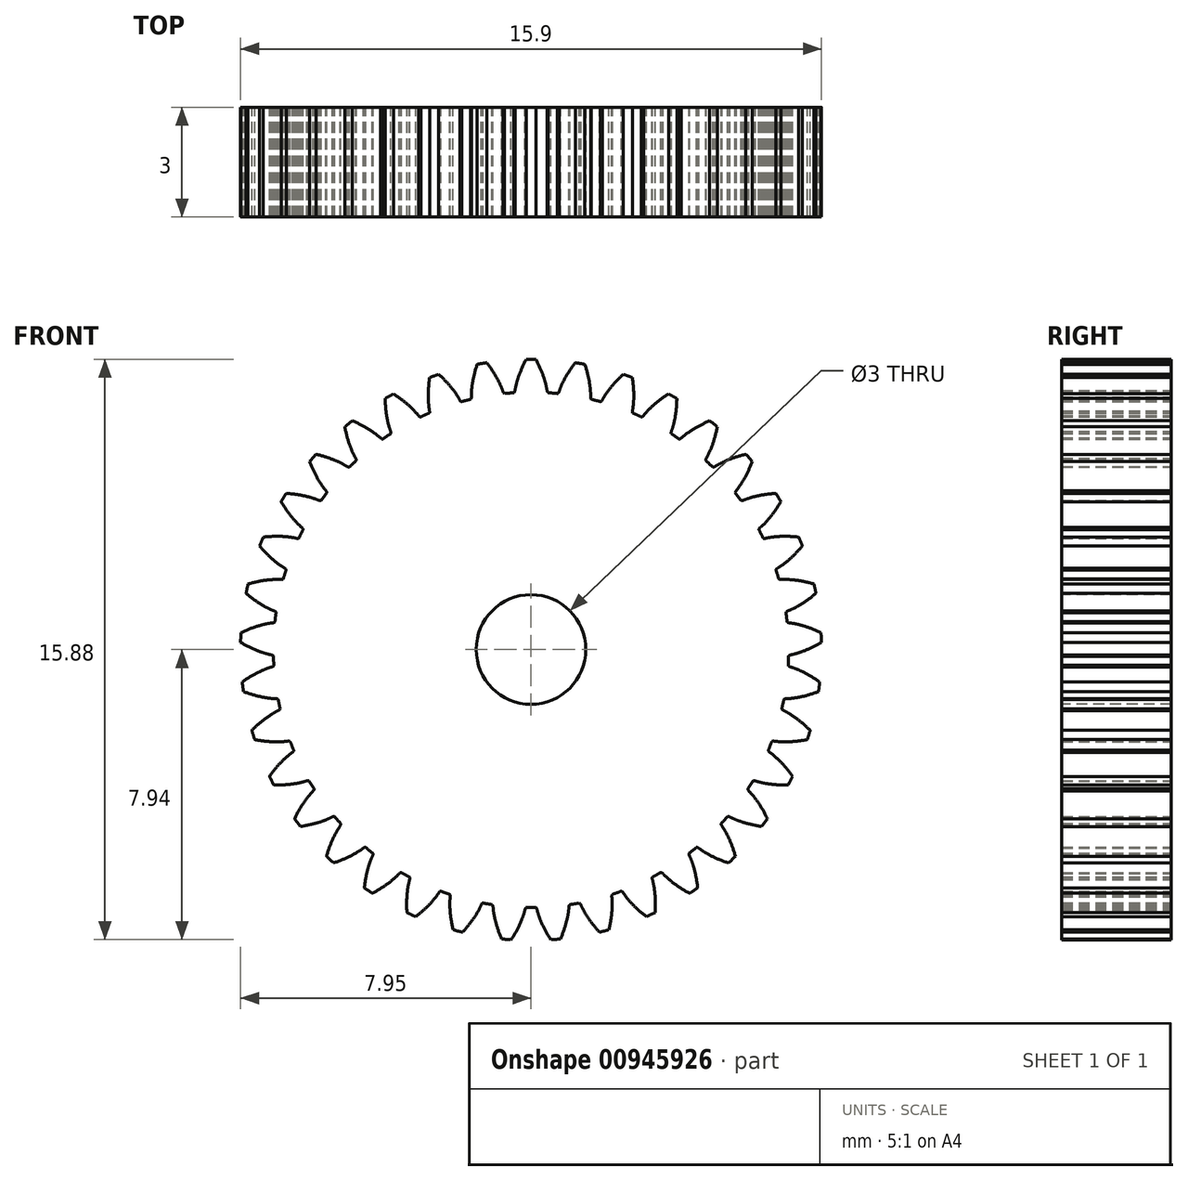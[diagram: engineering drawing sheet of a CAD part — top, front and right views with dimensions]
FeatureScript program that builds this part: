
annotation { "Feature Type Name" : "Feature", "Feature Type Description" : "" }
export const myFeature = defineFeature(function(context is Context, id is Id, definition is map)
    precondition{}
    {
        {
            var Q0;
            Q0=qCreatedBy(makeId("Front.planeOp"),FACE);
            var sketch = newSketch(context, id + "F0", { "sketchPlane" : qUnion([Q0])});
            skLineSegment(sketch, "E0", {"start": v(-0.47, 7.03) * mm, "end": v(-0.47, 7.03) * mm});
            skLineSegment(sketch, "E1", {"start": v(-0.47, 7.03) * mm, "end": v(-0.46, 7.03) * mm});
            skLineSegment(sketch, "E2", {"start": v(-0.46, 7.03) * mm, "end": v(-0.46, 7.04) * mm});
            skLineSegment(sketch, "E3", {"start": v(-0.46, 7.04) * mm, "end": v(-0.45, 7.05) * mm});
            skLineSegment(sketch, "E4", {"start": v(-0.45, 7.05) * mm, "end": v(-0.45, 7.06) * mm});
            skLineSegment(sketch, "E5", {"start": v(-0.45, 7.06) * mm, "end": v(-0.44, 7.07) * mm});
            skLineSegment(sketch, "E6", {"start": v(-0.44, 7.07) * mm, "end": v(-0.44, 7.09) * mm});
            skLineSegment(sketch, "E7", {"start": v(-0.44, 7.09) * mm, "end": v(-0.44, 7.1) * mm});
            skLineSegment(sketch, "E8", {"start": v(-0.44, 7.1) * mm, "end": v(-0.44, 7.1) * mm});
            skLineSegment(sketch, "E9", {"start": v(-0.44, 7.1) * mm, "end": v(-0.43, 7.12) * mm});
            skLineSegment(sketch, "E10", {"start": v(-0.43, 7.12) * mm, "end": v(-0.43, 7.13) * mm});
            skLineSegment(sketch, "E11", {"start": v(-0.43, 7.13) * mm, "end": v(-0.43, 7.15) * mm});
            skLineSegment(sketch, "E12", {"start": v(-0.43, 7.15) * mm, "end": v(-0.42, 7.16) * mm});
            skLineSegment(sketch, "E13", {"start": v(-0.42, 7.16) * mm, "end": v(-0.42, 7.18) * mm});
            skLineSegment(sketch, "E14", {"start": v(-0.42, 7.18) * mm, "end": v(-0.42, 7.2) * mm});
            skLineSegment(sketch, "E15", {"start": v(-0.42, 7.2) * mm, "end": v(-0.41, 7.21) * mm});
            skLineSegment(sketch, "E16", {"start": v(-0.41, 7.21) * mm, "end": v(-0.41, 7.23) * mm});
            skLineSegment(sketch, "E17", {"start": v(-0.41, 7.23) * mm, "end": v(-0.4, 7.25) * mm});
            skLineSegment(sketch, "E18", {"start": v(-0.4, 7.25) * mm, "end": v(-0.4, 7.27) * mm});
            skLineSegment(sketch, "E19", {"start": v(-0.4, 7.27) * mm, "end": v(-0.4, 7.28) * mm});
            skLineSegment(sketch, "E20", {"start": v(-0.4, 7.28) * mm, "end": v(-0.4, 7.3) * mm});
            skLineSegment(sketch, "E21", {"start": v(-0.4, 7.3) * mm, "end": v(-0.39, 7.32) * mm});
            skLineSegment(sketch, "E22", {"start": v(-0.39, 7.32) * mm, "end": v(-0.38, 7.34) * mm});
            skLineSegment(sketch, "E23", {"start": v(-0.38, 7.34) * mm, "end": v(-0.38, 7.36) * mm});
            skLineSegment(sketch, "E24", {"start": v(-0.38, 7.36) * mm, "end": v(-0.37, 7.38) * mm});
            skLineSegment(sketch, "E25", {"start": v(-0.37, 7.38) * mm, "end": v(-0.36, 7.4) * mm});
            skLineSegment(sketch, "E26", {"start": v(-0.36, 7.4) * mm, "end": v(-0.36, 7.43) * mm});
            skLineSegment(sketch, "E27", {"start": v(-0.36, 7.43) * mm, "end": v(-0.35, 7.45) * mm});
            skLineSegment(sketch, "E28", {"start": v(-0.35, 7.45) * mm, "end": v(-0.34, 7.47) * mm});
            skLineSegment(sketch, "E29", {"start": v(-0.34, 7.47) * mm, "end": v(-0.33, 7.5) * mm});
            skLineSegment(sketch, "E30", {"start": v(-0.33, 7.5) * mm, "end": v(-0.32, 7.52) * mm});
            skLineSegment(sketch, "E31", {"start": v(-0.32, 7.52) * mm, "end": v(-0.31, 7.54) * mm});
            skLineSegment(sketch, "E32", {"start": v(-0.31, 7.54) * mm, "end": v(-0.3, 7.56) * mm});
            skLineSegment(sketch, "E33", {"start": v(-0.3, 7.56) * mm, "end": v(-0.3, 7.59) * mm});
            skLineSegment(sketch, "E34", {"start": v(-0.3, 7.59) * mm, "end": v(-0.29, 7.61) * mm});
            skLineSegment(sketch, "E35", {"start": v(-0.29, 7.61) * mm, "end": v(-0.28, 7.64) * mm});
            skLineSegment(sketch, "E36", {"start": v(-0.28, 7.64) * mm, "end": v(-0.26, 7.66) * mm});
            skLineSegment(sketch, "E37", {"start": v(-0.26, 7.66) * mm, "end": v(-0.25, 7.7) * mm});
            skLineSegment(sketch, "E38", {"start": v(-0.25, 7.7) * mm, "end": v(-0.24, 7.72) * mm});
            skLineSegment(sketch, "E39", {"start": v(-0.24, 7.72) * mm, "end": v(-0.23, 7.74) * mm});
            skLineSegment(sketch, "E40", {"start": v(-0.23, 7.74) * mm, "end": v(-0.22, 7.77) * mm});
            skLineSegment(sketch, "E41", {"start": v(-0.22, 7.77) * mm, "end": v(-0.2, 7.8) * mm});
            skLineSegment(sketch, "E42", {"start": v(-0.2, 7.8) * mm, "end": v(-0.2, 7.83) * mm});
            skLineSegment(sketch, "E43", {"start": v(-0.2, 7.83) * mm, "end": v(-0.18, 7.85) * mm});
            skLineSegment(sketch, "E44", {"start": v(-0.18, 7.85) * mm, "end": v(-0.16, 7.88) * mm});
            skLineSegment(sketch, "E45", {"start": v(-0.16, 7.88) * mm, "end": v(-0.15, 7.91) * mm});
            skLineSegment(sketch, "E46", {"start": v(-0.15, 7.91) * mm, "end": v(-0.13, 7.94) * mm});
            skLineSegment(sketch, "E47", {"start": v(0.47, 7.03) * mm, "end": v(0.47, 7.03) * mm});
            skLineSegment(sketch, "E48", {"start": v(0.47, 7.03) * mm, "end": v(0.46, 7.03) * mm});
            skLineSegment(sketch, "E49", {"start": v(0.46, 7.03) * mm, "end": v(0.46, 7.04) * mm});
            skLineSegment(sketch, "E50", {"start": v(0.46, 7.04) * mm, "end": v(0.45, 7.05) * mm});
            skLineSegment(sketch, "E51", {"start": v(0.45, 7.05) * mm, "end": v(0.45, 7.06) * mm});
            skLineSegment(sketch, "E52", {"start": v(0.45, 7.06) * mm, "end": v(0.44, 7.07) * mm});
            skLineSegment(sketch, "E53", {"start": v(0.44, 7.07) * mm, "end": v(0.44, 7.09) * mm});
            skLineSegment(sketch, "E54", {"start": v(0.44, 7.09) * mm, "end": v(0.44, 7.1) * mm});
            skLineSegment(sketch, "E55", {"start": v(0.44, 7.1) * mm, "end": v(0.44, 7.1) * mm});
            skLineSegment(sketch, "E56", {"start": v(0.44, 7.1) * mm, "end": v(0.43, 7.12) * mm});
            skLineSegment(sketch, "E57", {"start": v(0.43, 7.12) * mm, "end": v(0.43, 7.13) * mm});
            skLineSegment(sketch, "E58", {"start": v(0.43, 7.13) * mm, "end": v(0.43, 7.15) * mm});
            skLineSegment(sketch, "E59", {"start": v(0.43, 7.15) * mm, "end": v(0.42, 7.16) * mm});
            skLineSegment(sketch, "E60", {"start": v(0.42, 7.16) * mm, "end": v(0.42, 7.18) * mm});
            skLineSegment(sketch, "E61", {"start": v(0.42, 7.18) * mm, "end": v(0.42, 7.2) * mm});
            skLineSegment(sketch, "E62", {"start": v(0.42, 7.2) * mm, "end": v(0.41, 7.21) * mm});
            skLineSegment(sketch, "E63", {"start": v(0.41, 7.21) * mm, "end": v(0.41, 7.23) * mm});
            skLineSegment(sketch, "E64", {"start": v(0.41, 7.23) * mm, "end": v(0.4, 7.25) * mm});
            skLineSegment(sketch, "E65", {"start": v(0.4, 7.25) * mm, "end": v(0.4, 7.27) * mm});
            skLineSegment(sketch, "E66", {"start": v(0.4, 7.27) * mm, "end": v(0.4, 7.28) * mm});
            skLineSegment(sketch, "E67", {"start": v(0.4, 7.28) * mm, "end": v(0.4, 7.3) * mm});
            skLineSegment(sketch, "E68", {"start": v(0.4, 7.3) * mm, "end": v(0.39, 7.32) * mm});
            skLineSegment(sketch, "E69", {"start": v(0.39, 7.32) * mm, "end": v(0.38, 7.34) * mm});
            skLineSegment(sketch, "E70", {"start": v(0.38, 7.34) * mm, "end": v(0.38, 7.36) * mm});
            skLineSegment(sketch, "E71", {"start": v(0.38, 7.36) * mm, "end": v(0.37, 7.38) * mm});
            skLineSegment(sketch, "E72", {"start": v(0.37, 7.38) * mm, "end": v(0.36, 7.4) * mm});
            skLineSegment(sketch, "E73", {"start": v(0.36, 7.4) * mm, "end": v(0.36, 7.43) * mm});
            skLineSegment(sketch, "E74", {"start": v(0.36, 7.43) * mm, "end": v(0.35, 7.45) * mm});
            skLineSegment(sketch, "E75", {"start": v(0.35, 7.45) * mm, "end": v(0.34, 7.47) * mm});
            skLineSegment(sketch, "E76", {"start": v(0.34, 7.47) * mm, "end": v(0.33, 7.5) * mm});
            skLineSegment(sketch, "E77", {"start": v(0.33, 7.5) * mm, "end": v(0.32, 7.52) * mm});
            skLineSegment(sketch, "E78", {"start": v(0.32, 7.52) * mm, "end": v(0.31, 7.54) * mm});
            skLineSegment(sketch, "E79", {"start": v(0.31, 7.54) * mm, "end": v(0.3, 7.56) * mm});
            skLineSegment(sketch, "E80", {"start": v(0.3, 7.56) * mm, "end": v(0.3, 7.59) * mm});
            skLineSegment(sketch, "E81", {"start": v(0.3, 7.59) * mm, "end": v(0.29, 7.61) * mm});
            skLineSegment(sketch, "E82", {"start": v(0.29, 7.61) * mm, "end": v(0.28, 7.64) * mm});
            skLineSegment(sketch, "E83", {"start": v(0.28, 7.64) * mm, "end": v(0.26, 7.66) * mm});
            skLineSegment(sketch, "E84", {"start": v(0.26, 7.66) * mm, "end": v(0.25, 7.7) * mm});
            skLineSegment(sketch, "E85", {"start": v(0.25, 7.7) * mm, "end": v(0.24, 7.72) * mm});
            skLineSegment(sketch, "E86", {"start": v(0.24, 7.72) * mm, "end": v(0.23, 7.74) * mm});
            skLineSegment(sketch, "E87", {"start": v(0.23, 7.74) * mm, "end": v(0.22, 7.77) * mm});
            skLineSegment(sketch, "E88", {"start": v(0.22, 7.77) * mm, "end": v(0.2, 7.8) * mm});
            skLineSegment(sketch, "E89", {"start": v(0.2, 7.8) * mm, "end": v(0.2, 7.83) * mm});
            skLineSegment(sketch, "E90", {"start": v(0.2, 7.83) * mm, "end": v(0.18, 7.85) * mm});
            skLineSegment(sketch, "E91", {"start": v(0.18, 7.85) * mm, "end": v(0.16, 7.88) * mm});
            skLineSegment(sketch, "E92", {"start": v(0.16, 7.88) * mm, "end": v(0.15, 7.91) * mm});
            skLineSegment(sketch, "E93", {"start": v(0.15, 7.91) * mm, "end": v(0.13, 7.94) * mm});
            skArc(sketch, "E94", {"start": v(0.13, 7.94) * mm, "mid": v(0, 7.94) * mm, "end": v(-0.13, 7.94) * mm});
            skLineSegment(sketch, "E95", {"start": v(0.72, 7) * mm, "end": v(0.73, 7) * mm});
            skLineSegment(sketch, "E96", {"start": v(0.73, 7) * mm, "end": v(0.74, 7) * mm});
            skLineSegment(sketch, "E97", {"start": v(0.74, 7) * mm, "end": v(0.74, 7.01) * mm});
            skLineSegment(sketch, "E98", {"start": v(0.74, 7.01) * mm, "end": v(0.75, 7.02) * mm});
            skLineSegment(sketch, "E99", {"start": v(0.75, 7.02) * mm, "end": v(0.76, 7.03) * mm});
            skLineSegment(sketch, "E100", {"start": v(0.76, 7.03) * mm, "end": v(0.76, 7.04) * mm});
            skLineSegment(sketch, "E101", {"start": v(0.76, 7.04) * mm, "end": v(0.77, 7.06) * mm});
            skLineSegment(sketch, "E102", {"start": v(0.77, 7.06) * mm, "end": v(0.77, 7.07) * mm});
            skLineSegment(sketch, "E103", {"start": v(0.77, 7.07) * mm, "end": v(0.77, 7.08) * mm});
            skLineSegment(sketch, "E104", {"start": v(0.77, 7.08) * mm, "end": v(0.78, 7.1) * mm});
            skLineSegment(sketch, "E105", {"start": v(0.78, 7.1) * mm, "end": v(0.78, 7.1) * mm});
            skLineSegment(sketch, "E106", {"start": v(0.78, 7.1) * mm, "end": v(0.79, 7.12) * mm});
            skLineSegment(sketch, "E107", {"start": v(0.79, 7.12) * mm, "end": v(0.8, 7.13) * mm});
            skLineSegment(sketch, "E108", {"start": v(0.8, 7.13) * mm, "end": v(0.8, 7.15) * mm});
            skLineSegment(sketch, "E109", {"start": v(0.8, 7.15) * mm, "end": v(0.8, 7.16) * mm});
            skLineSegment(sketch, "E110", {"start": v(0.8, 7.16) * mm, "end": v(0.81, 7.18) * mm});
            skLineSegment(sketch, "E111", {"start": v(0.81, 7.18) * mm, "end": v(0.82, 7.2) * mm});
            skLineSegment(sketch, "E112", {"start": v(0.82, 7.2) * mm, "end": v(0.83, 7.21) * mm});
            skLineSegment(sketch, "E113", {"start": v(0.83, 7.21) * mm, "end": v(0.83, 7.23) * mm});
            skLineSegment(sketch, "E114", {"start": v(0.83, 7.23) * mm, "end": v(0.84, 7.25) * mm});
            skLineSegment(sketch, "E115", {"start": v(0.84, 7.25) * mm, "end": v(0.85, 7.26) * mm});
            skLineSegment(sketch, "E116", {"start": v(0.85, 7.26) * mm, "end": v(0.86, 7.28) * mm});
            skLineSegment(sketch, "E117", {"start": v(0.86, 7.28) * mm, "end": v(0.87, 7.3) * mm});
            skLineSegment(sketch, "E118", {"start": v(0.87, 7.3) * mm, "end": v(0.88, 7.32) * mm});
            skLineSegment(sketch, "E119", {"start": v(0.88, 7.32) * mm, "end": v(0.89, 7.34) * mm});
            skLineSegment(sketch, "E120", {"start": v(0.89, 7.34) * mm, "end": v(0.9, 7.36) * mm});
            skLineSegment(sketch, "E121", {"start": v(0.9, 7.36) * mm, "end": v(0.9, 7.38) * mm});
            skLineSegment(sketch, "E122", {"start": v(0.9, 7.38) * mm, "end": v(0.92, 7.4) * mm});
            skLineSegment(sketch, "E123", {"start": v(0.92, 7.4) * mm, "end": v(0.93, 7.42) * mm});
            skLineSegment(sketch, "E124", {"start": v(0.93, 7.42) * mm, "end": v(0.94, 7.44) * mm});
            skLineSegment(sketch, "E125", {"start": v(0.94, 7.44) * mm, "end": v(0.95, 7.46) * mm});
            skLineSegment(sketch, "E126", {"start": v(0.95, 7.46) * mm, "end": v(0.97, 7.48) * mm});
            skLineSegment(sketch, "E127", {"start": v(0.97, 7.48) * mm, "end": v(0.98, 7.5) * mm});
            skLineSegment(sketch, "E128", {"start": v(0.98, 7.5) * mm, "end": v(1, 7.53) * mm});
            skLineSegment(sketch, "E129", {"start": v(1, 7.53) * mm, "end": v(1, 7.55) * mm});
            skLineSegment(sketch, "E130", {"start": v(1, 7.55) * mm, "end": v(1.02, 7.58) * mm});
            skLineSegment(sketch, "E131", {"start": v(1.02, 7.58) * mm, "end": v(1.04, 7.6) * mm});
            skLineSegment(sketch, "E132", {"start": v(1.04, 7.6) * mm, "end": v(1.05, 7.62) * mm});
            skLineSegment(sketch, "E133", {"start": v(1.05, 7.62) * mm, "end": v(1.07, 7.65) * mm});
            skLineSegment(sketch, "E134", {"start": v(1.07, 7.65) * mm, "end": v(1.08, 7.67) * mm});
            skLineSegment(sketch, "E135", {"start": v(1.08, 7.67) * mm, "end": v(1.1, 7.7) * mm});
            skLineSegment(sketch, "E136", {"start": v(1.1, 7.7) * mm, "end": v(1.12, 7.72) * mm});
            skLineSegment(sketch, "E137", {"start": v(1.12, 7.72) * mm, "end": v(1.14, 7.75) * mm});
            skLineSegment(sketch, "E138", {"start": v(1.14, 7.75) * mm, "end": v(1.15, 7.77) * mm});
            skLineSegment(sketch, "E139", {"start": v(1.15, 7.77) * mm, "end": v(1.17, 7.8) * mm});
            skLineSegment(sketch, "E140", {"start": v(1.17, 7.8) * mm, "end": v(1.2, 7.82) * mm});
            skLineSegment(sketch, "E141", {"start": v(1.2, 7.82) * mm, "end": v(1.21, 7.85) * mm});
            skLineSegment(sketch, "E142", {"start": v(1.65, 6.85) * mm, "end": v(1.65, 6.85) * mm});
            skLineSegment(sketch, "E143", {"start": v(1.65, 6.85) * mm, "end": v(1.64, 6.85) * mm});
            skLineSegment(sketch, "E144", {"start": v(1.64, 6.85) * mm, "end": v(1.64, 6.86) * mm});
            skLineSegment(sketch, "E145", {"start": v(1.64, 6.86) * mm, "end": v(1.64, 6.87) * mm});
            skLineSegment(sketch, "E146", {"start": v(1.64, 6.87) * mm, "end": v(1.63, 6.88) * mm});
            skLineSegment(sketch, "E147", {"start": v(1.63, 6.88) * mm, "end": v(1.63, 6.9) * mm});
            skLineSegment(sketch, "E148", {"start": v(1.63, 6.9) * mm, "end": v(1.63, 6.91) * mm});
            skLineSegment(sketch, "E149", {"start": v(1.63, 6.91) * mm, "end": v(1.63, 6.92) * mm});
            skLineSegment(sketch, "E150", {"start": v(1.63, 6.92) * mm, "end": v(1.63, 6.93) * mm});
            skLineSegment(sketch, "E151", {"start": v(1.63, 6.93) * mm, "end": v(1.63, 6.94) * mm});
            skLineSegment(sketch, "E152", {"start": v(1.63, 6.94) * mm, "end": v(1.63, 6.96) * mm});
            skLineSegment(sketch, "E153", {"start": v(1.63, 6.96) * mm, "end": v(1.63, 6.97) * mm});
            skLineSegment(sketch, "E154", {"start": v(1.63, 6.97) * mm, "end": v(1.63, 6.99) * mm});
            skLineSegment(sketch, "E155", {"start": v(1.63, 6.99) * mm, "end": v(1.63, 7) * mm});
            skLineSegment(sketch, "E156", {"start": v(1.63, 7) * mm, "end": v(1.63, 7.02) * mm});
            skLineSegment(sketch, "E157", {"start": v(1.63, 7.02) * mm, "end": v(1.63, 7.04) * mm});
            skLineSegment(sketch, "E158", {"start": v(1.63, 7.04) * mm, "end": v(1.63, 7.06) * mm});
            skLineSegment(sketch, "E159", {"start": v(1.63, 7.06) * mm, "end": v(1.63, 7.07) * mm});
            skLineSegment(sketch, "E160", {"start": v(1.63, 7.07) * mm, "end": v(1.63, 7.1) * mm});
            skLineSegment(sketch, "E161", {"start": v(1.63, 7.1) * mm, "end": v(1.62, 7.11) * mm});
            skLineSegment(sketch, "E162", {"start": v(1.62, 7.11) * mm, "end": v(1.62, 7.13) * mm});
            skLineSegment(sketch, "E163", {"start": v(1.62, 7.13) * mm, "end": v(1.62, 7.15) * mm});
            skLineSegment(sketch, "E164", {"start": v(1.62, 7.15) * mm, "end": v(1.62, 7.17) * mm});
            skLineSegment(sketch, "E165", {"start": v(1.62, 7.17) * mm, "end": v(1.62, 7.2) * mm});
            skLineSegment(sketch, "E166", {"start": v(1.62, 7.2) * mm, "end": v(1.61, 7.21) * mm});
            skLineSegment(sketch, "E167", {"start": v(1.61, 7.21) * mm, "end": v(1.6, 7.24) * mm});
            skLineSegment(sketch, "E168", {"start": v(1.6, 7.24) * mm, "end": v(1.6, 7.26) * mm});
            skLineSegment(sketch, "E169", {"start": v(1.6, 7.26) * mm, "end": v(1.6, 7.28) * mm});
            skLineSegment(sketch, "E170", {"start": v(1.6, 7.28) * mm, "end": v(1.6, 7.3) * mm});
            skLineSegment(sketch, "E171", {"start": v(1.6, 7.3) * mm, "end": v(1.6, 7.33) * mm});
            skLineSegment(sketch, "E172", {"start": v(1.6, 7.33) * mm, "end": v(1.6, 7.35) * mm});
            skLineSegment(sketch, "E173", {"start": v(1.6, 7.35) * mm, "end": v(1.59, 7.38) * mm});
            skLineSegment(sketch, "E174", {"start": v(1.59, 7.38) * mm, "end": v(1.58, 7.4) * mm});
            skLineSegment(sketch, "E175", {"start": v(1.58, 7.4) * mm, "end": v(1.58, 7.43) * mm});
            skLineSegment(sketch, "E176", {"start": v(1.58, 7.43) * mm, "end": v(1.57, 7.46) * mm});
            skLineSegment(sketch, "E177", {"start": v(1.57, 7.46) * mm, "end": v(1.56, 7.48) * mm});
            skLineSegment(sketch, "E178", {"start": v(1.56, 7.48) * mm, "end": v(1.56, 7.5) * mm});
            skLineSegment(sketch, "E179", {"start": v(1.56, 7.5) * mm, "end": v(1.55, 7.54) * mm});
            skLineSegment(sketch, "E180", {"start": v(1.55, 7.54) * mm, "end": v(1.54, 7.57) * mm});
            skLineSegment(sketch, "E181", {"start": v(1.54, 7.57) * mm, "end": v(1.54, 7.6) * mm});
            skLineSegment(sketch, "E182", {"start": v(1.54, 7.6) * mm, "end": v(1.53, 7.62) * mm});
            skLineSegment(sketch, "E183", {"start": v(1.53, 7.62) * mm, "end": v(1.52, 7.65) * mm});
            skLineSegment(sketch, "E184", {"start": v(1.52, 7.65) * mm, "end": v(1.51, 7.68) * mm});
            skLineSegment(sketch, "E185", {"start": v(1.51, 7.68) * mm, "end": v(1.5, 7.71) * mm});
            skLineSegment(sketch, "E186", {"start": v(1.5, 7.71) * mm, "end": v(1.5, 7.74) * mm});
            skLineSegment(sketch, "E187", {"start": v(1.5, 7.74) * mm, "end": v(1.48, 7.77) * mm});
            skLineSegment(sketch, "E188", {"start": v(1.48, 7.77) * mm, "end": v(1.47, 7.8) * mm});
            skArc(sketch, "E189", {"start": v(1.47, 7.8) * mm, "mid": v(1.34, 7.83) * mm, "end": v(1.21, 7.85) * mm});
            skLineSegment(sketch, "E190", {"start": v(1.9, 6.78) * mm, "end": v(1.9, 6.78) * mm});
            skLineSegment(sketch, "E191", {"start": v(1.9, 6.78) * mm, "end": v(1.91, 6.78) * mm});
            skLineSegment(sketch, "E192", {"start": v(1.91, 6.78) * mm, "end": v(1.92, 6.79) * mm});
            skLineSegment(sketch, "E193", {"start": v(1.92, 6.79) * mm, "end": v(1.93, 6.8) * mm});
            skLineSegment(sketch, "E194", {"start": v(1.93, 6.8) * mm, "end": v(1.93, 6.8) * mm});
            skLineSegment(sketch, "E195", {"start": v(1.93, 6.8) * mm, "end": v(1.94, 6.81) * mm});
            skLineSegment(sketch, "E196", {"start": v(1.94, 6.81) * mm, "end": v(1.95, 6.83) * mm});
            skLineSegment(sketch, "E197", {"start": v(1.95, 6.83) * mm, "end": v(1.95, 6.83) * mm});
            skLineSegment(sketch, "E198", {"start": v(1.95, 6.83) * mm, "end": v(1.96, 6.85) * mm});
            skLineSegment(sketch, "E199", {"start": v(1.96, 6.85) * mm, "end": v(1.97, 6.86) * mm});
            skLineSegment(sketch, "E200", {"start": v(1.97, 6.86) * mm, "end": v(1.97, 6.87) * mm});
            skLineSegment(sketch, "E201", {"start": v(1.97, 6.87) * mm, "end": v(1.98, 6.88) * mm});
            skLineSegment(sketch, "E202", {"start": v(1.98, 6.88) * mm, "end": v(1.99, 6.9) * mm});
            skLineSegment(sketch, "E203", {"start": v(1.99, 6.9) * mm, "end": v(2, 6.9) * mm});
            skLineSegment(sketch, "E204", {"start": v(2, 6.9) * mm, "end": v(2, 6.92) * mm});
            skLineSegment(sketch, "E205", {"start": v(2, 6.92) * mm, "end": v(2.02, 6.94) * mm});
            skLineSegment(sketch, "E206", {"start": v(2.02, 6.94) * mm, "end": v(2.02, 6.95) * mm});
            skLineSegment(sketch, "E207", {"start": v(2.02, 6.95) * mm, "end": v(2.03, 6.97) * mm});
            skLineSegment(sketch, "E208", {"start": v(2.03, 6.97) * mm, "end": v(2.04, 6.98) * mm});
            skLineSegment(sketch, "E209", {"start": v(2.04, 6.98) * mm, "end": v(2.06, 7) * mm});
            skLineSegment(sketch, "E210", {"start": v(2.06, 7) * mm, "end": v(2.07, 7.02) * mm});
            skLineSegment(sketch, "E211", {"start": v(2.07, 7.02) * mm, "end": v(2.08, 7.03) * mm});
            skLineSegment(sketch, "E212", {"start": v(2.08, 7.03) * mm, "end": v(2.09, 7.05) * mm});
            skLineSegment(sketch, "E213", {"start": v(2.09, 7.05) * mm, "end": v(2.1, 7.07) * mm});
            skLineSegment(sketch, "E214", {"start": v(2.1, 7.07) * mm, "end": v(2.11, 7.08) * mm});
            skLineSegment(sketch, "E215", {"start": v(2.11, 7.08) * mm, "end": v(2.13, 7.1) * mm});
            skLineSegment(sketch, "E216", {"start": v(2.13, 7.1) * mm, "end": v(2.14, 7.12) * mm});
            skLineSegment(sketch, "E217", {"start": v(2.14, 7.12) * mm, "end": v(2.16, 7.14) * mm});
            skLineSegment(sketch, "E218", {"start": v(2.16, 7.14) * mm, "end": v(2.17, 7.16) * mm});
            skLineSegment(sketch, "E219", {"start": v(2.17, 7.16) * mm, "end": v(2.19, 7.18) * mm});
            skLineSegment(sketch, "E220", {"start": v(2.19, 7.18) * mm, "end": v(2.2, 7.2) * mm});
            skLineSegment(sketch, "E221", {"start": v(2.2, 7.2) * mm, "end": v(2.22, 7.21) * mm});
            skLineSegment(sketch, "E222", {"start": v(2.22, 7.21) * mm, "end": v(2.23, 7.23) * mm});
            skLineSegment(sketch, "E223", {"start": v(2.23, 7.23) * mm, "end": v(2.25, 7.25) * mm});
            skLineSegment(sketch, "E224", {"start": v(2.25, 7.25) * mm, "end": v(2.27, 7.27) * mm});
            skLineSegment(sketch, "E225", {"start": v(2.27, 7.27) * mm, "end": v(2.29, 7.3) * mm});
            skLineSegment(sketch, "E226", {"start": v(2.29, 7.3) * mm, "end": v(2.3, 7.31) * mm});
            skLineSegment(sketch, "E227", {"start": v(2.3, 7.31) * mm, "end": v(2.33, 7.34) * mm});
            skLineSegment(sketch, "E228", {"start": v(2.33, 7.34) * mm, "end": v(2.35, 7.36) * mm});
            skLineSegment(sketch, "E229", {"start": v(2.35, 7.36) * mm, "end": v(2.37, 7.38) * mm});
            skLineSegment(sketch, "E230", {"start": v(2.37, 7.38) * mm, "end": v(2.39, 7.4) * mm});
            skLineSegment(sketch, "E231", {"start": v(2.39, 7.4) * mm, "end": v(2.4, 7.42) * mm});
            skLineSegment(sketch, "E232", {"start": v(2.4, 7.42) * mm, "end": v(2.43, 7.44) * mm});
            skLineSegment(sketch, "E233", {"start": v(2.43, 7.44) * mm, "end": v(2.45, 7.46) * mm});
            skLineSegment(sketch, "E234", {"start": v(2.45, 7.46) * mm, "end": v(2.48, 7.49) * mm});
            skLineSegment(sketch, "E235", {"start": v(2.48, 7.49) * mm, "end": v(2.5, 7.5) * mm});
            skLineSegment(sketch, "E236", {"start": v(2.5, 7.5) * mm, "end": v(2.52, 7.53) * mm});
            skLineSegment(sketch, "E237", {"start": v(2.79, 6.47) * mm, "end": v(2.78, 6.47) * mm});
            skLineSegment(sketch, "E238", {"start": v(2.78, 6.47) * mm, "end": v(2.78, 6.48) * mm});
            skLineSegment(sketch, "E239", {"start": v(2.78, 6.48) * mm, "end": v(2.78, 6.48) * mm});
            skLineSegment(sketch, "E240", {"start": v(2.78, 6.48) * mm, "end": v(2.78, 6.5) * mm});
            skLineSegment(sketch, "E241", {"start": v(2.78, 6.5) * mm, "end": v(2.77, 6.5) * mm});
            skLineSegment(sketch, "E242", {"start": v(2.77, 6.5) * mm, "end": v(2.78, 6.52) * mm});
            skLineSegment(sketch, "E243", {"start": v(2.78, 6.52) * mm, "end": v(2.78, 6.54) * mm});
            skLineSegment(sketch, "E244", {"start": v(2.78, 6.54) * mm, "end": v(2.78, 6.54) * mm});
            skLineSegment(sketch, "E245", {"start": v(2.78, 6.54) * mm, "end": v(2.78, 6.56) * mm});
            skLineSegment(sketch, "E246", {"start": v(2.78, 6.56) * mm, "end": v(2.78, 6.57) * mm});
            skLineSegment(sketch, "E247", {"start": v(2.78, 6.57) * mm, "end": v(2.79, 6.58) * mm});
            skLineSegment(sketch, "E248", {"start": v(2.79, 6.58) * mm, "end": v(2.79, 6.6) * mm});
            skLineSegment(sketch, "E249", {"start": v(2.79, 6.6) * mm, "end": v(2.8, 6.61) * mm});
            skLineSegment(sketch, "E250", {"start": v(2.8, 6.61) * mm, "end": v(2.8, 6.63) * mm});
            skLineSegment(sketch, "E251", {"start": v(2.8, 6.63) * mm, "end": v(2.8, 6.65) * mm});
            skLineSegment(sketch, "E252", {"start": v(2.8, 6.65) * mm, "end": v(2.8, 6.66) * mm});
            skLineSegment(sketch, "E253", {"start": v(2.8, 6.66) * mm, "end": v(2.8, 6.68) * mm});
            skLineSegment(sketch, "E254", {"start": v(2.8, 6.68) * mm, "end": v(2.8, 6.7) * mm});
            skLineSegment(sketch, "E255", {"start": v(2.8, 6.7) * mm, "end": v(2.8, 6.72) * mm});
            skLineSegment(sketch, "E256", {"start": v(2.8, 6.72) * mm, "end": v(2.8, 6.73) * mm});
            skLineSegment(sketch, "E257", {"start": v(2.8, 6.73) * mm, "end": v(2.8, 6.75) * mm});
            skLineSegment(sketch, "E258", {"start": v(2.8, 6.75) * mm, "end": v(2.8, 6.77) * mm});
            skLineSegment(sketch, "E259", {"start": v(2.8, 6.77) * mm, "end": v(2.8, 6.8) * mm});
            skLineSegment(sketch, "E260", {"start": v(2.8, 6.8) * mm, "end": v(2.8, 6.82) * mm});
            skLineSegment(sketch, "E261", {"start": v(2.8, 6.82) * mm, "end": v(2.81, 6.84) * mm});
            skLineSegment(sketch, "E262", {"start": v(2.81, 6.84) * mm, "end": v(2.81, 6.86) * mm});
            skLineSegment(sketch, "E263", {"start": v(2.81, 6.86) * mm, "end": v(2.81, 6.88) * mm});
            skLineSegment(sketch, "E264", {"start": v(2.81, 6.88) * mm, "end": v(2.81, 6.9) * mm});
            skLineSegment(sketch, "E265", {"start": v(2.81, 6.9) * mm, "end": v(2.81, 6.93) * mm});
            skLineSegment(sketch, "E266", {"start": v(2.81, 6.93) * mm, "end": v(2.81, 6.95) * mm});
            skLineSegment(sketch, "E267", {"start": v(2.81, 6.95) * mm, "end": v(2.81, 6.98) * mm});
            skLineSegment(sketch, "E268", {"start": v(2.81, 6.98) * mm, "end": v(2.81, 7) * mm});
            skLineSegment(sketch, "E269", {"start": v(2.81, 7) * mm, "end": v(2.81, 7.03) * mm});
            skLineSegment(sketch, "E270", {"start": v(2.81, 7.03) * mm, "end": v(2.81, 7.06) * mm});
            skLineSegment(sketch, "E271", {"start": v(2.81, 7.06) * mm, "end": v(2.8, 7.08) * mm});
            skLineSegment(sketch, "E272", {"start": v(2.8, 7.08) * mm, "end": v(2.8, 7.11) * mm});
            skLineSegment(sketch, "E273", {"start": v(2.8, 7.11) * mm, "end": v(2.8, 7.14) * mm});
            skLineSegment(sketch, "E274", {"start": v(2.8, 7.14) * mm, "end": v(2.8, 7.17) * mm});
            skLineSegment(sketch, "E275", {"start": v(2.8, 7.17) * mm, "end": v(2.8, 7.2) * mm});
            skLineSegment(sketch, "E276", {"start": v(2.8, 7.2) * mm, "end": v(2.8, 7.22) * mm});
            skLineSegment(sketch, "E277", {"start": v(2.8, 7.22) * mm, "end": v(2.8, 7.25) * mm});
            skLineSegment(sketch, "E278", {"start": v(2.8, 7.25) * mm, "end": v(2.8, 7.28) * mm});
            skLineSegment(sketch, "E279", {"start": v(2.8, 7.28) * mm, "end": v(2.8, 7.32) * mm});
            skLineSegment(sketch, "E280", {"start": v(2.8, 7.32) * mm, "end": v(2.79, 7.35) * mm});
            skLineSegment(sketch, "E281", {"start": v(2.79, 7.35) * mm, "end": v(2.78, 7.38) * mm});
            skLineSegment(sketch, "E282", {"start": v(2.78, 7.38) * mm, "end": v(2.78, 7.41) * mm});
            skLineSegment(sketch, "E283", {"start": v(2.78, 7.41) * mm, "end": v(2.77, 7.44) * mm});
            skArc(sketch, "E284", {"start": v(2.77, 7.44) * mm, "mid": v(2.65, 7.49) * mm, "end": v(2.52, 7.53) * mm});
            skLineSegment(sketch, "E285", {"start": v(3.02, 6.36) * mm, "end": v(3.03, 6.36) * mm});
            skLineSegment(sketch, "E286", {"start": v(3.03, 6.36) * mm, "end": v(3.03, 6.36) * mm});
            skLineSegment(sketch, "E287", {"start": v(3.03, 6.36) * mm, "end": v(3.04, 6.37) * mm});
            skLineSegment(sketch, "E288", {"start": v(3.04, 6.37) * mm, "end": v(3.05, 6.37) * mm});
            skLineSegment(sketch, "E289", {"start": v(3.05, 6.37) * mm, "end": v(3.06, 6.38) * mm});
            skLineSegment(sketch, "E290", {"start": v(3.06, 6.38) * mm, "end": v(3.07, 6.39) * mm});
            skLineSegment(sketch, "E291", {"start": v(3.07, 6.39) * mm, "end": v(3.08, 6.4) * mm});
            skLineSegment(sketch, "E292", {"start": v(3.08, 6.4) * mm, "end": v(3.08, 6.4) * mm});
            skLineSegment(sketch, "E293", {"start": v(3.08, 6.4) * mm, "end": v(3.1, 6.42) * mm});
            skLineSegment(sketch, "E294", {"start": v(3.1, 6.42) * mm, "end": v(3.1, 6.43) * mm});
            skLineSegment(sketch, "E295", {"start": v(3.1, 6.43) * mm, "end": v(3.1, 6.44) * mm});
            skLineSegment(sketch, "E296", {"start": v(3.1, 6.44) * mm, "end": v(3.12, 6.45) * mm});
            skLineSegment(sketch, "E297", {"start": v(3.12, 6.45) * mm, "end": v(3.13, 6.46) * mm});
            skLineSegment(sketch, "E298", {"start": v(3.13, 6.46) * mm, "end": v(3.14, 6.47) * mm});
            skLineSegment(sketch, "E299", {"start": v(3.14, 6.47) * mm, "end": v(3.15, 6.49) * mm});
            skLineSegment(sketch, "E300", {"start": v(3.15, 6.49) * mm, "end": v(3.16, 6.5) * mm});
            skLineSegment(sketch, "E301", {"start": v(3.16, 6.5) * mm, "end": v(3.17, 6.51) * mm});
            skLineSegment(sketch, "E302", {"start": v(3.17, 6.51) * mm, "end": v(3.18, 6.52) * mm});
            skLineSegment(sketch, "E303", {"start": v(3.18, 6.52) * mm, "end": v(3.2, 6.54) * mm});
            skLineSegment(sketch, "E304", {"start": v(3.2, 6.54) * mm, "end": v(3.21, 6.55) * mm});
            skLineSegment(sketch, "E305", {"start": v(3.21, 6.55) * mm, "end": v(3.22, 6.57) * mm});
            skLineSegment(sketch, "E306", {"start": v(3.22, 6.57) * mm, "end": v(3.24, 6.58) * mm});
            skLineSegment(sketch, "E307", {"start": v(3.24, 6.58) * mm, "end": v(3.25, 6.6) * mm});
            skLineSegment(sketch, "E308", {"start": v(3.25, 6.6) * mm, "end": v(3.27, 6.6) * mm});
            skLineSegment(sketch, "E309", {"start": v(3.27, 6.6) * mm, "end": v(3.28, 6.62) * mm});
            skLineSegment(sketch, "E310", {"start": v(3.28, 6.62) * mm, "end": v(3.3, 6.64) * mm});
            skLineSegment(sketch, "E311", {"start": v(3.3, 6.64) * mm, "end": v(3.32, 6.65) * mm});
            skLineSegment(sketch, "E312", {"start": v(3.32, 6.65) * mm, "end": v(3.33, 6.67) * mm});
            skLineSegment(sketch, "E313", {"start": v(3.33, 6.67) * mm, "end": v(3.35, 6.69) * mm});
            skLineSegment(sketch, "E314", {"start": v(3.35, 6.69) * mm, "end": v(3.37, 6.7) * mm});
            skLineSegment(sketch, "E315", {"start": v(3.37, 6.7) * mm, "end": v(3.39, 6.72) * mm});
            skLineSegment(sketch, "E316", {"start": v(3.39, 6.72) * mm, "end": v(3.4, 6.73) * mm});
            skLineSegment(sketch, "E317", {"start": v(3.4, 6.73) * mm, "end": v(3.43, 6.75) * mm});
            skLineSegment(sketch, "E318", {"start": v(3.43, 6.75) * mm, "end": v(3.45, 6.77) * mm});
            skLineSegment(sketch, "E319", {"start": v(3.45, 6.77) * mm, "end": v(3.47, 6.79) * mm});
            skLineSegment(sketch, "E320", {"start": v(3.47, 6.79) * mm, "end": v(3.49, 6.8) * mm});
            skLineSegment(sketch, "E321", {"start": v(3.49, 6.8) * mm, "end": v(3.51, 6.82) * mm});
            skLineSegment(sketch, "E322", {"start": v(3.51, 6.82) * mm, "end": v(3.53, 6.84) * mm});
            skLineSegment(sketch, "E323", {"start": v(3.53, 6.84) * mm, "end": v(3.56, 6.85) * mm});
            skLineSegment(sketch, "E324", {"start": v(3.56, 6.85) * mm, "end": v(3.58, 6.87) * mm});
            skLineSegment(sketch, "E325", {"start": v(3.58, 6.87) * mm, "end": v(3.6, 6.89) * mm});
            skLineSegment(sketch, "E326", {"start": v(3.6, 6.89) * mm, "end": v(3.63, 6.9) * mm});
            skLineSegment(sketch, "E327", {"start": v(3.63, 6.9) * mm, "end": v(3.66, 6.92) * mm});
            skLineSegment(sketch, "E328", {"start": v(3.66, 6.92) * mm, "end": v(3.68, 6.94) * mm});
            skLineSegment(sketch, "E329", {"start": v(3.68, 6.94) * mm, "end": v(3.7, 6.96) * mm});
            skLineSegment(sketch, "E330", {"start": v(3.7, 6.96) * mm, "end": v(3.73, 6.98) * mm});
            skLineSegment(sketch, "E331", {"start": v(3.73, 6.98) * mm, "end": v(3.76, 7) * mm});
            skLineSegment(sketch, "E332", {"start": v(3.84, 5.9) * mm, "end": v(3.84, 5.9) * mm});
            skLineSegment(sketch, "E333", {"start": v(3.84, 5.9) * mm, "end": v(3.84, 5.91) * mm});
            skLineSegment(sketch, "E334", {"start": v(3.84, 5.91) * mm, "end": v(3.83, 5.92) * mm});
            skLineSegment(sketch, "E335", {"start": v(3.83, 5.92) * mm, "end": v(3.83, 5.93) * mm});
            skLineSegment(sketch, "E336", {"start": v(3.83, 5.93) * mm, "end": v(3.84, 5.94) * mm});
            skLineSegment(sketch, "E337", {"start": v(3.84, 5.94) * mm, "end": v(3.84, 5.96) * mm});
            skLineSegment(sketch, "E338", {"start": v(3.84, 5.96) * mm, "end": v(3.84, 5.97) * mm});
            skLineSegment(sketch, "E339", {"start": v(3.84, 5.97) * mm, "end": v(3.85, 5.98) * mm});
            skLineSegment(sketch, "E340", {"start": v(3.85, 5.98) * mm, "end": v(3.85, 6) * mm});
            skLineSegment(sketch, "E341", {"start": v(3.85, 6) * mm, "end": v(3.86, 6) * mm});
            skLineSegment(sketch, "E342", {"start": v(3.86, 6) * mm, "end": v(3.86, 6.02) * mm});
            skLineSegment(sketch, "E343", {"start": v(3.86, 6.02) * mm, "end": v(3.86, 6.03) * mm});
            skLineSegment(sketch, "E344", {"start": v(3.86, 6.03) * mm, "end": v(3.87, 6.05) * mm});
            skLineSegment(sketch, "E345", {"start": v(3.87, 6.05) * mm, "end": v(3.87, 6.06) * mm});
            skLineSegment(sketch, "E346", {"start": v(3.87, 6.06) * mm, "end": v(3.88, 6.08) * mm});
            skLineSegment(sketch, "E347", {"start": v(3.88, 6.08) * mm, "end": v(3.88, 6.1) * mm});
            skLineSegment(sketch, "E348", {"start": v(3.88, 6.1) * mm, "end": v(3.89, 6.11) * mm});
            skLineSegment(sketch, "E349", {"start": v(3.89, 6.11) * mm, "end": v(3.9, 6.13) * mm});
            skLineSegment(sketch, "E350", {"start": v(3.9, 6.13) * mm, "end": v(3.9, 6.15) * mm});
            skLineSegment(sketch, "E351", {"start": v(3.9, 6.15) * mm, "end": v(3.9, 6.16) * mm});
            skLineSegment(sketch, "E352", {"start": v(3.9, 6.16) * mm, "end": v(3.9, 6.18) * mm});
            skLineSegment(sketch, "E353", {"start": v(3.9, 6.18) * mm, "end": v(3.91, 6.2) * mm});
            skLineSegment(sketch, "E354", {"start": v(3.91, 6.2) * mm, "end": v(3.92, 6.22) * mm});
            skLineSegment(sketch, "E355", {"start": v(3.92, 6.22) * mm, "end": v(3.92, 6.24) * mm});
            skLineSegment(sketch, "E356", {"start": v(3.92, 6.24) * mm, "end": v(3.93, 6.26) * mm});
            skLineSegment(sketch, "E357", {"start": v(3.93, 6.26) * mm, "end": v(3.93, 6.29) * mm});
            skLineSegment(sketch, "E358", {"start": v(3.93, 6.29) * mm, "end": v(3.94, 6.3) * mm});
            skLineSegment(sketch, "E359", {"start": v(3.94, 6.3) * mm, "end": v(3.94, 6.33) * mm});
            skLineSegment(sketch, "E360", {"start": v(3.94, 6.33) * mm, "end": v(3.94, 6.35) * mm});
            skLineSegment(sketch, "E361", {"start": v(3.94, 6.35) * mm, "end": v(3.95, 6.38) * mm});
            skLineSegment(sketch, "E362", {"start": v(3.95, 6.38) * mm, "end": v(3.95, 6.4) * mm});
            skLineSegment(sketch, "E363", {"start": v(3.95, 6.4) * mm, "end": v(3.96, 6.43) * mm});
            skLineSegment(sketch, "E364", {"start": v(3.96, 6.43) * mm, "end": v(3.96, 6.45) * mm});
            skLineSegment(sketch, "E365", {"start": v(3.96, 6.45) * mm, "end": v(3.96, 6.48) * mm});
            skLineSegment(sketch, "E366", {"start": v(3.96, 6.48) * mm, "end": v(3.97, 6.5) * mm});
            skLineSegment(sketch, "E367", {"start": v(3.97, 6.5) * mm, "end": v(3.97, 6.53) * mm});
            skLineSegment(sketch, "E368", {"start": v(3.97, 6.53) * mm, "end": v(3.97, 6.56) * mm});
            skLineSegment(sketch, "E369", {"start": v(3.97, 6.56) * mm, "end": v(3.98, 6.59) * mm});
            skLineSegment(sketch, "E370", {"start": v(3.98, 6.59) * mm, "end": v(3.98, 6.62) * mm});
            skLineSegment(sketch, "E371", {"start": v(3.98, 6.62) * mm, "end": v(3.98, 6.65) * mm});
            skLineSegment(sketch, "E372", {"start": v(3.98, 6.65) * mm, "end": v(3.98, 6.68) * mm});
            skLineSegment(sketch, "E373", {"start": v(3.98, 6.68) * mm, "end": v(3.99, 6.7) * mm});
            skLineSegment(sketch, "E374", {"start": v(3.99, 6.7) * mm, "end": v(3.99, 6.74) * mm});
            skLineSegment(sketch, "E375", {"start": v(3.99, 6.74) * mm, "end": v(3.99, 6.77) * mm});
            skLineSegment(sketch, "E376", {"start": v(3.99, 6.77) * mm, "end": v(4, 6.8) * mm});
            skLineSegment(sketch, "E377", {"start": v(4, 6.8) * mm, "end": v(4, 6.83) * mm});
            skLineSegment(sketch, "E378", {"start": v(4, 6.83) * mm, "end": v(4, 6.87) * mm});
            skArc(sketch, "E379", {"start": v(4, 6.87) * mm, "mid": v(3.88, 6.93) * mm, "end": v(3.76, 7) * mm});
            skLineSegment(sketch, "E380", {"start": v(4.05, 5.76) * mm, "end": v(4.06, 5.76) * mm});
            skLineSegment(sketch, "E381", {"start": v(4.06, 5.76) * mm, "end": v(4.07, 5.76) * mm});
            skLineSegment(sketch, "E382", {"start": v(4.07, 5.76) * mm, "end": v(4.07, 5.76) * mm});
            skLineSegment(sketch, "E383", {"start": v(4.07, 5.76) * mm, "end": v(4.08, 5.76) * mm});
            skLineSegment(sketch, "E384", {"start": v(4.08, 5.76) * mm, "end": v(4.1, 5.77) * mm});
            skLineSegment(sketch, "E385", {"start": v(4.1, 5.77) * mm, "end": v(4.1, 5.78) * mm});
            skLineSegment(sketch, "E386", {"start": v(4.1, 5.78) * mm, "end": v(4.12, 5.79) * mm});
            skLineSegment(sketch, "E387", {"start": v(4.12, 5.79) * mm, "end": v(4.12, 5.8) * mm});
            skLineSegment(sketch, "E388", {"start": v(4.12, 5.8) * mm, "end": v(4.13, 5.8) * mm});
            skLineSegment(sketch, "E389", {"start": v(4.13, 5.8) * mm, "end": v(4.14, 5.81) * mm});
            skLineSegment(sketch, "E390", {"start": v(4.14, 5.81) * mm, "end": v(4.15, 5.82) * mm});
            skLineSegment(sketch, "E391", {"start": v(4.15, 5.82) * mm, "end": v(4.16, 5.83) * mm});
            skLineSegment(sketch, "E392", {"start": v(4.16, 5.83) * mm, "end": v(4.18, 5.84) * mm});
            skLineSegment(sketch, "E393", {"start": v(4.18, 5.84) * mm, "end": v(4.19, 5.85) * mm});
            skLineSegment(sketch, "E394", {"start": v(4.19, 5.85) * mm, "end": v(4.2, 5.86) * mm});
            skLineSegment(sketch, "E395", {"start": v(4.2, 5.86) * mm, "end": v(4.21, 5.87) * mm});
            skLineSegment(sketch, "E396", {"start": v(4.21, 5.87) * mm, "end": v(4.23, 5.88) * mm});
            skLineSegment(sketch, "E397", {"start": v(4.23, 5.88) * mm, "end": v(4.24, 5.9) * mm});
            skLineSegment(sketch, "E398", {"start": v(4.24, 5.9) * mm, "end": v(4.26, 5.9) * mm});
            skLineSegment(sketch, "E399", {"start": v(4.26, 5.9) * mm, "end": v(4.27, 5.91) * mm});
            skLineSegment(sketch, "E400", {"start": v(4.27, 5.91) * mm, "end": v(4.29, 5.93) * mm});
            skLineSegment(sketch, "E401", {"start": v(4.29, 5.93) * mm, "end": v(4.3, 5.94) * mm});
            skLineSegment(sketch, "E402", {"start": v(4.3, 5.94) * mm, "end": v(4.32, 5.95) * mm});
            skLineSegment(sketch, "E403", {"start": v(4.32, 5.95) * mm, "end": v(4.34, 5.96) * mm});
            skLineSegment(sketch, "E404", {"start": v(4.34, 5.96) * mm, "end": v(4.36, 5.97) * mm});
            skLineSegment(sketch, "E405", {"start": v(4.36, 5.97) * mm, "end": v(4.38, 5.99) * mm});
            skLineSegment(sketch, "E406", {"start": v(4.38, 5.99) * mm, "end": v(4.4, 6) * mm});
            skLineSegment(sketch, "E407", {"start": v(4.4, 6) * mm, "end": v(4.41, 6.01) * mm});
            skLineSegment(sketch, "E408", {"start": v(4.41, 6.01) * mm, "end": v(4.43, 6.02) * mm});
            skLineSegment(sketch, "E409", {"start": v(4.43, 6.02) * mm, "end": v(4.45, 6.04) * mm});
            skLineSegment(sketch, "E410", {"start": v(4.45, 6.04) * mm, "end": v(4.48, 6.05) * mm});
            skLineSegment(sketch, "E411", {"start": v(4.48, 6.05) * mm, "end": v(4.5, 6.06) * mm});
            skLineSegment(sketch, "E412", {"start": v(4.5, 6.06) * mm, "end": v(4.52, 6.08) * mm});
            skLineSegment(sketch, "E413", {"start": v(4.52, 6.08) * mm, "end": v(4.54, 6.09) * mm});
            skLineSegment(sketch, "E414", {"start": v(4.54, 6.09) * mm, "end": v(4.57, 6.1) * mm});
            skLineSegment(sketch, "E415", {"start": v(4.57, 6.1) * mm, "end": v(4.6, 6.11) * mm});
            skLineSegment(sketch, "E416", {"start": v(4.6, 6.11) * mm, "end": v(4.61, 6.13) * mm});
            skLineSegment(sketch, "E417", {"start": v(4.61, 6.13) * mm, "end": v(4.64, 6.14) * mm});
            skLineSegment(sketch, "E418", {"start": v(4.64, 6.14) * mm, "end": v(4.67, 6.15) * mm});
            skLineSegment(sketch, "E419", {"start": v(4.67, 6.15) * mm, "end": v(4.7, 6.17) * mm});
            skLineSegment(sketch, "E420", {"start": v(4.7, 6.17) * mm, "end": v(4.72, 6.18) * mm});
            skLineSegment(sketch, "E421", {"start": v(4.72, 6.18) * mm, "end": v(4.75, 6.2) * mm});
            skLineSegment(sketch, "E422", {"start": v(4.75, 6.2) * mm, "end": v(4.77, 6.2) * mm});
            skLineSegment(sketch, "E423", {"start": v(4.77, 6.2) * mm, "end": v(4.8, 6.22) * mm});
            skLineSegment(sketch, "E424", {"start": v(4.8, 6.22) * mm, "end": v(4.83, 6.23) * mm});
            skLineSegment(sketch, "E425", {"start": v(4.83, 6.23) * mm, "end": v(4.86, 6.25) * mm});
            skLineSegment(sketch, "E426", {"start": v(4.86, 6.25) * mm, "end": v(4.9, 6.26) * mm});
            skLineSegment(sketch, "E427", {"start": v(4.79, 5.17) * mm, "end": v(4.78, 5.17) * mm});
            skLineSegment(sketch, "E428", {"start": v(4.78, 5.17) * mm, "end": v(4.78, 5.18) * mm});
            skLineSegment(sketch, "E429", {"start": v(4.78, 5.18) * mm, "end": v(4.78, 5.19) * mm});
            skLineSegment(sketch, "E430", {"start": v(4.78, 5.19) * mm, "end": v(4.78, 5.2) * mm});
            skLineSegment(sketch, "E431", {"start": v(4.78, 5.2) * mm, "end": v(4.79, 5.2) * mm});
            skLineSegment(sketch, "E432", {"start": v(4.79, 5.2) * mm, "end": v(4.8, 5.22) * mm});
            skLineSegment(sketch, "E433", {"start": v(4.8, 5.22) * mm, "end": v(4.8, 5.24) * mm});
            skLineSegment(sketch, "E434", {"start": v(4.8, 5.24) * mm, "end": v(4.8, 5.24) * mm});
            skLineSegment(sketch, "E435", {"start": v(4.8, 5.24) * mm, "end": v(4.8, 5.25) * mm});
            skLineSegment(sketch, "E436", {"start": v(4.8, 5.25) * mm, "end": v(4.82, 5.27) * mm});
            skLineSegment(sketch, "E437", {"start": v(4.82, 5.27) * mm, "end": v(4.82, 5.28) * mm});
            skLineSegment(sketch, "E438", {"start": v(4.82, 5.28) * mm, "end": v(4.83, 5.3) * mm});
            skLineSegment(sketch, "E439", {"start": v(4.83, 5.3) * mm, "end": v(4.84, 5.3) * mm});
            skLineSegment(sketch, "E440", {"start": v(4.84, 5.3) * mm, "end": v(4.84, 5.32) * mm});
            skLineSegment(sketch, "E441", {"start": v(4.84, 5.32) * mm, "end": v(4.85, 5.33) * mm});
            skLineSegment(sketch, "E442", {"start": v(4.85, 5.33) * mm, "end": v(4.86, 5.35) * mm});
            skLineSegment(sketch, "E443", {"start": v(4.86, 5.35) * mm, "end": v(4.87, 5.37) * mm});
            skLineSegment(sketch, "E444", {"start": v(4.87, 5.37) * mm, "end": v(4.88, 5.38) * mm});
            skLineSegment(sketch, "E445", {"start": v(4.88, 5.38) * mm, "end": v(4.88, 5.4) * mm});
            skLineSegment(sketch, "E446", {"start": v(4.88, 5.4) * mm, "end": v(4.9, 5.42) * mm});
            skLineSegment(sketch, "E447", {"start": v(4.9, 5.42) * mm, "end": v(4.9, 5.43) * mm});
            skLineSegment(sketch, "E448", {"start": v(4.9, 5.43) * mm, "end": v(4.9, 5.45) * mm});
            skLineSegment(sketch, "E449", {"start": v(4.9, 5.45) * mm, "end": v(4.91, 5.47) * mm});
            skLineSegment(sketch, "E450", {"start": v(4.91, 5.47) * mm, "end": v(4.92, 5.5) * mm});
            skLineSegment(sketch, "E451", {"start": v(4.92, 5.5) * mm, "end": v(4.93, 5.51) * mm});
            skLineSegment(sketch, "E452", {"start": v(4.93, 5.51) * mm, "end": v(4.94, 5.53) * mm});
            skLineSegment(sketch, "E453", {"start": v(4.94, 5.53) * mm, "end": v(4.95, 5.55) * mm});
            skLineSegment(sketch, "E454", {"start": v(4.95, 5.55) * mm, "end": v(4.96, 5.57) * mm});
            skLineSegment(sketch, "E455", {"start": v(4.96, 5.57) * mm, "end": v(4.96, 5.6) * mm});
            skLineSegment(sketch, "E456", {"start": v(4.96, 5.6) * mm, "end": v(4.97, 5.62) * mm});
            skLineSegment(sketch, "E457", {"start": v(4.97, 5.62) * mm, "end": v(4.98, 5.64) * mm});
            skLineSegment(sketch, "E458", {"start": v(4.98, 5.64) * mm, "end": v(4.99, 5.67) * mm});
            skLineSegment(sketch, "E459", {"start": v(4.99, 5.67) * mm, "end": v(5, 5.7) * mm});
            skLineSegment(sketch, "E460", {"start": v(5, 5.7) * mm, "end": v(5, 5.72) * mm});
            skLineSegment(sketch, "E461", {"start": v(5, 5.72) * mm, "end": v(5.01, 5.74) * mm});
            skLineSegment(sketch, "E462", {"start": v(5.01, 5.74) * mm, "end": v(5.02, 5.77) * mm});
            skLineSegment(sketch, "E463", {"start": v(5.02, 5.77) * mm, "end": v(5.03, 5.8) * mm});
            skLineSegment(sketch, "E464", {"start": v(5.03, 5.8) * mm, "end": v(5.03, 5.82) * mm});
            skLineSegment(sketch, "E465", {"start": v(5.03, 5.82) * mm, "end": v(5.04, 5.85) * mm});
            skLineSegment(sketch, "E466", {"start": v(5.04, 5.85) * mm, "end": v(5.05, 5.88) * mm});
            skLineSegment(sketch, "E467", {"start": v(5.05, 5.88) * mm, "end": v(5.06, 5.9) * mm});
            skLineSegment(sketch, "E468", {"start": v(5.06, 5.9) * mm, "end": v(5.06, 5.94) * mm});
            skLineSegment(sketch, "E469", {"start": v(5.06, 5.94) * mm, "end": v(5.07, 5.97) * mm});
            skLineSegment(sketch, "E470", {"start": v(5.07, 5.97) * mm, "end": v(5.08, 6) * mm});
            skLineSegment(sketch, "E471", {"start": v(5.08, 6) * mm, "end": v(5.08, 6.03) * mm});
            skLineSegment(sketch, "E472", {"start": v(5.08, 6.03) * mm, "end": v(5.1, 6.06) * mm});
            skLineSegment(sketch, "E473", {"start": v(5.1, 6.06) * mm, "end": v(5.1, 6.1) * mm});
            skArc(sketch, "E474", {"start": v(5.1, 6.1) * mm, "mid": v(5, 6.18) * mm, "end": v(4.9, 6.26) * mm});
            skLineSegment(sketch, "E475", {"start": v(4.97, 5) * mm, "end": v(4.97, 5) * mm});
            skLineSegment(sketch, "E476", {"start": v(4.97, 5) * mm, "end": v(4.98, 4.99) * mm});
            skLineSegment(sketch, "E477", {"start": v(4.98, 4.99) * mm, "end": v(5, 4.99) * mm});
            skLineSegment(sketch, "E478", {"start": v(5, 4.99) * mm, "end": v(5, 5) * mm});
            skLineSegment(sketch, "E479", {"start": v(5, 5) * mm, "end": v(5.01, 5) * mm});
            skLineSegment(sketch, "E480", {"start": v(5.01, 5) * mm, "end": v(5.02, 5) * mm});
            skLineSegment(sketch, "E481", {"start": v(5.02, 5) * mm, "end": v(5.04, 5) * mm});
            skLineSegment(sketch, "E482", {"start": v(5.04, 5) * mm, "end": v(5.04, 5.01) * mm});
            skLineSegment(sketch, "E483", {"start": v(5.04, 5.01) * mm, "end": v(5.05, 5.02) * mm});
            skLineSegment(sketch, "E484", {"start": v(5.05, 5.02) * mm, "end": v(5.07, 5.03) * mm});
            skLineSegment(sketch, "E485", {"start": v(5.07, 5.03) * mm, "end": v(5.08, 5.03) * mm});
            skLineSegment(sketch, "E486", {"start": v(5.08, 5.03) * mm, "end": v(5.1, 5.04) * mm});
            skLineSegment(sketch, "E487", {"start": v(5.1, 5.04) * mm, "end": v(5.1, 5.05) * mm});
            skLineSegment(sketch, "E488", {"start": v(5.1, 5.05) * mm, "end": v(5.12, 5.06) * mm});
            skLineSegment(sketch, "E489", {"start": v(5.12, 5.06) * mm, "end": v(5.13, 5.07) * mm});
            skLineSegment(sketch, "E490", {"start": v(5.13, 5.07) * mm, "end": v(5.15, 5.07) * mm});
            skLineSegment(sketch, "E491", {"start": v(5.15, 5.07) * mm, "end": v(5.16, 5.08) * mm});
            skLineSegment(sketch, "E492", {"start": v(5.16, 5.08) * mm, "end": v(5.18, 5.1) * mm});
            skLineSegment(sketch, "E493", {"start": v(5.18, 5.1) * mm, "end": v(5.2, 5.1) * mm});
            skLineSegment(sketch, "E494", {"start": v(5.2, 5.1) * mm, "end": v(5.21, 5.1) * mm});
            skLineSegment(sketch, "E495", {"start": v(5.21, 5.1) * mm, "end": v(5.23, 5.12) * mm});
            skLineSegment(sketch, "E496", {"start": v(5.23, 5.12) * mm, "end": v(5.25, 5.12) * mm});
            skLineSegment(sketch, "E497", {"start": v(5.25, 5.12) * mm, "end": v(5.27, 5.13) * mm});
            skLineSegment(sketch, "E498", {"start": v(5.27, 5.13) * mm, "end": v(5.29, 5.14) * mm});
            skLineSegment(sketch, "E499", {"start": v(5.29, 5.14) * mm, "end": v(5.3, 5.15) * mm});
            skLineSegment(sketch, "E500", {"start": v(5.3, 5.15) * mm, "end": v(5.33, 5.16) * mm});
            skLineSegment(sketch, "E501", {"start": v(5.33, 5.16) * mm, "end": v(5.35, 5.17) * mm});
            skLineSegment(sketch, "E502", {"start": v(5.35, 5.17) * mm, "end": v(5.37, 5.18) * mm});
            skLineSegment(sketch, "E503", {"start": v(5.37, 5.18) * mm, "end": v(5.39, 5.19) * mm});
            skLineSegment(sketch, "E504", {"start": v(5.39, 5.19) * mm, "end": v(5.41, 5.2) * mm});
            skLineSegment(sketch, "E505", {"start": v(5.41, 5.2) * mm, "end": v(5.44, 5.2) * mm});
            skLineSegment(sketch, "E506", {"start": v(5.44, 5.2) * mm, "end": v(5.46, 5.21) * mm});
            skLineSegment(sketch, "E507", {"start": v(5.46, 5.21) * mm, "end": v(5.48, 5.22) * mm});
            skLineSegment(sketch, "E508", {"start": v(5.48, 5.22) * mm, "end": v(5.5, 5.23) * mm});
            skLineSegment(sketch, "E509", {"start": v(5.5, 5.23) * mm, "end": v(5.53, 5.24) * mm});
            skLineSegment(sketch, "E510", {"start": v(5.53, 5.24) * mm, "end": v(5.56, 5.25) * mm});
            skLineSegment(sketch, "E511", {"start": v(5.56, 5.25) * mm, "end": v(5.59, 5.26) * mm});
            skLineSegment(sketch, "E512", {"start": v(5.59, 5.26) * mm, "end": v(5.61, 5.27) * mm});
            skLineSegment(sketch, "E513", {"start": v(5.61, 5.27) * mm, "end": v(5.64, 5.28) * mm});
            skLineSegment(sketch, "E514", {"start": v(5.64, 5.28) * mm, "end": v(5.67, 5.29) * mm});
            skLineSegment(sketch, "E515", {"start": v(5.67, 5.29) * mm, "end": v(5.7, 5.3) * mm});
            skLineSegment(sketch, "E516", {"start": v(5.7, 5.3) * mm, "end": v(5.73, 5.3) * mm});
            skLineSegment(sketch, "E517", {"start": v(5.73, 5.3) * mm, "end": v(5.76, 5.31) * mm});
            skLineSegment(sketch, "E518", {"start": v(5.76, 5.31) * mm, "end": v(5.79, 5.32) * mm});
            skLineSegment(sketch, "E519", {"start": v(5.79, 5.32) * mm, "end": v(5.82, 5.33) * mm});
            skLineSegment(sketch, "E520", {"start": v(5.82, 5.33) * mm, "end": v(5.85, 5.33) * mm});
            skLineSegment(sketch, "E521", {"start": v(5.85, 5.33) * mm, "end": v(5.88, 5.34) * mm});
            skLineSegment(sketch, "E522", {"start": v(5.6, 4.28) * mm, "end": v(5.6, 4.3) * mm});
            skLineSegment(sketch, "E523", {"start": v(5.6, 4.3) * mm, "end": v(5.6, 4.3) * mm});
            skLineSegment(sketch, "E524", {"start": v(5.6, 4.3) * mm, "end": v(5.6, 4.31) * mm});
            skLineSegment(sketch, "E525", {"start": v(5.6, 4.31) * mm, "end": v(5.6, 4.33) * mm});
            skLineSegment(sketch, "E526", {"start": v(5.6, 4.33) * mm, "end": v(5.6, 4.34) * mm});
            skLineSegment(sketch, "E527", {"start": v(5.6, 4.34) * mm, "end": v(5.62, 4.35) * mm});
            skLineSegment(sketch, "E528", {"start": v(5.62, 4.35) * mm, "end": v(5.62, 4.36) * mm});
            skLineSegment(sketch, "E529", {"start": v(5.62, 4.36) * mm, "end": v(5.63, 4.37) * mm});
            skLineSegment(sketch, "E530", {"start": v(5.63, 4.37) * mm, "end": v(5.64, 4.38) * mm});
            skLineSegment(sketch, "E531", {"start": v(5.64, 4.38) * mm, "end": v(5.65, 4.39) * mm});
            skLineSegment(sketch, "E532", {"start": v(5.65, 4.39) * mm, "end": v(5.66, 4.4) * mm});
            skLineSegment(sketch, "E533", {"start": v(5.66, 4.4) * mm, "end": v(5.67, 4.41) * mm});
            skLineSegment(sketch, "E534", {"start": v(5.67, 4.41) * mm, "end": v(5.68, 4.42) * mm});
            skLineSegment(sketch, "E535", {"start": v(5.68, 4.42) * mm, "end": v(5.69, 4.44) * mm});
            skLineSegment(sketch, "E536", {"start": v(5.69, 4.44) * mm, "end": v(5.7, 4.45) * mm});
            skLineSegment(sketch, "E537", {"start": v(5.7, 4.45) * mm, "end": v(5.7, 4.47) * mm});
            skLineSegment(sketch, "E538", {"start": v(5.7, 4.47) * mm, "end": v(5.72, 4.48) * mm});
            skLineSegment(sketch, "E539", {"start": v(5.72, 4.48) * mm, "end": v(5.73, 4.5) * mm});
            skLineSegment(sketch, "E540", {"start": v(5.73, 4.5) * mm, "end": v(5.74, 4.51) * mm});
            skLineSegment(sketch, "E541", {"start": v(5.74, 4.51) * mm, "end": v(5.75, 4.53) * mm});
            skLineSegment(sketch, "E542", {"start": v(5.75, 4.53) * mm, "end": v(5.76, 4.54) * mm});
            skLineSegment(sketch, "E543", {"start": v(5.76, 4.54) * mm, "end": v(5.77, 4.56) * mm});
            skLineSegment(sketch, "E544", {"start": v(5.77, 4.56) * mm, "end": v(5.78, 4.58) * mm});
            skLineSegment(sketch, "E545", {"start": v(5.78, 4.58) * mm, "end": v(5.8, 4.6) * mm});
            skLineSegment(sketch, "E546", {"start": v(5.8, 4.6) * mm, "end": v(5.8, 4.62) * mm});
            skLineSegment(sketch, "E547", {"start": v(5.8, 4.62) * mm, "end": v(5.82, 4.64) * mm});
            skLineSegment(sketch, "E548", {"start": v(5.82, 4.64) * mm, "end": v(5.83, 4.66) * mm});
            skLineSegment(sketch, "E549", {"start": v(5.83, 4.66) * mm, "end": v(5.84, 4.68) * mm});
            skLineSegment(sketch, "E550", {"start": v(5.84, 4.68) * mm, "end": v(5.85, 4.7) * mm});
            skLineSegment(sketch, "E551", {"start": v(5.85, 4.7) * mm, "end": v(5.86, 4.72) * mm});
            skLineSegment(sketch, "E552", {"start": v(5.86, 4.72) * mm, "end": v(5.88, 4.74) * mm});
            skLineSegment(sketch, "E553", {"start": v(5.88, 4.74) * mm, "end": v(5.89, 4.76) * mm});
            skLineSegment(sketch, "E554", {"start": v(5.89, 4.76) * mm, "end": v(5.9, 4.79) * mm});
            skLineSegment(sketch, "E555", {"start": v(5.9, 4.79) * mm, "end": v(5.91, 4.81) * mm});
            skLineSegment(sketch, "E556", {"start": v(5.91, 4.81) * mm, "end": v(5.92, 4.84) * mm});
            skLineSegment(sketch, "E557", {"start": v(5.92, 4.84) * mm, "end": v(5.94, 4.86) * mm});
            skLineSegment(sketch, "E558", {"start": v(5.94, 4.86) * mm, "end": v(5.95, 4.89) * mm});
            skLineSegment(sketch, "E559", {"start": v(5.95, 4.89) * mm, "end": v(5.96, 4.91) * mm});
            skLineSegment(sketch, "E560", {"start": v(5.96, 4.91) * mm, "end": v(5.97, 4.94) * mm});
            skLineSegment(sketch, "E561", {"start": v(5.97, 4.94) * mm, "end": v(5.98, 4.97) * mm});
            skLineSegment(sketch, "E562", {"start": v(5.98, 4.97) * mm, "end": v(6, 5) * mm});
            skLineSegment(sketch, "E563", {"start": v(6, 5) * mm, "end": v(6, 5.02) * mm});
            skLineSegment(sketch, "E564", {"start": v(6, 5.02) * mm, "end": v(6.02, 5.05) * mm});
            skLineSegment(sketch, "E565", {"start": v(6.02, 5.05) * mm, "end": v(6.03, 5.08) * mm});
            skLineSegment(sketch, "E566", {"start": v(6.03, 5.08) * mm, "end": v(6.04, 5.11) * mm});
            skLineSegment(sketch, "E567", {"start": v(6.04, 5.11) * mm, "end": v(6.06, 5.14) * mm});
            skArc(sketch, "E568", {"start": v(6.06, 5.14) * mm, "mid": v(5.97, 5.24) * mm, "end": v(5.88, 5.34) * mm});
            skLineSegment(sketch, "E569", {"start": v(5.74, 4.08) * mm, "end": v(5.75, 4.08) * mm});
            skLineSegment(sketch, "E570", {"start": v(5.75, 4.08) * mm, "end": v(5.75, 4.08) * mm});
            skLineSegment(sketch, "E571", {"start": v(5.75, 4.08) * mm, "end": v(5.76, 4.07) * mm});
            skLineSegment(sketch, "E572", {"start": v(5.76, 4.07) * mm, "end": v(5.77, 4.07) * mm});
            skLineSegment(sketch, "E573", {"start": v(5.77, 4.07) * mm, "end": v(5.78, 4.08) * mm});
            skLineSegment(sketch, "E574", {"start": v(5.78, 4.08) * mm, "end": v(5.8, 4.08) * mm});
            skLineSegment(sketch, "E575", {"start": v(5.8, 4.08) * mm, "end": v(5.81, 4.08) * mm});
            skLineSegment(sketch, "E576", {"start": v(5.81, 4.08) * mm, "end": v(5.82, 4.09) * mm});
            skLineSegment(sketch, "E577", {"start": v(5.82, 4.09) * mm, "end": v(5.83, 4.1) * mm});
            skLineSegment(sketch, "E578", {"start": v(5.83, 4.1) * mm, "end": v(5.84, 4.1) * mm});
            skLineSegment(sketch, "E579", {"start": v(5.84, 4.1) * mm, "end": v(5.86, 4.1) * mm});
            skLineSegment(sketch, "E580", {"start": v(5.86, 4.1) * mm, "end": v(5.87, 4.1) * mm});
            skLineSegment(sketch, "E581", {"start": v(5.87, 4.1) * mm, "end": v(5.89, 4.11) * mm});
            skLineSegment(sketch, "E582", {"start": v(5.89, 4.11) * mm, "end": v(5.9, 4.12) * mm});
            skLineSegment(sketch, "E583", {"start": v(5.9, 4.12) * mm, "end": v(5.92, 4.12) * mm});
            skLineSegment(sketch, "E584", {"start": v(5.92, 4.12) * mm, "end": v(5.93, 4.13) * mm});
            skLineSegment(sketch, "E585", {"start": v(5.93, 4.13) * mm, "end": v(5.95, 4.14) * mm});
            skLineSegment(sketch, "E586", {"start": v(5.95, 4.14) * mm, "end": v(5.97, 4.14) * mm});
            skLineSegment(sketch, "E587", {"start": v(5.97, 4.14) * mm, "end": v(5.98, 4.15) * mm});
            skLineSegment(sketch, "E588", {"start": v(5.98, 4.15) * mm, "end": v(6, 4.15) * mm});
            skLineSegment(sketch, "E589", {"start": v(6, 4.15) * mm, "end": v(6.02, 4.16) * mm});
            skLineSegment(sketch, "E590", {"start": v(6.02, 4.16) * mm, "end": v(6.04, 4.16) * mm});
            skLineSegment(sketch, "E591", {"start": v(6.04, 4.16) * mm, "end": v(6.06, 4.17) * mm});
            skLineSegment(sketch, "E592", {"start": v(6.06, 4.17) * mm, "end": v(6.08, 4.18) * mm});
            skLineSegment(sketch, "E593", {"start": v(6.08, 4.18) * mm, "end": v(6.1, 4.18) * mm});
            skLineSegment(sketch, "E594", {"start": v(6.1, 4.18) * mm, "end": v(6.12, 4.19) * mm});
            skLineSegment(sketch, "E595", {"start": v(6.12, 4.19) * mm, "end": v(6.14, 4.2) * mm});
            skLineSegment(sketch, "E596", {"start": v(6.14, 4.2) * mm, "end": v(6.17, 4.2) * mm});
            skLineSegment(sketch, "E597", {"start": v(6.17, 4.2) * mm, "end": v(6.2, 4.2) * mm});
            skLineSegment(sketch, "E598", {"start": v(6.2, 4.2) * mm, "end": v(6.21, 4.2) * mm});
            skLineSegment(sketch, "E599", {"start": v(6.21, 4.2) * mm, "end": v(6.24, 4.21) * mm});
            skLineSegment(sketch, "E600", {"start": v(6.24, 4.21) * mm, "end": v(6.26, 4.22) * mm});
            skLineSegment(sketch, "E601", {"start": v(6.26, 4.22) * mm, "end": v(6.29, 4.22) * mm});
            skLineSegment(sketch, "E602", {"start": v(6.29, 4.22) * mm, "end": v(6.31, 4.23) * mm});
            skLineSegment(sketch, "E603", {"start": v(6.31, 4.23) * mm, "end": v(6.34, 4.23) * mm});
            skLineSegment(sketch, "E604", {"start": v(6.34, 4.23) * mm, "end": v(6.37, 4.24) * mm});
            skLineSegment(sketch, "E605", {"start": v(6.37, 4.24) * mm, "end": v(6.4, 4.24) * mm});
            skLineSegment(sketch, "E606", {"start": v(6.4, 4.24) * mm, "end": v(6.42, 4.24) * mm});
            skLineSegment(sketch, "E607", {"start": v(6.42, 4.24) * mm, "end": v(6.45, 4.25) * mm});
            skLineSegment(sketch, "E608", {"start": v(6.45, 4.25) * mm, "end": v(6.48, 4.25) * mm});
            skLineSegment(sketch, "E609", {"start": v(6.48, 4.25) * mm, "end": v(6.51, 4.25) * mm});
            skLineSegment(sketch, "E610", {"start": v(6.51, 4.25) * mm, "end": v(6.54, 4.26) * mm});
            skLineSegment(sketch, "E611", {"start": v(6.54, 4.26) * mm, "end": v(6.57, 4.26) * mm});
            skLineSegment(sketch, "E612", {"start": v(6.57, 4.26) * mm, "end": v(6.6, 4.26) * mm});
            skLineSegment(sketch, "E613", {"start": v(6.6, 4.26) * mm, "end": v(6.64, 4.27) * mm});
            skLineSegment(sketch, "E614", {"start": v(6.64, 4.27) * mm, "end": v(6.67, 4.27) * mm});
            skLineSegment(sketch, "E615", {"start": v(6.67, 4.27) * mm, "end": v(6.7, 4.27) * mm});
            skLineSegment(sketch, "E616", {"start": v(6.24, 3.28) * mm, "end": v(6.24, 3.28) * mm});
            skLineSegment(sketch, "E617", {"start": v(6.24, 3.28) * mm, "end": v(6.24, 3.3) * mm});
            skLineSegment(sketch, "E618", {"start": v(6.24, 3.3) * mm, "end": v(6.24, 3.3) * mm});
            skLineSegment(sketch, "E619", {"start": v(6.24, 3.3) * mm, "end": v(6.25, 3.3) * mm});
            skLineSegment(sketch, "E620", {"start": v(6.25, 3.3) * mm, "end": v(6.25, 3.32) * mm});
            skLineSegment(sketch, "E621", {"start": v(6.25, 3.32) * mm, "end": v(6.26, 3.33) * mm});
            skLineSegment(sketch, "E622", {"start": v(6.26, 3.33) * mm, "end": v(6.27, 3.34) * mm});
            skLineSegment(sketch, "E623", {"start": v(6.27, 3.34) * mm, "end": v(6.28, 3.34) * mm});
            skLineSegment(sketch, "E624", {"start": v(6.28, 3.34) * mm, "end": v(6.29, 3.35) * mm});
            skLineSegment(sketch, "E625", {"start": v(6.29, 3.35) * mm, "end": v(6.3, 3.36) * mm});
            skLineSegment(sketch, "E626", {"start": v(6.3, 3.36) * mm, "end": v(6.3, 3.37) * mm});
            skLineSegment(sketch, "E627", {"start": v(6.3, 3.37) * mm, "end": v(6.32, 3.38) * mm});
            skLineSegment(sketch, "E628", {"start": v(6.32, 3.38) * mm, "end": v(6.33, 3.4) * mm});
            skLineSegment(sketch, "E629", {"start": v(6.33, 3.4) * mm, "end": v(6.34, 3.4) * mm});
            skLineSegment(sketch, "E630", {"start": v(6.34, 3.4) * mm, "end": v(6.36, 3.41) * mm});
            skLineSegment(sketch, "E631", {"start": v(6.36, 3.41) * mm, "end": v(6.37, 3.42) * mm});
            skLineSegment(sketch, "E632", {"start": v(6.37, 3.42) * mm, "end": v(6.38, 3.44) * mm});
            skLineSegment(sketch, "E633", {"start": v(6.38, 3.44) * mm, "end": v(6.4, 3.45) * mm});
            skLineSegment(sketch, "E634", {"start": v(6.4, 3.45) * mm, "end": v(6.4, 3.46) * mm});
            skLineSegment(sketch, "E635", {"start": v(6.4, 3.46) * mm, "end": v(6.42, 3.48) * mm});
            skLineSegment(sketch, "E636", {"start": v(6.42, 3.48) * mm, "end": v(6.43, 3.5) * mm});
            skLineSegment(sketch, "E637", {"start": v(6.43, 3.5) * mm, "end": v(6.45, 3.5) * mm});
            skLineSegment(sketch, "E638", {"start": v(6.45, 3.5) * mm, "end": v(6.46, 3.52) * mm});
            skLineSegment(sketch, "E639", {"start": v(6.46, 3.52) * mm, "end": v(6.47, 3.54) * mm});
            skLineSegment(sketch, "E640", {"start": v(6.47, 3.54) * mm, "end": v(6.49, 3.55) * mm});
            skLineSegment(sketch, "E641", {"start": v(6.49, 3.55) * mm, "end": v(6.5, 3.57) * mm});
            skLineSegment(sketch, "E642", {"start": v(6.5, 3.57) * mm, "end": v(6.52, 3.59) * mm});
            skLineSegment(sketch, "E643", {"start": v(6.52, 3.59) * mm, "end": v(6.53, 3.6) * mm});
            skLineSegment(sketch, "E644", {"start": v(6.53, 3.6) * mm, "end": v(6.55, 3.62) * mm});
            skLineSegment(sketch, "E645", {"start": v(6.55, 3.62) * mm, "end": v(6.56, 3.64) * mm});
            skLineSegment(sketch, "E646", {"start": v(6.56, 3.64) * mm, "end": v(6.58, 3.66) * mm});
            skLineSegment(sketch, "E647", {"start": v(6.58, 3.66) * mm, "end": v(6.6, 3.68) * mm});
            skLineSegment(sketch, "E648", {"start": v(6.6, 3.68) * mm, "end": v(6.6, 3.7) * mm});
            skLineSegment(sketch, "E649", {"start": v(6.6, 3.7) * mm, "end": v(6.63, 3.72) * mm});
            skLineSegment(sketch, "E650", {"start": v(6.63, 3.72) * mm, "end": v(6.64, 3.74) * mm});
            skLineSegment(sketch, "E651", {"start": v(6.64, 3.74) * mm, "end": v(6.66, 3.77) * mm});
            skLineSegment(sketch, "E652", {"start": v(6.66, 3.77) * mm, "end": v(6.67, 3.79) * mm});
            skLineSegment(sketch, "E653", {"start": v(6.67, 3.79) * mm, "end": v(6.69, 3.81) * mm});
            skLineSegment(sketch, "E654", {"start": v(6.69, 3.81) * mm, "end": v(6.7, 3.84) * mm});
            skLineSegment(sketch, "E655", {"start": v(6.7, 3.84) * mm, "end": v(6.72, 3.86) * mm});
            skLineSegment(sketch, "E656", {"start": v(6.72, 3.86) * mm, "end": v(6.74, 3.89) * mm});
            skLineSegment(sketch, "E657", {"start": v(6.74, 3.89) * mm, "end": v(6.76, 3.91) * mm});
            skLineSegment(sketch, "E658", {"start": v(6.76, 3.91) * mm, "end": v(6.77, 3.94) * mm});
            skLineSegment(sketch, "E659", {"start": v(6.77, 3.94) * mm, "end": v(6.79, 3.96) * mm});
            skLineSegment(sketch, "E660", {"start": v(6.79, 3.96) * mm, "end": v(6.8, 4) * mm});
            skLineSegment(sketch, "E661", {"start": v(6.8, 4) * mm, "end": v(6.82, 4.02) * mm});
            skLineSegment(sketch, "E662", {"start": v(6.82, 4.02) * mm, "end": v(6.84, 4.05) * mm});
            skArc(sketch, "E663", {"start": v(6.84, 4.05) * mm, "mid": v(6.77, 4.16) * mm, "end": v(6.7, 4.27) * mm});
            skLineSegment(sketch, "E664", {"start": v(6.35, 3.05) * mm, "end": v(6.36, 3.05) * mm});
            skLineSegment(sketch, "E665", {"start": v(6.36, 3.05) * mm, "end": v(6.36, 3.04) * mm});
            skLineSegment(sketch, "E666", {"start": v(6.36, 3.04) * mm, "end": v(6.37, 3.04) * mm});
            skLineSegment(sketch, "E667", {"start": v(6.37, 3.04) * mm, "end": v(6.38, 3.04) * mm});
            skLineSegment(sketch, "E668", {"start": v(6.38, 3.04) * mm, "end": v(6.4, 3.04) * mm});
            skLineSegment(sketch, "E669", {"start": v(6.4, 3.04) * mm, "end": v(6.4, 3.04) * mm});
            skLineSegment(sketch, "E670", {"start": v(6.4, 3.04) * mm, "end": v(6.42, 3.04) * mm});
            skLineSegment(sketch, "E671", {"start": v(6.42, 3.04) * mm, "end": v(6.43, 3.04) * mm});
            skLineSegment(sketch, "E672", {"start": v(6.43, 3.04) * mm, "end": v(6.44, 3.05) * mm});
            skLineSegment(sketch, "E673", {"start": v(6.44, 3.05) * mm, "end": v(6.45, 3.05) * mm});
            skLineSegment(sketch, "E674", {"start": v(6.45, 3.05) * mm, "end": v(6.47, 3.05) * mm});
            skLineSegment(sketch, "E675", {"start": v(6.47, 3.05) * mm, "end": v(6.48, 3.06) * mm});
            skLineSegment(sketch, "E676", {"start": v(6.48, 3.06) * mm, "end": v(6.5, 3.06) * mm});
            skLineSegment(sketch, "E677", {"start": v(6.5, 3.06) * mm, "end": v(6.51, 3.06) * mm});
            skLineSegment(sketch, "E678", {"start": v(6.51, 3.06) * mm, "end": v(6.53, 3.07) * mm});
            skLineSegment(sketch, "E679", {"start": v(6.53, 3.07) * mm, "end": v(6.55, 3.07) * mm});
            skLineSegment(sketch, "E680", {"start": v(6.55, 3.07) * mm, "end": v(6.56, 3.07) * mm});
            skLineSegment(sketch, "E681", {"start": v(6.56, 3.07) * mm, "end": v(6.58, 3.07) * mm});
            skLineSegment(sketch, "E682", {"start": v(6.58, 3.07) * mm, "end": v(6.6, 3.08) * mm});
            skLineSegment(sketch, "E683", {"start": v(6.6, 3.08) * mm, "end": v(6.62, 3.08) * mm});
            skLineSegment(sketch, "E684", {"start": v(6.62, 3.08) * mm, "end": v(6.64, 3.08) * mm});
            skLineSegment(sketch, "E685", {"start": v(6.64, 3.08) * mm, "end": v(6.66, 3.08) * mm});
            skLineSegment(sketch, "E686", {"start": v(6.66, 3.08) * mm, "end": v(6.68, 3.09) * mm});
            skLineSegment(sketch, "E687", {"start": v(6.68, 3.09) * mm, "end": v(6.7, 3.09) * mm});
            skLineSegment(sketch, "E688", {"start": v(6.7, 3.09) * mm, "end": v(6.72, 3.09) * mm});
            skLineSegment(sketch, "E689", {"start": v(6.72, 3.09) * mm, "end": v(6.74, 3.1) * mm});
            skLineSegment(sketch, "E690", {"start": v(6.74, 3.1) * mm, "end": v(6.77, 3.1) * mm});
            skLineSegment(sketch, "E691", {"start": v(6.77, 3.1) * mm, "end": v(6.79, 3.1) * mm});
            skLineSegment(sketch, "E692", {"start": v(6.79, 3.1) * mm, "end": v(6.81, 3.1) * mm});
            skLineSegment(sketch, "E693", {"start": v(6.81, 3.1) * mm, "end": v(6.84, 3.1) * mm});
            skLineSegment(sketch, "E694", {"start": v(6.84, 3.1) * mm, "end": v(6.86, 3.1) * mm});
            skLineSegment(sketch, "E695", {"start": v(6.86, 3.1) * mm, "end": v(6.89, 3.1) * mm});
            skLineSegment(sketch, "E696", {"start": v(6.89, 3.1) * mm, "end": v(6.91, 3.1) * mm});
            skLineSegment(sketch, "E697", {"start": v(6.91, 3.1) * mm, "end": v(6.94, 3.1) * mm});
            skLineSegment(sketch, "E698", {"start": v(6.94, 3.1) * mm, "end": v(6.97, 3.1) * mm});
            skLineSegment(sketch, "E699", {"start": v(6.97, 3.1) * mm, "end": v(7, 3.1) * mm});
            skLineSegment(sketch, "E700", {"start": v(7, 3.1) * mm, "end": v(7.02, 3.1) * mm});
            skLineSegment(sketch, "E701", {"start": v(7.02, 3.1) * mm, "end": v(7.05, 3.1) * mm});
            skLineSegment(sketch, "E702", {"start": v(7.05, 3.1) * mm, "end": v(7.08, 3.1) * mm});
            skLineSegment(sketch, "E703", {"start": v(7.08, 3.1) * mm, "end": v(7.1, 3.1) * mm});
            skLineSegment(sketch, "E704", {"start": v(7.1, 3.1) * mm, "end": v(7.14, 3.1) * mm});
            skLineSegment(sketch, "E705", {"start": v(7.14, 3.1) * mm, "end": v(7.17, 3.1) * mm});
            skLineSegment(sketch, "E706", {"start": v(7.17, 3.1) * mm, "end": v(7.2, 3.09) * mm});
            skLineSegment(sketch, "E707", {"start": v(7.2, 3.09) * mm, "end": v(7.23, 3.09) * mm});
            skLineSegment(sketch, "E708", {"start": v(7.23, 3.09) * mm, "end": v(7.26, 3.08) * mm});
            skLineSegment(sketch, "E709", {"start": v(7.26, 3.08) * mm, "end": v(7.3, 3.08) * mm});
            skLineSegment(sketch, "E710", {"start": v(7.3, 3.08) * mm, "end": v(7.33, 3.08) * mm});
            skLineSegment(sketch, "E711", {"start": v(6.7, 2.18) * mm, "end": v(6.7, 2.18) * mm});
            skLineSegment(sketch, "E712", {"start": v(6.7, 2.18) * mm, "end": v(6.7, 2.19) * mm});
            skLineSegment(sketch, "E713", {"start": v(6.7, 2.19) * mm, "end": v(6.7, 2.2) * mm});
            skLineSegment(sketch, "E714", {"start": v(6.7, 2.2) * mm, "end": v(6.72, 2.2) * mm});
            skLineSegment(sketch, "E715", {"start": v(6.72, 2.2) * mm, "end": v(6.72, 2.21) * mm});
            skLineSegment(sketch, "E716", {"start": v(6.72, 2.21) * mm, "end": v(6.74, 2.22) * mm});
            skLineSegment(sketch, "E717", {"start": v(6.74, 2.22) * mm, "end": v(6.75, 2.23) * mm});
            skLineSegment(sketch, "E718", {"start": v(6.75, 2.23) * mm, "end": v(6.75, 2.23) * mm});
            skLineSegment(sketch, "E719", {"start": v(6.75, 2.23) * mm, "end": v(6.77, 2.24) * mm});
            skLineSegment(sketch, "E720", {"start": v(6.77, 2.24) * mm, "end": v(6.78, 2.25) * mm});
            skLineSegment(sketch, "E721", {"start": v(6.78, 2.25) * mm, "end": v(6.79, 2.26) * mm});
            skLineSegment(sketch, "E722", {"start": v(6.79, 2.26) * mm, "end": v(6.8, 2.26) * mm});
            skLineSegment(sketch, "E723", {"start": v(6.8, 2.26) * mm, "end": v(6.81, 2.27) * mm});
            skLineSegment(sketch, "E724", {"start": v(6.81, 2.27) * mm, "end": v(6.83, 2.28) * mm});
            skLineSegment(sketch, "E725", {"start": v(6.83, 2.28) * mm, "end": v(6.84, 2.29) * mm});
            skLineSegment(sketch, "E726", {"start": v(6.84, 2.29) * mm, "end": v(6.86, 2.3) * mm});
            skLineSegment(sketch, "E727", {"start": v(6.86, 2.3) * mm, "end": v(6.87, 2.3) * mm});
            skLineSegment(sketch, "E728", {"start": v(6.87, 2.3) * mm, "end": v(6.88, 2.32) * mm});
            skLineSegment(sketch, "E729", {"start": v(6.88, 2.32) * mm, "end": v(6.9, 2.33) * mm});
            skLineSegment(sketch, "E730", {"start": v(6.9, 2.33) * mm, "end": v(6.92, 2.34) * mm});
            skLineSegment(sketch, "E731", {"start": v(6.92, 2.34) * mm, "end": v(6.93, 2.35) * mm});
            skLineSegment(sketch, "E732", {"start": v(6.93, 2.35) * mm, "end": v(6.95, 2.37) * mm});
            skLineSegment(sketch, "E733", {"start": v(6.95, 2.37) * mm, "end": v(6.96, 2.38) * mm});
            skLineSegment(sketch, "E734", {"start": v(6.96, 2.38) * mm, "end": v(6.98, 2.4) * mm});
            skLineSegment(sketch, "E735", {"start": v(6.98, 2.4) * mm, "end": v(7, 2.4) * mm});
            skLineSegment(sketch, "E736", {"start": v(7, 2.4) * mm, "end": v(7.01, 2.42) * mm});
            skLineSegment(sketch, "E737", {"start": v(7.01, 2.42) * mm, "end": v(7.03, 2.43) * mm});
            skLineSegment(sketch, "E738", {"start": v(7.03, 2.43) * mm, "end": v(7.05, 2.45) * mm});
            skLineSegment(sketch, "E739", {"start": v(7.05, 2.45) * mm, "end": v(7.07, 2.46) * mm});
            skLineSegment(sketch, "E740", {"start": v(7.07, 2.46) * mm, "end": v(7.09, 2.48) * mm});
            skLineSegment(sketch, "E741", {"start": v(7.09, 2.48) * mm, "end": v(7.1, 2.5) * mm});
            skLineSegment(sketch, "E742", {"start": v(7.1, 2.5) * mm, "end": v(7.12, 2.51) * mm});
            skLineSegment(sketch, "E743", {"start": v(7.12, 2.51) * mm, "end": v(7.14, 2.53) * mm});
            skLineSegment(sketch, "E744", {"start": v(7.14, 2.53) * mm, "end": v(7.16, 2.55) * mm});
            skLineSegment(sketch, "E745", {"start": v(7.16, 2.55) * mm, "end": v(7.18, 2.57) * mm});
            skLineSegment(sketch, "E746", {"start": v(7.18, 2.57) * mm, "end": v(7.2, 2.59) * mm});
            skLineSegment(sketch, "E747", {"start": v(7.2, 2.59) * mm, "end": v(7.22, 2.6) * mm});
            skLineSegment(sketch, "E748", {"start": v(7.22, 2.6) * mm, "end": v(7.24, 2.63) * mm});
            skLineSegment(sketch, "E749", {"start": v(7.24, 2.63) * mm, "end": v(7.26, 2.65) * mm});
            skLineSegment(sketch, "E750", {"start": v(7.26, 2.65) * mm, "end": v(7.28, 2.67) * mm});
            skLineSegment(sketch, "E751", {"start": v(7.28, 2.67) * mm, "end": v(7.3, 2.7) * mm});
            skLineSegment(sketch, "E752", {"start": v(7.3, 2.7) * mm, "end": v(7.32, 2.71) * mm});
            skLineSegment(sketch, "E753", {"start": v(7.32, 2.71) * mm, "end": v(7.34, 2.74) * mm});
            skLineSegment(sketch, "E754", {"start": v(7.34, 2.74) * mm, "end": v(7.36, 2.76) * mm});
            skLineSegment(sketch, "E755", {"start": v(7.36, 2.76) * mm, "end": v(7.38, 2.78) * mm});
            skLineSegment(sketch, "E756", {"start": v(7.38, 2.78) * mm, "end": v(7.4, 2.8) * mm});
            skLineSegment(sketch, "E757", {"start": v(7.4, 2.8) * mm, "end": v(7.43, 2.83) * mm});
            skArc(sketch, "E758", {"start": v(7.43, 2.83) * mm, "mid": v(7.38, 2.96) * mm, "end": v(7.33, 3.08) * mm});
            skLineSegment(sketch, "E759", {"start": v(6.78, 1.93) * mm, "end": v(6.78, 1.93) * mm});
            skLineSegment(sketch, "E760", {"start": v(6.78, 1.93) * mm, "end": v(6.79, 1.92) * mm});
            skLineSegment(sketch, "E761", {"start": v(6.79, 1.92) * mm, "end": v(6.8, 1.92) * mm});
            skLineSegment(sketch, "E762", {"start": v(6.8, 1.92) * mm, "end": v(6.8, 1.92) * mm});
            skLineSegment(sketch, "E763", {"start": v(6.8, 1.92) * mm, "end": v(6.82, 1.92) * mm});
            skLineSegment(sketch, "E764", {"start": v(6.82, 1.92) * mm, "end": v(6.83, 1.91) * mm});
            skLineSegment(sketch, "E765", {"start": v(6.83, 1.91) * mm, "end": v(6.84, 1.91) * mm});
            skLineSegment(sketch, "E766", {"start": v(6.84, 1.91) * mm, "end": v(6.85, 1.91) * mm});
            skLineSegment(sketch, "E767", {"start": v(6.85, 1.91) * mm, "end": v(6.86, 1.92) * mm});
            skLineSegment(sketch, "E768", {"start": v(6.86, 1.92) * mm, "end": v(6.88, 1.92) * mm});
            skLineSegment(sketch, "E769", {"start": v(6.88, 1.92) * mm, "end": v(6.9, 1.92) * mm});
            skLineSegment(sketch, "E770", {"start": v(6.9, 1.92) * mm, "end": v(6.9, 1.92) * mm});
            skLineSegment(sketch, "E771", {"start": v(6.9, 1.92) * mm, "end": v(6.92, 1.92) * mm});
            skLineSegment(sketch, "E772", {"start": v(6.92, 1.92) * mm, "end": v(6.94, 1.92) * mm});
            skLineSegment(sketch, "E773", {"start": v(6.94, 1.92) * mm, "end": v(6.96, 1.92) * mm});
            skLineSegment(sketch, "E774", {"start": v(6.96, 1.92) * mm, "end": v(6.97, 1.92) * mm});
            skLineSegment(sketch, "E775", {"start": v(6.97, 1.92) * mm, "end": v(7, 1.92) * mm});
            skLineSegment(sketch, "E776", {"start": v(7, 1.92) * mm, "end": v(7, 1.92) * mm});
            skLineSegment(sketch, "E777", {"start": v(7, 1.92) * mm, "end": v(7.03, 1.92) * mm});
            skLineSegment(sketch, "E778", {"start": v(7.03, 1.92) * mm, "end": v(7.05, 1.92) * mm});
            skLineSegment(sketch, "E779", {"start": v(7.05, 1.92) * mm, "end": v(7.07, 1.91) * mm});
            skLineSegment(sketch, "E780", {"start": v(7.07, 1.91) * mm, "end": v(7.09, 1.91) * mm});
            skLineSegment(sketch, "E781", {"start": v(7.09, 1.91) * mm, "end": v(7.1, 1.91) * mm});
            skLineSegment(sketch, "E782", {"start": v(7.1, 1.91) * mm, "end": v(7.13, 1.91) * mm});
            skLineSegment(sketch, "E783", {"start": v(7.13, 1.91) * mm, "end": v(7.15, 1.9) * mm});
            skLineSegment(sketch, "E784", {"start": v(7.15, 1.9) * mm, "end": v(7.17, 1.9) * mm});
            skLineSegment(sketch, "E785", {"start": v(7.17, 1.9) * mm, "end": v(7.2, 1.9) * mm});
            skLineSegment(sketch, "E786", {"start": v(7.2, 1.9) * mm, "end": v(7.22, 1.9) * mm});
            skLineSegment(sketch, "E787", {"start": v(7.22, 1.9) * mm, "end": v(7.24, 1.9) * mm});
            skLineSegment(sketch, "E788", {"start": v(7.24, 1.9) * mm, "end": v(7.26, 1.9) * mm});
            skLineSegment(sketch, "E789", {"start": v(7.26, 1.9) * mm, "end": v(7.29, 1.9) * mm});
            skLineSegment(sketch, "E790", {"start": v(7.29, 1.9) * mm, "end": v(7.31, 1.89) * mm});
            skLineSegment(sketch, "E791", {"start": v(7.31, 1.89) * mm, "end": v(7.34, 1.89) * mm});
            skLineSegment(sketch, "E792", {"start": v(7.34, 1.89) * mm, "end": v(7.37, 1.88) * mm});
            skLineSegment(sketch, "E793", {"start": v(7.37, 1.88) * mm, "end": v(7.4, 1.88) * mm});
            skLineSegment(sketch, "E794", {"start": v(7.4, 1.88) * mm, "end": v(7.42, 1.87) * mm});
            skLineSegment(sketch, "E795", {"start": v(7.42, 1.87) * mm, "end": v(7.45, 1.87) * mm});
            skLineSegment(sketch, "E796", {"start": v(7.45, 1.87) * mm, "end": v(7.47, 1.86) * mm});
            skLineSegment(sketch, "E797", {"start": v(7.47, 1.86) * mm, "end": v(7.5, 1.85) * mm});
            skLineSegment(sketch, "E798", {"start": v(7.5, 1.85) * mm, "end": v(7.53, 1.85) * mm});
            skLineSegment(sketch, "E799", {"start": v(7.53, 1.85) * mm, "end": v(7.56, 1.84) * mm});
            skLineSegment(sketch, "E800", {"start": v(7.56, 1.84) * mm, "end": v(7.59, 1.84) * mm});
            skLineSegment(sketch, "E801", {"start": v(7.59, 1.84) * mm, "end": v(7.62, 1.83) * mm});
            skLineSegment(sketch, "E802", {"start": v(7.62, 1.83) * mm, "end": v(7.65, 1.82) * mm});
            skLineSegment(sketch, "E803", {"start": v(7.65, 1.82) * mm, "end": v(7.68, 1.81) * mm});
            skLineSegment(sketch, "E804", {"start": v(7.68, 1.81) * mm, "end": v(7.71, 1.8) * mm});
            skLineSegment(sketch, "E805", {"start": v(7.71, 1.8) * mm, "end": v(7.74, 1.8) * mm});
            skLineSegment(sketch, "E806", {"start": v(6.98, 1.01) * mm, "end": v(6.98, 1.02) * mm});
            skLineSegment(sketch, "E807", {"start": v(6.98, 1.02) * mm, "end": v(6.98, 1.02) * mm});
            skLineSegment(sketch, "E808", {"start": v(6.98, 1.02) * mm, "end": v(6.99, 1.03) * mm});
            skLineSegment(sketch, "E809", {"start": v(6.99, 1.03) * mm, "end": v(7, 1.04) * mm});
            skLineSegment(sketch, "E810", {"start": v(7, 1.04) * mm, "end": v(7, 1.04) * mm});
            skLineSegment(sketch, "E811", {"start": v(7, 1.04) * mm, "end": v(7.02, 1.05) * mm});
            skLineSegment(sketch, "E812", {"start": v(7.02, 1.05) * mm, "end": v(7.03, 1.06) * mm});
            skLineSegment(sketch, "E813", {"start": v(7.03, 1.06) * mm, "end": v(7.04, 1.06) * mm});
            skLineSegment(sketch, "E814", {"start": v(7.04, 1.06) * mm, "end": v(7.05, 1.06) * mm});
            skLineSegment(sketch, "E815", {"start": v(7.05, 1.06) * mm, "end": v(7.06, 1.07) * mm});
            skLineSegment(sketch, "E816", {"start": v(7.06, 1.07) * mm, "end": v(7.07, 1.08) * mm});
            skLineSegment(sketch, "E817", {"start": v(7.07, 1.08) * mm, "end": v(7.09, 1.08) * mm});
            skLineSegment(sketch, "E818", {"start": v(7.09, 1.08) * mm, "end": v(7.1, 1.09) * mm});
            skLineSegment(sketch, "E819", {"start": v(7.1, 1.09) * mm, "end": v(7.12, 1.1) * mm});
            skLineSegment(sketch, "E820", {"start": v(7.12, 1.1) * mm, "end": v(7.13, 1.1) * mm});
            skLineSegment(sketch, "E821", {"start": v(7.13, 1.1) * mm, "end": v(7.15, 1.1) * mm});
            skLineSegment(sketch, "E822", {"start": v(7.15, 1.1) * mm, "end": v(7.16, 1.11) * mm});
            skLineSegment(sketch, "E823", {"start": v(7.16, 1.11) * mm, "end": v(7.18, 1.12) * mm});
            skLineSegment(sketch, "E824", {"start": v(7.18, 1.12) * mm, "end": v(7.2, 1.13) * mm});
            skLineSegment(sketch, "E825", {"start": v(7.2, 1.13) * mm, "end": v(7.21, 1.14) * mm});
            skLineSegment(sketch, "E826", {"start": v(7.21, 1.14) * mm, "end": v(7.23, 1.15) * mm});
            skLineSegment(sketch, "E827", {"start": v(7.23, 1.15) * mm, "end": v(7.25, 1.16) * mm});
            skLineSegment(sketch, "E828", {"start": v(7.25, 1.16) * mm, "end": v(7.27, 1.17) * mm});
            skLineSegment(sketch, "E829", {"start": v(7.27, 1.17) * mm, "end": v(7.29, 1.18) * mm});
            skLineSegment(sketch, "E830", {"start": v(7.29, 1.18) * mm, "end": v(7.3, 1.19) * mm});
            skLineSegment(sketch, "E831", {"start": v(7.3, 1.19) * mm, "end": v(7.32, 1.2) * mm});
            skLineSegment(sketch, "E832", {"start": v(7.32, 1.2) * mm, "end": v(7.34, 1.2) * mm});
            skLineSegment(sketch, "E833", {"start": v(7.34, 1.2) * mm, "end": v(7.36, 1.22) * mm});
            skLineSegment(sketch, "E834", {"start": v(7.36, 1.22) * mm, "end": v(7.38, 1.23) * mm});
            skLineSegment(sketch, "E835", {"start": v(7.38, 1.23) * mm, "end": v(7.4, 1.25) * mm});
            skLineSegment(sketch, "E836", {"start": v(7.4, 1.25) * mm, "end": v(7.42, 1.26) * mm});
            skLineSegment(sketch, "E837", {"start": v(7.42, 1.26) * mm, "end": v(7.45, 1.27) * mm});
            skLineSegment(sketch, "E838", {"start": v(7.45, 1.27) * mm, "end": v(7.47, 1.29) * mm});
            skLineSegment(sketch, "E839", {"start": v(7.47, 1.29) * mm, "end": v(7.49, 1.3) * mm});
            skLineSegment(sketch, "E840", {"start": v(7.49, 1.3) * mm, "end": v(7.51, 1.32) * mm});
            skLineSegment(sketch, "E841", {"start": v(7.51, 1.32) * mm, "end": v(7.53, 1.33) * mm});
            skLineSegment(sketch, "E842", {"start": v(7.53, 1.33) * mm, "end": v(7.56, 1.35) * mm});
            skLineSegment(sketch, "E843", {"start": v(7.56, 1.35) * mm, "end": v(7.58, 1.37) * mm});
            skLineSegment(sketch, "E844", {"start": v(7.58, 1.37) * mm, "end": v(7.6, 1.38) * mm});
            skLineSegment(sketch, "E845", {"start": v(7.6, 1.38) * mm, "end": v(7.63, 1.4) * mm});
            skLineSegment(sketch, "E846", {"start": v(7.63, 1.4) * mm, "end": v(7.65, 1.42) * mm});
            skLineSegment(sketch, "E847", {"start": v(7.65, 1.42) * mm, "end": v(7.68, 1.44) * mm});
            skLineSegment(sketch, "E848", {"start": v(7.68, 1.44) * mm, "end": v(7.7, 1.46) * mm});
            skLineSegment(sketch, "E849", {"start": v(7.7, 1.46) * mm, "end": v(7.72, 1.47) * mm});
            skLineSegment(sketch, "E850", {"start": v(7.72, 1.47) * mm, "end": v(7.75, 1.5) * mm});
            skLineSegment(sketch, "E851", {"start": v(7.75, 1.5) * mm, "end": v(7.77, 1.52) * mm});
            skLineSegment(sketch, "E852", {"start": v(7.77, 1.52) * mm, "end": v(7.8, 1.54) * mm});
            skArc(sketch, "E853", {"start": v(7.8, 1.54) * mm, "mid": v(7.77, 1.67) * mm, "end": v(7.74, 1.8) * mm});
            skLineSegment(sketch, "E854", {"start": v(7, 0.76) * mm, "end": v(7.01, 0.76) * mm});
            skLineSegment(sketch, "E855", {"start": v(7.01, 0.76) * mm, "end": v(7.02, 0.75) * mm});
            skLineSegment(sketch, "E856", {"start": v(7.02, 0.75) * mm, "end": v(7.02, 0.74) * mm});
            skLineSegment(sketch, "E857", {"start": v(7.02, 0.74) * mm, "end": v(7.03, 0.74) * mm});
            skLineSegment(sketch, "E858", {"start": v(7.03, 0.74) * mm, "end": v(7.04, 0.74) * mm});
            skLineSegment(sketch, "E859", {"start": v(7.04, 0.74) * mm, "end": v(7.06, 0.73) * mm});
            skLineSegment(sketch, "E860", {"start": v(7.06, 0.73) * mm, "end": v(7.07, 0.73) * mm});
            skLineSegment(sketch, "E861", {"start": v(7.07, 0.73) * mm, "end": v(7.08, 0.73) * mm});
            skLineSegment(sketch, "E862", {"start": v(7.08, 0.73) * mm, "end": v(7.1, 0.73) * mm});
            skLineSegment(sketch, "E863", {"start": v(7.1, 0.73) * mm, "end": v(7.1, 0.73) * mm});
            skLineSegment(sketch, "E864", {"start": v(7.1, 0.73) * mm, "end": v(7.12, 0.72) * mm});
            skLineSegment(sketch, "E865", {"start": v(7.12, 0.72) * mm, "end": v(7.13, 0.72) * mm});
            skLineSegment(sketch, "E866", {"start": v(7.13, 0.72) * mm, "end": v(7.15, 0.72) * mm});
            skLineSegment(sketch, "E867", {"start": v(7.15, 0.72) * mm, "end": v(7.17, 0.72) * mm});
            skLineSegment(sketch, "E868", {"start": v(7.17, 0.72) * mm, "end": v(7.18, 0.71) * mm});
            skLineSegment(sketch, "E869", {"start": v(7.18, 0.71) * mm, "end": v(7.2, 0.71) * mm});
            skLineSegment(sketch, "E870", {"start": v(7.2, 0.71) * mm, "end": v(7.22, 0.7) * mm});
            skLineSegment(sketch, "E871", {"start": v(7.22, 0.7) * mm, "end": v(7.23, 0.7) * mm});
            skLineSegment(sketch, "E872", {"start": v(7.23, 0.7) * mm, "end": v(7.25, 0.7) * mm});
            skLineSegment(sketch, "E873", {"start": v(7.25, 0.7) * mm, "end": v(7.27, 0.7) * mm});
            skLineSegment(sketch, "E874", {"start": v(7.27, 0.7) * mm, "end": v(7.29, 0.7) * mm});
            skLineSegment(sketch, "E875", {"start": v(7.29, 0.7) * mm, "end": v(7.3, 0.69) * mm});
            skLineSegment(sketch, "E876", {"start": v(7.3, 0.69) * mm, "end": v(7.33, 0.68) * mm});
            skLineSegment(sketch, "E877", {"start": v(7.33, 0.68) * mm, "end": v(7.35, 0.68) * mm});
            skLineSegment(sketch, "E878", {"start": v(7.35, 0.68) * mm, "end": v(7.37, 0.67) * mm});
            skLineSegment(sketch, "E879", {"start": v(7.37, 0.67) * mm, "end": v(7.4, 0.67) * mm});
            skLineSegment(sketch, "E880", {"start": v(7.4, 0.67) * mm, "end": v(7.41, 0.66) * mm});
            skLineSegment(sketch, "E881", {"start": v(7.41, 0.66) * mm, "end": v(7.44, 0.65) * mm});
            skLineSegment(sketch, "E882", {"start": v(7.44, 0.65) * mm, "end": v(7.46, 0.65) * mm});
            skLineSegment(sketch, "E883", {"start": v(7.46, 0.65) * mm, "end": v(7.48, 0.64) * mm});
            skLineSegment(sketch, "E884", {"start": v(7.48, 0.64) * mm, "end": v(7.5, 0.63) * mm});
            skLineSegment(sketch, "E885", {"start": v(7.5, 0.63) * mm, "end": v(7.53, 0.63) * mm});
            skLineSegment(sketch, "E886", {"start": v(7.53, 0.63) * mm, "end": v(7.55, 0.62) * mm});
            skLineSegment(sketch, "E887", {"start": v(7.55, 0.62) * mm, "end": v(7.58, 0.6) * mm});
            skLineSegment(sketch, "E888", {"start": v(7.58, 0.6) * mm, "end": v(7.6, 0.6) * mm});
            skLineSegment(sketch, "E889", {"start": v(7.6, 0.6) * mm, "end": v(7.63, 0.6) * mm});
            skLineSegment(sketch, "E890", {"start": v(7.63, 0.6) * mm, "end": v(7.66, 0.58) * mm});
            skLineSegment(sketch, "E891", {"start": v(7.66, 0.58) * mm, "end": v(7.68, 0.57) * mm});
            skLineSegment(sketch, "E892", {"start": v(7.68, 0.57) * mm, "end": v(7.7, 0.56) * mm});
            skLineSegment(sketch, "E893", {"start": v(7.7, 0.56) * mm, "end": v(7.74, 0.55) * mm});
            skLineSegment(sketch, "E894", {"start": v(7.74, 0.55) * mm, "end": v(7.76, 0.54) * mm});
            skLineSegment(sketch, "E895", {"start": v(7.76, 0.54) * mm, "end": v(7.8, 0.53) * mm});
            skLineSegment(sketch, "E896", {"start": v(7.8, 0.53) * mm, "end": v(7.82, 0.51) * mm});
            skLineSegment(sketch, "E897", {"start": v(7.82, 0.51) * mm, "end": v(7.85, 0.5) * mm});
            skLineSegment(sketch, "E898", {"start": v(7.85, 0.5) * mm, "end": v(7.88, 0.49) * mm});
            skLineSegment(sketch, "E899", {"start": v(7.88, 0.49) * mm, "end": v(7.9, 0.47) * mm});
            skLineSegment(sketch, "E900", {"start": v(7.9, 0.47) * mm, "end": v(7.94, 0.46) * mm});
            skLineSegment(sketch, "E901", {"start": v(7.05, -0.18) * mm, "end": v(7.05, -0.18) * mm});
            skLineSegment(sketch, "E902", {"start": v(7.05, -0.18) * mm, "end": v(7.05, -0.17) * mm});
            skLineSegment(sketch, "E903", {"start": v(7.05, -0.17) * mm, "end": v(7.06, -0.16) * mm});
            skLineSegment(sketch, "E904", {"start": v(7.06, -0.16) * mm, "end": v(7.07, -0.16) * mm});
            skLineSegment(sketch, "E905", {"start": v(7.07, -0.16) * mm, "end": v(7.08, -0.15) * mm});
            skLineSegment(sketch, "E906", {"start": v(7.08, -0.15) * mm, "end": v(7.1, -0.15) * mm});
            skLineSegment(sketch, "E907", {"start": v(7.1, -0.15) * mm, "end": v(7.1, -0.15) * mm});
            skLineSegment(sketch, "E908", {"start": v(7.1, -0.15) * mm, "end": v(7.12, -0.14) * mm});
            skLineSegment(sketch, "E909", {"start": v(7.12, -0.14) * mm, "end": v(7.13, -0.14) * mm});
            skLineSegment(sketch, "E910", {"start": v(7.13, -0.14) * mm, "end": v(7.14, -0.14) * mm});
            skLineSegment(sketch, "E911", {"start": v(7.14, -0.14) * mm, "end": v(7.16, -0.14) * mm});
            skLineSegment(sketch, "E912", {"start": v(7.16, -0.14) * mm, "end": v(7.17, -0.13) * mm});
            skLineSegment(sketch, "E913", {"start": v(7.17, -0.13) * mm, "end": v(7.19, -0.13) * mm});
            skLineSegment(sketch, "E914", {"start": v(7.19, -0.13) * mm, "end": v(7.2, -0.13) * mm});
            skLineSegment(sketch, "E915", {"start": v(7.2, -0.13) * mm, "end": v(7.22, -0.12) * mm});
            skLineSegment(sketch, "E916", {"start": v(7.22, -0.12) * mm, "end": v(7.23, -0.12) * mm});
            skLineSegment(sketch, "E917", {"start": v(7.23, -0.12) * mm, "end": v(7.25, -0.11) * mm});
            skLineSegment(sketch, "E918", {"start": v(7.25, -0.11) * mm, "end": v(7.27, -0.1) * mm});
            skLineSegment(sketch, "E919", {"start": v(7.27, -0.1) * mm, "end": v(7.29, -0.1) * mm});
            skLineSegment(sketch, "E920", {"start": v(7.29, -0.1) * mm, "end": v(7.3, -0.1) * mm});
            skLineSegment(sketch, "E921", {"start": v(7.3, -0.1) * mm, "end": v(7.32, -0.1) * mm});
            skLineSegment(sketch, "E922", {"start": v(7.32, -0.1) * mm, "end": v(7.34, -0.08) * mm});
            skLineSegment(sketch, "E923", {"start": v(7.34, -0.08) * mm, "end": v(7.36, -0.08) * mm});
            skLineSegment(sketch, "E924", {"start": v(7.36, -0.08) * mm, "end": v(7.38, -0.07) * mm});
            skLineSegment(sketch, "E925", {"start": v(7.38, -0.07) * mm, "end": v(7.4, -0.06) * mm});
            skLineSegment(sketch, "E926", {"start": v(7.4, -0.06) * mm, "end": v(7.42, -0.06) * mm});
            skLineSegment(sketch, "E927", {"start": v(7.42, -0.06) * mm, "end": v(7.44, -0.05) * mm});
            skLineSegment(sketch, "E928", {"start": v(7.44, -0.05) * mm, "end": v(7.47, -0.04) * mm});
            skLineSegment(sketch, "E929", {"start": v(7.47, -0.04) * mm, "end": v(7.49, -0.03) * mm});
            skLineSegment(sketch, "E930", {"start": v(7.49, -0.03) * mm, "end": v(7.5, -0.02) * mm});
            skLineSegment(sketch, "E931", {"start": v(7.5, -0.02) * mm, "end": v(7.53, -0.01) * mm});
            skLineSegment(sketch, "E932", {"start": v(7.53, -0.01) * mm, "end": v(7.56, 0) * mm});
            skLineSegment(sketch, "E933", {"start": v(7.56, 0) * mm, "end": v(7.58, 0) * mm});
            skLineSegment(sketch, "E934", {"start": v(7.58, 0) * mm, "end": v(7.6, 0.02) * mm});
            skLineSegment(sketch, "E935", {"start": v(7.6, 0.02) * mm, "end": v(7.63, 0.03) * mm});
            skLineSegment(sketch, "E936", {"start": v(7.63, 0.03) * mm, "end": v(7.65, 0.04) * mm});
            skLineSegment(sketch, "E937", {"start": v(7.65, 0.04) * mm, "end": v(7.68, 0.05) * mm});
            skLineSegment(sketch, "E938", {"start": v(7.68, 0.05) * mm, "end": v(7.7, 0.06) * mm});
            skLineSegment(sketch, "E939", {"start": v(7.7, 0.06) * mm, "end": v(7.73, 0.08) * mm});
            skLineSegment(sketch, "E940", {"start": v(7.73, 0.08) * mm, "end": v(7.76, 0.1) * mm});
            skLineSegment(sketch, "E941", {"start": v(7.76, 0.1) * mm, "end": v(7.78, 0.1) * mm});
            skLineSegment(sketch, "E942", {"start": v(7.78, 0.1) * mm, "end": v(7.8, 0.12) * mm});
            skLineSegment(sketch, "E943", {"start": v(7.8, 0.12) * mm, "end": v(7.84, 0.13) * mm});
            skLineSegment(sketch, "E944", {"start": v(7.84, 0.13) * mm, "end": v(7.86, 0.15) * mm});
            skLineSegment(sketch, "E945", {"start": v(7.86, 0.15) * mm, "end": v(7.9, 0.16) * mm});
            skLineSegment(sketch, "E946", {"start": v(7.9, 0.16) * mm, "end": v(7.92, 0.18) * mm});
            skLineSegment(sketch, "E947", {"start": v(7.92, 0.18) * mm, "end": v(7.95, 0.2) * mm});
            skArc(sketch, "E948", {"start": v(7.95, 0.2) * mm, "mid": v(7.94, 0.33) * mm, "end": v(7.94, 0.46) * mm});
            skLineSegment(sketch, "E949", {"start": v(7.04, -0.43) * mm, "end": v(7.04, -0.44) * mm});
            skLineSegment(sketch, "E950", {"start": v(7.04, -0.44) * mm, "end": v(7.04, -0.45) * mm});
            skLineSegment(sketch, "E951", {"start": v(7.04, -0.45) * mm, "end": v(7.05, -0.45) * mm});
            skLineSegment(sketch, "E952", {"start": v(7.05, -0.45) * mm, "end": v(7.06, -0.46) * mm});
            skLineSegment(sketch, "E953", {"start": v(7.06, -0.46) * mm, "end": v(7.07, -0.46) * mm});
            skLineSegment(sketch, "E954", {"start": v(7.07, -0.46) * mm, "end": v(7.08, -0.47) * mm});
            skLineSegment(sketch, "E955", {"start": v(7.08, -0.47) * mm, "end": v(7.1, -0.48) * mm});
            skLineSegment(sketch, "E956", {"start": v(7.1, -0.48) * mm, "end": v(7.1, -0.48) * mm});
            skLineSegment(sketch, "E957", {"start": v(7.1, -0.48) * mm, "end": v(7.11, -0.48) * mm});
            skLineSegment(sketch, "E958", {"start": v(7.11, -0.48) * mm, "end": v(7.13, -0.49) * mm});
            skLineSegment(sketch, "E959", {"start": v(7.13, -0.49) * mm, "end": v(7.14, -0.49) * mm});
            skLineSegment(sketch, "E960", {"start": v(7.14, -0.49) * mm, "end": v(7.16, -0.5) * mm});
            skLineSegment(sketch, "E961", {"start": v(7.16, -0.5) * mm, "end": v(7.17, -0.5) * mm});
            skLineSegment(sketch, "E962", {"start": v(7.17, -0.5) * mm, "end": v(7.18, -0.5) * mm});
            skLineSegment(sketch, "E963", {"start": v(7.18, -0.5) * mm, "end": v(7.2, -0.5) * mm});
            skLineSegment(sketch, "E964", {"start": v(7.2, -0.5) * mm, "end": v(7.22, -0.52) * mm});
            skLineSegment(sketch, "E965", {"start": v(7.22, -0.52) * mm, "end": v(7.23, -0.52) * mm});
            skLineSegment(sketch, "E966", {"start": v(7.23, -0.52) * mm, "end": v(7.25, -0.53) * mm});
            skLineSegment(sketch, "E967", {"start": v(7.25, -0.53) * mm, "end": v(7.27, -0.53) * mm});
            skLineSegment(sketch, "E968", {"start": v(7.27, -0.53) * mm, "end": v(7.28, -0.54) * mm});
            skLineSegment(sketch, "E969", {"start": v(7.28, -0.54) * mm, "end": v(7.3, -0.55) * mm});
            skLineSegment(sketch, "E970", {"start": v(7.3, -0.55) * mm, "end": v(7.32, -0.56) * mm});
            skLineSegment(sketch, "E971", {"start": v(7.32, -0.56) * mm, "end": v(7.34, -0.56) * mm});
            skLineSegment(sketch, "E972", {"start": v(7.34, -0.56) * mm, "end": v(7.36, -0.57) * mm});
            skLineSegment(sketch, "E973", {"start": v(7.36, -0.57) * mm, "end": v(7.38, -0.58) * mm});
            skLineSegment(sketch, "E974", {"start": v(7.38, -0.58) * mm, "end": v(7.4, -0.6) * mm});
            skLineSegment(sketch, "E975", {"start": v(7.4, -0.6) * mm, "end": v(7.42, -0.6) * mm});
            skLineSegment(sketch, "E976", {"start": v(7.42, -0.6) * mm, "end": v(7.44, -0.61) * mm});
            skLineSegment(sketch, "E977", {"start": v(7.44, -0.61) * mm, "end": v(7.46, -0.62) * mm});
            skLineSegment(sketch, "E978", {"start": v(7.46, -0.62) * mm, "end": v(7.48, -0.63) * mm});
            skLineSegment(sketch, "E979", {"start": v(7.48, -0.63) * mm, "end": v(7.5, -0.64) * mm});
            skLineSegment(sketch, "E980", {"start": v(7.5, -0.64) * mm, "end": v(7.53, -0.66) * mm});
            skLineSegment(sketch, "E981", {"start": v(7.53, -0.66) * mm, "end": v(7.55, -0.67) * mm});
            skLineSegment(sketch, "E982", {"start": v(7.55, -0.67) * mm, "end": v(7.57, -0.68) * mm});
            skLineSegment(sketch, "E983", {"start": v(7.57, -0.68) * mm, "end": v(7.6, -0.7) * mm});
            skLineSegment(sketch, "E984", {"start": v(7.6, -0.7) * mm, "end": v(7.62, -0.7) * mm});
            skLineSegment(sketch, "E985", {"start": v(7.62, -0.7) * mm, "end": v(7.65, -0.72) * mm});
            skLineSegment(sketch, "E986", {"start": v(7.65, -0.72) * mm, "end": v(7.67, -0.74) * mm});
            skLineSegment(sketch, "E987", {"start": v(7.67, -0.74) * mm, "end": v(7.7, -0.75) * mm});
            skLineSegment(sketch, "E988", {"start": v(7.7, -0.75) * mm, "end": v(7.72, -0.77) * mm});
            skLineSegment(sketch, "E989", {"start": v(7.72, -0.77) * mm, "end": v(7.74, -0.78) * mm});
            skLineSegment(sketch, "E990", {"start": v(7.74, -0.78) * mm, "end": v(7.77, -0.8) * mm});
            skLineSegment(sketch, "E991", {"start": v(7.77, -0.8) * mm, "end": v(7.8, -0.82) * mm});
            skLineSegment(sketch, "E992", {"start": v(7.8, -0.82) * mm, "end": v(7.82, -0.83) * mm});
            skLineSegment(sketch, "E993", {"start": v(7.82, -0.83) * mm, "end": v(7.85, -0.85) * mm});
            skLineSegment(sketch, "E994", {"start": v(7.85, -0.85) * mm, "end": v(7.88, -0.87) * mm});
            skLineSegment(sketch, "E995", {"start": v(7.88, -0.87) * mm, "end": v(7.9, -0.89) * mm});
            skLineSegment(sketch, "E996", {"start": v(6.92, -1.37) * mm, "end": v(6.92, -1.37) * mm});
            skLineSegment(sketch, "E997", {"start": v(6.92, -1.37) * mm, "end": v(6.93, -1.36) * mm});
            skLineSegment(sketch, "E998", {"start": v(6.93, -1.36) * mm, "end": v(6.93, -1.36) * mm});
            skLineSegment(sketch, "E999", {"start": v(6.93, -1.36) * mm, "end": v(6.94, -1.35) * mm});
            skLineSegment(sketch, "E1000", {"start": v(6.94, -1.35) * mm, "end": v(6.95, -1.35) * mm});
            skLineSegment(sketch, "E1001", {"start": v(6.95, -1.35) * mm, "end": v(6.97, -1.35) * mm});
            skLineSegment(sketch, "E1002", {"start": v(6.97, -1.35) * mm, "end": v(6.98, -1.35) * mm});
            skLineSegment(sketch, "E1003", {"start": v(6.98, -1.35) * mm, "end": v(6.99, -1.35) * mm});
            skLineSegment(sketch, "E1004", {"start": v(6.99, -1.35) * mm, "end": v(7, -1.34) * mm});
            skLineSegment(sketch, "E1005", {"start": v(7, -1.34) * mm, "end": v(7.02, -1.34) * mm});
            skLineSegment(sketch, "E1006", {"start": v(7.02, -1.34) * mm, "end": v(7.03, -1.34) * mm});
            skLineSegment(sketch, "E1007", {"start": v(7.03, -1.34) * mm, "end": v(7.05, -1.34) * mm});
            skLineSegment(sketch, "E1008", {"start": v(7.05, -1.34) * mm, "end": v(7.06, -1.34) * mm});
            skLineSegment(sketch, "E1009", {"start": v(7.06, -1.34) * mm, "end": v(7.08, -1.34) * mm});
            skLineSegment(sketch, "E1010", {"start": v(7.08, -1.34) * mm, "end": v(7.1, -1.34) * mm});
            skLineSegment(sketch, "E1011", {"start": v(7.1, -1.34) * mm, "end": v(7.11, -1.34) * mm});
            skLineSegment(sketch, "E1012", {"start": v(7.11, -1.34) * mm, "end": v(7.13, -1.34) * mm});
            skLineSegment(sketch, "E1013", {"start": v(7.13, -1.34) * mm, "end": v(7.15, -1.33) * mm});
            skLineSegment(sketch, "E1014", {"start": v(7.15, -1.33) * mm, "end": v(7.16, -1.33) * mm});
            skLineSegment(sketch, "E1015", {"start": v(7.16, -1.33) * mm, "end": v(7.18, -1.33) * mm});
            skLineSegment(sketch, "E1016", {"start": v(7.18, -1.33) * mm, "end": v(7.2, -1.33) * mm});
            skLineSegment(sketch, "E1017", {"start": v(7.2, -1.33) * mm, "end": v(7.22, -1.32) * mm});
            skLineSegment(sketch, "E1018", {"start": v(7.22, -1.32) * mm, "end": v(7.24, -1.32) * mm});
            skLineSegment(sketch, "E1019", {"start": v(7.24, -1.32) * mm, "end": v(7.26, -1.32) * mm});
            skLineSegment(sketch, "E1020", {"start": v(7.26, -1.32) * mm, "end": v(7.29, -1.31) * mm});
            skLineSegment(sketch, "E1021", {"start": v(7.29, -1.31) * mm, "end": v(7.3, -1.31) * mm});
            skLineSegment(sketch, "E1022", {"start": v(7.3, -1.31) * mm, "end": v(7.33, -1.3) * mm});
            skLineSegment(sketch, "E1023", {"start": v(7.33, -1.3) * mm, "end": v(7.35, -1.3) * mm});
            skLineSegment(sketch, "E1024", {"start": v(7.35, -1.3) * mm, "end": v(7.38, -1.3) * mm});
            skLineSegment(sketch, "E1025", {"start": v(7.38, -1.3) * mm, "end": v(7.4, -1.3) * mm});
            skLineSegment(sketch, "E1026", {"start": v(7.4, -1.3) * mm, "end": v(7.42, -1.29) * mm});
            skLineSegment(sketch, "E1027", {"start": v(7.42, -1.29) * mm, "end": v(7.45, -1.28) * mm});
            skLineSegment(sketch, "E1028", {"start": v(7.45, -1.28) * mm, "end": v(7.47, -1.27) * mm});
            skLineSegment(sketch, "E1029", {"start": v(7.47, -1.27) * mm, "end": v(7.5, -1.27) * mm});
            skLineSegment(sketch, "E1030", {"start": v(7.5, -1.27) * mm, "end": v(7.52, -1.26) * mm});
            skLineSegment(sketch, "E1031", {"start": v(7.52, -1.26) * mm, "end": v(7.55, -1.25) * mm});
            skLineSegment(sketch, "E1032", {"start": v(7.55, -1.25) * mm, "end": v(7.58, -1.25) * mm});
            skLineSegment(sketch, "E1033", {"start": v(7.58, -1.25) * mm, "end": v(7.6, -1.24) * mm});
            skLineSegment(sketch, "E1034", {"start": v(7.6, -1.24) * mm, "end": v(7.63, -1.23) * mm});
            skLineSegment(sketch, "E1035", {"start": v(7.63, -1.23) * mm, "end": v(7.66, -1.22) * mm});
            skLineSegment(sketch, "E1036", {"start": v(7.66, -1.22) * mm, "end": v(7.69, -1.21) * mm});
            skLineSegment(sketch, "E1037", {"start": v(7.69, -1.21) * mm, "end": v(7.72, -1.2) * mm});
            skLineSegment(sketch, "E1038", {"start": v(7.72, -1.2) * mm, "end": v(7.75, -1.2) * mm});
            skLineSegment(sketch, "E1039", {"start": v(7.75, -1.2) * mm, "end": v(7.78, -1.18) * mm});
            skLineSegment(sketch, "E1040", {"start": v(7.78, -1.18) * mm, "end": v(7.8, -1.17) * mm});
            skLineSegment(sketch, "E1041", {"start": v(7.8, -1.17) * mm, "end": v(7.84, -1.16) * mm});
            skLineSegment(sketch, "E1042", {"start": v(7.84, -1.16) * mm, "end": v(7.87, -1.15) * mm});
            skArc(sketch, "E1043", {"start": v(7.87, -1.15) * mm, "mid": v(7.89, -1.02) * mm, "end": v(7.9, -0.89) * mm});
            skLineSegment(sketch, "E1044", {"start": v(6.87, -1.62) * mm, "end": v(6.87, -1.62) * mm});
            skLineSegment(sketch, "E1045", {"start": v(6.87, -1.62) * mm, "end": v(6.87, -1.63) * mm});
            skLineSegment(sketch, "E1046", {"start": v(6.87, -1.63) * mm, "end": v(6.87, -1.64) * mm});
            skLineSegment(sketch, "E1047", {"start": v(6.87, -1.64) * mm, "end": v(6.88, -1.65) * mm});
            skLineSegment(sketch, "E1048", {"start": v(6.88, -1.65) * mm, "end": v(6.89, -1.65) * mm});
            skLineSegment(sketch, "E1049", {"start": v(6.89, -1.65) * mm, "end": v(6.9, -1.66) * mm});
            skLineSegment(sketch, "E1050", {"start": v(6.9, -1.66) * mm, "end": v(6.91, -1.67) * mm});
            skLineSegment(sketch, "E1051", {"start": v(6.91, -1.67) * mm, "end": v(6.92, -1.67) * mm});
            skLineSegment(sketch, "E1052", {"start": v(6.92, -1.67) * mm, "end": v(6.93, -1.68) * mm});
            skLineSegment(sketch, "E1053", {"start": v(6.93, -1.68) * mm, "end": v(6.94, -1.68) * mm});
            skLineSegment(sketch, "E1054", {"start": v(6.94, -1.68) * mm, "end": v(6.96, -1.69) * mm});
            skLineSegment(sketch, "E1055", {"start": v(6.96, -1.69) * mm, "end": v(6.97, -1.7) * mm});
            skLineSegment(sketch, "E1056", {"start": v(6.97, -1.7) * mm, "end": v(6.98, -1.7) * mm});
            skLineSegment(sketch, "E1057", {"start": v(6.98, -1.7) * mm, "end": v(7, -1.71) * mm});
            skLineSegment(sketch, "E1058", {"start": v(7, -1.71) * mm, "end": v(7.01, -1.72) * mm});
            skLineSegment(sketch, "E1059", {"start": v(7.01, -1.72) * mm, "end": v(7.03, -1.73) * mm});
            skLineSegment(sketch, "E1060", {"start": v(7.03, -1.73) * mm, "end": v(7.04, -1.74) * mm});
            skLineSegment(sketch, "E1061", {"start": v(7.04, -1.74) * mm, "end": v(7.06, -1.75) * mm});
            skLineSegment(sketch, "E1062", {"start": v(7.06, -1.75) * mm, "end": v(7.07, -1.76) * mm});
            skLineSegment(sketch, "E1063", {"start": v(7.07, -1.76) * mm, "end": v(7.09, -1.77) * mm});
            skLineSegment(sketch, "E1064", {"start": v(7.09, -1.77) * mm, "end": v(7.1, -1.78) * mm});
            skLineSegment(sketch, "E1065", {"start": v(7.1, -1.78) * mm, "end": v(7.12, -1.79) * mm});
            skLineSegment(sketch, "E1066", {"start": v(7.12, -1.79) * mm, "end": v(7.14, -1.8) * mm});
            skLineSegment(sketch, "E1067", {"start": v(7.14, -1.8) * mm, "end": v(7.16, -1.8) * mm});
            skLineSegment(sketch, "E1068", {"start": v(7.16, -1.8) * mm, "end": v(7.18, -1.82) * mm});
            skLineSegment(sketch, "E1069", {"start": v(7.18, -1.82) * mm, "end": v(7.2, -1.83) * mm});
            skLineSegment(sketch, "E1070", {"start": v(7.2, -1.83) * mm, "end": v(7.21, -1.85) * mm});
            skLineSegment(sketch, "E1071", {"start": v(7.21, -1.85) * mm, "end": v(7.23, -1.86) * mm});
            skLineSegment(sketch, "E1072", {"start": v(7.23, -1.86) * mm, "end": v(7.25, -1.87) * mm});
            skLineSegment(sketch, "E1073", {"start": v(7.25, -1.87) * mm, "end": v(7.27, -1.89) * mm});
            skLineSegment(sketch, "E1074", {"start": v(7.27, -1.89) * mm, "end": v(7.3, -1.9) * mm});
            skLineSegment(sketch, "E1075", {"start": v(7.3, -1.9) * mm, "end": v(7.31, -1.92) * mm});
            skLineSegment(sketch, "E1076", {"start": v(7.31, -1.92) * mm, "end": v(7.33, -1.93) * mm});
            skLineSegment(sketch, "E1077", {"start": v(7.33, -1.93) * mm, "end": v(7.35, -1.95) * mm});
            skLineSegment(sketch, "E1078", {"start": v(7.35, -1.95) * mm, "end": v(7.37, -1.97) * mm});
            skLineSegment(sketch, "E1079", {"start": v(7.37, -1.97) * mm, "end": v(7.4, -1.99) * mm});
            skLineSegment(sketch, "E1080", {"start": v(7.4, -1.99) * mm, "end": v(7.42, -2) * mm});
            skLineSegment(sketch, "E1081", {"start": v(7.42, -2) * mm, "end": v(7.44, -2.02) * mm});
            skLineSegment(sketch, "E1082", {"start": v(7.44, -2.02) * mm, "end": v(7.46, -2.04) * mm});
            skLineSegment(sketch, "E1083", {"start": v(7.46, -2.04) * mm, "end": v(7.48, -2.06) * mm});
            skLineSegment(sketch, "E1084", {"start": v(7.48, -2.06) * mm, "end": v(7.5, -2.08) * mm});
            skLineSegment(sketch, "E1085", {"start": v(7.5, -2.08) * mm, "end": v(7.53, -2.1) * mm});
            skLineSegment(sketch, "E1086", {"start": v(7.53, -2.1) * mm, "end": v(7.55, -2.12) * mm});
            skLineSegment(sketch, "E1087", {"start": v(7.55, -2.12) * mm, "end": v(7.57, -2.14) * mm});
            skLineSegment(sketch, "E1088", {"start": v(7.57, -2.14) * mm, "end": v(7.6, -2.17) * mm});
            skLineSegment(sketch, "E1089", {"start": v(7.6, -2.17) * mm, "end": v(7.62, -2.19) * mm});
            skLineSegment(sketch, "E1090", {"start": v(7.62, -2.19) * mm, "end": v(7.64, -2.21) * mm});
            skLineSegment(sketch, "E1091", {"start": v(6.59, -2.52) * mm, "end": v(6.6, -2.52) * mm});
            skLineSegment(sketch, "E1092", {"start": v(6.6, -2.52) * mm, "end": v(6.6, -2.51) * mm});
            skLineSegment(sketch, "E1093", {"start": v(6.6, -2.51) * mm, "end": v(6.6, -2.5) * mm});
            skLineSegment(sketch, "E1094", {"start": v(6.6, -2.5) * mm, "end": v(6.62, -2.5) * mm});
            skLineSegment(sketch, "E1095", {"start": v(6.62, -2.5) * mm, "end": v(6.63, -2.5) * mm});
            skLineSegment(sketch, "E1096", {"start": v(6.63, -2.5) * mm, "end": v(6.64, -2.5) * mm});
            skLineSegment(sketch, "E1097", {"start": v(6.64, -2.5) * mm, "end": v(6.66, -2.5) * mm});
            skLineSegment(sketch, "E1098", {"start": v(6.66, -2.5) * mm, "end": v(6.66, -2.5) * mm});
            skLineSegment(sketch, "E1099", {"start": v(6.66, -2.5) * mm, "end": v(6.68, -2.5) * mm});
            skLineSegment(sketch, "E1100", {"start": v(6.68, -2.5) * mm, "end": v(6.7, -2.51) * mm});
            skLineSegment(sketch, "E1101", {"start": v(6.7, -2.51) * mm, "end": v(6.7, -2.51) * mm});
            skLineSegment(sketch, "E1102", {"start": v(6.7, -2.51) * mm, "end": v(6.72, -2.51) * mm});
            skLineSegment(sketch, "E1103", {"start": v(6.72, -2.51) * mm, "end": v(6.74, -2.52) * mm});
            skLineSegment(sketch, "E1104", {"start": v(6.74, -2.52) * mm, "end": v(6.75, -2.52) * mm});
            skLineSegment(sketch, "E1105", {"start": v(6.75, -2.52) * mm, "end": v(6.77, -2.52) * mm});
            skLineSegment(sketch, "E1106", {"start": v(6.77, -2.52) * mm, "end": v(6.78, -2.52) * mm});
            skLineSegment(sketch, "E1107", {"start": v(6.78, -2.52) * mm, "end": v(6.8, -2.52) * mm});
            skLineSegment(sketch, "E1108", {"start": v(6.8, -2.52) * mm, "end": v(6.82, -2.52) * mm});
            skLineSegment(sketch, "E1109", {"start": v(6.82, -2.52) * mm, "end": v(6.84, -2.52) * mm});
            skLineSegment(sketch, "E1110", {"start": v(6.84, -2.52) * mm, "end": v(6.86, -2.52) * mm});
            skLineSegment(sketch, "E1111", {"start": v(6.86, -2.52) * mm, "end": v(6.88, -2.53) * mm});
            skLineSegment(sketch, "E1112", {"start": v(6.88, -2.53) * mm, "end": v(6.9, -2.53) * mm});
            skLineSegment(sketch, "E1113", {"start": v(6.9, -2.53) * mm, "end": v(6.92, -2.53) * mm});
            skLineSegment(sketch, "E1114", {"start": v(6.92, -2.53) * mm, "end": v(6.94, -2.53) * mm});
            skLineSegment(sketch, "E1115", {"start": v(6.94, -2.53) * mm, "end": v(6.96, -2.53) * mm});
            skLineSegment(sketch, "E1116", {"start": v(6.96, -2.53) * mm, "end": v(6.98, -2.53) * mm});
            skLineSegment(sketch, "E1117", {"start": v(6.98, -2.53) * mm, "end": v(7, -2.53) * mm});
            skLineSegment(sketch, "E1118", {"start": v(7, -2.53) * mm, "end": v(7.03, -2.53) * mm});
            skLineSegment(sketch, "E1119", {"start": v(7.03, -2.53) * mm, "end": v(7.05, -2.52) * mm});
            skLineSegment(sketch, "E1120", {"start": v(7.05, -2.52) * mm, "end": v(7.08, -2.52) * mm});
            skLineSegment(sketch, "E1121", {"start": v(7.08, -2.52) * mm, "end": v(7.1, -2.52) * mm});
            skLineSegment(sketch, "E1122", {"start": v(7.1, -2.52) * mm, "end": v(7.13, -2.52) * mm});
            skLineSegment(sketch, "E1123", {"start": v(7.13, -2.52) * mm, "end": v(7.15, -2.52) * mm});
            skLineSegment(sketch, "E1124", {"start": v(7.15, -2.52) * mm, "end": v(7.18, -2.52) * mm});
            skLineSegment(sketch, "E1125", {"start": v(7.18, -2.52) * mm, "end": v(7.2, -2.52) * mm});
            skLineSegment(sketch, "E1126", {"start": v(7.2, -2.52) * mm, "end": v(7.23, -2.51) * mm});
            skLineSegment(sketch, "E1127", {"start": v(7.23, -2.51) * mm, "end": v(7.26, -2.5) * mm});
            skLineSegment(sketch, "E1128", {"start": v(7.26, -2.5) * mm, "end": v(7.29, -2.5) * mm});
            skLineSegment(sketch, "E1129", {"start": v(7.29, -2.5) * mm, "end": v(7.32, -2.5) * mm});
            skLineSegment(sketch, "E1130", {"start": v(7.32, -2.5) * mm, "end": v(7.35, -2.5) * mm});
            skLineSegment(sketch, "E1131", {"start": v(7.35, -2.5) * mm, "end": v(7.38, -2.5) * mm});
            skLineSegment(sketch, "E1132", {"start": v(7.38, -2.5) * mm, "end": v(7.4, -2.5) * mm});
            skLineSegment(sketch, "E1133", {"start": v(7.4, -2.5) * mm, "end": v(7.44, -2.49) * mm});
            skLineSegment(sketch, "E1134", {"start": v(7.44, -2.49) * mm, "end": v(7.47, -2.48) * mm});
            skLineSegment(sketch, "E1135", {"start": v(7.47, -2.48) * mm, "end": v(7.5, -2.48) * mm});
            skLineSegment(sketch, "E1136", {"start": v(7.5, -2.48) * mm, "end": v(7.53, -2.47) * mm});
            skLineSegment(sketch, "E1137", {"start": v(7.53, -2.47) * mm, "end": v(7.56, -2.46) * mm});
            skArc(sketch, "E1138", {"start": v(7.56, -2.46) * mm, "mid": v(7.6, -2.34) * mm, "end": v(7.64, -2.21) * mm});
            skLineSegment(sketch, "E1139", {"start": v(6.5, -2.76) * mm, "end": v(6.5, -2.76) * mm});
            skLineSegment(sketch, "E1140", {"start": v(6.5, -2.76) * mm, "end": v(6.5, -2.77) * mm});
            skLineSegment(sketch, "E1141", {"start": v(6.5, -2.77) * mm, "end": v(6.5, -2.78) * mm});
            skLineSegment(sketch, "E1142", {"start": v(6.5, -2.78) * mm, "end": v(6.5, -2.78) * mm});
            skLineSegment(sketch, "E1143", {"start": v(6.5, -2.78) * mm, "end": v(6.51, -2.8) * mm});
            skLineSegment(sketch, "E1144", {"start": v(6.51, -2.8) * mm, "end": v(6.52, -2.8) * mm});
            skLineSegment(sketch, "E1145", {"start": v(6.52, -2.8) * mm, "end": v(6.53, -2.81) * mm});
            skLineSegment(sketch, "E1146", {"start": v(6.53, -2.81) * mm, "end": v(6.54, -2.82) * mm});
            skLineSegment(sketch, "E1147", {"start": v(6.54, -2.82) * mm, "end": v(6.55, -2.82) * mm});
            skLineSegment(sketch, "E1148", {"start": v(6.55, -2.82) * mm, "end": v(6.56, -2.83) * mm});
            skLineSegment(sketch, "E1149", {"start": v(6.56, -2.83) * mm, "end": v(6.57, -2.84) * mm});
            skLineSegment(sketch, "E1150", {"start": v(6.57, -2.84) * mm, "end": v(6.58, -2.85) * mm});
            skLineSegment(sketch, "E1151", {"start": v(6.58, -2.85) * mm, "end": v(6.6, -2.86) * mm});
            skLineSegment(sketch, "E1152", {"start": v(6.6, -2.86) * mm, "end": v(6.6, -2.87) * mm});
            skLineSegment(sketch, "E1153", {"start": v(6.6, -2.87) * mm, "end": v(6.62, -2.88) * mm});
            skLineSegment(sketch, "E1154", {"start": v(6.62, -2.88) * mm, "end": v(6.64, -2.9) * mm});
            skLineSegment(sketch, "E1155", {"start": v(6.64, -2.9) * mm, "end": v(6.65, -2.9) * mm});
            skLineSegment(sketch, "E1156", {"start": v(6.65, -2.9) * mm, "end": v(6.66, -2.91) * mm});
            skLineSegment(sketch, "E1157", {"start": v(6.66, -2.91) * mm, "end": v(6.68, -2.93) * mm});
            skLineSegment(sketch, "E1158", {"start": v(6.68, -2.93) * mm, "end": v(6.7, -2.94) * mm});
            skLineSegment(sketch, "E1159", {"start": v(6.7, -2.94) * mm, "end": v(6.7, -2.95) * mm});
            skLineSegment(sketch, "E1160", {"start": v(6.7, -2.95) * mm, "end": v(6.72, -2.96) * mm});
            skLineSegment(sketch, "E1161", {"start": v(6.72, -2.96) * mm, "end": v(6.74, -2.98) * mm});
            skLineSegment(sketch, "E1162", {"start": v(6.74, -2.98) * mm, "end": v(6.75, -3) * mm});
            skLineSegment(sketch, "E1163", {"start": v(6.75, -3) * mm, "end": v(6.77, -3) * mm});
            skLineSegment(sketch, "E1164", {"start": v(6.77, -3) * mm, "end": v(6.78, -3.02) * mm});
            skLineSegment(sketch, "E1165", {"start": v(6.78, -3.02) * mm, "end": v(6.8, -3.04) * mm});
            skLineSegment(sketch, "E1166", {"start": v(6.8, -3.04) * mm, "end": v(6.82, -3.06) * mm});
            skLineSegment(sketch, "E1167", {"start": v(6.82, -3.06) * mm, "end": v(6.83, -3.07) * mm});
            skLineSegment(sketch, "E1168", {"start": v(6.83, -3.07) * mm, "end": v(6.85, -3.1) * mm});
            skLineSegment(sketch, "E1169", {"start": v(6.85, -3.1) * mm, "end": v(6.87, -3.1) * mm});
            skLineSegment(sketch, "E1170", {"start": v(6.87, -3.1) * mm, "end": v(6.88, -3.13) * mm});
            skLineSegment(sketch, "E1171", {"start": v(6.88, -3.13) * mm, "end": v(6.9, -3.15) * mm});
            skLineSegment(sketch, "E1172", {"start": v(6.9, -3.15) * mm, "end": v(6.92, -3.17) * mm});
            skLineSegment(sketch, "E1173", {"start": v(6.92, -3.17) * mm, "end": v(6.94, -3.19) * mm});
            skLineSegment(sketch, "E1174", {"start": v(6.94, -3.19) * mm, "end": v(6.95, -3.2) * mm});
            skLineSegment(sketch, "E1175", {"start": v(6.95, -3.2) * mm, "end": v(6.97, -3.23) * mm});
            skLineSegment(sketch, "E1176", {"start": v(6.97, -3.23) * mm, "end": v(6.99, -3.25) * mm});
            skLineSegment(sketch, "E1177", {"start": v(6.99, -3.25) * mm, "end": v(7, -3.27) * mm});
            skLineSegment(sketch, "E1178", {"start": v(7, -3.27) * mm, "end": v(7.03, -3.3) * mm});
            skLineSegment(sketch, "E1179", {"start": v(7.03, -3.3) * mm, "end": v(7.05, -3.32) * mm});
            skLineSegment(sketch, "E1180", {"start": v(7.05, -3.32) * mm, "end": v(7.06, -3.34) * mm});
            skLineSegment(sketch, "E1181", {"start": v(7.06, -3.34) * mm, "end": v(7.08, -3.37) * mm});
            skLineSegment(sketch, "E1182", {"start": v(7.08, -3.37) * mm, "end": v(7.1, -3.4) * mm});
            skLineSegment(sketch, "E1183", {"start": v(7.1, -3.4) * mm, "end": v(7.12, -3.42) * mm});
            skLineSegment(sketch, "E1184", {"start": v(7.12, -3.42) * mm, "end": v(7.14, -3.44) * mm});
            skLineSegment(sketch, "E1185", {"start": v(7.14, -3.44) * mm, "end": v(7.16, -3.47) * mm});
            skLineSegment(sketch, "E1186", {"start": v(6.07, -3.6) * mm, "end": v(6.07, -3.6) * mm});
            skLineSegment(sketch, "E1187", {"start": v(6.07, -3.6) * mm, "end": v(6.08, -3.6) * mm});
            skLineSegment(sketch, "E1188", {"start": v(6.08, -3.6) * mm, "end": v(6.09, -3.59) * mm});
            skLineSegment(sketch, "E1189", {"start": v(6.09, -3.59) * mm, "end": v(6.1, -3.59) * mm});
            skLineSegment(sketch, "E1190", {"start": v(6.1, -3.59) * mm, "end": v(6.11, -3.59) * mm});
            skLineSegment(sketch, "E1191", {"start": v(6.11, -3.59) * mm, "end": v(6.12, -3.6) * mm});
            skLineSegment(sketch, "E1192", {"start": v(6.12, -3.6) * mm, "end": v(6.14, -3.6) * mm});
            skLineSegment(sketch, "E1193", {"start": v(6.14, -3.6) * mm, "end": v(6.15, -3.6) * mm});
            skLineSegment(sketch, "E1194", {"start": v(6.15, -3.6) * mm, "end": v(6.16, -3.6) * mm});
            skLineSegment(sketch, "E1195", {"start": v(6.16, -3.6) * mm, "end": v(6.17, -3.6) * mm});
            skLineSegment(sketch, "E1196", {"start": v(6.17, -3.6) * mm, "end": v(6.19, -3.6) * mm});
            skLineSegment(sketch, "E1197", {"start": v(6.19, -3.6) * mm, "end": v(6.2, -3.61) * mm});
            skLineSegment(sketch, "E1198", {"start": v(6.2, -3.61) * mm, "end": v(6.21, -3.62) * mm});
            skLineSegment(sketch, "E1199", {"start": v(6.21, -3.62) * mm, "end": v(6.23, -3.62) * mm});
            skLineSegment(sketch, "E1200", {"start": v(6.23, -3.62) * mm, "end": v(6.25, -3.63) * mm});
            skLineSegment(sketch, "E1201", {"start": v(6.25, -3.63) * mm, "end": v(6.26, -3.63) * mm});
            skLineSegment(sketch, "E1202", {"start": v(6.26, -3.63) * mm, "end": v(6.28, -3.64) * mm});
            skLineSegment(sketch, "E1203", {"start": v(6.28, -3.64) * mm, "end": v(6.3, -3.64) * mm});
            skLineSegment(sketch, "E1204", {"start": v(6.3, -3.64) * mm, "end": v(6.31, -3.64) * mm});
            skLineSegment(sketch, "E1205", {"start": v(6.31, -3.64) * mm, "end": v(6.33, -3.65) * mm});
            skLineSegment(sketch, "E1206", {"start": v(6.33, -3.65) * mm, "end": v(6.35, -3.65) * mm});
            skLineSegment(sketch, "E1207", {"start": v(6.35, -3.65) * mm, "end": v(6.37, -3.66) * mm});
            skLineSegment(sketch, "E1208", {"start": v(6.37, -3.66) * mm, "end": v(6.4, -3.66) * mm});
            skLineSegment(sketch, "E1209", {"start": v(6.4, -3.66) * mm, "end": v(6.41, -3.66) * mm});
            skLineSegment(sketch, "E1210", {"start": v(6.41, -3.66) * mm, "end": v(6.43, -3.67) * mm});
            skLineSegment(sketch, "E1211", {"start": v(6.43, -3.67) * mm, "end": v(6.46, -3.67) * mm});
            skLineSegment(sketch, "E1212", {"start": v(6.46, -3.67) * mm, "end": v(6.48, -3.67) * mm});
            skLineSegment(sketch, "E1213", {"start": v(6.48, -3.67) * mm, "end": v(6.5, -3.68) * mm});
            skLineSegment(sketch, "E1214", {"start": v(6.5, -3.68) * mm, "end": v(6.53, -3.68) * mm});
            skLineSegment(sketch, "E1215", {"start": v(6.53, -3.68) * mm, "end": v(6.55, -3.68) * mm});
            skLineSegment(sketch, "E1216", {"start": v(6.55, -3.68) * mm, "end": v(6.57, -3.69) * mm});
            skLineSegment(sketch, "E1217", {"start": v(6.57, -3.69) * mm, "end": v(6.6, -3.69) * mm});
            skLineSegment(sketch, "E1218", {"start": v(6.6, -3.69) * mm, "end": v(6.62, -3.7) * mm});
            skLineSegment(sketch, "E1219", {"start": v(6.62, -3.7) * mm, "end": v(6.65, -3.7) * mm});
            skLineSegment(sketch, "E1220", {"start": v(6.65, -3.7) * mm, "end": v(6.68, -3.7) * mm});
            skLineSegment(sketch, "E1221", {"start": v(6.68, -3.7) * mm, "end": v(6.7, -3.7) * mm});
            skLineSegment(sketch, "E1222", {"start": v(6.7, -3.7) * mm, "end": v(6.73, -3.7) * mm});
            skLineSegment(sketch, "E1223", {"start": v(6.73, -3.7) * mm, "end": v(6.76, -3.7) * mm});
            skLineSegment(sketch, "E1224", {"start": v(6.76, -3.7) * mm, "end": v(6.8, -3.7) * mm});
            skLineSegment(sketch, "E1225", {"start": v(6.8, -3.7) * mm, "end": v(6.82, -3.7) * mm});
            skLineSegment(sketch, "E1226", {"start": v(6.82, -3.7) * mm, "end": v(6.85, -3.7) * mm});
            skLineSegment(sketch, "E1227", {"start": v(6.85, -3.7) * mm, "end": v(6.88, -3.7) * mm});
            skLineSegment(sketch, "E1228", {"start": v(6.88, -3.7) * mm, "end": v(6.91, -3.7) * mm});
            skLineSegment(sketch, "E1229", {"start": v(6.91, -3.7) * mm, "end": v(6.94, -3.7) * mm});
            skLineSegment(sketch, "E1230", {"start": v(6.94, -3.7) * mm, "end": v(6.97, -3.7) * mm});
            skLineSegment(sketch, "E1231", {"start": v(6.97, -3.7) * mm, "end": v(7, -3.7) * mm});
            skLineSegment(sketch, "E1232", {"start": v(7, -3.7) * mm, "end": v(7.04, -3.7) * mm});
            skArc(sketch, "E1233", {"start": v(7.04, -3.7) * mm, "mid": v(7.1, -3.59) * mm, "end": v(7.16, -3.47) * mm});
            skLineSegment(sketch, "E1234", {"start": v(5.94, -3.81) * mm, "end": v(5.94, -3.82) * mm});
            skLineSegment(sketch, "E1235", {"start": v(5.94, -3.82) * mm, "end": v(5.94, -3.83) * mm});
            skLineSegment(sketch, "E1236", {"start": v(5.94, -3.83) * mm, "end": v(5.94, -3.83) * mm});
            skLineSegment(sketch, "E1237", {"start": v(5.94, -3.83) * mm, "end": v(5.94, -3.84) * mm});
            skLineSegment(sketch, "E1238", {"start": v(5.94, -3.84) * mm, "end": v(5.95, -3.85) * mm});
            skLineSegment(sketch, "E1239", {"start": v(5.95, -3.85) * mm, "end": v(5.96, -3.86) * mm});
            skLineSegment(sketch, "E1240", {"start": v(5.96, -3.86) * mm, "end": v(5.97, -3.88) * mm});
            skLineSegment(sketch, "E1241", {"start": v(5.97, -3.88) * mm, "end": v(5.97, -3.88) * mm});
            skLineSegment(sketch, "E1242", {"start": v(5.97, -3.88) * mm, "end": v(5.98, -3.9) * mm});
            skLineSegment(sketch, "E1243", {"start": v(5.98, -3.9) * mm, "end": v(5.99, -3.9) * mm});
            skLineSegment(sketch, "E1244", {"start": v(5.99, -3.9) * mm, "end": v(6, -3.91) * mm});
            skLineSegment(sketch, "E1245", {"start": v(6, -3.91) * mm, "end": v(6, -3.92) * mm});
            skLineSegment(sketch, "E1246", {"start": v(6, -3.92) * mm, "end": v(6.02, -3.93) * mm});
            skLineSegment(sketch, "E1247", {"start": v(6.02, -3.93) * mm, "end": v(6.03, -3.95) * mm});
            skLineSegment(sketch, "E1248", {"start": v(6.03, -3.95) * mm, "end": v(6.04, -3.96) * mm});
            skLineSegment(sketch, "E1249", {"start": v(6.04, -3.96) * mm, "end": v(6.05, -3.97) * mm});
            skLineSegment(sketch, "E1250", {"start": v(6.05, -3.97) * mm, "end": v(6.06, -3.98) * mm});
            skLineSegment(sketch, "E1251", {"start": v(6.06, -3.98) * mm, "end": v(6.08, -4) * mm});
            skLineSegment(sketch, "E1252", {"start": v(6.08, -4) * mm, "end": v(6.09, -4.01) * mm});
            skLineSegment(sketch, "E1253", {"start": v(6.09, -4.01) * mm, "end": v(6.1, -4.03) * mm});
            skLineSegment(sketch, "E1254", {"start": v(6.1, -4.03) * mm, "end": v(6.11, -4.04) * mm});
            skLineSegment(sketch, "E1255", {"start": v(6.11, -4.04) * mm, "end": v(6.12, -4.06) * mm});
            skLineSegment(sketch, "E1256", {"start": v(6.12, -4.06) * mm, "end": v(6.14, -4.07) * mm});
            skLineSegment(sketch, "E1257", {"start": v(6.14, -4.07) * mm, "end": v(6.15, -4.1) * mm});
            skLineSegment(sketch, "E1258", {"start": v(6.15, -4.1) * mm, "end": v(6.16, -4.1) * mm});
            skLineSegment(sketch, "E1259", {"start": v(6.16, -4.1) * mm, "end": v(6.18, -4.13) * mm});
            skLineSegment(sketch, "E1260", {"start": v(6.18, -4.13) * mm, "end": v(6.19, -4.14) * mm});
            skLineSegment(sketch, "E1261", {"start": v(6.19, -4.14) * mm, "end": v(6.2, -4.16) * mm});
            skLineSegment(sketch, "E1262", {"start": v(6.2, -4.16) * mm, "end": v(6.22, -4.18) * mm});
            skLineSegment(sketch, "E1263", {"start": v(6.22, -4.18) * mm, "end": v(6.23, -4.2) * mm});
            skLineSegment(sketch, "E1264", {"start": v(6.23, -4.2) * mm, "end": v(6.24, -4.22) * mm});
            skLineSegment(sketch, "E1265", {"start": v(6.24, -4.22) * mm, "end": v(6.26, -4.25) * mm});
            skLineSegment(sketch, "E1266", {"start": v(6.26, -4.25) * mm, "end": v(6.27, -4.27) * mm});
            skLineSegment(sketch, "E1267", {"start": v(6.27, -4.27) * mm, "end": v(6.28, -4.29) * mm});
            skLineSegment(sketch, "E1268", {"start": v(6.28, -4.29) * mm, "end": v(6.3, -4.31) * mm});
            skLineSegment(sketch, "E1269", {"start": v(6.3, -4.31) * mm, "end": v(6.31, -4.34) * mm});
            skLineSegment(sketch, "E1270", {"start": v(6.31, -4.34) * mm, "end": v(6.33, -4.36) * mm});
            skLineSegment(sketch, "E1271", {"start": v(6.33, -4.36) * mm, "end": v(6.34, -4.38) * mm});
            skLineSegment(sketch, "E1272", {"start": v(6.34, -4.38) * mm, "end": v(6.36, -4.4) * mm});
            skLineSegment(sketch, "E1273", {"start": v(6.36, -4.4) * mm, "end": v(6.37, -4.43) * mm});
            skLineSegment(sketch, "E1274", {"start": v(6.37, -4.43) * mm, "end": v(6.38, -4.46) * mm});
            skLineSegment(sketch, "E1275", {"start": v(6.38, -4.46) * mm, "end": v(6.4, -4.49) * mm});
            skLineSegment(sketch, "E1276", {"start": v(6.4, -4.49) * mm, "end": v(6.41, -4.52) * mm});
            skLineSegment(sketch, "E1277", {"start": v(6.41, -4.52) * mm, "end": v(6.43, -4.54) * mm});
            skLineSegment(sketch, "E1278", {"start": v(6.43, -4.54) * mm, "end": v(6.44, -4.57) * mm});
            skLineSegment(sketch, "E1279", {"start": v(6.44, -4.57) * mm, "end": v(6.46, -4.6) * mm});
            skLineSegment(sketch, "E1280", {"start": v(6.46, -4.6) * mm, "end": v(6.47, -4.63) * mm});
            skLineSegment(sketch, "E1281", {"start": v(5.38, -4.57) * mm, "end": v(5.38, -4.57) * mm});
            skLineSegment(sketch, "E1282", {"start": v(5.38, -4.57) * mm, "end": v(5.39, -4.57) * mm});
            skLineSegment(sketch, "E1283", {"start": v(5.39, -4.57) * mm, "end": v(5.4, -4.57) * mm});
            skLineSegment(sketch, "E1284", {"start": v(5.4, -4.57) * mm, "end": v(5.4, -4.57) * mm});
            skLineSegment(sketch, "E1285", {"start": v(5.4, -4.57) * mm, "end": v(5.42, -4.57) * mm});
            skLineSegment(sketch, "E1286", {"start": v(5.42, -4.57) * mm, "end": v(5.43, -4.58) * mm});
            skLineSegment(sketch, "E1287", {"start": v(5.43, -4.58) * mm, "end": v(5.44, -4.58) * mm});
            skLineSegment(sketch, "E1288", {"start": v(5.44, -4.58) * mm, "end": v(5.45, -4.58) * mm});
            skLineSegment(sketch, "E1289", {"start": v(5.45, -4.58) * mm, "end": v(5.46, -4.6) * mm});
            skLineSegment(sketch, "E1290", {"start": v(5.46, -4.6) * mm, "end": v(5.47, -4.6) * mm});
            skLineSegment(sketch, "E1291", {"start": v(5.47, -4.6) * mm, "end": v(5.49, -4.6) * mm});
            skLineSegment(sketch, "E1292", {"start": v(5.49, -4.6) * mm, "end": v(5.5, -4.61) * mm});
            skLineSegment(sketch, "E1293", {"start": v(5.5, -4.61) * mm, "end": v(5.52, -4.62) * mm});
            skLineSegment(sketch, "E1294", {"start": v(5.52, -4.62) * mm, "end": v(5.53, -4.62) * mm});
            skLineSegment(sketch, "E1295", {"start": v(5.53, -4.62) * mm, "end": v(5.54, -4.63) * mm});
            skLineSegment(sketch, "E1296", {"start": v(5.54, -4.63) * mm, "end": v(5.56, -4.64) * mm});
            skLineSegment(sketch, "E1297", {"start": v(5.56, -4.64) * mm, "end": v(5.58, -4.64) * mm});
            skLineSegment(sketch, "E1298", {"start": v(5.58, -4.64) * mm, "end": v(5.6, -4.65) * mm});
            skLineSegment(sketch, "E1299", {"start": v(5.6, -4.65) * mm, "end": v(5.6, -4.66) * mm});
            skLineSegment(sketch, "E1300", {"start": v(5.6, -4.66) * mm, "end": v(5.63, -4.67) * mm});
            skLineSegment(sketch, "E1301", {"start": v(5.63, -4.67) * mm, "end": v(5.65, -4.67) * mm});
            skLineSegment(sketch, "E1302", {"start": v(5.65, -4.67) * mm, "end": v(5.66, -4.68) * mm});
            skLineSegment(sketch, "E1303", {"start": v(5.66, -4.68) * mm, "end": v(5.68, -4.69) * mm});
            skLineSegment(sketch, "E1304", {"start": v(5.68, -4.69) * mm, "end": v(5.7, -4.7) * mm});
            skLineSegment(sketch, "E1305", {"start": v(5.7, -4.7) * mm, "end": v(5.72, -4.7) * mm});
            skLineSegment(sketch, "E1306", {"start": v(5.72, -4.7) * mm, "end": v(5.74, -4.7) * mm});
            skLineSegment(sketch, "E1307", {"start": v(5.74, -4.7) * mm, "end": v(5.77, -4.72) * mm});
            skLineSegment(sketch, "E1308", {"start": v(5.77, -4.72) * mm, "end": v(5.79, -4.72) * mm});
            skLineSegment(sketch, "E1309", {"start": v(5.79, -4.72) * mm, "end": v(5.81, -4.73) * mm});
            skLineSegment(sketch, "E1310", {"start": v(5.81, -4.73) * mm, "end": v(5.83, -4.74) * mm});
            skLineSegment(sketch, "E1311", {"start": v(5.83, -4.74) * mm, "end": v(5.86, -4.74) * mm});
            skLineSegment(sketch, "E1312", {"start": v(5.86, -4.74) * mm, "end": v(5.88, -4.75) * mm});
            skLineSegment(sketch, "E1313", {"start": v(5.88, -4.75) * mm, "end": v(5.9, -4.76) * mm});
            skLineSegment(sketch, "E1314", {"start": v(5.9, -4.76) * mm, "end": v(5.93, -4.77) * mm});
            skLineSegment(sketch, "E1315", {"start": v(5.93, -4.77) * mm, "end": v(5.96, -4.77) * mm});
            skLineSegment(sketch, "E1316", {"start": v(5.96, -4.77) * mm, "end": v(5.99, -4.78) * mm});
            skLineSegment(sketch, "E1317", {"start": v(5.99, -4.78) * mm, "end": v(6.01, -4.79) * mm});
            skLineSegment(sketch, "E1318", {"start": v(6.01, -4.79) * mm, "end": v(6.04, -4.8) * mm});
            skLineSegment(sketch, "E1319", {"start": v(6.04, -4.8) * mm, "end": v(6.07, -4.8) * mm});
            skLineSegment(sketch, "E1320", {"start": v(6.07, -4.8) * mm, "end": v(6.1, -4.8) * mm});
            skLineSegment(sketch, "E1321", {"start": v(6.1, -4.8) * mm, "end": v(6.13, -4.81) * mm});
            skLineSegment(sketch, "E1322", {"start": v(6.13, -4.81) * mm, "end": v(6.16, -4.82) * mm});
            skLineSegment(sketch, "E1323", {"start": v(6.16, -4.82) * mm, "end": v(6.19, -4.82) * mm});
            skLineSegment(sketch, "E1324", {"start": v(6.19, -4.82) * mm, "end": v(6.22, -4.83) * mm});
            skLineSegment(sketch, "E1325", {"start": v(6.22, -4.83) * mm, "end": v(6.25, -4.83) * mm});
            skLineSegment(sketch, "E1326", {"start": v(6.25, -4.83) * mm, "end": v(6.28, -4.84) * mm});
            skLineSegment(sketch, "E1327", {"start": v(6.28, -4.84) * mm, "end": v(6.31, -4.84) * mm});
            skArc(sketch, "E1328", {"start": v(6.31, -4.84) * mm, "mid": v(6.4, -4.74) * mm, "end": v(6.47, -4.63) * mm});
            skLineSegment(sketch, "E1329", {"start": v(5.2, -4.76) * mm, "end": v(5.2, -4.77) * mm});
            skLineSegment(sketch, "E1330", {"start": v(5.2, -4.77) * mm, "end": v(5.2, -4.77) * mm});
            skLineSegment(sketch, "E1331", {"start": v(5.2, -4.77) * mm, "end": v(5.2, -4.78) * mm});
            skLineSegment(sketch, "E1332", {"start": v(5.2, -4.78) * mm, "end": v(5.2, -4.8) * mm});
            skLineSegment(sketch, "E1333", {"start": v(5.2, -4.8) * mm, "end": v(5.21, -4.8) * mm});
            skLineSegment(sketch, "E1334", {"start": v(5.21, -4.8) * mm, "end": v(5.22, -4.82) * mm});
            skLineSegment(sketch, "E1335", {"start": v(5.22, -4.82) * mm, "end": v(5.23, -4.83) * mm});
            skLineSegment(sketch, "E1336", {"start": v(5.23, -4.83) * mm, "end": v(5.23, -4.83) * mm});
            skLineSegment(sketch, "E1337", {"start": v(5.23, -4.83) * mm, "end": v(5.24, -4.85) * mm});
            skLineSegment(sketch, "E1338", {"start": v(5.24, -4.85) * mm, "end": v(5.25, -4.86) * mm});
            skLineSegment(sketch, "E1339", {"start": v(5.25, -4.86) * mm, "end": v(5.25, -4.87) * mm});
            skLineSegment(sketch, "E1340", {"start": v(5.25, -4.87) * mm, "end": v(5.26, -4.88) * mm});
            skLineSegment(sketch, "E1341", {"start": v(5.26, -4.88) * mm, "end": v(5.27, -4.9) * mm});
            skLineSegment(sketch, "E1342", {"start": v(5.27, -4.9) * mm, "end": v(5.28, -4.9) * mm});
            skLineSegment(sketch, "E1343", {"start": v(5.28, -4.9) * mm, "end": v(5.29, -4.92) * mm});
            skLineSegment(sketch, "E1344", {"start": v(5.29, -4.92) * mm, "end": v(5.3, -4.94) * mm});
            skLineSegment(sketch, "E1345", {"start": v(5.3, -4.94) * mm, "end": v(5.3, -4.95) * mm});
            skLineSegment(sketch, "E1346", {"start": v(5.3, -4.95) * mm, "end": v(5.31, -4.97) * mm});
            skLineSegment(sketch, "E1347", {"start": v(5.31, -4.97) * mm, "end": v(5.32, -4.98) * mm});
            skLineSegment(sketch, "E1348", {"start": v(5.32, -4.98) * mm, "end": v(5.33, -5) * mm});
            skLineSegment(sketch, "E1349", {"start": v(5.33, -5) * mm, "end": v(5.34, -5.02) * mm});
            skLineSegment(sketch, "E1350", {"start": v(5.34, -5.02) * mm, "end": v(5.35, -5.03) * mm});
            skLineSegment(sketch, "E1351", {"start": v(5.35, -5.03) * mm, "end": v(5.36, -5.05) * mm});
            skLineSegment(sketch, "E1352", {"start": v(5.36, -5.05) * mm, "end": v(5.37, -5.07) * mm});
            skLineSegment(sketch, "E1353", {"start": v(5.37, -5.07) * mm, "end": v(5.38, -5.1) * mm});
            skLineSegment(sketch, "E1354", {"start": v(5.38, -5.1) * mm, "end": v(5.4, -5.11) * mm});
            skLineSegment(sketch, "E1355", {"start": v(5.4, -5.11) * mm, "end": v(5.4, -5.13) * mm});
            skLineSegment(sketch, "E1356", {"start": v(5.4, -5.13) * mm, "end": v(5.41, -5.15) * mm});
            skLineSegment(sketch, "E1357", {"start": v(5.41, -5.15) * mm, "end": v(5.42, -5.17) * mm});
            skLineSegment(sketch, "E1358", {"start": v(5.42, -5.17) * mm, "end": v(5.43, -5.2) * mm});
            skLineSegment(sketch, "E1359", {"start": v(5.43, -5.2) * mm, "end": v(5.44, -5.22) * mm});
            skLineSegment(sketch, "E1360", {"start": v(5.44, -5.22) * mm, "end": v(5.45, -5.24) * mm});
            skLineSegment(sketch, "E1361", {"start": v(5.45, -5.24) * mm, "end": v(5.46, -5.27) * mm});
            skLineSegment(sketch, "E1362", {"start": v(5.46, -5.27) * mm, "end": v(5.47, -5.29) * mm});
            skLineSegment(sketch, "E1363", {"start": v(5.47, -5.29) * mm, "end": v(5.48, -5.31) * mm});
            skLineSegment(sketch, "E1364", {"start": v(5.48, -5.31) * mm, "end": v(5.5, -5.34) * mm});
            skLineSegment(sketch, "E1365", {"start": v(5.5, -5.34) * mm, "end": v(5.5, -5.37) * mm});
            skLineSegment(sketch, "E1366", {"start": v(5.5, -5.37) * mm, "end": v(5.51, -5.4) * mm});
            skLineSegment(sketch, "E1367", {"start": v(5.51, -5.4) * mm, "end": v(5.52, -5.42) * mm});
            skLineSegment(sketch, "E1368", {"start": v(5.52, -5.42) * mm, "end": v(5.53, -5.45) * mm});
            skLineSegment(sketch, "E1369", {"start": v(5.53, -5.45) * mm, "end": v(5.54, -5.48) * mm});
            skLineSegment(sketch, "E1370", {"start": v(5.54, -5.48) * mm, "end": v(5.55, -5.5) * mm});
            skLineSegment(sketch, "E1371", {"start": v(5.55, -5.5) * mm, "end": v(5.56, -5.53) * mm});
            skLineSegment(sketch, "E1372", {"start": v(5.56, -5.53) * mm, "end": v(5.57, -5.56) * mm});
            skLineSegment(sketch, "E1373", {"start": v(5.57, -5.56) * mm, "end": v(5.58, -5.6) * mm});
            skLineSegment(sketch, "E1374", {"start": v(5.58, -5.6) * mm, "end": v(5.59, -5.63) * mm});
            skLineSegment(sketch, "E1375", {"start": v(5.59, -5.63) * mm, "end": v(5.6, -5.66) * mm});
            skLineSegment(sketch, "E1376", {"start": v(4.53, -5.42) * mm, "end": v(4.53, -5.41) * mm});
            skLineSegment(sketch, "E1377", {"start": v(4.53, -5.41) * mm, "end": v(4.54, -5.41) * mm});
            skLineSegment(sketch, "E1378", {"start": v(4.54, -5.41) * mm, "end": v(4.55, -5.41) * mm});
            skLineSegment(sketch, "E1379", {"start": v(4.55, -5.41) * mm, "end": v(4.56, -5.42) * mm});
            skLineSegment(sketch, "E1380", {"start": v(4.56, -5.42) * mm, "end": v(4.57, -5.42) * mm});
            skLineSegment(sketch, "E1381", {"start": v(4.57, -5.42) * mm, "end": v(4.58, -5.43) * mm});
            skLineSegment(sketch, "E1382", {"start": v(4.58, -5.43) * mm, "end": v(4.6, -5.44) * mm});
            skLineSegment(sketch, "E1383", {"start": v(4.6, -5.44) * mm, "end": v(4.6, -5.44) * mm});
            skLineSegment(sketch, "E1384", {"start": v(4.6, -5.44) * mm, "end": v(4.6, -5.45) * mm});
            skLineSegment(sketch, "E1385", {"start": v(4.6, -5.45) * mm, "end": v(4.62, -5.46) * mm});
            skLineSegment(sketch, "E1386", {"start": v(4.62, -5.46) * mm, "end": v(4.63, -5.46) * mm});
            skLineSegment(sketch, "E1387", {"start": v(4.63, -5.46) * mm, "end": v(4.64, -5.47) * mm});
            skLineSegment(sketch, "E1388", {"start": v(4.64, -5.47) * mm, "end": v(4.66, -5.48) * mm});
            skLineSegment(sketch, "E1389", {"start": v(4.66, -5.48) * mm, "end": v(4.67, -5.5) * mm});
            skLineSegment(sketch, "E1390", {"start": v(4.67, -5.5) * mm, "end": v(4.68, -5.5) * mm});
            skLineSegment(sketch, "E1391", {"start": v(4.68, -5.5) * mm, "end": v(4.7, -5.51) * mm});
            skLineSegment(sketch, "E1392", {"start": v(4.7, -5.51) * mm, "end": v(4.71, -5.52) * mm});
            skLineSegment(sketch, "E1393", {"start": v(4.71, -5.52) * mm, "end": v(4.73, -5.53) * mm});
            skLineSegment(sketch, "E1394", {"start": v(4.73, -5.53) * mm, "end": v(4.74, -5.54) * mm});
            skLineSegment(sketch, "E1395", {"start": v(4.74, -5.54) * mm, "end": v(4.76, -5.55) * mm});
            skLineSegment(sketch, "E1396", {"start": v(4.76, -5.55) * mm, "end": v(4.78, -5.56) * mm});
            skLineSegment(sketch, "E1397", {"start": v(4.78, -5.56) * mm, "end": v(4.8, -5.57) * mm});
            skLineSegment(sketch, "E1398", {"start": v(4.8, -5.57) * mm, "end": v(4.81, -5.58) * mm});
            skLineSegment(sketch, "E1399", {"start": v(4.81, -5.58) * mm, "end": v(4.83, -5.6) * mm});
            skLineSegment(sketch, "E1400", {"start": v(4.83, -5.6) * mm, "end": v(4.85, -5.6) * mm});
            skLineSegment(sketch, "E1401", {"start": v(4.85, -5.6) * mm, "end": v(4.87, -5.61) * mm});
            skLineSegment(sketch, "E1402", {"start": v(4.87, -5.61) * mm, "end": v(4.89, -5.62) * mm});
            skLineSegment(sketch, "E1403", {"start": v(4.89, -5.62) * mm, "end": v(4.9, -5.63) * mm});
            skLineSegment(sketch, "E1404", {"start": v(4.9, -5.63) * mm, "end": v(4.93, -5.64) * mm});
            skLineSegment(sketch, "E1405", {"start": v(4.93, -5.64) * mm, "end": v(4.95, -5.66) * mm});
            skLineSegment(sketch, "E1406", {"start": v(4.95, -5.66) * mm, "end": v(4.97, -5.67) * mm});
            skLineSegment(sketch, "E1407", {"start": v(4.97, -5.67) * mm, "end": v(5, -5.68) * mm});
            skLineSegment(sketch, "E1408", {"start": v(5, -5.68) * mm, "end": v(5.02, -5.69) * mm});
            skLineSegment(sketch, "E1409", {"start": v(5.02, -5.69) * mm, "end": v(5.04, -5.7) * mm});
            skLineSegment(sketch, "E1410", {"start": v(5.04, -5.7) * mm, "end": v(5.07, -5.71) * mm});
            skLineSegment(sketch, "E1411", {"start": v(5.07, -5.71) * mm, "end": v(5.1, -5.72) * mm});
            skLineSegment(sketch, "E1412", {"start": v(5.1, -5.72) * mm, "end": v(5.12, -5.73) * mm});
            skLineSegment(sketch, "E1413", {"start": v(5.12, -5.73) * mm, "end": v(5.14, -5.74) * mm});
            skLineSegment(sketch, "E1414", {"start": v(5.14, -5.74) * mm, "end": v(5.17, -5.75) * mm});
            skLineSegment(sketch, "E1415", {"start": v(5.17, -5.75) * mm, "end": v(5.2, -5.77) * mm});
            skLineSegment(sketch, "E1416", {"start": v(5.2, -5.77) * mm, "end": v(5.23, -5.78) * mm});
            skLineSegment(sketch, "E1417", {"start": v(5.23, -5.78) * mm, "end": v(5.26, -5.79) * mm});
            skLineSegment(sketch, "E1418", {"start": v(5.26, -5.79) * mm, "end": v(5.28, -5.8) * mm});
            skLineSegment(sketch, "E1419", {"start": v(5.28, -5.8) * mm, "end": v(5.31, -5.8) * mm});
            skLineSegment(sketch, "E1420", {"start": v(5.31, -5.8) * mm, "end": v(5.34, -5.82) * mm});
            skLineSegment(sketch, "E1421", {"start": v(5.34, -5.82) * mm, "end": v(5.38, -5.83) * mm});
            skLineSegment(sketch, "E1422", {"start": v(5.38, -5.83) * mm, "end": v(5.4, -5.84) * mm});
            skArc(sketch, "E1423", {"start": v(5.4, -5.84) * mm, "mid": v(5.5, -5.75) * mm, "end": v(5.6, -5.66) * mm});
            skLineSegment(sketch, "E1424", {"start": v(4.33, -5.57) * mm, "end": v(4.33, -5.58) * mm});
            skLineSegment(sketch, "E1425", {"start": v(4.33, -5.58) * mm, "end": v(4.32, -5.59) * mm});
            skLineSegment(sketch, "E1426", {"start": v(4.32, -5.59) * mm, "end": v(4.32, -5.6) * mm});
            skLineSegment(sketch, "E1427", {"start": v(4.32, -5.6) * mm, "end": v(4.32, -5.6) * mm});
            skLineSegment(sketch, "E1428", {"start": v(4.32, -5.6) * mm, "end": v(4.33, -5.62) * mm});
            skLineSegment(sketch, "E1429", {"start": v(4.33, -5.62) * mm, "end": v(4.33, -5.63) * mm});
            skLineSegment(sketch, "E1430", {"start": v(4.33, -5.63) * mm, "end": v(4.34, -5.64) * mm});
            skLineSegment(sketch, "E1431", {"start": v(4.34, -5.64) * mm, "end": v(4.34, -5.65) * mm});
            skLineSegment(sketch, "E1432", {"start": v(4.34, -5.65) * mm, "end": v(4.35, -5.66) * mm});
            skLineSegment(sketch, "E1433", {"start": v(4.35, -5.66) * mm, "end": v(4.35, -5.67) * mm});
            skLineSegment(sketch, "E1434", {"start": v(4.35, -5.67) * mm, "end": v(4.36, -5.69) * mm});
            skLineSegment(sketch, "E1435", {"start": v(4.36, -5.69) * mm, "end": v(4.36, -5.7) * mm});
            skLineSegment(sketch, "E1436", {"start": v(4.36, -5.7) * mm, "end": v(4.37, -5.72) * mm});
            skLineSegment(sketch, "E1437", {"start": v(4.37, -5.72) * mm, "end": v(4.38, -5.73) * mm});
            skLineSegment(sketch, "E1438", {"start": v(4.38, -5.73) * mm, "end": v(4.38, -5.74) * mm});
            skLineSegment(sketch, "E1439", {"start": v(4.38, -5.74) * mm, "end": v(4.39, -5.76) * mm});
            skLineSegment(sketch, "E1440", {"start": v(4.39, -5.76) * mm, "end": v(4.4, -5.78) * mm});
            skLineSegment(sketch, "E1441", {"start": v(4.4, -5.78) * mm, "end": v(4.4, -5.8) * mm});
            skLineSegment(sketch, "E1442", {"start": v(4.4, -5.8) * mm, "end": v(4.4, -5.81) * mm});
            skLineSegment(sketch, "E1443", {"start": v(4.4, -5.81) * mm, "end": v(4.41, -5.83) * mm});
            skLineSegment(sketch, "E1444", {"start": v(4.41, -5.83) * mm, "end": v(4.42, -5.85) * mm});
            skLineSegment(sketch, "E1445", {"start": v(4.42, -5.85) * mm, "end": v(4.43, -5.87) * mm});
            skLineSegment(sketch, "E1446", {"start": v(4.43, -5.87) * mm, "end": v(4.43, -5.89) * mm});
            skLineSegment(sketch, "E1447", {"start": v(4.43, -5.89) * mm, "end": v(4.44, -5.9) * mm});
            skLineSegment(sketch, "E1448", {"start": v(4.44, -5.9) * mm, "end": v(4.45, -5.93) * mm});
            skLineSegment(sketch, "E1449", {"start": v(4.45, -5.93) * mm, "end": v(4.45, -5.95) * mm});
            skLineSegment(sketch, "E1450", {"start": v(4.45, -5.95) * mm, "end": v(4.46, -5.97) * mm});
            skLineSegment(sketch, "E1451", {"start": v(4.46, -5.97) * mm, "end": v(4.46, -6) * mm});
            skLineSegment(sketch, "E1452", {"start": v(4.46, -6) * mm, "end": v(4.47, -6.02) * mm});
            skLineSegment(sketch, "E1453", {"start": v(4.47, -6.02) * mm, "end": v(4.48, -6.04) * mm});
            skLineSegment(sketch, "E1454", {"start": v(4.48, -6.04) * mm, "end": v(4.48, -6.06) * mm});
            skLineSegment(sketch, "E1455", {"start": v(4.48, -6.06) * mm, "end": v(4.49, -6.09) * mm});
            skLineSegment(sketch, "E1456", {"start": v(4.49, -6.09) * mm, "end": v(4.5, -6.11) * mm});
            skLineSegment(sketch, "E1457", {"start": v(4.5, -6.11) * mm, "end": v(4.5, -6.14) * mm});
            skLineSegment(sketch, "E1458", {"start": v(4.5, -6.14) * mm, "end": v(4.5, -6.16) * mm});
            skLineSegment(sketch, "E1459", {"start": v(4.5, -6.16) * mm, "end": v(4.51, -6.2) * mm});
            skLineSegment(sketch, "E1460", {"start": v(4.51, -6.2) * mm, "end": v(4.52, -6.22) * mm});
            skLineSegment(sketch, "E1461", {"start": v(4.52, -6.22) * mm, "end": v(4.52, -6.25) * mm});
            skLineSegment(sketch, "E1462", {"start": v(4.52, -6.25) * mm, "end": v(4.53, -6.28) * mm});
            skLineSegment(sketch, "E1463", {"start": v(4.53, -6.28) * mm, "end": v(4.53, -6.3) * mm});
            skLineSegment(sketch, "E1464", {"start": v(4.53, -6.3) * mm, "end": v(4.54, -6.33) * mm});
            skLineSegment(sketch, "E1465", {"start": v(4.54, -6.33) * mm, "end": v(4.54, -6.36) * mm});
            skLineSegment(sketch, "E1466", {"start": v(4.54, -6.36) * mm, "end": v(4.55, -6.4) * mm});
            skLineSegment(sketch, "E1467", {"start": v(4.55, -6.4) * mm, "end": v(4.55, -6.43) * mm});
            skLineSegment(sketch, "E1468", {"start": v(4.55, -6.43) * mm, "end": v(4.55, -6.46) * mm});
            skLineSegment(sketch, "E1469", {"start": v(4.55, -6.46) * mm, "end": v(4.56, -6.49) * mm});
            skLineSegment(sketch, "E1470", {"start": v(4.56, -6.49) * mm, "end": v(4.56, -6.52) * mm});
            skLineSegment(sketch, "E1471", {"start": v(3.55, -6.1) * mm, "end": v(3.55, -6.1) * mm});
            skLineSegment(sketch, "E1472", {"start": v(3.55, -6.1) * mm, "end": v(3.56, -6.1) * mm});
            skLineSegment(sketch, "E1473", {"start": v(3.56, -6.1) * mm, "end": v(3.57, -6.1) * mm});
            skLineSegment(sketch, "E1474", {"start": v(3.57, -6.1) * mm, "end": v(3.58, -6.1) * mm});
            skLineSegment(sketch, "E1475", {"start": v(3.58, -6.1) * mm, "end": v(3.59, -6.11) * mm});
            skLineSegment(sketch, "E1476", {"start": v(3.59, -6.11) * mm, "end": v(3.6, -6.12) * mm});
            skLineSegment(sketch, "E1477", {"start": v(3.6, -6.12) * mm, "end": v(3.61, -6.13) * mm});
            skLineSegment(sketch, "E1478", {"start": v(3.61, -6.13) * mm, "end": v(3.62, -6.14) * mm});
            skLineSegment(sketch, "E1479", {"start": v(3.62, -6.14) * mm, "end": v(3.62, -6.15) * mm});
            skLineSegment(sketch, "E1480", {"start": v(3.62, -6.15) * mm, "end": v(3.63, -6.16) * mm});
            skLineSegment(sketch, "E1481", {"start": v(3.63, -6.16) * mm, "end": v(3.64, -6.17) * mm});
            skLineSegment(sketch, "E1482", {"start": v(3.64, -6.17) * mm, "end": v(3.65, -6.18) * mm});
            skLineSegment(sketch, "E1483", {"start": v(3.65, -6.18) * mm, "end": v(3.67, -6.2) * mm});
            skLineSegment(sketch, "E1484", {"start": v(3.67, -6.2) * mm, "end": v(3.68, -6.2) * mm});
            skLineSegment(sketch, "E1485", {"start": v(3.68, -6.2) * mm, "end": v(3.69, -6.21) * mm});
            skLineSegment(sketch, "E1486", {"start": v(3.69, -6.21) * mm, "end": v(3.7, -6.23) * mm});
            skLineSegment(sketch, "E1487", {"start": v(3.7, -6.23) * mm, "end": v(3.71, -6.24) * mm});
            skLineSegment(sketch, "E1488", {"start": v(3.71, -6.24) * mm, "end": v(3.73, -6.25) * mm});
            skLineSegment(sketch, "E1489", {"start": v(3.73, -6.25) * mm, "end": v(3.74, -6.26) * mm});
            skLineSegment(sketch, "E1490", {"start": v(3.74, -6.26) * mm, "end": v(3.75, -6.27) * mm});
            skLineSegment(sketch, "E1491", {"start": v(3.75, -6.27) * mm, "end": v(3.77, -6.29) * mm});
            skLineSegment(sketch, "E1492", {"start": v(3.77, -6.29) * mm, "end": v(3.78, -6.3) * mm});
            skLineSegment(sketch, "E1493", {"start": v(3.78, -6.3) * mm, "end": v(3.8, -6.31) * mm});
            skLineSegment(sketch, "E1494", {"start": v(3.8, -6.31) * mm, "end": v(3.82, -6.33) * mm});
            skLineSegment(sketch, "E1495", {"start": v(3.82, -6.33) * mm, "end": v(3.83, -6.34) * mm});
            skLineSegment(sketch, "E1496", {"start": v(3.83, -6.34) * mm, "end": v(3.85, -6.35) * mm});
            skLineSegment(sketch, "E1497", {"start": v(3.85, -6.35) * mm, "end": v(3.87, -6.37) * mm});
            skLineSegment(sketch, "E1498", {"start": v(3.87, -6.37) * mm, "end": v(3.89, -6.38) * mm});
            skLineSegment(sketch, "E1499", {"start": v(3.89, -6.38) * mm, "end": v(3.9, -6.4) * mm});
            skLineSegment(sketch, "E1500", {"start": v(3.9, -6.4) * mm, "end": v(3.93, -6.41) * mm});
            skLineSegment(sketch, "E1501", {"start": v(3.93, -6.41) * mm, "end": v(3.95, -6.43) * mm});
            skLineSegment(sketch, "E1502", {"start": v(3.95, -6.43) * mm, "end": v(3.97, -6.44) * mm});
            skLineSegment(sketch, "E1503", {"start": v(3.97, -6.44) * mm, "end": v(3.99, -6.46) * mm});
            skLineSegment(sketch, "E1504", {"start": v(3.99, -6.46) * mm, "end": v(4, -6.47) * mm});
            skLineSegment(sketch, "E1505", {"start": v(4, -6.47) * mm, "end": v(4.03, -6.49) * mm});
            skLineSegment(sketch, "E1506", {"start": v(4.03, -6.49) * mm, "end": v(4.05, -6.5) * mm});
            skLineSegment(sketch, "E1507", {"start": v(4.05, -6.5) * mm, "end": v(4.08, -6.52) * mm});
            skLineSegment(sketch, "E1508", {"start": v(4.08, -6.52) * mm, "end": v(4.1, -6.53) * mm});
            skLineSegment(sketch, "E1509", {"start": v(4.1, -6.53) * mm, "end": v(4.13, -6.55) * mm});
            skLineSegment(sketch, "E1510", {"start": v(4.13, -6.55) * mm, "end": v(4.15, -6.56) * mm});
            skLineSegment(sketch, "E1511", {"start": v(4.15, -6.56) * mm, "end": v(4.18, -6.58) * mm});
            skLineSegment(sketch, "E1512", {"start": v(4.18, -6.58) * mm, "end": v(4.2, -6.6) * mm});
            skLineSegment(sketch, "E1513", {"start": v(4.2, -6.6) * mm, "end": v(4.23, -6.6) * mm});
            skLineSegment(sketch, "E1514", {"start": v(4.23, -6.6) * mm, "end": v(4.26, -6.62) * mm});
            skLineSegment(sketch, "E1515", {"start": v(4.26, -6.62) * mm, "end": v(4.29, -6.64) * mm});
            skLineSegment(sketch, "E1516", {"start": v(4.29, -6.64) * mm, "end": v(4.31, -6.65) * mm});
            skLineSegment(sketch, "E1517", {"start": v(4.31, -6.65) * mm, "end": v(4.34, -6.67) * mm});
            skArc(sketch, "E1518", {"start": v(4.34, -6.67) * mm, "mid": v(4.45, -6.6) * mm, "end": v(4.56, -6.52) * mm});
            skLineSegment(sketch, "E1519", {"start": v(3.33, -6.23) * mm, "end": v(3.32, -6.23) * mm});
            skLineSegment(sketch, "E1520", {"start": v(3.32, -6.23) * mm, "end": v(3.32, -6.24) * mm});
            skLineSegment(sketch, "E1521", {"start": v(3.32, -6.24) * mm, "end": v(3.32, -6.24) * mm});
            skLineSegment(sketch, "E1522", {"start": v(3.32, -6.24) * mm, "end": v(3.32, -6.25) * mm});
            skLineSegment(sketch, "E1523", {"start": v(3.32, -6.25) * mm, "end": v(3.32, -6.27) * mm});
            skLineSegment(sketch, "E1524", {"start": v(3.32, -6.27) * mm, "end": v(3.32, -6.28) * mm});
            skLineSegment(sketch, "E1525", {"start": v(3.32, -6.28) * mm, "end": v(3.32, -6.3) * mm});
            skLineSegment(sketch, "E1526", {"start": v(3.32, -6.3) * mm, "end": v(3.32, -6.3) * mm});
            skLineSegment(sketch, "E1527", {"start": v(3.32, -6.3) * mm, "end": v(3.33, -6.31) * mm});
            skLineSegment(sketch, "E1528", {"start": v(3.33, -6.31) * mm, "end": v(3.33, -6.33) * mm});
            skLineSegment(sketch, "E1529", {"start": v(3.33, -6.33) * mm, "end": v(3.33, -6.34) * mm});
            skLineSegment(sketch, "E1530", {"start": v(3.33, -6.34) * mm, "end": v(3.34, -6.36) * mm});
            skLineSegment(sketch, "E1531", {"start": v(3.34, -6.36) * mm, "end": v(3.34, -6.37) * mm});
            skLineSegment(sketch, "E1532", {"start": v(3.34, -6.37) * mm, "end": v(3.35, -6.39) * mm});
            skLineSegment(sketch, "E1533", {"start": v(3.35, -6.39) * mm, "end": v(3.35, -6.4) * mm});
            skLineSegment(sketch, "E1534", {"start": v(3.35, -6.4) * mm, "end": v(3.35, -6.42) * mm});
            skLineSegment(sketch, "E1535", {"start": v(3.35, -6.42) * mm, "end": v(3.36, -6.44) * mm});
            skLineSegment(sketch, "E1536", {"start": v(3.36, -6.44) * mm, "end": v(3.36, -6.45) * mm});
            skLineSegment(sketch, "E1537", {"start": v(3.36, -6.45) * mm, "end": v(3.36, -6.47) * mm});
            skLineSegment(sketch, "E1538", {"start": v(3.36, -6.47) * mm, "end": v(3.37, -6.5) * mm});
            skLineSegment(sketch, "E1539", {"start": v(3.37, -6.5) * mm, "end": v(3.37, -6.51) * mm});
            skLineSegment(sketch, "E1540", {"start": v(3.37, -6.51) * mm, "end": v(3.37, -6.53) * mm});
            skLineSegment(sketch, "E1541", {"start": v(3.37, -6.53) * mm, "end": v(3.38, -6.55) * mm});
            skLineSegment(sketch, "E1542", {"start": v(3.38, -6.55) * mm, "end": v(3.38, -6.57) * mm});
            skLineSegment(sketch, "E1543", {"start": v(3.38, -6.57) * mm, "end": v(3.38, -6.6) * mm});
            skLineSegment(sketch, "E1544", {"start": v(3.38, -6.6) * mm, "end": v(3.38, -6.62) * mm});
            skLineSegment(sketch, "E1545", {"start": v(3.38, -6.62) * mm, "end": v(3.39, -6.64) * mm});
            skLineSegment(sketch, "E1546", {"start": v(3.39, -6.64) * mm, "end": v(3.39, -6.66) * mm});
            skLineSegment(sketch, "E1547", {"start": v(3.39, -6.66) * mm, "end": v(3.4, -6.68) * mm});
            skLineSegment(sketch, "E1548", {"start": v(3.4, -6.68) * mm, "end": v(3.4, -6.7) * mm});
            skLineSegment(sketch, "E1549", {"start": v(3.4, -6.7) * mm, "end": v(3.4, -6.73) * mm});
            skLineSegment(sketch, "E1550", {"start": v(3.4, -6.73) * mm, "end": v(3.4, -6.76) * mm});
            skLineSegment(sketch, "E1551", {"start": v(3.4, -6.76) * mm, "end": v(3.4, -6.78) * mm});
            skLineSegment(sketch, "E1552", {"start": v(3.4, -6.78) * mm, "end": v(3.4, -6.81) * mm});
            skLineSegment(sketch, "E1553", {"start": v(3.4, -6.81) * mm, "end": v(3.4, -6.84) * mm});
            skLineSegment(sketch, "E1554", {"start": v(3.4, -6.84) * mm, "end": v(3.4, -6.86) * mm});
            skLineSegment(sketch, "E1555", {"start": v(3.4, -6.86) * mm, "end": v(3.4, -6.9) * mm});
            skLineSegment(sketch, "E1556", {"start": v(3.4, -6.9) * mm, "end": v(3.4, -6.92) * mm});
            skLineSegment(sketch, "E1557", {"start": v(3.4, -6.92) * mm, "end": v(3.4, -6.95) * mm});
            skLineSegment(sketch, "E1558", {"start": v(3.4, -6.95) * mm, "end": v(3.4, -6.98) * mm});
            skLineSegment(sketch, "E1559", {"start": v(3.4, -6.98) * mm, "end": v(3.4, -7) * mm});
            skLineSegment(sketch, "E1560", {"start": v(3.4, -7) * mm, "end": v(3.4, -7.04) * mm});
            skLineSegment(sketch, "E1561", {"start": v(3.4, -7.04) * mm, "end": v(3.4, -7.07) * mm});
            skLineSegment(sketch, "E1562", {"start": v(3.4, -7.07) * mm, "end": v(3.4, -7.1) * mm});
            skLineSegment(sketch, "E1563", {"start": v(3.4, -7.1) * mm, "end": v(3.4, -7.13) * mm});
            skLineSegment(sketch, "E1564", {"start": v(3.4, -7.13) * mm, "end": v(3.4, -7.17) * mm});
            skLineSegment(sketch, "E1565", {"start": v(3.4, -7.17) * mm, "end": v(3.4, -7.2) * mm});
            skLineSegment(sketch, "E1566", {"start": v(2.47, -6.62) * mm, "end": v(2.47, -6.61) * mm});
            skLineSegment(sketch, "E1567", {"start": v(2.47, -6.61) * mm, "end": v(2.48, -6.62) * mm});
            skLineSegment(sketch, "E1568", {"start": v(2.48, -6.62) * mm, "end": v(2.49, -6.62) * mm});
            skLineSegment(sketch, "E1569", {"start": v(2.49, -6.62) * mm, "end": v(2.5, -6.63) * mm});
            skLineSegment(sketch, "E1570", {"start": v(2.5, -6.63) * mm, "end": v(2.5, -6.63) * mm});
            skLineSegment(sketch, "E1571", {"start": v(2.5, -6.63) * mm, "end": v(2.51, -6.64) * mm});
            skLineSegment(sketch, "E1572", {"start": v(2.51, -6.64) * mm, "end": v(2.52, -6.66) * mm});
            skLineSegment(sketch, "E1573", {"start": v(2.52, -6.66) * mm, "end": v(2.53, -6.66) * mm});
            skLineSegment(sketch, "E1574", {"start": v(2.53, -6.66) * mm, "end": v(2.53, -6.67) * mm});
            skLineSegment(sketch, "E1575", {"start": v(2.53, -6.67) * mm, "end": v(2.54, -6.68) * mm});
            skLineSegment(sketch, "E1576", {"start": v(2.54, -6.68) * mm, "end": v(2.55, -6.7) * mm});
            skLineSegment(sketch, "E1577", {"start": v(2.55, -6.7) * mm, "end": v(2.56, -6.7) * mm});
            skLineSegment(sketch, "E1578", {"start": v(2.56, -6.7) * mm, "end": v(2.57, -6.72) * mm});
            skLineSegment(sketch, "E1579", {"start": v(2.57, -6.72) * mm, "end": v(2.58, -6.73) * mm});
            skLineSegment(sketch, "E1580", {"start": v(2.58, -6.73) * mm, "end": v(2.59, -6.75) * mm});
            skLineSegment(sketch, "E1581", {"start": v(2.59, -6.75) * mm, "end": v(2.6, -6.76) * mm});
            skLineSegment(sketch, "E1582", {"start": v(2.6, -6.76) * mm, "end": v(2.6, -6.77) * mm});
            skLineSegment(sketch, "E1583", {"start": v(2.6, -6.77) * mm, "end": v(2.62, -6.79) * mm});
            skLineSegment(sketch, "E1584", {"start": v(2.62, -6.79) * mm, "end": v(2.63, -6.8) * mm});
            skLineSegment(sketch, "E1585", {"start": v(2.63, -6.8) * mm, "end": v(2.64, -6.82) * mm});
            skLineSegment(sketch, "E1586", {"start": v(2.64, -6.82) * mm, "end": v(2.65, -6.83) * mm});
            skLineSegment(sketch, "E1587", {"start": v(2.65, -6.83) * mm, "end": v(2.67, -6.85) * mm});
            skLineSegment(sketch, "E1588", {"start": v(2.67, -6.85) * mm, "end": v(2.68, -6.86) * mm});
            skLineSegment(sketch, "E1589", {"start": v(2.68, -6.86) * mm, "end": v(2.7, -6.88) * mm});
            skLineSegment(sketch, "E1590", {"start": v(2.7, -6.88) * mm, "end": v(2.7, -6.9) * mm});
            skLineSegment(sketch, "E1591", {"start": v(2.7, -6.9) * mm, "end": v(2.72, -6.91) * mm});
            skLineSegment(sketch, "E1592", {"start": v(2.72, -6.91) * mm, "end": v(2.74, -6.93) * mm});
            skLineSegment(sketch, "E1593", {"start": v(2.74, -6.93) * mm, "end": v(2.75, -6.95) * mm});
            skLineSegment(sketch, "E1594", {"start": v(2.75, -6.95) * mm, "end": v(2.77, -6.96) * mm});
            skLineSegment(sketch, "E1595", {"start": v(2.77, -6.96) * mm, "end": v(2.79, -6.98) * mm});
            skLineSegment(sketch, "E1596", {"start": v(2.79, -6.98) * mm, "end": v(2.8, -7) * mm});
            skLineSegment(sketch, "E1597", {"start": v(2.8, -7) * mm, "end": v(2.82, -7.02) * mm});
            skLineSegment(sketch, "E1598", {"start": v(2.82, -7.02) * mm, "end": v(2.84, -7.04) * mm});
            skLineSegment(sketch, "E1599", {"start": v(2.84, -7.04) * mm, "end": v(2.86, -7.05) * mm});
            skLineSegment(sketch, "E1600", {"start": v(2.86, -7.05) * mm, "end": v(2.88, -7.07) * mm});
            skLineSegment(sketch, "E1601", {"start": v(2.88, -7.07) * mm, "end": v(2.9, -7.1) * mm});
            skLineSegment(sketch, "E1602", {"start": v(2.9, -7.1) * mm, "end": v(2.92, -7.11) * mm});
            skLineSegment(sketch, "E1603", {"start": v(2.92, -7.11) * mm, "end": v(2.94, -7.13) * mm});
            skLineSegment(sketch, "E1604", {"start": v(2.94, -7.13) * mm, "end": v(2.96, -7.15) * mm});
            skLineSegment(sketch, "E1605", {"start": v(2.96, -7.15) * mm, "end": v(2.98, -7.17) * mm});
            skLineSegment(sketch, "E1606", {"start": v(2.98, -7.17) * mm, "end": v(3, -7.19) * mm});
            skLineSegment(sketch, "E1607", {"start": v(3, -7.19) * mm, "end": v(3.03, -7.2) * mm});
            skLineSegment(sketch, "E1608", {"start": v(3.03, -7.2) * mm, "end": v(3.05, -7.23) * mm});
            skLineSegment(sketch, "E1609", {"start": v(3.05, -7.23) * mm, "end": v(3.08, -7.25) * mm});
            skLineSegment(sketch, "E1610", {"start": v(3.08, -7.25) * mm, "end": v(3.1, -7.27) * mm});
            skLineSegment(sketch, "E1611", {"start": v(3.1, -7.27) * mm, "end": v(3.13, -7.29) * mm});
            skLineSegment(sketch, "E1612", {"start": v(3.13, -7.29) * mm, "end": v(3.15, -7.3) * mm});
            skArc(sketch, "E1613", {"start": v(3.15, -7.3) * mm, "mid": v(3.28, -7.26) * mm, "end": v(3.4, -7.2) * mm});
            skLineSegment(sketch, "E1614", {"start": v(2.23, -6.7) * mm, "end": v(2.22, -6.7) * mm});
            skLineSegment(sketch, "E1615", {"start": v(2.22, -6.7) * mm, "end": v(2.22, -6.7) * mm});
            skLineSegment(sketch, "E1616", {"start": v(2.22, -6.7) * mm, "end": v(2.22, -6.72) * mm});
            skLineSegment(sketch, "E1617", {"start": v(2.22, -6.72) * mm, "end": v(2.21, -6.72) * mm});
            skLineSegment(sketch, "E1618", {"start": v(2.21, -6.72) * mm, "end": v(2.21, -6.74) * mm});
            skLineSegment(sketch, "E1619", {"start": v(2.21, -6.74) * mm, "end": v(2.21, -6.75) * mm});
            skLineSegment(sketch, "E1620", {"start": v(2.21, -6.75) * mm, "end": v(2.21, -6.77) * mm});
            skLineSegment(sketch, "E1621", {"start": v(2.21, -6.77) * mm, "end": v(2.21, -6.77) * mm});
            skLineSegment(sketch, "E1622", {"start": v(2.21, -6.77) * mm, "end": v(2.21, -6.79) * mm});
            skLineSegment(sketch, "E1623", {"start": v(2.21, -6.79) * mm, "end": v(2.22, -6.8) * mm});
            skLineSegment(sketch, "E1624", {"start": v(2.22, -6.8) * mm, "end": v(2.22, -6.81) * mm});
            skLineSegment(sketch, "E1625", {"start": v(2.22, -6.81) * mm, "end": v(2.22, -6.83) * mm});
            skLineSegment(sketch, "E1626", {"start": v(2.22, -6.83) * mm, "end": v(2.22, -6.84) * mm});
            skLineSegment(sketch, "E1627", {"start": v(2.22, -6.84) * mm, "end": v(2.22, -6.86) * mm});
            skLineSegment(sketch, "E1628", {"start": v(2.22, -6.86) * mm, "end": v(2.22, -6.88) * mm});
            skLineSegment(sketch, "E1629", {"start": v(2.22, -6.88) * mm, "end": v(2.22, -6.9) * mm});
            skLineSegment(sketch, "E1630", {"start": v(2.22, -6.9) * mm, "end": v(2.22, -6.91) * mm});
            skLineSegment(sketch, "E1631", {"start": v(2.22, -6.91) * mm, "end": v(2.22, -6.93) * mm});
            skLineSegment(sketch, "E1632", {"start": v(2.22, -6.93) * mm, "end": v(2.22, -6.95) * mm});
            skLineSegment(sketch, "E1633", {"start": v(2.22, -6.95) * mm, "end": v(2.22, -6.97) * mm});
            skLineSegment(sketch, "E1634", {"start": v(2.22, -6.97) * mm, "end": v(2.22, -6.99) * mm});
            skLineSegment(sketch, "E1635", {"start": v(2.22, -6.99) * mm, "end": v(2.22, -7) * mm});
            skLineSegment(sketch, "E1636", {"start": v(2.22, -7) * mm, "end": v(2.22, -7.03) * mm});
            skLineSegment(sketch, "E1637", {"start": v(2.22, -7.03) * mm, "end": v(2.22, -7.05) * mm});
            skLineSegment(sketch, "E1638", {"start": v(2.22, -7.05) * mm, "end": v(2.22, -7.07) * mm});
            skLineSegment(sketch, "E1639", {"start": v(2.22, -7.07) * mm, "end": v(2.22, -7.1) * mm});
            skLineSegment(sketch, "E1640", {"start": v(2.22, -7.1) * mm, "end": v(2.22, -7.11) * mm});
            skLineSegment(sketch, "E1641", {"start": v(2.22, -7.11) * mm, "end": v(2.22, -7.14) * mm});
            skLineSegment(sketch, "E1642", {"start": v(2.22, -7.14) * mm, "end": v(2.21, -7.16) * mm});
            skLineSegment(sketch, "E1643", {"start": v(2.21, -7.16) * mm, "end": v(2.21, -7.19) * mm});
            skLineSegment(sketch, "E1644", {"start": v(2.21, -7.19) * mm, "end": v(2.2, -7.21) * mm});
            skLineSegment(sketch, "E1645", {"start": v(2.2, -7.21) * mm, "end": v(2.2, -7.24) * mm});
            skLineSegment(sketch, "E1646", {"start": v(2.2, -7.24) * mm, "end": v(2.2, -7.26) * mm});
            skLineSegment(sketch, "E1647", {"start": v(2.2, -7.26) * mm, "end": v(2.2, -7.29) * mm});
            skLineSegment(sketch, "E1648", {"start": v(2.2, -7.29) * mm, "end": v(2.2, -7.31) * mm});
            skLineSegment(sketch, "E1649", {"start": v(2.2, -7.31) * mm, "end": v(2.2, -7.34) * mm});
            skLineSegment(sketch, "E1650", {"start": v(2.2, -7.34) * mm, "end": v(2.19, -7.37) * mm});
            skLineSegment(sketch, "E1651", {"start": v(2.19, -7.37) * mm, "end": v(2.19, -7.4) * mm});
            skLineSegment(sketch, "E1652", {"start": v(2.19, -7.4) * mm, "end": v(2.18, -7.43) * mm});
            skLineSegment(sketch, "E1653", {"start": v(2.18, -7.43) * mm, "end": v(2.18, -7.45) * mm});
            skLineSegment(sketch, "E1654", {"start": v(2.18, -7.45) * mm, "end": v(2.17, -7.48) * mm});
            skLineSegment(sketch, "E1655", {"start": v(2.17, -7.48) * mm, "end": v(2.16, -7.51) * mm});
            skLineSegment(sketch, "E1656", {"start": v(2.16, -7.51) * mm, "end": v(2.16, -7.54) * mm});
            skLineSegment(sketch, "E1657", {"start": v(2.16, -7.54) * mm, "end": v(2.15, -7.58) * mm});
            skLineSegment(sketch, "E1658", {"start": v(2.15, -7.58) * mm, "end": v(2.15, -7.6) * mm});
            skLineSegment(sketch, "E1659", {"start": v(2.15, -7.6) * mm, "end": v(2.14, -7.64) * mm});
            skLineSegment(sketch, "E1660", {"start": v(2.14, -7.64) * mm, "end": v(2.13, -7.67) * mm});
            skLineSegment(sketch, "E1661", {"start": v(1.32, -6.94) * mm, "end": v(1.32, -6.94) * mm});
            skLineSegment(sketch, "E1662", {"start": v(1.32, -6.94) * mm, "end": v(1.33, -6.94) * mm});
            skLineSegment(sketch, "E1663", {"start": v(1.33, -6.94) * mm, "end": v(1.34, -6.94) * mm});
            skLineSegment(sketch, "E1664", {"start": v(1.34, -6.94) * mm, "end": v(1.34, -6.95) * mm});
            skLineSegment(sketch, "E1665", {"start": v(1.34, -6.95) * mm, "end": v(1.35, -6.96) * mm});
            skLineSegment(sketch, "E1666", {"start": v(1.35, -6.96) * mm, "end": v(1.36, -6.97) * mm});
            skLineSegment(sketch, "E1667", {"start": v(1.36, -6.97) * mm, "end": v(1.36, -6.99) * mm});
            skLineSegment(sketch, "E1668", {"start": v(1.36, -6.99) * mm, "end": v(1.37, -7) * mm});
            skLineSegment(sketch, "E1669", {"start": v(1.37, -7) * mm, "end": v(1.37, -7) * mm});
            skLineSegment(sketch, "E1670", {"start": v(1.37, -7) * mm, "end": v(1.38, -7.02) * mm});
            skLineSegment(sketch, "E1671", {"start": v(1.38, -7.02) * mm, "end": v(1.38, -7.03) * mm});
            skLineSegment(sketch, "E1672", {"start": v(1.38, -7.03) * mm, "end": v(1.39, -7.04) * mm});
            skLineSegment(sketch, "E1673", {"start": v(1.39, -7.04) * mm, "end": v(1.4, -7.06) * mm});
            skLineSegment(sketch, "E1674", {"start": v(1.4, -7.06) * mm, "end": v(1.4, -7.07) * mm});
            skLineSegment(sketch, "E1675", {"start": v(1.4, -7.07) * mm, "end": v(1.41, -7.09) * mm});
            skLineSegment(sketch, "E1676", {"start": v(1.41, -7.09) * mm, "end": v(1.42, -7.1) * mm});
            skLineSegment(sketch, "E1677", {"start": v(1.42, -7.1) * mm, "end": v(1.43, -7.12) * mm});
            skLineSegment(sketch, "E1678", {"start": v(1.43, -7.12) * mm, "end": v(1.44, -7.13) * mm});
            skLineSegment(sketch, "E1679", {"start": v(1.44, -7.13) * mm, "end": v(1.44, -7.15) * mm});
            skLineSegment(sketch, "E1680", {"start": v(1.44, -7.15) * mm, "end": v(1.45, -7.17) * mm});
            skLineSegment(sketch, "E1681", {"start": v(1.45, -7.17) * mm, "end": v(1.46, -7.18) * mm});
            skLineSegment(sketch, "E1682", {"start": v(1.46, -7.18) * mm, "end": v(1.47, -7.2) * mm});
            skLineSegment(sketch, "E1683", {"start": v(1.47, -7.2) * mm, "end": v(1.48, -7.22) * mm});
            skLineSegment(sketch, "E1684", {"start": v(1.48, -7.22) * mm, "end": v(1.5, -7.24) * mm});
            skLineSegment(sketch, "E1685", {"start": v(1.5, -7.24) * mm, "end": v(1.5, -7.26) * mm});
            skLineSegment(sketch, "E1686", {"start": v(1.5, -7.26) * mm, "end": v(1.52, -7.27) * mm});
            skLineSegment(sketch, "E1687", {"start": v(1.52, -7.27) * mm, "end": v(1.53, -7.3) * mm});
            skLineSegment(sketch, "E1688", {"start": v(1.53, -7.3) * mm, "end": v(1.54, -7.31) * mm});
            skLineSegment(sketch, "E1689", {"start": v(1.54, -7.31) * mm, "end": v(1.56, -7.33) * mm});
            skLineSegment(sketch, "E1690", {"start": v(1.56, -7.33) * mm, "end": v(1.57, -7.35) * mm});
            skLineSegment(sketch, "E1691", {"start": v(1.57, -7.35) * mm, "end": v(1.58, -7.37) * mm});
            skLineSegment(sketch, "E1692", {"start": v(1.58, -7.37) * mm, "end": v(1.6, -7.4) * mm});
            skLineSegment(sketch, "E1693", {"start": v(1.6, -7.4) * mm, "end": v(1.61, -7.42) * mm});
            skLineSegment(sketch, "E1694", {"start": v(1.61, -7.42) * mm, "end": v(1.63, -7.44) * mm});
            skLineSegment(sketch, "E1695", {"start": v(1.63, -7.44) * mm, "end": v(1.64, -7.46) * mm});
            skLineSegment(sketch, "E1696", {"start": v(1.64, -7.46) * mm, "end": v(1.66, -7.48) * mm});
            skLineSegment(sketch, "E1697", {"start": v(1.66, -7.48) * mm, "end": v(1.68, -7.5) * mm});
            skLineSegment(sketch, "E1698", {"start": v(1.68, -7.5) * mm, "end": v(1.7, -7.52) * mm});
            skLineSegment(sketch, "E1699", {"start": v(1.7, -7.52) * mm, "end": v(1.71, -7.55) * mm});
            skLineSegment(sketch, "E1700", {"start": v(1.71, -7.55) * mm, "end": v(1.73, -7.57) * mm});
            skLineSegment(sketch, "E1701", {"start": v(1.73, -7.57) * mm, "end": v(1.75, -7.6) * mm});
            skLineSegment(sketch, "E1702", {"start": v(1.75, -7.6) * mm, "end": v(1.77, -7.62) * mm});
            skLineSegment(sketch, "E1703", {"start": v(1.77, -7.62) * mm, "end": v(1.8, -7.64) * mm});
            skLineSegment(sketch, "E1704", {"start": v(1.8, -7.64) * mm, "end": v(1.81, -7.66) * mm});
            skLineSegment(sketch, "E1705", {"start": v(1.81, -7.66) * mm, "end": v(1.83, -7.69) * mm});
            skLineSegment(sketch, "E1706", {"start": v(1.83, -7.69) * mm, "end": v(1.85, -7.71) * mm});
            skLineSegment(sketch, "E1707", {"start": v(1.85, -7.71) * mm, "end": v(1.88, -7.74) * mm});
            skArc(sketch, "E1708", {"start": v(1.88, -7.74) * mm, "mid": v(2, -7.7) * mm, "end": v(2.13, -7.67) * mm});
            skLineSegment(sketch, "E1709", {"start": v(1.07, -6.98) * mm, "end": v(1.06, -6.98) * mm});
            skLineSegment(sketch, "E1710", {"start": v(1.06, -6.98) * mm, "end": v(1.06, -6.99) * mm});
            skLineSegment(sketch, "E1711", {"start": v(1.06, -6.99) * mm, "end": v(1.05, -7) * mm});
            skLineSegment(sketch, "E1712", {"start": v(1.05, -7) * mm, "end": v(1.05, -7) * mm});
            skLineSegment(sketch, "E1713", {"start": v(1.05, -7) * mm, "end": v(1.04, -7.01) * mm});
            skLineSegment(sketch, "E1714", {"start": v(1.04, -7.01) * mm, "end": v(1.04, -7.03) * mm});
            skLineSegment(sketch, "E1715", {"start": v(1.04, -7.03) * mm, "end": v(1.04, -7.04) * mm});
            skLineSegment(sketch, "E1716", {"start": v(1.04, -7.04) * mm, "end": v(1.04, -7.05) * mm});
            skLineSegment(sketch, "E1717", {"start": v(1.04, -7.05) * mm, "end": v(1.04, -7.06) * mm});
            skLineSegment(sketch, "E1718", {"start": v(1.04, -7.06) * mm, "end": v(1.04, -7.08) * mm});
            skLineSegment(sketch, "E1719", {"start": v(1.04, -7.08) * mm, "end": v(1.03, -7.1) * mm});
            skLineSegment(sketch, "E1720", {"start": v(1.03, -7.1) * mm, "end": v(1.03, -7.1) * mm});
            skLineSegment(sketch, "E1721", {"start": v(1.03, -7.1) * mm, "end": v(1.03, -7.12) * mm});
            skLineSegment(sketch, "E1722", {"start": v(1.03, -7.12) * mm, "end": v(1.03, -7.14) * mm});
            skLineSegment(sketch, "E1723", {"start": v(1.03, -7.14) * mm, "end": v(1.03, -7.15) * mm});
            skLineSegment(sketch, "E1724", {"start": v(1.03, -7.15) * mm, "end": v(1.03, -7.17) * mm});
            skLineSegment(sketch, "E1725", {"start": v(1.03, -7.17) * mm, "end": v(1.02, -7.19) * mm});
            skLineSegment(sketch, "E1726", {"start": v(1.02, -7.19) * mm, "end": v(1.02, -7.2) * mm});
            skLineSegment(sketch, "E1727", {"start": v(1.02, -7.2) * mm, "end": v(1.02, -7.22) * mm});
            skLineSegment(sketch, "E1728", {"start": v(1.02, -7.22) * mm, "end": v(1.01, -7.24) * mm});
            skLineSegment(sketch, "E1729", {"start": v(1.01, -7.24) * mm, "end": v(1.01, -7.26) * mm});
            skLineSegment(sketch, "E1730", {"start": v(1.01, -7.26) * mm, "end": v(1, -7.28) * mm});
            skLineSegment(sketch, "E1731", {"start": v(1, -7.28) * mm, "end": v(1, -7.3) * mm});
            skLineSegment(sketch, "E1732", {"start": v(1, -7.3) * mm, "end": v(1, -7.32) * mm});
            skLineSegment(sketch, "E1733", {"start": v(1, -7.32) * mm, "end": v(1, -7.34) * mm});
            skLineSegment(sketch, "E1734", {"start": v(1, -7.34) * mm, "end": v(0.99, -7.37) * mm});
            skLineSegment(sketch, "E1735", {"start": v(0.99, -7.37) * mm, "end": v(0.98, -7.39) * mm});
            skLineSegment(sketch, "E1736", {"start": v(0.98, -7.39) * mm, "end": v(0.98, -7.4) * mm});
            skLineSegment(sketch, "E1737", {"start": v(0.98, -7.4) * mm, "end": v(0.97, -7.43) * mm});
            skLineSegment(sketch, "E1738", {"start": v(0.97, -7.43) * mm, "end": v(0.97, -7.46) * mm});
            skLineSegment(sketch, "E1739", {"start": v(0.97, -7.46) * mm, "end": v(0.96, -7.48) * mm});
            skLineSegment(sketch, "E1740", {"start": v(0.96, -7.48) * mm, "end": v(0.95, -7.5) * mm});
            skLineSegment(sketch, "E1741", {"start": v(0.95, -7.5) * mm, "end": v(0.95, -7.53) * mm});
            skLineSegment(sketch, "E1742", {"start": v(0.95, -7.53) * mm, "end": v(0.94, -7.55) * mm});
            skLineSegment(sketch, "E1743", {"start": v(0.94, -7.55) * mm, "end": v(0.93, -7.58) * mm});
            skLineSegment(sketch, "E1744", {"start": v(0.93, -7.58) * mm, "end": v(0.92, -7.6) * mm});
            skLineSegment(sketch, "E1745", {"start": v(0.92, -7.6) * mm, "end": v(0.91, -7.63) * mm});
            skLineSegment(sketch, "E1746", {"start": v(0.91, -7.63) * mm, "end": v(0.9, -7.66) * mm});
            skLineSegment(sketch, "E1747", {"start": v(0.9, -7.66) * mm, "end": v(0.9, -7.69) * mm});
            skLineSegment(sketch, "E1748", {"start": v(0.9, -7.69) * mm, "end": v(0.89, -7.72) * mm});
            skLineSegment(sketch, "E1749", {"start": v(0.89, -7.72) * mm, "end": v(0.88, -7.74) * mm});
            skLineSegment(sketch, "E1750", {"start": v(0.88, -7.74) * mm, "end": v(0.87, -7.77) * mm});
            skLineSegment(sketch, "E1751", {"start": v(0.87, -7.77) * mm, "end": v(0.85, -7.8) * mm});
            skLineSegment(sketch, "E1752", {"start": v(0.85, -7.8) * mm, "end": v(0.84, -7.83) * mm});
            skLineSegment(sketch, "E1753", {"start": v(0.84, -7.83) * mm, "end": v(0.83, -7.86) * mm});
            skLineSegment(sketch, "E1754", {"start": v(0.83, -7.86) * mm, "end": v(0.82, -7.89) * mm});
            skLineSegment(sketch, "E1755", {"start": v(0.82, -7.89) * mm, "end": v(0.8, -7.92) * mm});
            skLineSegment(sketch, "E1756", {"start": v(0.13, -7.06) * mm, "end": v(0.13, -7.06) * mm});
            skLineSegment(sketch, "E1757", {"start": v(0.13, -7.06) * mm, "end": v(0.14, -7.06) * mm});
            skLineSegment(sketch, "E1758", {"start": v(0.14, -7.06) * mm, "end": v(0.14, -7.07) * mm});
            skLineSegment(sketch, "E1759", {"start": v(0.14, -7.07) * mm, "end": v(0.15, -7.08) * mm});
            skLineSegment(sketch, "E1760", {"start": v(0.15, -7.08) * mm, "end": v(0.16, -7.09) * mm});
            skLineSegment(sketch, "E1761", {"start": v(0.16, -7.09) * mm, "end": v(0.16, -7.1) * mm});
            skLineSegment(sketch, "E1762", {"start": v(0.16, -7.1) * mm, "end": v(0.16, -7.12) * mm});
            skLineSegment(sketch, "E1763", {"start": v(0.16, -7.12) * mm, "end": v(0.17, -7.12) * mm});
            skLineSegment(sketch, "E1764", {"start": v(0.17, -7.12) * mm, "end": v(0.17, -7.14) * mm});
            skLineSegment(sketch, "E1765", {"start": v(0.17, -7.14) * mm, "end": v(0.17, -7.15) * mm});
            skLineSegment(sketch, "E1766", {"start": v(0.17, -7.15) * mm, "end": v(0.18, -7.16) * mm});
            skLineSegment(sketch, "E1767", {"start": v(0.18, -7.16) * mm, "end": v(0.18, -7.18) * mm});
            skLineSegment(sketch, "E1768", {"start": v(0.18, -7.18) * mm, "end": v(0.19, -7.2) * mm});
            skLineSegment(sketch, "E1769", {"start": v(0.19, -7.2) * mm, "end": v(0.19, -7.2) * mm});
            skLineSegment(sketch, "E1770", {"start": v(0.19, -7.2) * mm, "end": v(0.2, -7.22) * mm});
            skLineSegment(sketch, "E1771", {"start": v(0.2, -7.22) * mm, "end": v(0.2, -7.24) * mm});
            skLineSegment(sketch, "E1772", {"start": v(0.2, -7.24) * mm, "end": v(0.2, -7.26) * mm});
            skLineSegment(sketch, "E1773", {"start": v(0.2, -7.26) * mm, "end": v(0.21, -7.27) * mm});
            skLineSegment(sketch, "E1774", {"start": v(0.21, -7.27) * mm, "end": v(0.22, -7.3) * mm});
            skLineSegment(sketch, "E1775", {"start": v(0.22, -7.3) * mm, "end": v(0.22, -7.3) * mm});
            skLineSegment(sketch, "E1776", {"start": v(0.22, -7.3) * mm, "end": v(0.23, -7.33) * mm});
            skLineSegment(sketch, "E1777", {"start": v(0.23, -7.33) * mm, "end": v(0.24, -7.35) * mm});
            skLineSegment(sketch, "E1778", {"start": v(0.24, -7.35) * mm, "end": v(0.24, -7.37) * mm});
            skLineSegment(sketch, "E1779", {"start": v(0.24, -7.37) * mm, "end": v(0.25, -7.39) * mm});
            skLineSegment(sketch, "E1780", {"start": v(0.25, -7.39) * mm, "end": v(0.26, -7.4) * mm});
            skLineSegment(sketch, "E1781", {"start": v(0.26, -7.4) * mm, "end": v(0.27, -7.43) * mm});
            skLineSegment(sketch, "E1782", {"start": v(0.27, -7.43) * mm, "end": v(0.28, -7.45) * mm});
            skLineSegment(sketch, "E1783", {"start": v(0.28, -7.45) * mm, "end": v(0.29, -7.47) * mm});
            skLineSegment(sketch, "E1784", {"start": v(0.29, -7.47) * mm, "end": v(0.3, -7.5) * mm});
            skLineSegment(sketch, "E1785", {"start": v(0.3, -7.5) * mm, "end": v(0.3, -7.51) * mm});
            skLineSegment(sketch, "E1786", {"start": v(0.3, -7.51) * mm, "end": v(0.32, -7.54) * mm});
            skLineSegment(sketch, "E1787", {"start": v(0.32, -7.54) * mm, "end": v(0.33, -7.56) * mm});
            skLineSegment(sketch, "E1788", {"start": v(0.33, -7.56) * mm, "end": v(0.34, -7.58) * mm});
            skLineSegment(sketch, "E1789", {"start": v(0.34, -7.58) * mm, "end": v(0.35, -7.6) * mm});
            skLineSegment(sketch, "E1790", {"start": v(0.35, -7.6) * mm, "end": v(0.36, -7.63) * mm});
            skLineSegment(sketch, "E1791", {"start": v(0.36, -7.63) * mm, "end": v(0.37, -7.65) * mm});
            skLineSegment(sketch, "E1792", {"start": v(0.37, -7.65) * mm, "end": v(0.39, -7.68) * mm});
            skLineSegment(sketch, "E1793", {"start": v(0.39, -7.68) * mm, "end": v(0.4, -7.7) * mm});
            skLineSegment(sketch, "E1794", {"start": v(0.4, -7.7) * mm, "end": v(0.41, -7.73) * mm});
            skLineSegment(sketch, "E1795", {"start": v(0.41, -7.73) * mm, "end": v(0.43, -7.75) * mm});
            skLineSegment(sketch, "E1796", {"start": v(0.43, -7.75) * mm, "end": v(0.44, -7.78) * mm});
            skLineSegment(sketch, "E1797", {"start": v(0.44, -7.78) * mm, "end": v(0.46, -7.8) * mm});
            skLineSegment(sketch, "E1798", {"start": v(0.46, -7.8) * mm, "end": v(0.47, -7.83) * mm});
            skLineSegment(sketch, "E1799", {"start": v(0.47, -7.83) * mm, "end": v(0.5, -7.86) * mm});
            skLineSegment(sketch, "E1800", {"start": v(0.5, -7.86) * mm, "end": v(0.5, -7.89) * mm});
            skLineSegment(sketch, "E1801", {"start": v(0.5, -7.89) * mm, "end": v(0.53, -7.91) * mm});
            skLineSegment(sketch, "E1802", {"start": v(0.53, -7.91) * mm, "end": v(0.54, -7.94) * mm});
            skArc(sketch, "E1803", {"start": v(0.54, -7.94) * mm, "mid": v(0.67, -7.93) * mm, "end": v(0.8, -7.92) * mm});
            skLineSegment(sketch, "E1804", {"start": v(-0.13, -7.06) * mm, "end": v(-0.13, -7.06) * mm});
            skLineSegment(sketch, "E1805", {"start": v(-0.13, -7.06) * mm, "end": v(-0.14, -7.06) * mm});
            skLineSegment(sketch, "E1806", {"start": v(-0.14, -7.06) * mm, "end": v(-0.14, -7.07) * mm});
            skLineSegment(sketch, "E1807", {"start": v(-0.14, -7.07) * mm, "end": v(-0.15, -7.08) * mm});
            skLineSegment(sketch, "E1808", {"start": v(-0.15, -7.08) * mm, "end": v(-0.16, -7.09) * mm});
            skLineSegment(sketch, "E1809", {"start": v(-0.16, -7.09) * mm, "end": v(-0.16, -7.1) * mm});
            skLineSegment(sketch, "E1810", {"start": v(-0.16, -7.1) * mm, "end": v(-0.16, -7.12) * mm});
            skLineSegment(sketch, "E1811", {"start": v(-0.16, -7.12) * mm, "end": v(-0.17, -7.12) * mm});
            skLineSegment(sketch, "E1812", {"start": v(-0.17, -7.12) * mm, "end": v(-0.17, -7.14) * mm});
            skLineSegment(sketch, "E1813", {"start": v(-0.17, -7.14) * mm, "end": v(-0.17, -7.15) * mm});
            skLineSegment(sketch, "E1814", {"start": v(-0.17, -7.15) * mm, "end": v(-0.18, -7.16) * mm});
            skLineSegment(sketch, "E1815", {"start": v(-0.18, -7.16) * mm, "end": v(-0.18, -7.18) * mm});
            skLineSegment(sketch, "E1816", {"start": v(-0.18, -7.18) * mm, "end": v(-0.19, -7.2) * mm});
            skLineSegment(sketch, "E1817", {"start": v(-0.19, -7.2) * mm, "end": v(-0.19, -7.2) * mm});
            skLineSegment(sketch, "E1818", {"start": v(-0.19, -7.2) * mm, "end": v(-0.2, -7.22) * mm});
            skLineSegment(sketch, "E1819", {"start": v(-0.2, -7.22) * mm, "end": v(-0.2, -7.24) * mm});
            skLineSegment(sketch, "E1820", {"start": v(-0.2, -7.24) * mm, "end": v(-0.2, -7.26) * mm});
            skLineSegment(sketch, "E1821", {"start": v(-0.2, -7.26) * mm, "end": v(-0.21, -7.27) * mm});
            skLineSegment(sketch, "E1822", {"start": v(-0.21, -7.27) * mm, "end": v(-0.22, -7.3) * mm});
            skLineSegment(sketch, "E1823", {"start": v(-0.22, -7.3) * mm, "end": v(-0.22, -7.3) * mm});
            skLineSegment(sketch, "E1824", {"start": v(-0.22, -7.3) * mm, "end": v(-0.23, -7.33) * mm});
            skLineSegment(sketch, "E1825", {"start": v(-0.23, -7.33) * mm, "end": v(-0.24, -7.35) * mm});
            skLineSegment(sketch, "E1826", {"start": v(-0.24, -7.35) * mm, "end": v(-0.24, -7.37) * mm});
            skLineSegment(sketch, "E1827", {"start": v(-0.24, -7.37) * mm, "end": v(-0.25, -7.39) * mm});
            skLineSegment(sketch, "E1828", {"start": v(-0.25, -7.39) * mm, "end": v(-0.26, -7.4) * mm});
            skLineSegment(sketch, "E1829", {"start": v(-0.26, -7.4) * mm, "end": v(-0.27, -7.43) * mm});
            skLineSegment(sketch, "E1830", {"start": v(-0.27, -7.43) * mm, "end": v(-0.28, -7.45) * mm});
            skLineSegment(sketch, "E1831", {"start": v(-0.28, -7.45) * mm, "end": v(-0.29, -7.47) * mm});
            skLineSegment(sketch, "E1832", {"start": v(-0.29, -7.47) * mm, "end": v(-0.3, -7.5) * mm});
            skLineSegment(sketch, "E1833", {"start": v(-0.3, -7.5) * mm, "end": v(-0.3, -7.51) * mm});
            skLineSegment(sketch, "E1834", {"start": v(-0.3, -7.51) * mm, "end": v(-0.32, -7.54) * mm});
            skLineSegment(sketch, "E1835", {"start": v(-0.32, -7.54) * mm, "end": v(-0.33, -7.56) * mm});
            skLineSegment(sketch, "E1836", {"start": v(-0.33, -7.56) * mm, "end": v(-0.34, -7.58) * mm});
            skLineSegment(sketch, "E1837", {"start": v(-0.34, -7.58) * mm, "end": v(-0.35, -7.6) * mm});
            skLineSegment(sketch, "E1838", {"start": v(-0.35, -7.6) * mm, "end": v(-0.36, -7.63) * mm});
            skLineSegment(sketch, "E1839", {"start": v(-0.36, -7.63) * mm, "end": v(-0.37, -7.65) * mm});
            skLineSegment(sketch, "E1840", {"start": v(-0.37, -7.65) * mm, "end": v(-0.39, -7.68) * mm});
            skLineSegment(sketch, "E1841", {"start": v(-0.39, -7.68) * mm, "end": v(-0.4, -7.7) * mm});
            skLineSegment(sketch, "E1842", {"start": v(-0.4, -7.7) * mm, "end": v(-0.41, -7.73) * mm});
            skLineSegment(sketch, "E1843", {"start": v(-0.41, -7.73) * mm, "end": v(-0.43, -7.75) * mm});
            skLineSegment(sketch, "E1844", {"start": v(-0.43, -7.75) * mm, "end": v(-0.44, -7.78) * mm});
            skLineSegment(sketch, "E1845", {"start": v(-0.44, -7.78) * mm, "end": v(-0.46, -7.8) * mm});
            skLineSegment(sketch, "E1846", {"start": v(-0.46, -7.8) * mm, "end": v(-0.47, -7.83) * mm});
            skLineSegment(sketch, "E1847", {"start": v(-0.47, -7.83) * mm, "end": v(-0.5, -7.86) * mm});
            skLineSegment(sketch, "E1848", {"start": v(-0.5, -7.86) * mm, "end": v(-0.5, -7.89) * mm});
            skLineSegment(sketch, "E1849", {"start": v(-0.5, -7.89) * mm, "end": v(-0.53, -7.91) * mm});
            skLineSegment(sketch, "E1850", {"start": v(-0.53, -7.91) * mm, "end": v(-0.54, -7.94) * mm});
            skLineSegment(sketch, "E1851", {"start": v(-1.07, -6.98) * mm, "end": v(-1.06, -6.98) * mm});
            skLineSegment(sketch, "E1852", {"start": v(-1.06, -6.98) * mm, "end": v(-1.06, -6.99) * mm});
            skLineSegment(sketch, "E1853", {"start": v(-1.06, -6.99) * mm, "end": v(-1.05, -7) * mm});
            skLineSegment(sketch, "E1854", {"start": v(-1.05, -7) * mm, "end": v(-1.05, -7) * mm});
            skLineSegment(sketch, "E1855", {"start": v(-1.05, -7) * mm, "end": v(-1.04, -7.01) * mm});
            skLineSegment(sketch, "E1856", {"start": v(-1.04, -7.01) * mm, "end": v(-1.04, -7.03) * mm});
            skLineSegment(sketch, "E1857", {"start": v(-1.04, -7.03) * mm, "end": v(-1.04, -7.04) * mm});
            skLineSegment(sketch, "E1858", {"start": v(-1.04, -7.04) * mm, "end": v(-1.04, -7.05) * mm});
            skLineSegment(sketch, "E1859", {"start": v(-1.04, -7.05) * mm, "end": v(-1.04, -7.06) * mm});
            skLineSegment(sketch, "E1860", {"start": v(-1.04, -7.06) * mm, "end": v(-1.04, -7.08) * mm});
            skLineSegment(sketch, "E1861", {"start": v(-1.04, -7.08) * mm, "end": v(-1.03, -7.1) * mm});
            skLineSegment(sketch, "E1862", {"start": v(-1.03, -7.1) * mm, "end": v(-1.03, -7.1) * mm});
            skLineSegment(sketch, "E1863", {"start": v(-1.03, -7.1) * mm, "end": v(-1.03, -7.12) * mm});
            skLineSegment(sketch, "E1864", {"start": v(-1.03, -7.12) * mm, "end": v(-1.03, -7.14) * mm});
            skLineSegment(sketch, "E1865", {"start": v(-1.03, -7.14) * mm, "end": v(-1.03, -7.15) * mm});
            skLineSegment(sketch, "E1866", {"start": v(-1.03, -7.15) * mm, "end": v(-1.03, -7.17) * mm});
            skLineSegment(sketch, "E1867", {"start": v(-1.03, -7.17) * mm, "end": v(-1.02, -7.19) * mm});
            skLineSegment(sketch, "E1868", {"start": v(-1.02, -7.19) * mm, "end": v(-1.02, -7.2) * mm});
            skLineSegment(sketch, "E1869", {"start": v(-1.02, -7.2) * mm, "end": v(-1.02, -7.22) * mm});
            skLineSegment(sketch, "E1870", {"start": v(-1.02, -7.22) * mm, "end": v(-1.01, -7.24) * mm});
            skLineSegment(sketch, "E1871", {"start": v(-1.01, -7.24) * mm, "end": v(-1.01, -7.26) * mm});
            skLineSegment(sketch, "E1872", {"start": v(-1.01, -7.26) * mm, "end": v(-1, -7.28) * mm});
            skLineSegment(sketch, "E1873", {"start": v(-1, -7.28) * mm, "end": v(-1, -7.3) * mm});
            skLineSegment(sketch, "E1874", {"start": v(-1, -7.3) * mm, "end": v(-1, -7.32) * mm});
            skLineSegment(sketch, "E1875", {"start": v(-1, -7.32) * mm, "end": v(-1, -7.34) * mm});
            skLineSegment(sketch, "E1876", {"start": v(-1, -7.34) * mm, "end": v(-0.99, -7.37) * mm});
            skLineSegment(sketch, "E1877", {"start": v(-0.99, -7.37) * mm, "end": v(-0.98, -7.39) * mm});
            skLineSegment(sketch, "E1878", {"start": v(-0.98, -7.39) * mm, "end": v(-0.98, -7.4) * mm});
            skLineSegment(sketch, "E1879", {"start": v(-0.98, -7.4) * mm, "end": v(-0.97, -7.43) * mm});
            skLineSegment(sketch, "E1880", {"start": v(-0.97, -7.43) * mm, "end": v(-0.97, -7.46) * mm});
            skLineSegment(sketch, "E1881", {"start": v(-0.97, -7.46) * mm, "end": v(-0.96, -7.48) * mm});
            skLineSegment(sketch, "E1882", {"start": v(-0.96, -7.48) * mm, "end": v(-0.95, -7.5) * mm});
            skLineSegment(sketch, "E1883", {"start": v(-0.95, -7.5) * mm, "end": v(-0.95, -7.53) * mm});
            skLineSegment(sketch, "E1884", {"start": v(-0.95, -7.53) * mm, "end": v(-0.94, -7.55) * mm});
            skLineSegment(sketch, "E1885", {"start": v(-0.94, -7.55) * mm, "end": v(-0.93, -7.58) * mm});
            skLineSegment(sketch, "E1886", {"start": v(-0.93, -7.58) * mm, "end": v(-0.92, -7.6) * mm});
            skLineSegment(sketch, "E1887", {"start": v(-0.92, -7.6) * mm, "end": v(-0.91, -7.63) * mm});
            skLineSegment(sketch, "E1888", {"start": v(-0.91, -7.63) * mm, "end": v(-0.9, -7.66) * mm});
            skLineSegment(sketch, "E1889", {"start": v(-0.9, -7.66) * mm, "end": v(-0.9, -7.69) * mm});
            skLineSegment(sketch, "E1890", {"start": v(-0.9, -7.69) * mm, "end": v(-0.89, -7.72) * mm});
            skLineSegment(sketch, "E1891", {"start": v(-0.89, -7.72) * mm, "end": v(-0.88, -7.74) * mm});
            skLineSegment(sketch, "E1892", {"start": v(-0.88, -7.74) * mm, "end": v(-0.87, -7.77) * mm});
            skLineSegment(sketch, "E1893", {"start": v(-0.87, -7.77) * mm, "end": v(-0.85, -7.8) * mm});
            skLineSegment(sketch, "E1894", {"start": v(-0.85, -7.8) * mm, "end": v(-0.84, -7.83) * mm});
            skLineSegment(sketch, "E1895", {"start": v(-0.84, -7.83) * mm, "end": v(-0.83, -7.86) * mm});
            skLineSegment(sketch, "E1896", {"start": v(-0.83, -7.86) * mm, "end": v(-0.82, -7.89) * mm});
            skLineSegment(sketch, "E1897", {"start": v(-0.82, -7.89) * mm, "end": v(-0.8, -7.92) * mm});
            skArc(sketch, "E1898", {"start": v(-0.8, -7.92) * mm, "mid": v(-0.67, -7.93) * mm, "end": v(-0.54, -7.94) * mm});
            skLineSegment(sketch, "E1899", {"start": v(-1.32, -6.94) * mm, "end": v(-1.32, -6.94) * mm});
            skLineSegment(sketch, "E1900", {"start": v(-1.32, -6.94) * mm, "end": v(-1.33, -6.94) * mm});
            skLineSegment(sketch, "E1901", {"start": v(-1.33, -6.94) * mm, "end": v(-1.34, -6.94) * mm});
            skLineSegment(sketch, "E1902", {"start": v(-1.34, -6.94) * mm, "end": v(-1.34, -6.95) * mm});
            skLineSegment(sketch, "E1903", {"start": v(-1.34, -6.95) * mm, "end": v(-1.35, -6.96) * mm});
            skLineSegment(sketch, "E1904", {"start": v(-1.35, -6.96) * mm, "end": v(-1.36, -6.97) * mm});
            skLineSegment(sketch, "E1905", {"start": v(-1.36, -6.97) * mm, "end": v(-1.36, -6.99) * mm});
            skLineSegment(sketch, "E1906", {"start": v(-1.36, -6.99) * mm, "end": v(-1.37, -7) * mm});
            skLineSegment(sketch, "E1907", {"start": v(-1.37, -7) * mm, "end": v(-1.37, -7) * mm});
            skLineSegment(sketch, "E1908", {"start": v(-1.37, -7) * mm, "end": v(-1.38, -7.02) * mm});
            skLineSegment(sketch, "E1909", {"start": v(-1.38, -7.02) * mm, "end": v(-1.38, -7.03) * mm});
            skLineSegment(sketch, "E1910", {"start": v(-1.38, -7.03) * mm, "end": v(-1.39, -7.04) * mm});
            skLineSegment(sketch, "E1911", {"start": v(-1.39, -7.04) * mm, "end": v(-1.4, -7.06) * mm});
            skLineSegment(sketch, "E1912", {"start": v(-1.4, -7.06) * mm, "end": v(-1.4, -7.07) * mm});
            skLineSegment(sketch, "E1913", {"start": v(-1.4, -7.07) * mm, "end": v(-1.41, -7.09) * mm});
            skLineSegment(sketch, "E1914", {"start": v(-1.41, -7.09) * mm, "end": v(-1.42, -7.1) * mm});
            skLineSegment(sketch, "E1915", {"start": v(-1.42, -7.1) * mm, "end": v(-1.43, -7.12) * mm});
            skLineSegment(sketch, "E1916", {"start": v(-1.43, -7.12) * mm, "end": v(-1.44, -7.13) * mm});
            skLineSegment(sketch, "E1917", {"start": v(-1.44, -7.13) * mm, "end": v(-1.44, -7.15) * mm});
            skLineSegment(sketch, "E1918", {"start": v(-1.44, -7.15) * mm, "end": v(-1.45, -7.17) * mm});
            skLineSegment(sketch, "E1919", {"start": v(-1.45, -7.17) * mm, "end": v(-1.46, -7.18) * mm});
            skLineSegment(sketch, "E1920", {"start": v(-1.46, -7.18) * mm, "end": v(-1.47, -7.2) * mm});
            skLineSegment(sketch, "E1921", {"start": v(-1.47, -7.2) * mm, "end": v(-1.48, -7.22) * mm});
            skLineSegment(sketch, "E1922", {"start": v(-1.48, -7.22) * mm, "end": v(-1.5, -7.24) * mm});
            skLineSegment(sketch, "E1923", {"start": v(-1.5, -7.24) * mm, "end": v(-1.5, -7.26) * mm});
            skLineSegment(sketch, "E1924", {"start": v(-1.5, -7.26) * mm, "end": v(-1.52, -7.27) * mm});
            skLineSegment(sketch, "E1925", {"start": v(-1.52, -7.27) * mm, "end": v(-1.53, -7.3) * mm});
            skLineSegment(sketch, "E1926", {"start": v(-1.53, -7.3) * mm, "end": v(-1.54, -7.31) * mm});
            skLineSegment(sketch, "E1927", {"start": v(-1.54, -7.31) * mm, "end": v(-1.56, -7.33) * mm});
            skLineSegment(sketch, "E1928", {"start": v(-1.56, -7.33) * mm, "end": v(-1.57, -7.35) * mm});
            skLineSegment(sketch, "E1929", {"start": v(-1.57, -7.35) * mm, "end": v(-1.58, -7.37) * mm});
            skLineSegment(sketch, "E1930", {"start": v(-1.58, -7.37) * mm, "end": v(-1.6, -7.4) * mm});
            skLineSegment(sketch, "E1931", {"start": v(-1.6, -7.4) * mm, "end": v(-1.61, -7.42) * mm});
            skLineSegment(sketch, "E1932", {"start": v(-1.61, -7.42) * mm, "end": v(-1.63, -7.44) * mm});
            skLineSegment(sketch, "E1933", {"start": v(-1.63, -7.44) * mm, "end": v(-1.64, -7.46) * mm});
            skLineSegment(sketch, "E1934", {"start": v(-1.64, -7.46) * mm, "end": v(-1.66, -7.48) * mm});
            skLineSegment(sketch, "E1935", {"start": v(-1.66, -7.48) * mm, "end": v(-1.68, -7.5) * mm});
            skLineSegment(sketch, "E1936", {"start": v(-1.68, -7.5) * mm, "end": v(-1.7, -7.52) * mm});
            skLineSegment(sketch, "E1937", {"start": v(-1.7, -7.52) * mm, "end": v(-1.71, -7.55) * mm});
            skLineSegment(sketch, "E1938", {"start": v(-1.71, -7.55) * mm, "end": v(-1.73, -7.57) * mm});
            skLineSegment(sketch, "E1939", {"start": v(-1.73, -7.57) * mm, "end": v(-1.75, -7.6) * mm});
            skLineSegment(sketch, "E1940", {"start": v(-1.75, -7.6) * mm, "end": v(-1.77, -7.62) * mm});
            skLineSegment(sketch, "E1941", {"start": v(-1.77, -7.62) * mm, "end": v(-1.8, -7.64) * mm});
            skLineSegment(sketch, "E1942", {"start": v(-1.8, -7.64) * mm, "end": v(-1.81, -7.66) * mm});
            skLineSegment(sketch, "E1943", {"start": v(-1.81, -7.66) * mm, "end": v(-1.83, -7.69) * mm});
            skLineSegment(sketch, "E1944", {"start": v(-1.83, -7.69) * mm, "end": v(-1.85, -7.71) * mm});
            skLineSegment(sketch, "E1945", {"start": v(-1.85, -7.71) * mm, "end": v(-1.88, -7.74) * mm});
            skLineSegment(sketch, "E1946", {"start": v(-2.23, -6.7) * mm, "end": v(-2.22, -6.7) * mm});
            skLineSegment(sketch, "E1947", {"start": v(-2.22, -6.7) * mm, "end": v(-2.22, -6.7) * mm});
            skLineSegment(sketch, "E1948", {"start": v(-2.22, -6.7) * mm, "end": v(-2.22, -6.72) * mm});
            skLineSegment(sketch, "E1949", {"start": v(-2.22, -6.72) * mm, "end": v(-2.21, -6.72) * mm});
            skLineSegment(sketch, "E1950", {"start": v(-2.21, -6.72) * mm, "end": v(-2.21, -6.74) * mm});
            skLineSegment(sketch, "E1951", {"start": v(-2.21, -6.74) * mm, "end": v(-2.21, -6.75) * mm});
            skLineSegment(sketch, "E1952", {"start": v(-2.21, -6.75) * mm, "end": v(-2.21, -6.77) * mm});
            skLineSegment(sketch, "E1953", {"start": v(-2.21, -6.77) * mm, "end": v(-2.21, -6.77) * mm});
            skLineSegment(sketch, "E1954", {"start": v(-2.21, -6.77) * mm, "end": v(-2.21, -6.79) * mm});
            skLineSegment(sketch, "E1955", {"start": v(-2.21, -6.79) * mm, "end": v(-2.22, -6.8) * mm});
            skLineSegment(sketch, "E1956", {"start": v(-2.22, -6.8) * mm, "end": v(-2.22, -6.81) * mm});
            skLineSegment(sketch, "E1957", {"start": v(-2.22, -6.81) * mm, "end": v(-2.22, -6.83) * mm});
            skLineSegment(sketch, "E1958", {"start": v(-2.22, -6.83) * mm, "end": v(-2.22, -6.84) * mm});
            skLineSegment(sketch, "E1959", {"start": v(-2.22, -6.84) * mm, "end": v(-2.22, -6.86) * mm});
            skLineSegment(sketch, "E1960", {"start": v(-2.22, -6.86) * mm, "end": v(-2.22, -6.88) * mm});
            skLineSegment(sketch, "E1961", {"start": v(-2.22, -6.88) * mm, "end": v(-2.22, -6.9) * mm});
            skLineSegment(sketch, "E1962", {"start": v(-2.22, -6.9) * mm, "end": v(-2.22, -6.91) * mm});
            skLineSegment(sketch, "E1963", {"start": v(-2.22, -6.91) * mm, "end": v(-2.22, -6.93) * mm});
            skLineSegment(sketch, "E1964", {"start": v(-2.22, -6.93) * mm, "end": v(-2.22, -6.95) * mm});
            skLineSegment(sketch, "E1965", {"start": v(-2.22, -6.95) * mm, "end": v(-2.22, -6.97) * mm});
            skLineSegment(sketch, "E1966", {"start": v(-2.22, -6.97) * mm, "end": v(-2.22, -6.99) * mm});
            skLineSegment(sketch, "E1967", {"start": v(-2.22, -6.99) * mm, "end": v(-2.22, -7) * mm});
            skLineSegment(sketch, "E1968", {"start": v(-2.22, -7) * mm, "end": v(-2.22, -7.03) * mm});
            skLineSegment(sketch, "E1969", {"start": v(-2.22, -7.03) * mm, "end": v(-2.22, -7.05) * mm});
            skLineSegment(sketch, "E1970", {"start": v(-2.22, -7.05) * mm, "end": v(-2.22, -7.07) * mm});
            skLineSegment(sketch, "E1971", {"start": v(-2.22, -7.07) * mm, "end": v(-2.22, -7.1) * mm});
            skLineSegment(sketch, "E1972", {"start": v(-2.22, -7.1) * mm, "end": v(-2.22, -7.11) * mm});
            skLineSegment(sketch, "E1973", {"start": v(-2.22, -7.11) * mm, "end": v(-2.22, -7.14) * mm});
            skLineSegment(sketch, "E1974", {"start": v(-2.22, -7.14) * mm, "end": v(-2.21, -7.16) * mm});
            skLineSegment(sketch, "E1975", {"start": v(-2.21, -7.16) * mm, "end": v(-2.21, -7.19) * mm});
            skLineSegment(sketch, "E1976", {"start": v(-2.21, -7.19) * mm, "end": v(-2.2, -7.21) * mm});
            skLineSegment(sketch, "E1977", {"start": v(-2.2, -7.21) * mm, "end": v(-2.2, -7.24) * mm});
            skLineSegment(sketch, "E1978", {"start": v(-2.2, -7.24) * mm, "end": v(-2.2, -7.26) * mm});
            skLineSegment(sketch, "E1979", {"start": v(-2.2, -7.26) * mm, "end": v(-2.2, -7.29) * mm});
            skLineSegment(sketch, "E1980", {"start": v(-2.2, -7.29) * mm, "end": v(-2.2, -7.31) * mm});
            skLineSegment(sketch, "E1981", {"start": v(-2.2, -7.31) * mm, "end": v(-2.2, -7.34) * mm});
            skLineSegment(sketch, "E1982", {"start": v(-2.2, -7.34) * mm, "end": v(-2.19, -7.37) * mm});
            skLineSegment(sketch, "E1983", {"start": v(-2.19, -7.37) * mm, "end": v(-2.19, -7.4) * mm});
            skLineSegment(sketch, "E1984", {"start": v(-2.19, -7.4) * mm, "end": v(-2.18, -7.43) * mm});
            skLineSegment(sketch, "E1985", {"start": v(-2.18, -7.43) * mm, "end": v(-2.18, -7.45) * mm});
            skLineSegment(sketch, "E1986", {"start": v(-2.18, -7.45) * mm, "end": v(-2.17, -7.48) * mm});
            skLineSegment(sketch, "E1987", {"start": v(-2.17, -7.48) * mm, "end": v(-2.16, -7.51) * mm});
            skLineSegment(sketch, "E1988", {"start": v(-2.16, -7.51) * mm, "end": v(-2.16, -7.54) * mm});
            skLineSegment(sketch, "E1989", {"start": v(-2.16, -7.54) * mm, "end": v(-2.15, -7.58) * mm});
            skLineSegment(sketch, "E1990", {"start": v(-2.15, -7.58) * mm, "end": v(-2.15, -7.6) * mm});
            skLineSegment(sketch, "E1991", {"start": v(-2.15, -7.6) * mm, "end": v(-2.14, -7.64) * mm});
            skLineSegment(sketch, "E1992", {"start": v(-2.14, -7.64) * mm, "end": v(-2.13, -7.67) * mm});
            skArc(sketch, "E1993", {"start": v(-2.13, -7.67) * mm, "mid": v(-2, -7.7) * mm, "end": v(-1.88, -7.74) * mm});
            skLineSegment(sketch, "E1994", {"start": v(-2.47, -6.62) * mm, "end": v(-2.47, -6.61) * mm});
            skLineSegment(sketch, "E1995", {"start": v(-2.47, -6.61) * mm, "end": v(-2.48, -6.62) * mm});
            skLineSegment(sketch, "E1996", {"start": v(-2.48, -6.62) * mm, "end": v(-2.49, -6.62) * mm});
            skLineSegment(sketch, "E1997", {"start": v(-2.49, -6.62) * mm, "end": v(-2.5, -6.63) * mm});
            skLineSegment(sketch, "E1998", {"start": v(-2.5, -6.63) * mm, "end": v(-2.5, -6.63) * mm});
            skLineSegment(sketch, "E1999", {"start": v(-2.5, -6.63) * mm, "end": v(-2.51, -6.64) * mm});
            skLineSegment(sketch, "E2000", {"start": v(-2.51, -6.64) * mm, "end": v(-2.52, -6.66) * mm});
            skLineSegment(sketch, "E2001", {"start": v(-2.52, -6.66) * mm, "end": v(-2.53, -6.66) * mm});
            skLineSegment(sketch, "E2002", {"start": v(-2.53, -6.66) * mm, "end": v(-2.53, -6.67) * mm});
            skLineSegment(sketch, "E2003", {"start": v(-2.53, -6.67) * mm, "end": v(-2.54, -6.68) * mm});
            skLineSegment(sketch, "E2004", {"start": v(-2.54, -6.68) * mm, "end": v(-2.55, -6.7) * mm});
            skLineSegment(sketch, "E2005", {"start": v(-2.55, -6.7) * mm, "end": v(-2.56, -6.7) * mm});
            skLineSegment(sketch, "E2006", {"start": v(-2.56, -6.7) * mm, "end": v(-2.57, -6.72) * mm});
            skLineSegment(sketch, "E2007", {"start": v(-2.57, -6.72) * mm, "end": v(-2.58, -6.73) * mm});
            skLineSegment(sketch, "E2008", {"start": v(-2.58, -6.73) * mm, "end": v(-2.59, -6.75) * mm});
            skLineSegment(sketch, "E2009", {"start": v(-2.59, -6.75) * mm, "end": v(-2.6, -6.76) * mm});
            skLineSegment(sketch, "E2010", {"start": v(-2.6, -6.76) * mm, "end": v(-2.6, -6.77) * mm});
            skLineSegment(sketch, "E2011", {"start": v(-2.6, -6.77) * mm, "end": v(-2.62, -6.79) * mm});
            skLineSegment(sketch, "E2012", {"start": v(-2.62, -6.79) * mm, "end": v(-2.63, -6.8) * mm});
            skLineSegment(sketch, "E2013", {"start": v(-2.63, -6.8) * mm, "end": v(-2.64, -6.82) * mm});
            skLineSegment(sketch, "E2014", {"start": v(-2.64, -6.82) * mm, "end": v(-2.65, -6.83) * mm});
            skLineSegment(sketch, "E2015", {"start": v(-2.65, -6.83) * mm, "end": v(-2.67, -6.85) * mm});
            skLineSegment(sketch, "E2016", {"start": v(-2.67, -6.85) * mm, "end": v(-2.68, -6.86) * mm});
            skLineSegment(sketch, "E2017", {"start": v(-2.68, -6.86) * mm, "end": v(-2.7, -6.88) * mm});
            skLineSegment(sketch, "E2018", {"start": v(-2.7, -6.88) * mm, "end": v(-2.7, -6.9) * mm});
            skLineSegment(sketch, "E2019", {"start": v(-2.7, -6.9) * mm, "end": v(-2.72, -6.91) * mm});
            skLineSegment(sketch, "E2020", {"start": v(-2.72, -6.91) * mm, "end": v(-2.74, -6.93) * mm});
            skLineSegment(sketch, "E2021", {"start": v(-2.74, -6.93) * mm, "end": v(-2.75, -6.95) * mm});
            skLineSegment(sketch, "E2022", {"start": v(-2.75, -6.95) * mm, "end": v(-2.77, -6.96) * mm});
            skLineSegment(sketch, "E2023", {"start": v(-2.77, -6.96) * mm, "end": v(-2.79, -6.98) * mm});
            skLineSegment(sketch, "E2024", {"start": v(-2.79, -6.98) * mm, "end": v(-2.8, -7) * mm});
            skLineSegment(sketch, "E2025", {"start": v(-2.8, -7) * mm, "end": v(-2.82, -7.02) * mm});
            skLineSegment(sketch, "E2026", {"start": v(-2.82, -7.02) * mm, "end": v(-2.84, -7.04) * mm});
            skLineSegment(sketch, "E2027", {"start": v(-2.84, -7.04) * mm, "end": v(-2.86, -7.05) * mm});
            skLineSegment(sketch, "E2028", {"start": v(-2.86, -7.05) * mm, "end": v(-2.88, -7.07) * mm});
            skLineSegment(sketch, "E2029", {"start": v(-2.88, -7.07) * mm, "end": v(-2.9, -7.1) * mm});
            skLineSegment(sketch, "E2030", {"start": v(-2.9, -7.1) * mm, "end": v(-2.92, -7.11) * mm});
            skLineSegment(sketch, "E2031", {"start": v(-2.92, -7.11) * mm, "end": v(-2.94, -7.13) * mm});
            skLineSegment(sketch, "E2032", {"start": v(-2.94, -7.13) * mm, "end": v(-2.96, -7.15) * mm});
            skLineSegment(sketch, "E2033", {"start": v(-2.96, -7.15) * mm, "end": v(-2.98, -7.17) * mm});
            skLineSegment(sketch, "E2034", {"start": v(-2.98, -7.17) * mm, "end": v(-3, -7.19) * mm});
            skLineSegment(sketch, "E2035", {"start": v(-3, -7.19) * mm, "end": v(-3.03, -7.2) * mm});
            skLineSegment(sketch, "E2036", {"start": v(-3.03, -7.2) * mm, "end": v(-3.05, -7.23) * mm});
            skLineSegment(sketch, "E2037", {"start": v(-3.05, -7.23) * mm, "end": v(-3.08, -7.25) * mm});
            skLineSegment(sketch, "E2038", {"start": v(-3.08, -7.25) * mm, "end": v(-3.1, -7.27) * mm});
            skLineSegment(sketch, "E2039", {"start": v(-3.1, -7.27) * mm, "end": v(-3.13, -7.29) * mm});
            skLineSegment(sketch, "E2040", {"start": v(-3.13, -7.29) * mm, "end": v(-3.15, -7.3) * mm});
            skLineSegment(sketch, "E2041", {"start": v(-3.33, -6.23) * mm, "end": v(-3.32, -6.23) * mm});
            skLineSegment(sketch, "E2042", {"start": v(-3.32, -6.23) * mm, "end": v(-3.32, -6.24) * mm});
            skLineSegment(sketch, "E2043", {"start": v(-3.32, -6.24) * mm, "end": v(-3.32, -6.24) * mm});
            skLineSegment(sketch, "E2044", {"start": v(-3.32, -6.24) * mm, "end": v(-3.32, -6.25) * mm});
            skLineSegment(sketch, "E2045", {"start": v(-3.32, -6.25) * mm, "end": v(-3.32, -6.27) * mm});
            skLineSegment(sketch, "E2046", {"start": v(-3.32, -6.27) * mm, "end": v(-3.32, -6.28) * mm});
            skLineSegment(sketch, "E2047", {"start": v(-3.32, -6.28) * mm, "end": v(-3.32, -6.3) * mm});
            skLineSegment(sketch, "E2048", {"start": v(-3.32, -6.3) * mm, "end": v(-3.32, -6.3) * mm});
            skLineSegment(sketch, "E2049", {"start": v(-3.32, -6.3) * mm, "end": v(-3.33, -6.31) * mm});
            skLineSegment(sketch, "E2050", {"start": v(-3.33, -6.31) * mm, "end": v(-3.33, -6.33) * mm});
            skLineSegment(sketch, "E2051", {"start": v(-3.33, -6.33) * mm, "end": v(-3.33, -6.34) * mm});
            skLineSegment(sketch, "E2052", {"start": v(-3.33, -6.34) * mm, "end": v(-3.34, -6.36) * mm});
            skLineSegment(sketch, "E2053", {"start": v(-3.34, -6.36) * mm, "end": v(-3.34, -6.37) * mm});
            skLineSegment(sketch, "E2054", {"start": v(-3.34, -6.37) * mm, "end": v(-3.35, -6.39) * mm});
            skLineSegment(sketch, "E2055", {"start": v(-3.35, -6.39) * mm, "end": v(-3.35, -6.4) * mm});
            skLineSegment(sketch, "E2056", {"start": v(-3.35, -6.4) * mm, "end": v(-3.35, -6.42) * mm});
            skLineSegment(sketch, "E2057", {"start": v(-3.35, -6.42) * mm, "end": v(-3.36, -6.44) * mm});
            skLineSegment(sketch, "E2058", {"start": v(-3.36, -6.44) * mm, "end": v(-3.36, -6.45) * mm});
            skLineSegment(sketch, "E2059", {"start": v(-3.36, -6.45) * mm, "end": v(-3.36, -6.47) * mm});
            skLineSegment(sketch, "E2060", {"start": v(-3.36, -6.47) * mm, "end": v(-3.37, -6.5) * mm});
            skLineSegment(sketch, "E2061", {"start": v(-3.37, -6.5) * mm, "end": v(-3.37, -6.51) * mm});
            skLineSegment(sketch, "E2062", {"start": v(-3.37, -6.51) * mm, "end": v(-3.37, -6.53) * mm});
            skLineSegment(sketch, "E2063", {"start": v(-3.37, -6.53) * mm, "end": v(-3.38, -6.55) * mm});
            skLineSegment(sketch, "E2064", {"start": v(-3.38, -6.55) * mm, "end": v(-3.38, -6.57) * mm});
            skLineSegment(sketch, "E2065", {"start": v(-3.38, -6.57) * mm, "end": v(-3.38, -6.6) * mm});
            skLineSegment(sketch, "E2066", {"start": v(-3.38, -6.6) * mm, "end": v(-3.38, -6.62) * mm});
            skLineSegment(sketch, "E2067", {"start": v(-3.38, -6.62) * mm, "end": v(-3.39, -6.64) * mm});
            skLineSegment(sketch, "E2068", {"start": v(-3.39, -6.64) * mm, "end": v(-3.39, -6.66) * mm});
            skLineSegment(sketch, "E2069", {"start": v(-3.39, -6.66) * mm, "end": v(-3.4, -6.68) * mm});
            skLineSegment(sketch, "E2070", {"start": v(-3.4, -6.68) * mm, "end": v(-3.4, -6.7) * mm});
            skLineSegment(sketch, "E2071", {"start": v(-3.4, -6.7) * mm, "end": v(-3.4, -6.73) * mm});
            skLineSegment(sketch, "E2072", {"start": v(-3.4, -6.73) * mm, "end": v(-3.4, -6.76) * mm});
            skLineSegment(sketch, "E2073", {"start": v(-3.4, -6.76) * mm, "end": v(-3.4, -6.78) * mm});
            skLineSegment(sketch, "E2074", {"start": v(-3.4, -6.78) * mm, "end": v(-3.4, -6.81) * mm});
            skLineSegment(sketch, "E2075", {"start": v(-3.4, -6.81) * mm, "end": v(-3.4, -6.84) * mm});
            skLineSegment(sketch, "E2076", {"start": v(-3.4, -6.84) * mm, "end": v(-3.4, -6.86) * mm});
            skLineSegment(sketch, "E2077", {"start": v(-3.4, -6.86) * mm, "end": v(-3.4, -6.9) * mm});
            skLineSegment(sketch, "E2078", {"start": v(-3.4, -6.9) * mm, "end": v(-3.4, -6.92) * mm});
            skLineSegment(sketch, "E2079", {"start": v(-3.4, -6.92) * mm, "end": v(-3.4, -6.95) * mm});
            skLineSegment(sketch, "E2080", {"start": v(-3.4, -6.95) * mm, "end": v(-3.4, -6.98) * mm});
            skLineSegment(sketch, "E2081", {"start": v(-3.4, -6.98) * mm, "end": v(-3.4, -7) * mm});
            skLineSegment(sketch, "E2082", {"start": v(-3.4, -7) * mm, "end": v(-3.4, -7.04) * mm});
            skLineSegment(sketch, "E2083", {"start": v(-3.4, -7.04) * mm, "end": v(-3.4, -7.07) * mm});
            skLineSegment(sketch, "E2084", {"start": v(-3.4, -7.07) * mm, "end": v(-3.4, -7.1) * mm});
            skLineSegment(sketch, "E2085", {"start": v(-3.4, -7.1) * mm, "end": v(-3.4, -7.13) * mm});
            skLineSegment(sketch, "E2086", {"start": v(-3.4, -7.13) * mm, "end": v(-3.4, -7.17) * mm});
            skLineSegment(sketch, "E2087", {"start": v(-3.4, -7.17) * mm, "end": v(-3.4, -7.2) * mm});
            skArc(sketch, "E2088", {"start": v(-3.4, -7.2) * mm, "mid": v(-3.28, -7.26) * mm, "end": v(-3.15, -7.3) * mm});
            skLineSegment(sketch, "E2089", {"start": v(-3.55, -6.1) * mm, "end": v(-3.55, -6.1) * mm});
            skLineSegment(sketch, "E2090", {"start": v(-3.55, -6.1) * mm, "end": v(-3.56, -6.1) * mm});
            skLineSegment(sketch, "E2091", {"start": v(-3.56, -6.1) * mm, "end": v(-3.57, -6.1) * mm});
            skLineSegment(sketch, "E2092", {"start": v(-3.57, -6.1) * mm, "end": v(-3.58, -6.1) * mm});
            skLineSegment(sketch, "E2093", {"start": v(-3.58, -6.1) * mm, "end": v(-3.59, -6.11) * mm});
            skLineSegment(sketch, "E2094", {"start": v(-3.59, -6.11) * mm, "end": v(-3.6, -6.12) * mm});
            skLineSegment(sketch, "E2095", {"start": v(-3.6, -6.12) * mm, "end": v(-3.61, -6.13) * mm});
            skLineSegment(sketch, "E2096", {"start": v(-3.61, -6.13) * mm, "end": v(-3.62, -6.14) * mm});
            skLineSegment(sketch, "E2097", {"start": v(-3.62, -6.14) * mm, "end": v(-3.62, -6.15) * mm});
            skLineSegment(sketch, "E2098", {"start": v(-3.62, -6.15) * mm, "end": v(-3.63, -6.16) * mm});
            skLineSegment(sketch, "E2099", {"start": v(-3.63, -6.16) * mm, "end": v(-3.64, -6.17) * mm});
            skLineSegment(sketch, "E2100", {"start": v(-3.64, -6.17) * mm, "end": v(-3.65, -6.18) * mm});
            skLineSegment(sketch, "E2101", {"start": v(-3.65, -6.18) * mm, "end": v(-3.67, -6.2) * mm});
            skLineSegment(sketch, "E2102", {"start": v(-3.67, -6.2) * mm, "end": v(-3.68, -6.2) * mm});
            skLineSegment(sketch, "E2103", {"start": v(-3.68, -6.2) * mm, "end": v(-3.69, -6.21) * mm});
            skLineSegment(sketch, "E2104", {"start": v(-3.69, -6.21) * mm, "end": v(-3.7, -6.23) * mm});
            skLineSegment(sketch, "E2105", {"start": v(-3.7, -6.23) * mm, "end": v(-3.71, -6.24) * mm});
            skLineSegment(sketch, "E2106", {"start": v(-3.71, -6.24) * mm, "end": v(-3.73, -6.25) * mm});
            skLineSegment(sketch, "E2107", {"start": v(-3.73, -6.25) * mm, "end": v(-3.74, -6.26) * mm});
            skLineSegment(sketch, "E2108", {"start": v(-3.74, -6.26) * mm, "end": v(-3.75, -6.27) * mm});
            skLineSegment(sketch, "E2109", {"start": v(-3.75, -6.27) * mm, "end": v(-3.77, -6.29) * mm});
            skLineSegment(sketch, "E2110", {"start": v(-3.77, -6.29) * mm, "end": v(-3.78, -6.3) * mm});
            skLineSegment(sketch, "E2111", {"start": v(-3.78, -6.3) * mm, "end": v(-3.8, -6.31) * mm});
            skLineSegment(sketch, "E2112", {"start": v(-3.8, -6.31) * mm, "end": v(-3.82, -6.33) * mm});
            skLineSegment(sketch, "E2113", {"start": v(-3.82, -6.33) * mm, "end": v(-3.83, -6.34) * mm});
            skLineSegment(sketch, "E2114", {"start": v(-3.83, -6.34) * mm, "end": v(-3.85, -6.35) * mm});
            skLineSegment(sketch, "E2115", {"start": v(-3.85, -6.35) * mm, "end": v(-3.87, -6.37) * mm});
            skLineSegment(sketch, "E2116", {"start": v(-3.87, -6.37) * mm, "end": v(-3.89, -6.38) * mm});
            skLineSegment(sketch, "E2117", {"start": v(-3.89, -6.38) * mm, "end": v(-3.9, -6.4) * mm});
            skLineSegment(sketch, "E2118", {"start": v(-3.9, -6.4) * mm, "end": v(-3.93, -6.41) * mm});
            skLineSegment(sketch, "E2119", {"start": v(-3.93, -6.41) * mm, "end": v(-3.95, -6.43) * mm});
            skLineSegment(sketch, "E2120", {"start": v(-3.95, -6.43) * mm, "end": v(-3.97, -6.44) * mm});
            skLineSegment(sketch, "E2121", {"start": v(-3.97, -6.44) * mm, "end": v(-3.99, -6.46) * mm});
            skLineSegment(sketch, "E2122", {"start": v(-3.99, -6.46) * mm, "end": v(-4, -6.47) * mm});
            skLineSegment(sketch, "E2123", {"start": v(-4, -6.47) * mm, "end": v(-4.03, -6.49) * mm});
            skLineSegment(sketch, "E2124", {"start": v(-4.03, -6.49) * mm, "end": v(-4.05, -6.5) * mm});
            skLineSegment(sketch, "E2125", {"start": v(-4.05, -6.5) * mm, "end": v(-4.08, -6.52) * mm});
            skLineSegment(sketch, "E2126", {"start": v(-4.08, -6.52) * mm, "end": v(-4.1, -6.53) * mm});
            skLineSegment(sketch, "E2127", {"start": v(-4.1, -6.53) * mm, "end": v(-4.13, -6.55) * mm});
            skLineSegment(sketch, "E2128", {"start": v(-4.13, -6.55) * mm, "end": v(-4.15, -6.56) * mm});
            skLineSegment(sketch, "E2129", {"start": v(-4.15, -6.56) * mm, "end": v(-4.18, -6.58) * mm});
            skLineSegment(sketch, "E2130", {"start": v(-4.18, -6.58) * mm, "end": v(-4.2, -6.6) * mm});
            skLineSegment(sketch, "E2131", {"start": v(-4.2, -6.6) * mm, "end": v(-4.23, -6.6) * mm});
            skLineSegment(sketch, "E2132", {"start": v(-4.23, -6.6) * mm, "end": v(-4.26, -6.62) * mm});
            skLineSegment(sketch, "E2133", {"start": v(-4.26, -6.62) * mm, "end": v(-4.29, -6.64) * mm});
            skLineSegment(sketch, "E2134", {"start": v(-4.29, -6.64) * mm, "end": v(-4.31, -6.65) * mm});
            skLineSegment(sketch, "E2135", {"start": v(-4.31, -6.65) * mm, "end": v(-4.34, -6.67) * mm});
            skLineSegment(sketch, "E2136", {"start": v(-4.33, -5.57) * mm, "end": v(-4.33, -5.58) * mm});
            skLineSegment(sketch, "E2137", {"start": v(-4.33, -5.58) * mm, "end": v(-4.32, -5.59) * mm});
            skLineSegment(sketch, "E2138", {"start": v(-4.32, -5.59) * mm, "end": v(-4.32, -5.6) * mm});
            skLineSegment(sketch, "E2139", {"start": v(-4.32, -5.6) * mm, "end": v(-4.32, -5.6) * mm});
            skLineSegment(sketch, "E2140", {"start": v(-4.32, -5.6) * mm, "end": v(-4.33, -5.62) * mm});
            skLineSegment(sketch, "E2141", {"start": v(-4.33, -5.62) * mm, "end": v(-4.33, -5.63) * mm});
            skLineSegment(sketch, "E2142", {"start": v(-4.33, -5.63) * mm, "end": v(-4.34, -5.64) * mm});
            skLineSegment(sketch, "E2143", {"start": v(-4.34, -5.64) * mm, "end": v(-4.34, -5.65) * mm});
            skLineSegment(sketch, "E2144", {"start": v(-4.34, -5.65) * mm, "end": v(-4.35, -5.66) * mm});
            skLineSegment(sketch, "E2145", {"start": v(-4.35, -5.66) * mm, "end": v(-4.35, -5.67) * mm});
            skLineSegment(sketch, "E2146", {"start": v(-4.35, -5.67) * mm, "end": v(-4.36, -5.69) * mm});
            skLineSegment(sketch, "E2147", {"start": v(-4.36, -5.69) * mm, "end": v(-4.36, -5.7) * mm});
            skLineSegment(sketch, "E2148", {"start": v(-4.36, -5.7) * mm, "end": v(-4.37, -5.72) * mm});
            skLineSegment(sketch, "E2149", {"start": v(-4.37, -5.72) * mm, "end": v(-4.38, -5.73) * mm});
            skLineSegment(sketch, "E2150", {"start": v(-4.38, -5.73) * mm, "end": v(-4.38, -5.74) * mm});
            skLineSegment(sketch, "E2151", {"start": v(-4.38, -5.74) * mm, "end": v(-4.39, -5.76) * mm});
            skLineSegment(sketch, "E2152", {"start": v(-4.39, -5.76) * mm, "end": v(-4.4, -5.78) * mm});
            skLineSegment(sketch, "E2153", {"start": v(-4.4, -5.78) * mm, "end": v(-4.4, -5.8) * mm});
            skLineSegment(sketch, "E2154", {"start": v(-4.4, -5.8) * mm, "end": v(-4.4, -5.81) * mm});
            skLineSegment(sketch, "E2155", {"start": v(-4.4, -5.81) * mm, "end": v(-4.41, -5.83) * mm});
            skLineSegment(sketch, "E2156", {"start": v(-4.41, -5.83) * mm, "end": v(-4.42, -5.85) * mm});
            skLineSegment(sketch, "E2157", {"start": v(-4.42, -5.85) * mm, "end": v(-4.43, -5.87) * mm});
            skLineSegment(sketch, "E2158", {"start": v(-4.43, -5.87) * mm, "end": v(-4.43, -5.89) * mm});
            skLineSegment(sketch, "E2159", {"start": v(-4.43, -5.89) * mm, "end": v(-4.44, -5.9) * mm});
            skLineSegment(sketch, "E2160", {"start": v(-4.44, -5.9) * mm, "end": v(-4.45, -5.93) * mm});
            skLineSegment(sketch, "E2161", {"start": v(-4.45, -5.93) * mm, "end": v(-4.45, -5.95) * mm});
            skLineSegment(sketch, "E2162", {"start": v(-4.45, -5.95) * mm, "end": v(-4.46, -5.97) * mm});
            skLineSegment(sketch, "E2163", {"start": v(-4.46, -5.97) * mm, "end": v(-4.46, -6) * mm});
            skLineSegment(sketch, "E2164", {"start": v(-4.46, -6) * mm, "end": v(-4.47, -6.02) * mm});
            skLineSegment(sketch, "E2165", {"start": v(-4.47, -6.02) * mm, "end": v(-4.48, -6.04) * mm});
            skLineSegment(sketch, "E2166", {"start": v(-4.48, -6.04) * mm, "end": v(-4.48, -6.06) * mm});
            skLineSegment(sketch, "E2167", {"start": v(-4.48, -6.06) * mm, "end": v(-4.49, -6.09) * mm});
            skLineSegment(sketch, "E2168", {"start": v(-4.49, -6.09) * mm, "end": v(-4.5, -6.11) * mm});
            skLineSegment(sketch, "E2169", {"start": v(-4.5, -6.11) * mm, "end": v(-4.5, -6.14) * mm});
            skLineSegment(sketch, "E2170", {"start": v(-4.5, -6.14) * mm, "end": v(-4.5, -6.16) * mm});
            skLineSegment(sketch, "E2171", {"start": v(-4.5, -6.16) * mm, "end": v(-4.51, -6.2) * mm});
            skLineSegment(sketch, "E2172", {"start": v(-4.51, -6.2) * mm, "end": v(-4.52, -6.22) * mm});
            skLineSegment(sketch, "E2173", {"start": v(-4.52, -6.22) * mm, "end": v(-4.52, -6.25) * mm});
            skLineSegment(sketch, "E2174", {"start": v(-4.52, -6.25) * mm, "end": v(-4.53, -6.28) * mm});
            skLineSegment(sketch, "E2175", {"start": v(-4.53, -6.28) * mm, "end": v(-4.53, -6.3) * mm});
            skLineSegment(sketch, "E2176", {"start": v(-4.53, -6.3) * mm, "end": v(-4.54, -6.33) * mm});
            skLineSegment(sketch, "E2177", {"start": v(-4.54, -6.33) * mm, "end": v(-4.54, -6.36) * mm});
            skLineSegment(sketch, "E2178", {"start": v(-4.54, -6.36) * mm, "end": v(-4.55, -6.4) * mm});
            skLineSegment(sketch, "E2179", {"start": v(-4.55, -6.4) * mm, "end": v(-4.55, -6.43) * mm});
            skLineSegment(sketch, "E2180", {"start": v(-4.55, -6.43) * mm, "end": v(-4.55, -6.46) * mm});
            skLineSegment(sketch, "E2181", {"start": v(-4.55, -6.46) * mm, "end": v(-4.56, -6.49) * mm});
            skLineSegment(sketch, "E2182", {"start": v(-4.56, -6.49) * mm, "end": v(-4.56, -6.52) * mm});
            skArc(sketch, "E2183", {"start": v(-4.56, -6.52) * mm, "mid": v(-4.45, -6.6) * mm, "end": v(-4.34, -6.67) * mm});
            skLineSegment(sketch, "E2184", {"start": v(-4.53, -5.42) * mm, "end": v(-4.53, -5.41) * mm});
            skLineSegment(sketch, "E2185", {"start": v(-4.53, -5.41) * mm, "end": v(-4.54, -5.41) * mm});
            skLineSegment(sketch, "E2186", {"start": v(-4.54, -5.41) * mm, "end": v(-4.55, -5.41) * mm});
            skLineSegment(sketch, "E2187", {"start": v(-4.55, -5.41) * mm, "end": v(-4.56, -5.42) * mm});
            skLineSegment(sketch, "E2188", {"start": v(-4.56, -5.42) * mm, "end": v(-4.57, -5.42) * mm});
            skLineSegment(sketch, "E2189", {"start": v(-4.57, -5.42) * mm, "end": v(-4.58, -5.43) * mm});
            skLineSegment(sketch, "E2190", {"start": v(-4.58, -5.43) * mm, "end": v(-4.6, -5.44) * mm});
            skLineSegment(sketch, "E2191", {"start": v(-4.6, -5.44) * mm, "end": v(-4.6, -5.44) * mm});
            skLineSegment(sketch, "E2192", {"start": v(-4.6, -5.44) * mm, "end": v(-4.6, -5.45) * mm});
            skLineSegment(sketch, "E2193", {"start": v(-4.6, -5.45) * mm, "end": v(-4.62, -5.46) * mm});
            skLineSegment(sketch, "E2194", {"start": v(-4.62, -5.46) * mm, "end": v(-4.63, -5.46) * mm});
            skLineSegment(sketch, "E2195", {"start": v(-4.63, -5.46) * mm, "end": v(-4.64, -5.47) * mm});
            skLineSegment(sketch, "E2196", {"start": v(-4.64, -5.47) * mm, "end": v(-4.66, -5.48) * mm});
            skLineSegment(sketch, "E2197", {"start": v(-4.66, -5.48) * mm, "end": v(-4.67, -5.5) * mm});
            skLineSegment(sketch, "E2198", {"start": v(-4.67, -5.5) * mm, "end": v(-4.68, -5.5) * mm});
            skLineSegment(sketch, "E2199", {"start": v(-4.68, -5.5) * mm, "end": v(-4.7, -5.51) * mm});
            skLineSegment(sketch, "E2200", {"start": v(-4.7, -5.51) * mm, "end": v(-4.71, -5.52) * mm});
            skLineSegment(sketch, "E2201", {"start": v(-4.71, -5.52) * mm, "end": v(-4.73, -5.53) * mm});
            skLineSegment(sketch, "E2202", {"start": v(-4.73, -5.53) * mm, "end": v(-4.74, -5.54) * mm});
            skLineSegment(sketch, "E2203", {"start": v(-4.74, -5.54) * mm, "end": v(-4.76, -5.55) * mm});
            skLineSegment(sketch, "E2204", {"start": v(-4.76, -5.55) * mm, "end": v(-4.78, -5.56) * mm});
            skLineSegment(sketch, "E2205", {"start": v(-4.78, -5.56) * mm, "end": v(-4.8, -5.57) * mm});
            skLineSegment(sketch, "E2206", {"start": v(-4.8, -5.57) * mm, "end": v(-4.81, -5.58) * mm});
            skLineSegment(sketch, "E2207", {"start": v(-4.81, -5.58) * mm, "end": v(-4.83, -5.6) * mm});
            skLineSegment(sketch, "E2208", {"start": v(-4.83, -5.6) * mm, "end": v(-4.85, -5.6) * mm});
            skLineSegment(sketch, "E2209", {"start": v(-4.85, -5.6) * mm, "end": v(-4.87, -5.61) * mm});
            skLineSegment(sketch, "E2210", {"start": v(-4.87, -5.61) * mm, "end": v(-4.89, -5.62) * mm});
            skLineSegment(sketch, "E2211", {"start": v(-4.89, -5.62) * mm, "end": v(-4.9, -5.63) * mm});
            skLineSegment(sketch, "E2212", {"start": v(-4.9, -5.63) * mm, "end": v(-4.93, -5.64) * mm});
            skLineSegment(sketch, "E2213", {"start": v(-4.93, -5.64) * mm, "end": v(-4.95, -5.66) * mm});
            skLineSegment(sketch, "E2214", {"start": v(-4.95, -5.66) * mm, "end": v(-4.97, -5.67) * mm});
            skLineSegment(sketch, "E2215", {"start": v(-4.97, -5.67) * mm, "end": v(-5, -5.68) * mm});
            skLineSegment(sketch, "E2216", {"start": v(-5, -5.68) * mm, "end": v(-5.02, -5.69) * mm});
            skLineSegment(sketch, "E2217", {"start": v(-5.02, -5.69) * mm, "end": v(-5.04, -5.7) * mm});
            skLineSegment(sketch, "E2218", {"start": v(-5.04, -5.7) * mm, "end": v(-5.07, -5.71) * mm});
            skLineSegment(sketch, "E2219", {"start": v(-5.07, -5.71) * mm, "end": v(-5.1, -5.72) * mm});
            skLineSegment(sketch, "E2220", {"start": v(-5.1, -5.72) * mm, "end": v(-5.12, -5.73) * mm});
            skLineSegment(sketch, "E2221", {"start": v(-5.12, -5.73) * mm, "end": v(-5.14, -5.74) * mm});
            skLineSegment(sketch, "E2222", {"start": v(-5.14, -5.74) * mm, "end": v(-5.17, -5.75) * mm});
            skLineSegment(sketch, "E2223", {"start": v(-5.17, -5.75) * mm, "end": v(-5.2, -5.77) * mm});
            skLineSegment(sketch, "E2224", {"start": v(-5.2, -5.77) * mm, "end": v(-5.23, -5.78) * mm});
            skLineSegment(sketch, "E2225", {"start": v(-5.23, -5.78) * mm, "end": v(-5.26, -5.79) * mm});
            skLineSegment(sketch, "E2226", {"start": v(-5.26, -5.79) * mm, "end": v(-5.28, -5.8) * mm});
            skLineSegment(sketch, "E2227", {"start": v(-5.28, -5.8) * mm, "end": v(-5.31, -5.8) * mm});
            skLineSegment(sketch, "E2228", {"start": v(-5.31, -5.8) * mm, "end": v(-5.34, -5.82) * mm});
            skLineSegment(sketch, "E2229", {"start": v(-5.34, -5.82) * mm, "end": v(-5.38, -5.83) * mm});
            skLineSegment(sketch, "E2230", {"start": v(-5.38, -5.83) * mm, "end": v(-5.4, -5.84) * mm});
            skLineSegment(sketch, "E2231", {"start": v(-5.2, -4.76) * mm, "end": v(-5.2, -4.77) * mm});
            skLineSegment(sketch, "E2232", {"start": v(-5.2, -4.77) * mm, "end": v(-5.2, -4.77) * mm});
            skLineSegment(sketch, "E2233", {"start": v(-5.2, -4.77) * mm, "end": v(-5.2, -4.78) * mm});
            skLineSegment(sketch, "E2234", {"start": v(-5.2, -4.78) * mm, "end": v(-5.2, -4.8) * mm});
            skLineSegment(sketch, "E2235", {"start": v(-5.2, -4.8) * mm, "end": v(-5.21, -4.8) * mm});
            skLineSegment(sketch, "E2236", {"start": v(-5.21, -4.8) * mm, "end": v(-5.22, -4.82) * mm});
            skLineSegment(sketch, "E2237", {"start": v(-5.22, -4.82) * mm, "end": v(-5.23, -4.83) * mm});
            skLineSegment(sketch, "E2238", {"start": v(-5.23, -4.83) * mm, "end": v(-5.23, -4.83) * mm});
            skLineSegment(sketch, "E2239", {"start": v(-5.23, -4.83) * mm, "end": v(-5.24, -4.85) * mm});
            skLineSegment(sketch, "E2240", {"start": v(-5.24, -4.85) * mm, "end": v(-5.25, -4.86) * mm});
            skLineSegment(sketch, "E2241", {"start": v(-5.25, -4.86) * mm, "end": v(-5.25, -4.87) * mm});
            skLineSegment(sketch, "E2242", {"start": v(-5.25, -4.87) * mm, "end": v(-5.26, -4.88) * mm});
            skLineSegment(sketch, "E2243", {"start": v(-5.26, -4.88) * mm, "end": v(-5.27, -4.9) * mm});
            skLineSegment(sketch, "E2244", {"start": v(-5.27, -4.9) * mm, "end": v(-5.28, -4.9) * mm});
            skLineSegment(sketch, "E2245", {"start": v(-5.28, -4.9) * mm, "end": v(-5.29, -4.92) * mm});
            skLineSegment(sketch, "E2246", {"start": v(-5.29, -4.92) * mm, "end": v(-5.3, -4.94) * mm});
            skLineSegment(sketch, "E2247", {"start": v(-5.3, -4.94) * mm, "end": v(-5.3, -4.95) * mm});
            skLineSegment(sketch, "E2248", {"start": v(-5.3, -4.95) * mm, "end": v(-5.31, -4.97) * mm});
            skLineSegment(sketch, "E2249", {"start": v(-5.31, -4.97) * mm, "end": v(-5.32, -4.98) * mm});
            skLineSegment(sketch, "E2250", {"start": v(-5.32, -4.98) * mm, "end": v(-5.33, -5) * mm});
            skLineSegment(sketch, "E2251", {"start": v(-5.33, -5) * mm, "end": v(-5.34, -5.02) * mm});
            skLineSegment(sketch, "E2252", {"start": v(-5.34, -5.02) * mm, "end": v(-5.35, -5.03) * mm});
            skLineSegment(sketch, "E2253", {"start": v(-5.35, -5.03) * mm, "end": v(-5.36, -5.05) * mm});
            skLineSegment(sketch, "E2254", {"start": v(-5.36, -5.05) * mm, "end": v(-5.37, -5.07) * mm});
            skLineSegment(sketch, "E2255", {"start": v(-5.37, -5.07) * mm, "end": v(-5.38, -5.1) * mm});
            skLineSegment(sketch, "E2256", {"start": v(-5.38, -5.1) * mm, "end": v(-5.4, -5.11) * mm});
            skLineSegment(sketch, "E2257", {"start": v(-5.4, -5.11) * mm, "end": v(-5.4, -5.13) * mm});
            skLineSegment(sketch, "E2258", {"start": v(-5.4, -5.13) * mm, "end": v(-5.41, -5.15) * mm});
            skLineSegment(sketch, "E2259", {"start": v(-5.41, -5.15) * mm, "end": v(-5.42, -5.17) * mm});
            skLineSegment(sketch, "E2260", {"start": v(-5.42, -5.17) * mm, "end": v(-5.43, -5.2) * mm});
            skLineSegment(sketch, "E2261", {"start": v(-5.43, -5.2) * mm, "end": v(-5.44, -5.22) * mm});
            skLineSegment(sketch, "E2262", {"start": v(-5.44, -5.22) * mm, "end": v(-5.45, -5.24) * mm});
            skLineSegment(sketch, "E2263", {"start": v(-5.45, -5.24) * mm, "end": v(-5.46, -5.27) * mm});
            skLineSegment(sketch, "E2264", {"start": v(-5.46, -5.27) * mm, "end": v(-5.47, -5.29) * mm});
            skLineSegment(sketch, "E2265", {"start": v(-5.47, -5.29) * mm, "end": v(-5.48, -5.31) * mm});
            skLineSegment(sketch, "E2266", {"start": v(-5.48, -5.31) * mm, "end": v(-5.5, -5.34) * mm});
            skLineSegment(sketch, "E2267", {"start": v(-5.5, -5.34) * mm, "end": v(-5.5, -5.37) * mm});
            skLineSegment(sketch, "E2268", {"start": v(-5.5, -5.37) * mm, "end": v(-5.51, -5.4) * mm});
            skLineSegment(sketch, "E2269", {"start": v(-5.51, -5.4) * mm, "end": v(-5.52, -5.42) * mm});
            skLineSegment(sketch, "E2270", {"start": v(-5.52, -5.42) * mm, "end": v(-5.53, -5.45) * mm});
            skLineSegment(sketch, "E2271", {"start": v(-5.53, -5.45) * mm, "end": v(-5.54, -5.48) * mm});
            skLineSegment(sketch, "E2272", {"start": v(-5.54, -5.48) * mm, "end": v(-5.55, -5.5) * mm});
            skLineSegment(sketch, "E2273", {"start": v(-5.55, -5.5) * mm, "end": v(-5.56, -5.53) * mm});
            skLineSegment(sketch, "E2274", {"start": v(-5.56, -5.53) * mm, "end": v(-5.57, -5.56) * mm});
            skLineSegment(sketch, "E2275", {"start": v(-5.57, -5.56) * mm, "end": v(-5.58, -5.6) * mm});
            skLineSegment(sketch, "E2276", {"start": v(-5.58, -5.6) * mm, "end": v(-5.59, -5.63) * mm});
            skLineSegment(sketch, "E2277", {"start": v(-5.59, -5.63) * mm, "end": v(-5.6, -5.66) * mm});
            skArc(sketch, "E2278", {"start": v(-5.6, -5.66) * mm, "mid": v(-5.5, -5.75) * mm, "end": v(-5.4, -5.84) * mm});
            skLineSegment(sketch, "E2279", {"start": v(-5.38, -4.57) * mm, "end": v(-5.38, -4.57) * mm});
            skLineSegment(sketch, "E2280", {"start": v(-5.38, -4.57) * mm, "end": v(-5.39, -4.57) * mm});
            skLineSegment(sketch, "E2281", {"start": v(-5.39, -4.57) * mm, "end": v(-5.4, -4.57) * mm});
            skLineSegment(sketch, "E2282", {"start": v(-5.4, -4.57) * mm, "end": v(-5.4, -4.57) * mm});
            skLineSegment(sketch, "E2283", {"start": v(-5.4, -4.57) * mm, "end": v(-5.42, -4.57) * mm});
            skLineSegment(sketch, "E2284", {"start": v(-5.42, -4.57) * mm, "end": v(-5.43, -4.58) * mm});
            skLineSegment(sketch, "E2285", {"start": v(-5.43, -4.58) * mm, "end": v(-5.44, -4.58) * mm});
            skLineSegment(sketch, "E2286", {"start": v(-5.44, -4.58) * mm, "end": v(-5.45, -4.58) * mm});
            skLineSegment(sketch, "E2287", {"start": v(-5.45, -4.58) * mm, "end": v(-5.46, -4.6) * mm});
            skLineSegment(sketch, "E2288", {"start": v(-5.46, -4.6) * mm, "end": v(-5.47, -4.6) * mm});
            skLineSegment(sketch, "E2289", {"start": v(-5.47, -4.6) * mm, "end": v(-5.49, -4.6) * mm});
            skLineSegment(sketch, "E2290", {"start": v(-5.49, -4.6) * mm, "end": v(-5.5, -4.61) * mm});
            skLineSegment(sketch, "E2291", {"start": v(-5.5, -4.61) * mm, "end": v(-5.52, -4.62) * mm});
            skLineSegment(sketch, "E2292", {"start": v(-5.52, -4.62) * mm, "end": v(-5.53, -4.62) * mm});
            skLineSegment(sketch, "E2293", {"start": v(-5.53, -4.62) * mm, "end": v(-5.54, -4.63) * mm});
            skLineSegment(sketch, "E2294", {"start": v(-5.54, -4.63) * mm, "end": v(-5.56, -4.64) * mm});
            skLineSegment(sketch, "E2295", {"start": v(-5.56, -4.64) * mm, "end": v(-5.58, -4.64) * mm});
            skLineSegment(sketch, "E2296", {"start": v(-5.58, -4.64) * mm, "end": v(-5.6, -4.65) * mm});
            skLineSegment(sketch, "E2297", {"start": v(-5.6, -4.65) * mm, "end": v(-5.6, -4.66) * mm});
            skLineSegment(sketch, "E2298", {"start": v(-5.6, -4.66) * mm, "end": v(-5.63, -4.67) * mm});
            skLineSegment(sketch, "E2299", {"start": v(-5.63, -4.67) * mm, "end": v(-5.65, -4.67) * mm});
            skLineSegment(sketch, "E2300", {"start": v(-5.65, -4.67) * mm, "end": v(-5.66, -4.68) * mm});
            skLineSegment(sketch, "E2301", {"start": v(-5.66, -4.68) * mm, "end": v(-5.68, -4.69) * mm});
            skLineSegment(sketch, "E2302", {"start": v(-5.68, -4.69) * mm, "end": v(-5.7, -4.7) * mm});
            skLineSegment(sketch, "E2303", {"start": v(-5.7, -4.7) * mm, "end": v(-5.72, -4.7) * mm});
            skLineSegment(sketch, "E2304", {"start": v(-5.72, -4.7) * mm, "end": v(-5.74, -4.7) * mm});
            skLineSegment(sketch, "E2305", {"start": v(-5.74, -4.7) * mm, "end": v(-5.77, -4.72) * mm});
            skLineSegment(sketch, "E2306", {"start": v(-5.77, -4.72) * mm, "end": v(-5.79, -4.72) * mm});
            skLineSegment(sketch, "E2307", {"start": v(-5.79, -4.72) * mm, "end": v(-5.81, -4.73) * mm});
            skLineSegment(sketch, "E2308", {"start": v(-5.81, -4.73) * mm, "end": v(-5.83, -4.74) * mm});
            skLineSegment(sketch, "E2309", {"start": v(-5.83, -4.74) * mm, "end": v(-5.86, -4.74) * mm});
            skLineSegment(sketch, "E2310", {"start": v(-5.86, -4.74) * mm, "end": v(-5.88, -4.75) * mm});
            skLineSegment(sketch, "E2311", {"start": v(-5.88, -4.75) * mm, "end": v(-5.9, -4.76) * mm});
            skLineSegment(sketch, "E2312", {"start": v(-5.9, -4.76) * mm, "end": v(-5.93, -4.77) * mm});
            skLineSegment(sketch, "E2313", {"start": v(-5.93, -4.77) * mm, "end": v(-5.96, -4.77) * mm});
            skLineSegment(sketch, "E2314", {"start": v(-5.96, -4.77) * mm, "end": v(-5.99, -4.78) * mm});
            skLineSegment(sketch, "E2315", {"start": v(-5.99, -4.78) * mm, "end": v(-6.01, -4.79) * mm});
            skLineSegment(sketch, "E2316", {"start": v(-6.01, -4.79) * mm, "end": v(-6.04, -4.8) * mm});
            skLineSegment(sketch, "E2317", {"start": v(-6.04, -4.8) * mm, "end": v(-6.07, -4.8) * mm});
            skLineSegment(sketch, "E2318", {"start": v(-6.07, -4.8) * mm, "end": v(-6.1, -4.8) * mm});
            skLineSegment(sketch, "E2319", {"start": v(-6.1, -4.8) * mm, "end": v(-6.13, -4.81) * mm});
            skLineSegment(sketch, "E2320", {"start": v(-6.13, -4.81) * mm, "end": v(-6.16, -4.82) * mm});
            skLineSegment(sketch, "E2321", {"start": v(-6.16, -4.82) * mm, "end": v(-6.19, -4.82) * mm});
            skLineSegment(sketch, "E2322", {"start": v(-6.19, -4.82) * mm, "end": v(-6.22, -4.83) * mm});
            skLineSegment(sketch, "E2323", {"start": v(-6.22, -4.83) * mm, "end": v(-6.25, -4.83) * mm});
            skLineSegment(sketch, "E2324", {"start": v(-6.25, -4.83) * mm, "end": v(-6.28, -4.84) * mm});
            skLineSegment(sketch, "E2325", {"start": v(-6.28, -4.84) * mm, "end": v(-6.31, -4.84) * mm});
            skLineSegment(sketch, "E2326", {"start": v(-5.94, -3.81) * mm, "end": v(-5.94, -3.82) * mm});
            skLineSegment(sketch, "E2327", {"start": v(-5.94, -3.82) * mm, "end": v(-5.94, -3.83) * mm});
            skLineSegment(sketch, "E2328", {"start": v(-5.94, -3.83) * mm, "end": v(-5.94, -3.83) * mm});
            skLineSegment(sketch, "E2329", {"start": v(-5.94, -3.83) * mm, "end": v(-5.94, -3.84) * mm});
            skLineSegment(sketch, "E2330", {"start": v(-5.94, -3.84) * mm, "end": v(-5.95, -3.85) * mm});
            skLineSegment(sketch, "E2331", {"start": v(-5.95, -3.85) * mm, "end": v(-5.96, -3.86) * mm});
            skLineSegment(sketch, "E2332", {"start": v(-5.96, -3.86) * mm, "end": v(-5.97, -3.88) * mm});
            skLineSegment(sketch, "E2333", {"start": v(-5.97, -3.88) * mm, "end": v(-5.97, -3.88) * mm});
            skLineSegment(sketch, "E2334", {"start": v(-5.97, -3.88) * mm, "end": v(-5.98, -3.9) * mm});
            skLineSegment(sketch, "E2335", {"start": v(-5.98, -3.9) * mm, "end": v(-5.99, -3.9) * mm});
            skLineSegment(sketch, "E2336", {"start": v(-5.99, -3.9) * mm, "end": v(-6, -3.91) * mm});
            skLineSegment(sketch, "E2337", {"start": v(-6, -3.91) * mm, "end": v(-6, -3.92) * mm});
            skLineSegment(sketch, "E2338", {"start": v(-6, -3.92) * mm, "end": v(-6.02, -3.93) * mm});
            skLineSegment(sketch, "E2339", {"start": v(-6.02, -3.93) * mm, "end": v(-6.03, -3.95) * mm});
            skLineSegment(sketch, "E2340", {"start": v(-6.03, -3.95) * mm, "end": v(-6.04, -3.96) * mm});
            skLineSegment(sketch, "E2341", {"start": v(-6.04, -3.96) * mm, "end": v(-6.05, -3.97) * mm});
            skLineSegment(sketch, "E2342", {"start": v(-6.05, -3.97) * mm, "end": v(-6.06, -3.98) * mm});
            skLineSegment(sketch, "E2343", {"start": v(-6.06, -3.98) * mm, "end": v(-6.08, -4) * mm});
            skLineSegment(sketch, "E2344", {"start": v(-6.08, -4) * mm, "end": v(-6.09, -4.01) * mm});
            skLineSegment(sketch, "E2345", {"start": v(-6.09, -4.01) * mm, "end": v(-6.1, -4.03) * mm});
            skLineSegment(sketch, "E2346", {"start": v(-6.1, -4.03) * mm, "end": v(-6.11, -4.04) * mm});
            skLineSegment(sketch, "E2347", {"start": v(-6.11, -4.04) * mm, "end": v(-6.12, -4.06) * mm});
            skLineSegment(sketch, "E2348", {"start": v(-6.12, -4.06) * mm, "end": v(-6.14, -4.07) * mm});
            skLineSegment(sketch, "E2349", {"start": v(-6.14, -4.07) * mm, "end": v(-6.15, -4.1) * mm});
            skLineSegment(sketch, "E2350", {"start": v(-6.15, -4.1) * mm, "end": v(-6.16, -4.1) * mm});
            skLineSegment(sketch, "E2351", {"start": v(-6.16, -4.1) * mm, "end": v(-6.18, -4.13) * mm});
            skLineSegment(sketch, "E2352", {"start": v(-6.18, -4.13) * mm, "end": v(-6.19, -4.14) * mm});
            skLineSegment(sketch, "E2353", {"start": v(-6.19, -4.14) * mm, "end": v(-6.2, -4.16) * mm});
            skLineSegment(sketch, "E2354", {"start": v(-6.2, -4.16) * mm, "end": v(-6.22, -4.18) * mm});
            skLineSegment(sketch, "E2355", {"start": v(-6.22, -4.18) * mm, "end": v(-6.23, -4.2) * mm});
            skLineSegment(sketch, "E2356", {"start": v(-6.23, -4.2) * mm, "end": v(-6.24, -4.22) * mm});
            skLineSegment(sketch, "E2357", {"start": v(-6.24, -4.22) * mm, "end": v(-6.26, -4.25) * mm});
            skLineSegment(sketch, "E2358", {"start": v(-6.26, -4.25) * mm, "end": v(-6.27, -4.27) * mm});
            skLineSegment(sketch, "E2359", {"start": v(-6.27, -4.27) * mm, "end": v(-6.28, -4.29) * mm});
            skLineSegment(sketch, "E2360", {"start": v(-6.28, -4.29) * mm, "end": v(-6.3, -4.31) * mm});
            skLineSegment(sketch, "E2361", {"start": v(-6.3, -4.31) * mm, "end": v(-6.31, -4.34) * mm});
            skLineSegment(sketch, "E2362", {"start": v(-6.31, -4.34) * mm, "end": v(-6.33, -4.36) * mm});
            skLineSegment(sketch, "E2363", {"start": v(-6.33, -4.36) * mm, "end": v(-6.34, -4.38) * mm});
            skLineSegment(sketch, "E2364", {"start": v(-6.34, -4.38) * mm, "end": v(-6.36, -4.4) * mm});
            skLineSegment(sketch, "E2365", {"start": v(-6.36, -4.4) * mm, "end": v(-6.37, -4.43) * mm});
            skLineSegment(sketch, "E2366", {"start": v(-6.37, -4.43) * mm, "end": v(-6.38, -4.46) * mm});
            skLineSegment(sketch, "E2367", {"start": v(-6.38, -4.46) * mm, "end": v(-6.4, -4.49) * mm});
            skLineSegment(sketch, "E2368", {"start": v(-6.4, -4.49) * mm, "end": v(-6.41, -4.52) * mm});
            skLineSegment(sketch, "E2369", {"start": v(-6.41, -4.52) * mm, "end": v(-6.43, -4.54) * mm});
            skLineSegment(sketch, "E2370", {"start": v(-6.43, -4.54) * mm, "end": v(-6.44, -4.57) * mm});
            skLineSegment(sketch, "E2371", {"start": v(-6.44, -4.57) * mm, "end": v(-6.46, -4.6) * mm});
            skLineSegment(sketch, "E2372", {"start": v(-6.46, -4.6) * mm, "end": v(-6.47, -4.63) * mm});
            skArc(sketch, "E2373", {"start": v(-6.47, -4.63) * mm, "mid": v(-6.4, -4.74) * mm, "end": v(-6.31, -4.84) * mm});
            skLineSegment(sketch, "E2374", {"start": v(-6.07, -3.6) * mm, "end": v(-6.07, -3.6) * mm});
            skLineSegment(sketch, "E2375", {"start": v(-6.07, -3.6) * mm, "end": v(-6.08, -3.6) * mm});
            skLineSegment(sketch, "E2376", {"start": v(-6.08, -3.6) * mm, "end": v(-6.09, -3.59) * mm});
            skLineSegment(sketch, "E2377", {"start": v(-6.09, -3.59) * mm, "end": v(-6.1, -3.59) * mm});
            skLineSegment(sketch, "E2378", {"start": v(-6.1, -3.59) * mm, "end": v(-6.11, -3.59) * mm});
            skLineSegment(sketch, "E2379", {"start": v(-6.11, -3.59) * mm, "end": v(-6.12, -3.6) * mm});
            skLineSegment(sketch, "E2380", {"start": v(-6.12, -3.6) * mm, "end": v(-6.14, -3.6) * mm});
            skLineSegment(sketch, "E2381", {"start": v(-6.14, -3.6) * mm, "end": v(-6.15, -3.6) * mm});
            skLineSegment(sketch, "E2382", {"start": v(-6.15, -3.6) * mm, "end": v(-6.16, -3.6) * mm});
            skLineSegment(sketch, "E2383", {"start": v(-6.16, -3.6) * mm, "end": v(-6.17, -3.6) * mm});
            skLineSegment(sketch, "E2384", {"start": v(-6.17, -3.6) * mm, "end": v(-6.19, -3.6) * mm});
            skLineSegment(sketch, "E2385", {"start": v(-6.19, -3.6) * mm, "end": v(-6.2, -3.61) * mm});
            skLineSegment(sketch, "E2386", {"start": v(-6.2, -3.61) * mm, "end": v(-6.21, -3.62) * mm});
            skLineSegment(sketch, "E2387", {"start": v(-6.21, -3.62) * mm, "end": v(-6.23, -3.62) * mm});
            skLineSegment(sketch, "E2388", {"start": v(-6.23, -3.62) * mm, "end": v(-6.25, -3.63) * mm});
            skLineSegment(sketch, "E2389", {"start": v(-6.25, -3.63) * mm, "end": v(-6.26, -3.63) * mm});
            skLineSegment(sketch, "E2390", {"start": v(-6.26, -3.63) * mm, "end": v(-6.28, -3.64) * mm});
            skLineSegment(sketch, "E2391", {"start": v(-6.28, -3.64) * mm, "end": v(-6.3, -3.64) * mm});
            skLineSegment(sketch, "E2392", {"start": v(-6.3, -3.64) * mm, "end": v(-6.31, -3.64) * mm});
            skLineSegment(sketch, "E2393", {"start": v(-6.31, -3.64) * mm, "end": v(-6.33, -3.65) * mm});
            skLineSegment(sketch, "E2394", {"start": v(-6.33, -3.65) * mm, "end": v(-6.35, -3.65) * mm});
            skLineSegment(sketch, "E2395", {"start": v(-6.35, -3.65) * mm, "end": v(-6.37, -3.66) * mm});
            skLineSegment(sketch, "E2396", {"start": v(-6.37, -3.66) * mm, "end": v(-6.4, -3.66) * mm});
            skLineSegment(sketch, "E2397", {"start": v(-6.4, -3.66) * mm, "end": v(-6.41, -3.66) * mm});
            skLineSegment(sketch, "E2398", {"start": v(-6.41, -3.66) * mm, "end": v(-6.43, -3.67) * mm});
            skLineSegment(sketch, "E2399", {"start": v(-6.43, -3.67) * mm, "end": v(-6.46, -3.67) * mm});
            skLineSegment(sketch, "E2400", {"start": v(-6.46, -3.67) * mm, "end": v(-6.48, -3.67) * mm});
            skLineSegment(sketch, "E2401", {"start": v(-6.48, -3.67) * mm, "end": v(-6.5, -3.68) * mm});
            skLineSegment(sketch, "E2402", {"start": v(-6.5, -3.68) * mm, "end": v(-6.53, -3.68) * mm});
            skLineSegment(sketch, "E2403", {"start": v(-6.53, -3.68) * mm, "end": v(-6.55, -3.68) * mm});
            skLineSegment(sketch, "E2404", {"start": v(-6.55, -3.68) * mm, "end": v(-6.57, -3.69) * mm});
            skLineSegment(sketch, "E2405", {"start": v(-6.57, -3.69) * mm, "end": v(-6.6, -3.69) * mm});
            skLineSegment(sketch, "E2406", {"start": v(-6.6, -3.69) * mm, "end": v(-6.62, -3.7) * mm});
            skLineSegment(sketch, "E2407", {"start": v(-6.62, -3.7) * mm, "end": v(-6.65, -3.7) * mm});
            skLineSegment(sketch, "E2408", {"start": v(-6.65, -3.7) * mm, "end": v(-6.68, -3.7) * mm});
            skLineSegment(sketch, "E2409", {"start": v(-6.68, -3.7) * mm, "end": v(-6.7, -3.7) * mm});
            skLineSegment(sketch, "E2410", {"start": v(-6.7, -3.7) * mm, "end": v(-6.73, -3.7) * mm});
            skLineSegment(sketch, "E2411", {"start": v(-6.73, -3.7) * mm, "end": v(-6.76, -3.7) * mm});
            skLineSegment(sketch, "E2412", {"start": v(-6.76, -3.7) * mm, "end": v(-6.8, -3.7) * mm});
            skLineSegment(sketch, "E2413", {"start": v(-6.8, -3.7) * mm, "end": v(-6.82, -3.7) * mm});
            skLineSegment(sketch, "E2414", {"start": v(-6.82, -3.7) * mm, "end": v(-6.85, -3.7) * mm});
            skLineSegment(sketch, "E2415", {"start": v(-6.85, -3.7) * mm, "end": v(-6.88, -3.7) * mm});
            skLineSegment(sketch, "E2416", {"start": v(-6.88, -3.7) * mm, "end": v(-6.91, -3.7) * mm});
            skLineSegment(sketch, "E2417", {"start": v(-6.91, -3.7) * mm, "end": v(-6.94, -3.7) * mm});
            skLineSegment(sketch, "E2418", {"start": v(-6.94, -3.7) * mm, "end": v(-6.97, -3.7) * mm});
            skLineSegment(sketch, "E2419", {"start": v(-6.97, -3.7) * mm, "end": v(-7, -3.7) * mm});
            skLineSegment(sketch, "E2420", {"start": v(-7, -3.7) * mm, "end": v(-7.04, -3.7) * mm});
            skLineSegment(sketch, "E2421", {"start": v(-6.5, -2.76) * mm, "end": v(-6.5, -2.76) * mm});
            skLineSegment(sketch, "E2422", {"start": v(-6.5, -2.76) * mm, "end": v(-6.5, -2.77) * mm});
            skLineSegment(sketch, "E2423", {"start": v(-6.5, -2.77) * mm, "end": v(-6.5, -2.78) * mm});
            skLineSegment(sketch, "E2424", {"start": v(-6.5, -2.78) * mm, "end": v(-6.5, -2.78) * mm});
            skLineSegment(sketch, "E2425", {"start": v(-6.5, -2.78) * mm, "end": v(-6.51, -2.8) * mm});
            skLineSegment(sketch, "E2426", {"start": v(-6.51, -2.8) * mm, "end": v(-6.52, -2.8) * mm});
            skLineSegment(sketch, "E2427", {"start": v(-6.52, -2.8) * mm, "end": v(-6.53, -2.81) * mm});
            skLineSegment(sketch, "E2428", {"start": v(-6.53, -2.81) * mm, "end": v(-6.54, -2.82) * mm});
            skLineSegment(sketch, "E2429", {"start": v(-6.54, -2.82) * mm, "end": v(-6.55, -2.82) * mm});
            skLineSegment(sketch, "E2430", {"start": v(-6.55, -2.82) * mm, "end": v(-6.56, -2.83) * mm});
            skLineSegment(sketch, "E2431", {"start": v(-6.56, -2.83) * mm, "end": v(-6.57, -2.84) * mm});
            skLineSegment(sketch, "E2432", {"start": v(-6.57, -2.84) * mm, "end": v(-6.58, -2.85) * mm});
            skLineSegment(sketch, "E2433", {"start": v(-6.58, -2.85) * mm, "end": v(-6.6, -2.86) * mm});
            skLineSegment(sketch, "E2434", {"start": v(-6.6, -2.86) * mm, "end": v(-6.6, -2.87) * mm});
            skLineSegment(sketch, "E2435", {"start": v(-6.6, -2.87) * mm, "end": v(-6.62, -2.88) * mm});
            skLineSegment(sketch, "E2436", {"start": v(-6.62, -2.88) * mm, "end": v(-6.64, -2.9) * mm});
            skLineSegment(sketch, "E2437", {"start": v(-6.64, -2.9) * mm, "end": v(-6.65, -2.9) * mm});
            skLineSegment(sketch, "E2438", {"start": v(-6.65, -2.9) * mm, "end": v(-6.66, -2.91) * mm});
            skLineSegment(sketch, "E2439", {"start": v(-6.66, -2.91) * mm, "end": v(-6.68, -2.93) * mm});
            skLineSegment(sketch, "E2440", {"start": v(-6.68, -2.93) * mm, "end": v(-6.7, -2.94) * mm});
            skLineSegment(sketch, "E2441", {"start": v(-6.7, -2.94) * mm, "end": v(-6.7, -2.95) * mm});
            skLineSegment(sketch, "E2442", {"start": v(-6.7, -2.95) * mm, "end": v(-6.72, -2.96) * mm});
            skLineSegment(sketch, "E2443", {"start": v(-6.72, -2.96) * mm, "end": v(-6.74, -2.98) * mm});
            skLineSegment(sketch, "E2444", {"start": v(-6.74, -2.98) * mm, "end": v(-6.75, -3) * mm});
            skLineSegment(sketch, "E2445", {"start": v(-6.75, -3) * mm, "end": v(-6.77, -3) * mm});
            skLineSegment(sketch, "E2446", {"start": v(-6.77, -3) * mm, "end": v(-6.78, -3.02) * mm});
            skLineSegment(sketch, "E2447", {"start": v(-6.78, -3.02) * mm, "end": v(-6.8, -3.04) * mm});
            skLineSegment(sketch, "E2448", {"start": v(-6.8, -3.04) * mm, "end": v(-6.82, -3.06) * mm});
            skLineSegment(sketch, "E2449", {"start": v(-6.82, -3.06) * mm, "end": v(-6.83, -3.07) * mm});
            skLineSegment(sketch, "E2450", {"start": v(-6.83, -3.07) * mm, "end": v(-6.85, -3.1) * mm});
            skLineSegment(sketch, "E2451", {"start": v(-6.85, -3.1) * mm, "end": v(-6.87, -3.1) * mm});
            skLineSegment(sketch, "E2452", {"start": v(-6.87, -3.1) * mm, "end": v(-6.88, -3.13) * mm});
            skLineSegment(sketch, "E2453", {"start": v(-6.88, -3.13) * mm, "end": v(-6.9, -3.15) * mm});
            skLineSegment(sketch, "E2454", {"start": v(-6.9, -3.15) * mm, "end": v(-6.92, -3.17) * mm});
            skLineSegment(sketch, "E2455", {"start": v(-6.92, -3.17) * mm, "end": v(-6.94, -3.19) * mm});
            skLineSegment(sketch, "E2456", {"start": v(-6.94, -3.19) * mm, "end": v(-6.95, -3.2) * mm});
            skLineSegment(sketch, "E2457", {"start": v(-6.95, -3.2) * mm, "end": v(-6.97, -3.23) * mm});
            skLineSegment(sketch, "E2458", {"start": v(-6.97, -3.23) * mm, "end": v(-6.99, -3.25) * mm});
            skLineSegment(sketch, "E2459", {"start": v(-6.99, -3.25) * mm, "end": v(-7, -3.27) * mm});
            skLineSegment(sketch, "E2460", {"start": v(-7, -3.27) * mm, "end": v(-7.03, -3.3) * mm});
            skLineSegment(sketch, "E2461", {"start": v(-7.03, -3.3) * mm, "end": v(-7.05, -3.32) * mm});
            skLineSegment(sketch, "E2462", {"start": v(-7.05, -3.32) * mm, "end": v(-7.06, -3.34) * mm});
            skLineSegment(sketch, "E2463", {"start": v(-7.06, -3.34) * mm, "end": v(-7.08, -3.37) * mm});
            skLineSegment(sketch, "E2464", {"start": v(-7.08, -3.37) * mm, "end": v(-7.1, -3.4) * mm});
            skLineSegment(sketch, "E2465", {"start": v(-7.1, -3.4) * mm, "end": v(-7.12, -3.42) * mm});
            skLineSegment(sketch, "E2466", {"start": v(-7.12, -3.42) * mm, "end": v(-7.14, -3.44) * mm});
            skLineSegment(sketch, "E2467", {"start": v(-7.14, -3.44) * mm, "end": v(-7.16, -3.47) * mm});
            skArc(sketch, "E2468", {"start": v(-7.16, -3.47) * mm, "mid": v(-7.1, -3.59) * mm, "end": v(-7.04, -3.7) * mm});
            skLineSegment(sketch, "E2469", {"start": v(-6.59, -2.52) * mm, "end": v(-6.6, -2.52) * mm});
            skLineSegment(sketch, "E2470", {"start": v(-6.6, -2.52) * mm, "end": v(-6.6, -2.51) * mm});
            skLineSegment(sketch, "E2471", {"start": v(-6.6, -2.51) * mm, "end": v(-6.6, -2.5) * mm});
            skLineSegment(sketch, "E2472", {"start": v(-6.6, -2.5) * mm, "end": v(-6.62, -2.5) * mm});
            skLineSegment(sketch, "E2473", {"start": v(-6.62, -2.5) * mm, "end": v(-6.63, -2.5) * mm});
            skLineSegment(sketch, "E2474", {"start": v(-6.63, -2.5) * mm, "end": v(-6.64, -2.5) * mm});
            skLineSegment(sketch, "E2475", {"start": v(-6.64, -2.5) * mm, "end": v(-6.66, -2.5) * mm});
            skLineSegment(sketch, "E2476", {"start": v(-6.66, -2.5) * mm, "end": v(-6.66, -2.5) * mm});
            skLineSegment(sketch, "E2477", {"start": v(-6.66, -2.5) * mm, "end": v(-6.68, -2.5) * mm});
            skLineSegment(sketch, "E2478", {"start": v(-6.68, -2.5) * mm, "end": v(-6.7, -2.51) * mm});
            skLineSegment(sketch, "E2479", {"start": v(-6.7, -2.51) * mm, "end": v(-6.7, -2.51) * mm});
            skLineSegment(sketch, "E2480", {"start": v(-6.7, -2.51) * mm, "end": v(-6.72, -2.51) * mm});
            skLineSegment(sketch, "E2481", {"start": v(-6.72, -2.51) * mm, "end": v(-6.74, -2.52) * mm});
            skLineSegment(sketch, "E2482", {"start": v(-6.74, -2.52) * mm, "end": v(-6.75, -2.52) * mm});
            skLineSegment(sketch, "E2483", {"start": v(-6.75, -2.52) * mm, "end": v(-6.77, -2.52) * mm});
            skLineSegment(sketch, "E2484", {"start": v(-6.77, -2.52) * mm, "end": v(-6.78, -2.52) * mm});
            skLineSegment(sketch, "E2485", {"start": v(-6.78, -2.52) * mm, "end": v(-6.8, -2.52) * mm});
            skLineSegment(sketch, "E2486", {"start": v(-6.8, -2.52) * mm, "end": v(-6.82, -2.52) * mm});
            skLineSegment(sketch, "E2487", {"start": v(-6.82, -2.52) * mm, "end": v(-6.84, -2.52) * mm});
            skLineSegment(sketch, "E2488", {"start": v(-6.84, -2.52) * mm, "end": v(-6.86, -2.52) * mm});
            skLineSegment(sketch, "E2489", {"start": v(-6.86, -2.52) * mm, "end": v(-6.88, -2.53) * mm});
            skLineSegment(sketch, "E2490", {"start": v(-6.88, -2.53) * mm, "end": v(-6.9, -2.53) * mm});
            skLineSegment(sketch, "E2491", {"start": v(-6.9, -2.53) * mm, "end": v(-6.92, -2.53) * mm});
            skLineSegment(sketch, "E2492", {"start": v(-6.92, -2.53) * mm, "end": v(-6.94, -2.53) * mm});
            skLineSegment(sketch, "E2493", {"start": v(-6.94, -2.53) * mm, "end": v(-6.96, -2.53) * mm});
            skLineSegment(sketch, "E2494", {"start": v(-6.96, -2.53) * mm, "end": v(-6.98, -2.53) * mm});
            skLineSegment(sketch, "E2495", {"start": v(-6.98, -2.53) * mm, "end": v(-7, -2.53) * mm});
            skLineSegment(sketch, "E2496", {"start": v(-7, -2.53) * mm, "end": v(-7.03, -2.53) * mm});
            skLineSegment(sketch, "E2497", {"start": v(-7.03, -2.53) * mm, "end": v(-7.05, -2.52) * mm});
            skLineSegment(sketch, "E2498", {"start": v(-7.05, -2.52) * mm, "end": v(-7.08, -2.52) * mm});
            skLineSegment(sketch, "E2499", {"start": v(-7.08, -2.52) * mm, "end": v(-7.1, -2.52) * mm});
            skLineSegment(sketch, "E2500", {"start": v(-7.1, -2.52) * mm, "end": v(-7.13, -2.52) * mm});
            skLineSegment(sketch, "E2501", {"start": v(-7.13, -2.52) * mm, "end": v(-7.15, -2.52) * mm});
            skLineSegment(sketch, "E2502", {"start": v(-7.15, -2.52) * mm, "end": v(-7.18, -2.52) * mm});
            skLineSegment(sketch, "E2503", {"start": v(-7.18, -2.52) * mm, "end": v(-7.2, -2.52) * mm});
            skLineSegment(sketch, "E2504", {"start": v(-7.2, -2.52) * mm, "end": v(-7.23, -2.51) * mm});
            skLineSegment(sketch, "E2505", {"start": v(-7.23, -2.51) * mm, "end": v(-7.26, -2.5) * mm});
            skLineSegment(sketch, "E2506", {"start": v(-7.26, -2.5) * mm, "end": v(-7.29, -2.5) * mm});
            skLineSegment(sketch, "E2507", {"start": v(-7.29, -2.5) * mm, "end": v(-7.32, -2.5) * mm});
            skLineSegment(sketch, "E2508", {"start": v(-7.32, -2.5) * mm, "end": v(-7.35, -2.5) * mm});
            skLineSegment(sketch, "E2509", {"start": v(-7.35, -2.5) * mm, "end": v(-7.38, -2.5) * mm});
            skLineSegment(sketch, "E2510", {"start": v(-7.38, -2.5) * mm, "end": v(-7.4, -2.5) * mm});
            skLineSegment(sketch, "E2511", {"start": v(-7.4, -2.5) * mm, "end": v(-7.44, -2.49) * mm});
            skLineSegment(sketch, "E2512", {"start": v(-7.44, -2.49) * mm, "end": v(-7.47, -2.48) * mm});
            skLineSegment(sketch, "E2513", {"start": v(-7.47, -2.48) * mm, "end": v(-7.5, -2.48) * mm});
            skLineSegment(sketch, "E2514", {"start": v(-7.5, -2.48) * mm, "end": v(-7.53, -2.47) * mm});
            skLineSegment(sketch, "E2515", {"start": v(-7.53, -2.47) * mm, "end": v(-7.56, -2.46) * mm});
            skLineSegment(sketch, "E2516", {"start": v(-6.87, -1.62) * mm, "end": v(-6.87, -1.62) * mm});
            skLineSegment(sketch, "E2517", {"start": v(-6.87, -1.62) * mm, "end": v(-6.87, -1.63) * mm});
            skLineSegment(sketch, "E2518", {"start": v(-6.87, -1.63) * mm, "end": v(-6.87, -1.64) * mm});
            skLineSegment(sketch, "E2519", {"start": v(-6.87, -1.64) * mm, "end": v(-6.88, -1.65) * mm});
            skLineSegment(sketch, "E2520", {"start": v(-6.88, -1.65) * mm, "end": v(-6.89, -1.65) * mm});
            skLineSegment(sketch, "E2521", {"start": v(-6.89, -1.65) * mm, "end": v(-6.9, -1.66) * mm});
            skLineSegment(sketch, "E2522", {"start": v(-6.9, -1.66) * mm, "end": v(-6.91, -1.67) * mm});
            skLineSegment(sketch, "E2523", {"start": v(-6.91, -1.67) * mm, "end": v(-6.92, -1.67) * mm});
            skLineSegment(sketch, "E2524", {"start": v(-6.92, -1.67) * mm, "end": v(-6.93, -1.68) * mm});
            skLineSegment(sketch, "E2525", {"start": v(-6.93, -1.68) * mm, "end": v(-6.94, -1.68) * mm});
            skLineSegment(sketch, "E2526", {"start": v(-6.94, -1.68) * mm, "end": v(-6.96, -1.69) * mm});
            skLineSegment(sketch, "E2527", {"start": v(-6.96, -1.69) * mm, "end": v(-6.97, -1.7) * mm});
            skLineSegment(sketch, "E2528", {"start": v(-6.97, -1.7) * mm, "end": v(-6.98, -1.7) * mm});
            skLineSegment(sketch, "E2529", {"start": v(-6.98, -1.7) * mm, "end": v(-7, -1.71) * mm});
            skLineSegment(sketch, "E2530", {"start": v(-7, -1.71) * mm, "end": v(-7.01, -1.72) * mm});
            skLineSegment(sketch, "E2531", {"start": v(-7.01, -1.72) * mm, "end": v(-7.03, -1.73) * mm});
            skLineSegment(sketch, "E2532", {"start": v(-7.03, -1.73) * mm, "end": v(-7.04, -1.74) * mm});
            skLineSegment(sketch, "E2533", {"start": v(-7.04, -1.74) * mm, "end": v(-7.06, -1.75) * mm});
            skLineSegment(sketch, "E2534", {"start": v(-7.06, -1.75) * mm, "end": v(-7.07, -1.76) * mm});
            skLineSegment(sketch, "E2535", {"start": v(-7.07, -1.76) * mm, "end": v(-7.09, -1.77) * mm});
            skLineSegment(sketch, "E2536", {"start": v(-7.09, -1.77) * mm, "end": v(-7.1, -1.78) * mm});
            skLineSegment(sketch, "E2537", {"start": v(-7.1, -1.78) * mm, "end": v(-7.12, -1.79) * mm});
            skLineSegment(sketch, "E2538", {"start": v(-7.12, -1.79) * mm, "end": v(-7.14, -1.8) * mm});
            skLineSegment(sketch, "E2539", {"start": v(-7.14, -1.8) * mm, "end": v(-7.16, -1.8) * mm});
            skLineSegment(sketch, "E2540", {"start": v(-7.16, -1.8) * mm, "end": v(-7.18, -1.82) * mm});
            skLineSegment(sketch, "E2541", {"start": v(-7.18, -1.82) * mm, "end": v(-7.2, -1.83) * mm});
            skLineSegment(sketch, "E2542", {"start": v(-7.2, -1.83) * mm, "end": v(-7.21, -1.85) * mm});
            skLineSegment(sketch, "E2543", {"start": v(-7.21, -1.85) * mm, "end": v(-7.23, -1.86) * mm});
            skLineSegment(sketch, "E2544", {"start": v(-7.23, -1.86) * mm, "end": v(-7.25, -1.87) * mm});
            skLineSegment(sketch, "E2545", {"start": v(-7.25, -1.87) * mm, "end": v(-7.27, -1.89) * mm});
            skLineSegment(sketch, "E2546", {"start": v(-7.27, -1.89) * mm, "end": v(-7.3, -1.9) * mm});
            skLineSegment(sketch, "E2547", {"start": v(-7.3, -1.9) * mm, "end": v(-7.31, -1.92) * mm});
            skLineSegment(sketch, "E2548", {"start": v(-7.31, -1.92) * mm, "end": v(-7.33, -1.93) * mm});
            skLineSegment(sketch, "E2549", {"start": v(-7.33, -1.93) * mm, "end": v(-7.35, -1.95) * mm});
            skLineSegment(sketch, "E2550", {"start": v(-7.35, -1.95) * mm, "end": v(-7.37, -1.97) * mm});
            skLineSegment(sketch, "E2551", {"start": v(-7.37, -1.97) * mm, "end": v(-7.4, -1.99) * mm});
            skLineSegment(sketch, "E2552", {"start": v(-7.4, -1.99) * mm, "end": v(-7.42, -2) * mm});
            skLineSegment(sketch, "E2553", {"start": v(-7.42, -2) * mm, "end": v(-7.44, -2.02) * mm});
            skLineSegment(sketch, "E2554", {"start": v(-7.44, -2.02) * mm, "end": v(-7.46, -2.04) * mm});
            skLineSegment(sketch, "E2555", {"start": v(-7.46, -2.04) * mm, "end": v(-7.48, -2.06) * mm});
            skLineSegment(sketch, "E2556", {"start": v(-7.48, -2.06) * mm, "end": v(-7.5, -2.08) * mm});
            skLineSegment(sketch, "E2557", {"start": v(-7.5, -2.08) * mm, "end": v(-7.53, -2.1) * mm});
            skLineSegment(sketch, "E2558", {"start": v(-7.53, -2.1) * mm, "end": v(-7.55, -2.12) * mm});
            skLineSegment(sketch, "E2559", {"start": v(-7.55, -2.12) * mm, "end": v(-7.57, -2.14) * mm});
            skLineSegment(sketch, "E2560", {"start": v(-7.57, -2.14) * mm, "end": v(-7.6, -2.17) * mm});
            skLineSegment(sketch, "E2561", {"start": v(-7.6, -2.17) * mm, "end": v(-7.62, -2.19) * mm});
            skLineSegment(sketch, "E2562", {"start": v(-7.62, -2.19) * mm, "end": v(-7.64, -2.21) * mm});
            skArc(sketch, "E2563", {"start": v(-7.64, -2.21) * mm, "mid": v(-7.6, -2.34) * mm, "end": v(-7.56, -2.46) * mm});
            skLineSegment(sketch, "E2564", {"start": v(-6.92, -1.37) * mm, "end": v(-6.92, -1.37) * mm});
            skLineSegment(sketch, "E2565", {"start": v(-6.92, -1.37) * mm, "end": v(-6.93, -1.36) * mm});
            skLineSegment(sketch, "E2566", {"start": v(-6.93, -1.36) * mm, "end": v(-6.93, -1.36) * mm});
            skLineSegment(sketch, "E2567", {"start": v(-6.93, -1.36) * mm, "end": v(-6.94, -1.35) * mm});
            skLineSegment(sketch, "E2568", {"start": v(-6.94, -1.35) * mm, "end": v(-6.95, -1.35) * mm});
            skLineSegment(sketch, "E2569", {"start": v(-6.95, -1.35) * mm, "end": v(-6.97, -1.35) * mm});
            skLineSegment(sketch, "E2570", {"start": v(-6.97, -1.35) * mm, "end": v(-6.98, -1.35) * mm});
            skLineSegment(sketch, "E2571", {"start": v(-6.98, -1.35) * mm, "end": v(-6.99, -1.35) * mm});
            skLineSegment(sketch, "E2572", {"start": v(-6.99, -1.35) * mm, "end": v(-7, -1.34) * mm});
            skLineSegment(sketch, "E2573", {"start": v(-7, -1.34) * mm, "end": v(-7.02, -1.34) * mm});
            skLineSegment(sketch, "E2574", {"start": v(-7.02, -1.34) * mm, "end": v(-7.03, -1.34) * mm});
            skLineSegment(sketch, "E2575", {"start": v(-7.03, -1.34) * mm, "end": v(-7.05, -1.34) * mm});
            skLineSegment(sketch, "E2576", {"start": v(-7.05, -1.34) * mm, "end": v(-7.06, -1.34) * mm});
            skLineSegment(sketch, "E2577", {"start": v(-7.06, -1.34) * mm, "end": v(-7.08, -1.34) * mm});
            skLineSegment(sketch, "E2578", {"start": v(-7.08, -1.34) * mm, "end": v(-7.1, -1.34) * mm});
            skLineSegment(sketch, "E2579", {"start": v(-7.1, -1.34) * mm, "end": v(-7.11, -1.34) * mm});
            skLineSegment(sketch, "E2580", {"start": v(-7.11, -1.34) * mm, "end": v(-7.13, -1.34) * mm});
            skLineSegment(sketch, "E2581", {"start": v(-7.13, -1.34) * mm, "end": v(-7.15, -1.33) * mm});
            skLineSegment(sketch, "E2582", {"start": v(-7.15, -1.33) * mm, "end": v(-7.16, -1.33) * mm});
            skLineSegment(sketch, "E2583", {"start": v(-7.16, -1.33) * mm, "end": v(-7.18, -1.33) * mm});
            skLineSegment(sketch, "E2584", {"start": v(-7.18, -1.33) * mm, "end": v(-7.2, -1.33) * mm});
            skLineSegment(sketch, "E2585", {"start": v(-7.2, -1.33) * mm, "end": v(-7.22, -1.32) * mm});
            skLineSegment(sketch, "E2586", {"start": v(-7.22, -1.32) * mm, "end": v(-7.24, -1.32) * mm});
            skLineSegment(sketch, "E2587", {"start": v(-7.24, -1.32) * mm, "end": v(-7.26, -1.32) * mm});
            skLineSegment(sketch, "E2588", {"start": v(-7.26, -1.32) * mm, "end": v(-7.29, -1.31) * mm});
            skLineSegment(sketch, "E2589", {"start": v(-7.29, -1.31) * mm, "end": v(-7.3, -1.31) * mm});
            skLineSegment(sketch, "E2590", {"start": v(-7.3, -1.31) * mm, "end": v(-7.33, -1.3) * mm});
            skLineSegment(sketch, "E2591", {"start": v(-7.33, -1.3) * mm, "end": v(-7.35, -1.3) * mm});
            skLineSegment(sketch, "E2592", {"start": v(-7.35, -1.3) * mm, "end": v(-7.38, -1.3) * mm});
            skLineSegment(sketch, "E2593", {"start": v(-7.38, -1.3) * mm, "end": v(-7.4, -1.3) * mm});
            skLineSegment(sketch, "E2594", {"start": v(-7.4, -1.3) * mm, "end": v(-7.42, -1.29) * mm});
            skLineSegment(sketch, "E2595", {"start": v(-7.42, -1.29) * mm, "end": v(-7.45, -1.28) * mm});
            skLineSegment(sketch, "E2596", {"start": v(-7.45, -1.28) * mm, "end": v(-7.47, -1.27) * mm});
            skLineSegment(sketch, "E2597", {"start": v(-7.47, -1.27) * mm, "end": v(-7.5, -1.27) * mm});
            skLineSegment(sketch, "E2598", {"start": v(-7.5, -1.27) * mm, "end": v(-7.52, -1.26) * mm});
            skLineSegment(sketch, "E2599", {"start": v(-7.52, -1.26) * mm, "end": v(-7.55, -1.25) * mm});
            skLineSegment(sketch, "E2600", {"start": v(-7.55, -1.25) * mm, "end": v(-7.58, -1.25) * mm});
            skLineSegment(sketch, "E2601", {"start": v(-7.58, -1.25) * mm, "end": v(-7.6, -1.24) * mm});
            skLineSegment(sketch, "E2602", {"start": v(-7.6, -1.24) * mm, "end": v(-7.63, -1.23) * mm});
            skLineSegment(sketch, "E2603", {"start": v(-7.63, -1.23) * mm, "end": v(-7.66, -1.22) * mm});
            skLineSegment(sketch, "E2604", {"start": v(-7.66, -1.22) * mm, "end": v(-7.69, -1.21) * mm});
            skLineSegment(sketch, "E2605", {"start": v(-7.69, -1.21) * mm, "end": v(-7.72, -1.2) * mm});
            skLineSegment(sketch, "E2606", {"start": v(-7.72, -1.2) * mm, "end": v(-7.75, -1.2) * mm});
            skLineSegment(sketch, "E2607", {"start": v(-7.75, -1.2) * mm, "end": v(-7.78, -1.18) * mm});
            skLineSegment(sketch, "E2608", {"start": v(-7.78, -1.18) * mm, "end": v(-7.8, -1.17) * mm});
            skLineSegment(sketch, "E2609", {"start": v(-7.8, -1.17) * mm, "end": v(-7.84, -1.16) * mm});
            skLineSegment(sketch, "E2610", {"start": v(-7.84, -1.16) * mm, "end": v(-7.87, -1.15) * mm});
            skLineSegment(sketch, "E2611", {"start": v(-7.04, -0.43) * mm, "end": v(-7.04, -0.44) * mm});
            skLineSegment(sketch, "E2612", {"start": v(-7.04, -0.44) * mm, "end": v(-7.04, -0.45) * mm});
            skLineSegment(sketch, "E2613", {"start": v(-7.04, -0.45) * mm, "end": v(-7.05, -0.45) * mm});
            skLineSegment(sketch, "E2614", {"start": v(-7.05, -0.45) * mm, "end": v(-7.06, -0.46) * mm});
            skLineSegment(sketch, "E2615", {"start": v(-7.06, -0.46) * mm, "end": v(-7.07, -0.46) * mm});
            skLineSegment(sketch, "E2616", {"start": v(-7.07, -0.46) * mm, "end": v(-7.08, -0.47) * mm});
            skLineSegment(sketch, "E2617", {"start": v(-7.08, -0.47) * mm, "end": v(-7.1, -0.48) * mm});
            skLineSegment(sketch, "E2618", {"start": v(-7.1, -0.48) * mm, "end": v(-7.1, -0.48) * mm});
            skLineSegment(sketch, "E2619", {"start": v(-7.1, -0.48) * mm, "end": v(-7.11, -0.48) * mm});
            skLineSegment(sketch, "E2620", {"start": v(-7.11, -0.48) * mm, "end": v(-7.13, -0.49) * mm});
            skLineSegment(sketch, "E2621", {"start": v(-7.13, -0.49) * mm, "end": v(-7.14, -0.49) * mm});
            skLineSegment(sketch, "E2622", {"start": v(-7.14, -0.49) * mm, "end": v(-7.16, -0.5) * mm});
            skLineSegment(sketch, "E2623", {"start": v(-7.16, -0.5) * mm, "end": v(-7.17, -0.5) * mm});
            skLineSegment(sketch, "E2624", {"start": v(-7.17, -0.5) * mm, "end": v(-7.18, -0.5) * mm});
            skLineSegment(sketch, "E2625", {"start": v(-7.18, -0.5) * mm, "end": v(-7.2, -0.5) * mm});
            skLineSegment(sketch, "E2626", {"start": v(-7.2, -0.5) * mm, "end": v(-7.22, -0.52) * mm});
            skLineSegment(sketch, "E2627", {"start": v(-7.22, -0.52) * mm, "end": v(-7.23, -0.52) * mm});
            skLineSegment(sketch, "E2628", {"start": v(-7.23, -0.52) * mm, "end": v(-7.25, -0.53) * mm});
            skLineSegment(sketch, "E2629", {"start": v(-7.25, -0.53) * mm, "end": v(-7.27, -0.53) * mm});
            skLineSegment(sketch, "E2630", {"start": v(-7.27, -0.53) * mm, "end": v(-7.28, -0.54) * mm});
            skLineSegment(sketch, "E2631", {"start": v(-7.28, -0.54) * mm, "end": v(-7.3, -0.55) * mm});
            skLineSegment(sketch, "E2632", {"start": v(-7.3, -0.55) * mm, "end": v(-7.32, -0.56) * mm});
            skLineSegment(sketch, "E2633", {"start": v(-7.32, -0.56) * mm, "end": v(-7.34, -0.56) * mm});
            skLineSegment(sketch, "E2634", {"start": v(-7.34, -0.56) * mm, "end": v(-7.36, -0.57) * mm});
            skLineSegment(sketch, "E2635", {"start": v(-7.36, -0.57) * mm, "end": v(-7.38, -0.58) * mm});
            skLineSegment(sketch, "E2636", {"start": v(-7.38, -0.58) * mm, "end": v(-7.4, -0.6) * mm});
            skLineSegment(sketch, "E2637", {"start": v(-7.4, -0.6) * mm, "end": v(-7.42, -0.6) * mm});
            skLineSegment(sketch, "E2638", {"start": v(-7.42, -0.6) * mm, "end": v(-7.44, -0.61) * mm});
            skLineSegment(sketch, "E2639", {"start": v(-7.44, -0.61) * mm, "end": v(-7.46, -0.62) * mm});
            skLineSegment(sketch, "E2640", {"start": v(-7.46, -0.62) * mm, "end": v(-7.48, -0.63) * mm});
            skLineSegment(sketch, "E2641", {"start": v(-7.48, -0.63) * mm, "end": v(-7.5, -0.64) * mm});
            skLineSegment(sketch, "E2642", {"start": v(-7.5, -0.64) * mm, "end": v(-7.53, -0.66) * mm});
            skLineSegment(sketch, "E2643", {"start": v(-7.53, -0.66) * mm, "end": v(-7.55, -0.67) * mm});
            skLineSegment(sketch, "E2644", {"start": v(-7.55, -0.67) * mm, "end": v(-7.57, -0.68) * mm});
            skLineSegment(sketch, "E2645", {"start": v(-7.57, -0.68) * mm, "end": v(-7.6, -0.7) * mm});
            skLineSegment(sketch, "E2646", {"start": v(-7.6, -0.7) * mm, "end": v(-7.62, -0.7) * mm});
            skLineSegment(sketch, "E2647", {"start": v(-7.62, -0.7) * mm, "end": v(-7.65, -0.72) * mm});
            skLineSegment(sketch, "E2648", {"start": v(-7.65, -0.72) * mm, "end": v(-7.67, -0.74) * mm});
            skLineSegment(sketch, "E2649", {"start": v(-7.67, -0.74) * mm, "end": v(-7.7, -0.75) * mm});
            skLineSegment(sketch, "E2650", {"start": v(-7.7, -0.75) * mm, "end": v(-7.72, -0.77) * mm});
            skLineSegment(sketch, "E2651", {"start": v(-7.72, -0.77) * mm, "end": v(-7.74, -0.78) * mm});
            skLineSegment(sketch, "E2652", {"start": v(-7.74, -0.78) * mm, "end": v(-7.77, -0.8) * mm});
            skLineSegment(sketch, "E2653", {"start": v(-7.77, -0.8) * mm, "end": v(-7.8, -0.82) * mm});
            skLineSegment(sketch, "E2654", {"start": v(-7.8, -0.82) * mm, "end": v(-7.82, -0.83) * mm});
            skLineSegment(sketch, "E2655", {"start": v(-7.82, -0.83) * mm, "end": v(-7.85, -0.85) * mm});
            skLineSegment(sketch, "E2656", {"start": v(-7.85, -0.85) * mm, "end": v(-7.88, -0.87) * mm});
            skLineSegment(sketch, "E2657", {"start": v(-7.88, -0.87) * mm, "end": v(-7.9, -0.89) * mm});
            skArc(sketch, "E2658", {"start": v(-7.9, -0.89) * mm, "mid": v(-7.89, -1.02) * mm, "end": v(-7.87, -1.15) * mm});
            skLineSegment(sketch, "E2659", {"start": v(-7.05, -0.18) * mm, "end": v(-7.05, -0.18) * mm});
            skLineSegment(sketch, "E2660", {"start": v(-7.05, -0.18) * mm, "end": v(-7.05, -0.17) * mm});
            skLineSegment(sketch, "E2661", {"start": v(-7.05, -0.17) * mm, "end": v(-7.06, -0.16) * mm});
            skLineSegment(sketch, "E2662", {"start": v(-7.06, -0.16) * mm, "end": v(-7.07, -0.16) * mm});
            skLineSegment(sketch, "E2663", {"start": v(-7.07, -0.16) * mm, "end": v(-7.08, -0.15) * mm});
            skLineSegment(sketch, "E2664", {"start": v(-7.08, -0.15) * mm, "end": v(-7.1, -0.15) * mm});
            skLineSegment(sketch, "E2665", {"start": v(-7.1, -0.15) * mm, "end": v(-7.1, -0.15) * mm});
            skLineSegment(sketch, "E2666", {"start": v(-7.1, -0.15) * mm, "end": v(-7.12, -0.14) * mm});
            skLineSegment(sketch, "E2667", {"start": v(-7.12, -0.14) * mm, "end": v(-7.13, -0.14) * mm});
            skLineSegment(sketch, "E2668", {"start": v(-7.13, -0.14) * mm, "end": v(-7.14, -0.14) * mm});
            skLineSegment(sketch, "E2669", {"start": v(-7.14, -0.14) * mm, "end": v(-7.16, -0.14) * mm});
            skLineSegment(sketch, "E2670", {"start": v(-7.16, -0.14) * mm, "end": v(-7.17, -0.13) * mm});
            skLineSegment(sketch, "E2671", {"start": v(-7.17, -0.13) * mm, "end": v(-7.19, -0.13) * mm});
            skLineSegment(sketch, "E2672", {"start": v(-7.19, -0.13) * mm, "end": v(-7.2, -0.13) * mm});
            skLineSegment(sketch, "E2673", {"start": v(-7.2, -0.13) * mm, "end": v(-7.22, -0.12) * mm});
            skLineSegment(sketch, "E2674", {"start": v(-7.22, -0.12) * mm, "end": v(-7.23, -0.12) * mm});
            skLineSegment(sketch, "E2675", {"start": v(-7.23, -0.12) * mm, "end": v(-7.25, -0.11) * mm});
            skLineSegment(sketch, "E2676", {"start": v(-7.25, -0.11) * mm, "end": v(-7.27, -0.1) * mm});
            skLineSegment(sketch, "E2677", {"start": v(-7.27, -0.1) * mm, "end": v(-7.29, -0.1) * mm});
            skLineSegment(sketch, "E2678", {"start": v(-7.29, -0.1) * mm, "end": v(-7.3, -0.1) * mm});
            skLineSegment(sketch, "E2679", {"start": v(-7.3, -0.1) * mm, "end": v(-7.32, -0.1) * mm});
            skLineSegment(sketch, "E2680", {"start": v(-7.32, -0.1) * mm, "end": v(-7.34, -0.08) * mm});
            skLineSegment(sketch, "E2681", {"start": v(-7.34, -0.08) * mm, "end": v(-7.36, -0.08) * mm});
            skLineSegment(sketch, "E2682", {"start": v(-7.36, -0.08) * mm, "end": v(-7.38, -0.07) * mm});
            skLineSegment(sketch, "E2683", {"start": v(-7.38, -0.07) * mm, "end": v(-7.4, -0.06) * mm});
            skLineSegment(sketch, "E2684", {"start": v(-7.4, -0.06) * mm, "end": v(-7.42, -0.06) * mm});
            skLineSegment(sketch, "E2685", {"start": v(-7.42, -0.06) * mm, "end": v(-7.44, -0.05) * mm});
            skLineSegment(sketch, "E2686", {"start": v(-7.44, -0.05) * mm, "end": v(-7.47, -0.04) * mm});
            skLineSegment(sketch, "E2687", {"start": v(-7.47, -0.04) * mm, "end": v(-7.49, -0.03) * mm});
            skLineSegment(sketch, "E2688", {"start": v(-7.49, -0.03) * mm, "end": v(-7.5, -0.02) * mm});
            skLineSegment(sketch, "E2689", {"start": v(-7.5, -0.02) * mm, "end": v(-7.53, -0.01) * mm});
            skLineSegment(sketch, "E2690", {"start": v(-7.53, -0.01) * mm, "end": v(-7.56, 0) * mm});
            skLineSegment(sketch, "E2691", {"start": v(-7.56, 0) * mm, "end": v(-7.58, 0) * mm});
            skLineSegment(sketch, "E2692", {"start": v(-7.58, 0) * mm, "end": v(-7.6, 0.02) * mm});
            skLineSegment(sketch, "E2693", {"start": v(-7.6, 0.02) * mm, "end": v(-7.63, 0.03) * mm});
            skLineSegment(sketch, "E2694", {"start": v(-7.63, 0.03) * mm, "end": v(-7.65, 0.04) * mm});
            skLineSegment(sketch, "E2695", {"start": v(-7.65, 0.04) * mm, "end": v(-7.68, 0.05) * mm});
            skLineSegment(sketch, "E2696", {"start": v(-7.68, 0.05) * mm, "end": v(-7.7, 0.06) * mm});
            skLineSegment(sketch, "E2697", {"start": v(-7.7, 0.06) * mm, "end": v(-7.73, 0.08) * mm});
            skLineSegment(sketch, "E2698", {"start": v(-7.73, 0.08) * mm, "end": v(-7.76, 0.1) * mm});
            skLineSegment(sketch, "E2699", {"start": v(-7.76, 0.1) * mm, "end": v(-7.78, 0.1) * mm});
            skLineSegment(sketch, "E2700", {"start": v(-7.78, 0.1) * mm, "end": v(-7.8, 0.12) * mm});
            skLineSegment(sketch, "E2701", {"start": v(-7.8, 0.12) * mm, "end": v(-7.84, 0.13) * mm});
            skLineSegment(sketch, "E2702", {"start": v(-7.84, 0.13) * mm, "end": v(-7.86, 0.15) * mm});
            skLineSegment(sketch, "E2703", {"start": v(-7.86, 0.15) * mm, "end": v(-7.9, 0.16) * mm});
            skLineSegment(sketch, "E2704", {"start": v(-7.9, 0.16) * mm, "end": v(-7.92, 0.18) * mm});
            skLineSegment(sketch, "E2705", {"start": v(-7.92, 0.18) * mm, "end": v(-7.95, 0.2) * mm});
            skLineSegment(sketch, "E2706", {"start": v(-7, 0.76) * mm, "end": v(-7.01, 0.76) * mm});
            skLineSegment(sketch, "E2707", {"start": v(-7.01, 0.76) * mm, "end": v(-7.02, 0.75) * mm});
            skLineSegment(sketch, "E2708", {"start": v(-7.02, 0.75) * mm, "end": v(-7.02, 0.74) * mm});
            skLineSegment(sketch, "E2709", {"start": v(-7.02, 0.74) * mm, "end": v(-7.03, 0.74) * mm});
            skLineSegment(sketch, "E2710", {"start": v(-7.03, 0.74) * mm, "end": v(-7.04, 0.74) * mm});
            skLineSegment(sketch, "E2711", {"start": v(-7.04, 0.74) * mm, "end": v(-7.06, 0.73) * mm});
            skLineSegment(sketch, "E2712", {"start": v(-7.06, 0.73) * mm, "end": v(-7.07, 0.73) * mm});
            skLineSegment(sketch, "E2713", {"start": v(-7.07, 0.73) * mm, "end": v(-7.08, 0.73) * mm});
            skLineSegment(sketch, "E2714", {"start": v(-7.08, 0.73) * mm, "end": v(-7.1, 0.73) * mm});
            skLineSegment(sketch, "E2715", {"start": v(-7.1, 0.73) * mm, "end": v(-7.1, 0.73) * mm});
            skLineSegment(sketch, "E2716", {"start": v(-7.1, 0.73) * mm, "end": v(-7.12, 0.72) * mm});
            skLineSegment(sketch, "E2717", {"start": v(-7.12, 0.72) * mm, "end": v(-7.13, 0.72) * mm});
            skLineSegment(sketch, "E2718", {"start": v(-7.13, 0.72) * mm, "end": v(-7.15, 0.72) * mm});
            skLineSegment(sketch, "E2719", {"start": v(-7.15, 0.72) * mm, "end": v(-7.17, 0.72) * mm});
            skLineSegment(sketch, "E2720", {"start": v(-7.17, 0.72) * mm, "end": v(-7.18, 0.71) * mm});
            skLineSegment(sketch, "E2721", {"start": v(-7.18, 0.71) * mm, "end": v(-7.2, 0.71) * mm});
            skLineSegment(sketch, "E2722", {"start": v(-7.2, 0.71) * mm, "end": v(-7.22, 0.7) * mm});
            skLineSegment(sketch, "E2723", {"start": v(-7.22, 0.7) * mm, "end": v(-7.23, 0.7) * mm});
            skLineSegment(sketch, "E2724", {"start": v(-7.23, 0.7) * mm, "end": v(-7.25, 0.7) * mm});
            skLineSegment(sketch, "E2725", {"start": v(-7.25, 0.7) * mm, "end": v(-7.27, 0.7) * mm});
            skLineSegment(sketch, "E2726", {"start": v(-7.27, 0.7) * mm, "end": v(-7.29, 0.7) * mm});
            skLineSegment(sketch, "E2727", {"start": v(-7.29, 0.7) * mm, "end": v(-7.3, 0.69) * mm});
            skLineSegment(sketch, "E2728", {"start": v(-7.3, 0.69) * mm, "end": v(-7.33, 0.68) * mm});
            skLineSegment(sketch, "E2729", {"start": v(-7.33, 0.68) * mm, "end": v(-7.35, 0.68) * mm});
            skLineSegment(sketch, "E2730", {"start": v(-7.35, 0.68) * mm, "end": v(-7.37, 0.67) * mm});
            skLineSegment(sketch, "E2731", {"start": v(-7.37, 0.67) * mm, "end": v(-7.4, 0.67) * mm});
            skLineSegment(sketch, "E2732", {"start": v(-7.4, 0.67) * mm, "end": v(-7.41, 0.66) * mm});
            skLineSegment(sketch, "E2733", {"start": v(-7.41, 0.66) * mm, "end": v(-7.44, 0.65) * mm});
            skLineSegment(sketch, "E2734", {"start": v(-7.44, 0.65) * mm, "end": v(-7.46, 0.65) * mm});
            skLineSegment(sketch, "E2735", {"start": v(-7.46, 0.65) * mm, "end": v(-7.48, 0.64) * mm});
            skLineSegment(sketch, "E2736", {"start": v(-7.48, 0.64) * mm, "end": v(-7.5, 0.63) * mm});
            skLineSegment(sketch, "E2737", {"start": v(-7.5, 0.63) * mm, "end": v(-7.53, 0.63) * mm});
            skLineSegment(sketch, "E2738", {"start": v(-7.53, 0.63) * mm, "end": v(-7.55, 0.62) * mm});
            skLineSegment(sketch, "E2739", {"start": v(-7.55, 0.62) * mm, "end": v(-7.58, 0.6) * mm});
            skLineSegment(sketch, "E2740", {"start": v(-7.58, 0.6) * mm, "end": v(-7.6, 0.6) * mm});
            skLineSegment(sketch, "E2741", {"start": v(-7.6, 0.6) * mm, "end": v(-7.63, 0.6) * mm});
            skLineSegment(sketch, "E2742", {"start": v(-7.63, 0.6) * mm, "end": v(-7.66, 0.58) * mm});
            skLineSegment(sketch, "E2743", {"start": v(-7.66, 0.58) * mm, "end": v(-7.68, 0.57) * mm});
            skLineSegment(sketch, "E2744", {"start": v(-7.68, 0.57) * mm, "end": v(-7.7, 0.56) * mm});
            skLineSegment(sketch, "E2745", {"start": v(-7.7, 0.56) * mm, "end": v(-7.74, 0.55) * mm});
            skLineSegment(sketch, "E2746", {"start": v(-7.74, 0.55) * mm, "end": v(-7.76, 0.54) * mm});
            skLineSegment(sketch, "E2747", {"start": v(-7.76, 0.54) * mm, "end": v(-7.8, 0.53) * mm});
            skLineSegment(sketch, "E2748", {"start": v(-7.8, 0.53) * mm, "end": v(-7.82, 0.51) * mm});
            skLineSegment(sketch, "E2749", {"start": v(-7.82, 0.51) * mm, "end": v(-7.85, 0.5) * mm});
            skLineSegment(sketch, "E2750", {"start": v(-7.85, 0.5) * mm, "end": v(-7.88, 0.49) * mm});
            skLineSegment(sketch, "E2751", {"start": v(-7.88, 0.49) * mm, "end": v(-7.9, 0.47) * mm});
            skLineSegment(sketch, "E2752", {"start": v(-7.9, 0.47) * mm, "end": v(-7.94, 0.46) * mm});
            skArc(sketch, "E2753", {"start": v(-7.94, 0.46) * mm, "mid": v(-7.94, 0.33) * mm, "end": v(-7.95, 0.2) * mm});
            skLineSegment(sketch, "E2754", {"start": v(-6.98, 1.01) * mm, "end": v(-6.98, 1.02) * mm});
            skLineSegment(sketch, "E2755", {"start": v(-6.98, 1.02) * mm, "end": v(-6.98, 1.02) * mm});
            skLineSegment(sketch, "E2756", {"start": v(-6.98, 1.02) * mm, "end": v(-6.99, 1.03) * mm});
            skLineSegment(sketch, "E2757", {"start": v(-6.99, 1.03) * mm, "end": v(-7, 1.04) * mm});
            skLineSegment(sketch, "E2758", {"start": v(-7, 1.04) * mm, "end": v(-7, 1.04) * mm});
            skLineSegment(sketch, "E2759", {"start": v(-7, 1.04) * mm, "end": v(-7.02, 1.05) * mm});
            skLineSegment(sketch, "E2760", {"start": v(-7.02, 1.05) * mm, "end": v(-7.03, 1.06) * mm});
            skLineSegment(sketch, "E2761", {"start": v(-7.03, 1.06) * mm, "end": v(-7.04, 1.06) * mm});
            skLineSegment(sketch, "E2762", {"start": v(-7.04, 1.06) * mm, "end": v(-7.05, 1.06) * mm});
            skLineSegment(sketch, "E2763", {"start": v(-7.05, 1.06) * mm, "end": v(-7.06, 1.07) * mm});
            skLineSegment(sketch, "E2764", {"start": v(-7.06, 1.07) * mm, "end": v(-7.07, 1.08) * mm});
            skLineSegment(sketch, "E2765", {"start": v(-7.07, 1.08) * mm, "end": v(-7.09, 1.08) * mm});
            skLineSegment(sketch, "E2766", {"start": v(-7.09, 1.08) * mm, "end": v(-7.1, 1.09) * mm});
            skLineSegment(sketch, "E2767", {"start": v(-7.1, 1.09) * mm, "end": v(-7.12, 1.1) * mm});
            skLineSegment(sketch, "E2768", {"start": v(-7.12, 1.1) * mm, "end": v(-7.13, 1.1) * mm});
            skLineSegment(sketch, "E2769", {"start": v(-7.13, 1.1) * mm, "end": v(-7.15, 1.1) * mm});
            skLineSegment(sketch, "E2770", {"start": v(-7.15, 1.1) * mm, "end": v(-7.16, 1.11) * mm});
            skLineSegment(sketch, "E2771", {"start": v(-7.16, 1.11) * mm, "end": v(-7.18, 1.12) * mm});
            skLineSegment(sketch, "E2772", {"start": v(-7.18, 1.12) * mm, "end": v(-7.2, 1.13) * mm});
            skLineSegment(sketch, "E2773", {"start": v(-7.2, 1.13) * mm, "end": v(-7.21, 1.14) * mm});
            skLineSegment(sketch, "E2774", {"start": v(-7.21, 1.14) * mm, "end": v(-7.23, 1.15) * mm});
            skLineSegment(sketch, "E2775", {"start": v(-7.23, 1.15) * mm, "end": v(-7.25, 1.16) * mm});
            skLineSegment(sketch, "E2776", {"start": v(-7.25, 1.16) * mm, "end": v(-7.27, 1.17) * mm});
            skLineSegment(sketch, "E2777", {"start": v(-7.27, 1.17) * mm, "end": v(-7.29, 1.18) * mm});
            skLineSegment(sketch, "E2778", {"start": v(-7.29, 1.18) * mm, "end": v(-7.3, 1.19) * mm});
            skLineSegment(sketch, "E2779", {"start": v(-7.3, 1.19) * mm, "end": v(-7.32, 1.2) * mm});
            skLineSegment(sketch, "E2780", {"start": v(-7.32, 1.2) * mm, "end": v(-7.34, 1.2) * mm});
            skLineSegment(sketch, "E2781", {"start": v(-7.34, 1.2) * mm, "end": v(-7.36, 1.22) * mm});
            skLineSegment(sketch, "E2782", {"start": v(-7.36, 1.22) * mm, "end": v(-7.38, 1.23) * mm});
            skLineSegment(sketch, "E2783", {"start": v(-7.38, 1.23) * mm, "end": v(-7.4, 1.25) * mm});
            skLineSegment(sketch, "E2784", {"start": v(-7.4, 1.25) * mm, "end": v(-7.42, 1.26) * mm});
            skLineSegment(sketch, "E2785", {"start": v(-7.42, 1.26) * mm, "end": v(-7.45, 1.27) * mm});
            skLineSegment(sketch, "E2786", {"start": v(-7.45, 1.27) * mm, "end": v(-7.47, 1.29) * mm});
            skLineSegment(sketch, "E2787", {"start": v(-7.47, 1.29) * mm, "end": v(-7.49, 1.3) * mm});
            skLineSegment(sketch, "E2788", {"start": v(-7.49, 1.3) * mm, "end": v(-7.51, 1.32) * mm});
            skLineSegment(sketch, "E2789", {"start": v(-7.51, 1.32) * mm, "end": v(-7.53, 1.33) * mm});
            skLineSegment(sketch, "E2790", {"start": v(-7.53, 1.33) * mm, "end": v(-7.56, 1.35) * mm});
            skLineSegment(sketch, "E2791", {"start": v(-7.56, 1.35) * mm, "end": v(-7.58, 1.37) * mm});
            skLineSegment(sketch, "E2792", {"start": v(-7.58, 1.37) * mm, "end": v(-7.6, 1.38) * mm});
            skLineSegment(sketch, "E2793", {"start": v(-7.6, 1.38) * mm, "end": v(-7.63, 1.4) * mm});
            skLineSegment(sketch, "E2794", {"start": v(-7.63, 1.4) * mm, "end": v(-7.65, 1.42) * mm});
            skLineSegment(sketch, "E2795", {"start": v(-7.65, 1.42) * mm, "end": v(-7.68, 1.44) * mm});
            skLineSegment(sketch, "E2796", {"start": v(-7.68, 1.44) * mm, "end": v(-7.7, 1.46) * mm});
            skLineSegment(sketch, "E2797", {"start": v(-7.7, 1.46) * mm, "end": v(-7.72, 1.47) * mm});
            skLineSegment(sketch, "E2798", {"start": v(-7.72, 1.47) * mm, "end": v(-7.75, 1.5) * mm});
            skLineSegment(sketch, "E2799", {"start": v(-7.75, 1.5) * mm, "end": v(-7.77, 1.52) * mm});
            skLineSegment(sketch, "E2800", {"start": v(-7.77, 1.52) * mm, "end": v(-7.8, 1.54) * mm});
            skLineSegment(sketch, "E2801", {"start": v(-6.78, 1.93) * mm, "end": v(-6.78, 1.93) * mm});
            skLineSegment(sketch, "E2802", {"start": v(-6.78, 1.93) * mm, "end": v(-6.79, 1.92) * mm});
            skLineSegment(sketch, "E2803", {"start": v(-6.79, 1.92) * mm, "end": v(-6.8, 1.92) * mm});
            skLineSegment(sketch, "E2804", {"start": v(-6.8, 1.92) * mm, "end": v(-6.8, 1.92) * mm});
            skLineSegment(sketch, "E2805", {"start": v(-6.8, 1.92) * mm, "end": v(-6.82, 1.92) * mm});
            skLineSegment(sketch, "E2806", {"start": v(-6.82, 1.92) * mm, "end": v(-6.83, 1.91) * mm});
            skLineSegment(sketch, "E2807", {"start": v(-6.83, 1.91) * mm, "end": v(-6.84, 1.91) * mm});
            skLineSegment(sketch, "E2808", {"start": v(-6.84, 1.91) * mm, "end": v(-6.85, 1.91) * mm});
            skLineSegment(sketch, "E2809", {"start": v(-6.85, 1.91) * mm, "end": v(-6.86, 1.92) * mm});
            skLineSegment(sketch, "E2810", {"start": v(-6.86, 1.92) * mm, "end": v(-6.88, 1.92) * mm});
            skLineSegment(sketch, "E2811", {"start": v(-6.88, 1.92) * mm, "end": v(-6.9, 1.92) * mm});
            skLineSegment(sketch, "E2812", {"start": v(-6.9, 1.92) * mm, "end": v(-6.9, 1.92) * mm});
            skLineSegment(sketch, "E2813", {"start": v(-6.9, 1.92) * mm, "end": v(-6.92, 1.92) * mm});
            skLineSegment(sketch, "E2814", {"start": v(-6.92, 1.92) * mm, "end": v(-6.94, 1.92) * mm});
            skLineSegment(sketch, "E2815", {"start": v(-6.94, 1.92) * mm, "end": v(-6.96, 1.92) * mm});
            skLineSegment(sketch, "E2816", {"start": v(-6.96, 1.92) * mm, "end": v(-6.97, 1.92) * mm});
            skLineSegment(sketch, "E2817", {"start": v(-6.97, 1.92) * mm, "end": v(-7, 1.92) * mm});
            skLineSegment(sketch, "E2818", {"start": v(-7, 1.92) * mm, "end": v(-7, 1.92) * mm});
            skLineSegment(sketch, "E2819", {"start": v(-7, 1.92) * mm, "end": v(-7.03, 1.92) * mm});
            skLineSegment(sketch, "E2820", {"start": v(-7.03, 1.92) * mm, "end": v(-7.05, 1.92) * mm});
            skLineSegment(sketch, "E2821", {"start": v(-7.05, 1.92) * mm, "end": v(-7.07, 1.91) * mm});
            skLineSegment(sketch, "E2822", {"start": v(-7.07, 1.91) * mm, "end": v(-7.09, 1.91) * mm});
            skLineSegment(sketch, "E2823", {"start": v(-7.09, 1.91) * mm, "end": v(-7.1, 1.91) * mm});
            skLineSegment(sketch, "E2824", {"start": v(-7.1, 1.91) * mm, "end": v(-7.13, 1.91) * mm});
            skLineSegment(sketch, "E2825", {"start": v(-7.13, 1.91) * mm, "end": v(-7.15, 1.9) * mm});
            skLineSegment(sketch, "E2826", {"start": v(-7.15, 1.9) * mm, "end": v(-7.17, 1.9) * mm});
            skLineSegment(sketch, "E2827", {"start": v(-7.17, 1.9) * mm, "end": v(-7.2, 1.9) * mm});
            skLineSegment(sketch, "E2828", {"start": v(-7.2, 1.9) * mm, "end": v(-7.22, 1.9) * mm});
            skLineSegment(sketch, "E2829", {"start": v(-7.22, 1.9) * mm, "end": v(-7.24, 1.9) * mm});
            skLineSegment(sketch, "E2830", {"start": v(-7.24, 1.9) * mm, "end": v(-7.26, 1.9) * mm});
            skLineSegment(sketch, "E2831", {"start": v(-7.26, 1.9) * mm, "end": v(-7.29, 1.9) * mm});
            skLineSegment(sketch, "E2832", {"start": v(-7.29, 1.9) * mm, "end": v(-7.31, 1.89) * mm});
            skLineSegment(sketch, "E2833", {"start": v(-7.31, 1.89) * mm, "end": v(-7.34, 1.89) * mm});
            skLineSegment(sketch, "E2834", {"start": v(-7.34, 1.89) * mm, "end": v(-7.37, 1.88) * mm});
            skLineSegment(sketch, "E2835", {"start": v(-7.37, 1.88) * mm, "end": v(-7.4, 1.88) * mm});
            skLineSegment(sketch, "E2836", {"start": v(-7.4, 1.88) * mm, "end": v(-7.42, 1.87) * mm});
            skLineSegment(sketch, "E2837", {"start": v(-7.42, 1.87) * mm, "end": v(-7.45, 1.87) * mm});
            skLineSegment(sketch, "E2838", {"start": v(-7.45, 1.87) * mm, "end": v(-7.47, 1.86) * mm});
            skLineSegment(sketch, "E2839", {"start": v(-7.47, 1.86) * mm, "end": v(-7.5, 1.85) * mm});
            skLineSegment(sketch, "E2840", {"start": v(-7.5, 1.85) * mm, "end": v(-7.53, 1.85) * mm});
            skLineSegment(sketch, "E2841", {"start": v(-7.53, 1.85) * mm, "end": v(-7.56, 1.84) * mm});
            skLineSegment(sketch, "E2842", {"start": v(-7.56, 1.84) * mm, "end": v(-7.59, 1.84) * mm});
            skLineSegment(sketch, "E2843", {"start": v(-7.59, 1.84) * mm, "end": v(-7.62, 1.83) * mm});
            skLineSegment(sketch, "E2844", {"start": v(-7.62, 1.83) * mm, "end": v(-7.65, 1.82) * mm});
            skLineSegment(sketch, "E2845", {"start": v(-7.65, 1.82) * mm, "end": v(-7.68, 1.81) * mm});
            skLineSegment(sketch, "E2846", {"start": v(-7.68, 1.81) * mm, "end": v(-7.71, 1.8) * mm});
            skLineSegment(sketch, "E2847", {"start": v(-7.71, 1.8) * mm, "end": v(-7.74, 1.8) * mm});
            skArc(sketch, "E2848", {"start": v(-7.74, 1.8) * mm, "mid": v(-7.77, 1.67) * mm, "end": v(-7.8, 1.54) * mm});
            skLineSegment(sketch, "E2849", {"start": v(-6.7, 2.18) * mm, "end": v(-6.7, 2.18) * mm});
            skLineSegment(sketch, "E2850", {"start": v(-6.7, 2.18) * mm, "end": v(-6.7, 2.19) * mm});
            skLineSegment(sketch, "E2851", {"start": v(-6.7, 2.19) * mm, "end": v(-6.7, 2.2) * mm});
            skLineSegment(sketch, "E2852", {"start": v(-6.7, 2.2) * mm, "end": v(-6.72, 2.2) * mm});
            skLineSegment(sketch, "E2853", {"start": v(-6.72, 2.2) * mm, "end": v(-6.72, 2.21) * mm});
            skLineSegment(sketch, "E2854", {"start": v(-6.72, 2.21) * mm, "end": v(-6.74, 2.22) * mm});
            skLineSegment(sketch, "E2855", {"start": v(-6.74, 2.22) * mm, "end": v(-6.75, 2.23) * mm});
            skLineSegment(sketch, "E2856", {"start": v(-6.75, 2.23) * mm, "end": v(-6.75, 2.23) * mm});
            skLineSegment(sketch, "E2857", {"start": v(-6.75, 2.23) * mm, "end": v(-6.77, 2.24) * mm});
            skLineSegment(sketch, "E2858", {"start": v(-6.77, 2.24) * mm, "end": v(-6.78, 2.25) * mm});
            skLineSegment(sketch, "E2859", {"start": v(-6.78, 2.25) * mm, "end": v(-6.79, 2.26) * mm});
            skLineSegment(sketch, "E2860", {"start": v(-6.79, 2.26) * mm, "end": v(-6.8, 2.26) * mm});
            skLineSegment(sketch, "E2861", {"start": v(-6.8, 2.26) * mm, "end": v(-6.81, 2.27) * mm});
            skLineSegment(sketch, "E2862", {"start": v(-6.81, 2.27) * mm, "end": v(-6.83, 2.28) * mm});
            skLineSegment(sketch, "E2863", {"start": v(-6.83, 2.28) * mm, "end": v(-6.84, 2.29) * mm});
            skLineSegment(sketch, "E2864", {"start": v(-6.84, 2.29) * mm, "end": v(-6.86, 2.3) * mm});
            skLineSegment(sketch, "E2865", {"start": v(-6.86, 2.3) * mm, "end": v(-6.87, 2.3) * mm});
            skLineSegment(sketch, "E2866", {"start": v(-6.87, 2.3) * mm, "end": v(-6.88, 2.32) * mm});
            skLineSegment(sketch, "E2867", {"start": v(-6.88, 2.32) * mm, "end": v(-6.9, 2.33) * mm});
            skLineSegment(sketch, "E2868", {"start": v(-6.9, 2.33) * mm, "end": v(-6.92, 2.34) * mm});
            skLineSegment(sketch, "E2869", {"start": v(-6.92, 2.34) * mm, "end": v(-6.93, 2.35) * mm});
            skLineSegment(sketch, "E2870", {"start": v(-6.93, 2.35) * mm, "end": v(-6.95, 2.37) * mm});
            skLineSegment(sketch, "E2871", {"start": v(-6.95, 2.37) * mm, "end": v(-6.96, 2.38) * mm});
            skLineSegment(sketch, "E2872", {"start": v(-6.96, 2.38) * mm, "end": v(-6.98, 2.4) * mm});
            skLineSegment(sketch, "E2873", {"start": v(-6.98, 2.4) * mm, "end": v(-7, 2.4) * mm});
            skLineSegment(sketch, "E2874", {"start": v(-7, 2.4) * mm, "end": v(-7.01, 2.42) * mm});
            skLineSegment(sketch, "E2875", {"start": v(-7.01, 2.42) * mm, "end": v(-7.03, 2.43) * mm});
            skLineSegment(sketch, "E2876", {"start": v(-7.03, 2.43) * mm, "end": v(-7.05, 2.45) * mm});
            skLineSegment(sketch, "E2877", {"start": v(-7.05, 2.45) * mm, "end": v(-7.07, 2.46) * mm});
            skLineSegment(sketch, "E2878", {"start": v(-7.07, 2.46) * mm, "end": v(-7.09, 2.48) * mm});
            skLineSegment(sketch, "E2879", {"start": v(-7.09, 2.48) * mm, "end": v(-7.1, 2.5) * mm});
            skLineSegment(sketch, "E2880", {"start": v(-7.1, 2.5) * mm, "end": v(-7.12, 2.51) * mm});
            skLineSegment(sketch, "E2881", {"start": v(-7.12, 2.51) * mm, "end": v(-7.14, 2.53) * mm});
            skLineSegment(sketch, "E2882", {"start": v(-7.14, 2.53) * mm, "end": v(-7.16, 2.55) * mm});
            skLineSegment(sketch, "E2883", {"start": v(-7.16, 2.55) * mm, "end": v(-7.18, 2.57) * mm});
            skLineSegment(sketch, "E2884", {"start": v(-7.18, 2.57) * mm, "end": v(-7.2, 2.59) * mm});
            skLineSegment(sketch, "E2885", {"start": v(-7.2, 2.59) * mm, "end": v(-7.22, 2.6) * mm});
            skLineSegment(sketch, "E2886", {"start": v(-7.22, 2.6) * mm, "end": v(-7.24, 2.63) * mm});
            skLineSegment(sketch, "E2887", {"start": v(-7.24, 2.63) * mm, "end": v(-7.26, 2.65) * mm});
            skLineSegment(sketch, "E2888", {"start": v(-7.26, 2.65) * mm, "end": v(-7.28, 2.67) * mm});
            skLineSegment(sketch, "E2889", {"start": v(-7.28, 2.67) * mm, "end": v(-7.3, 2.7) * mm});
            skLineSegment(sketch, "E2890", {"start": v(-7.3, 2.7) * mm, "end": v(-7.32, 2.71) * mm});
            skLineSegment(sketch, "E2891", {"start": v(-7.32, 2.71) * mm, "end": v(-7.34, 2.74) * mm});
            skLineSegment(sketch, "E2892", {"start": v(-7.34, 2.74) * mm, "end": v(-7.36, 2.76) * mm});
            skLineSegment(sketch, "E2893", {"start": v(-7.36, 2.76) * mm, "end": v(-7.38, 2.78) * mm});
            skLineSegment(sketch, "E2894", {"start": v(-7.38, 2.78) * mm, "end": v(-7.4, 2.8) * mm});
            skLineSegment(sketch, "E2895", {"start": v(-7.4, 2.8) * mm, "end": v(-7.43, 2.83) * mm});
            skLineSegment(sketch, "E2896", {"start": v(-6.35, 3.05) * mm, "end": v(-6.36, 3.05) * mm});
            skLineSegment(sketch, "E2897", {"start": v(-6.36, 3.05) * mm, "end": v(-6.36, 3.04) * mm});
            skLineSegment(sketch, "E2898", {"start": v(-6.36, 3.04) * mm, "end": v(-6.37, 3.04) * mm});
            skLineSegment(sketch, "E2899", {"start": v(-6.37, 3.04) * mm, "end": v(-6.38, 3.04) * mm});
            skLineSegment(sketch, "E2900", {"start": v(-6.38, 3.04) * mm, "end": v(-6.4, 3.04) * mm});
            skLineSegment(sketch, "E2901", {"start": v(-6.4, 3.04) * mm, "end": v(-6.4, 3.04) * mm});
            skLineSegment(sketch, "E2902", {"start": v(-6.4, 3.04) * mm, "end": v(-6.42, 3.04) * mm});
            skLineSegment(sketch, "E2903", {"start": v(-6.42, 3.04) * mm, "end": v(-6.43, 3.04) * mm});
            skLineSegment(sketch, "E2904", {"start": v(-6.43, 3.04) * mm, "end": v(-6.44, 3.05) * mm});
            skLineSegment(sketch, "E2905", {"start": v(-6.44, 3.05) * mm, "end": v(-6.45, 3.05) * mm});
            skLineSegment(sketch, "E2906", {"start": v(-6.45, 3.05) * mm, "end": v(-6.47, 3.05) * mm});
            skLineSegment(sketch, "E2907", {"start": v(-6.47, 3.05) * mm, "end": v(-6.48, 3.06) * mm});
            skLineSegment(sketch, "E2908", {"start": v(-6.48, 3.06) * mm, "end": v(-6.5, 3.06) * mm});
            skLineSegment(sketch, "E2909", {"start": v(-6.5, 3.06) * mm, "end": v(-6.51, 3.06) * mm});
            skLineSegment(sketch, "E2910", {"start": v(-6.51, 3.06) * mm, "end": v(-6.53, 3.07) * mm});
            skLineSegment(sketch, "E2911", {"start": v(-6.53, 3.07) * mm, "end": v(-6.55, 3.07) * mm});
            skLineSegment(sketch, "E2912", {"start": v(-6.55, 3.07) * mm, "end": v(-6.56, 3.07) * mm});
            skLineSegment(sketch, "E2913", {"start": v(-6.56, 3.07) * mm, "end": v(-6.58, 3.07) * mm});
            skLineSegment(sketch, "E2914", {"start": v(-6.58, 3.07) * mm, "end": v(-6.6, 3.08) * mm});
            skLineSegment(sketch, "E2915", {"start": v(-6.6, 3.08) * mm, "end": v(-6.62, 3.08) * mm});
            skLineSegment(sketch, "E2916", {"start": v(-6.62, 3.08) * mm, "end": v(-6.64, 3.08) * mm});
            skLineSegment(sketch, "E2917", {"start": v(-6.64, 3.08) * mm, "end": v(-6.66, 3.08) * mm});
            skLineSegment(sketch, "E2918", {"start": v(-6.66, 3.08) * mm, "end": v(-6.68, 3.09) * mm});
            skLineSegment(sketch, "E2919", {"start": v(-6.68, 3.09) * mm, "end": v(-6.7, 3.09) * mm});
            skLineSegment(sketch, "E2920", {"start": v(-6.7, 3.09) * mm, "end": v(-6.72, 3.09) * mm});
            skLineSegment(sketch, "E2921", {"start": v(-6.72, 3.09) * mm, "end": v(-6.74, 3.1) * mm});
            skLineSegment(sketch, "E2922", {"start": v(-6.74, 3.1) * mm, "end": v(-6.77, 3.1) * mm});
            skLineSegment(sketch, "E2923", {"start": v(-6.77, 3.1) * mm, "end": v(-6.79, 3.1) * mm});
            skLineSegment(sketch, "E2924", {"start": v(-6.79, 3.1) * mm, "end": v(-6.81, 3.1) * mm});
            skLineSegment(sketch, "E2925", {"start": v(-6.81, 3.1) * mm, "end": v(-6.84, 3.1) * mm});
            skLineSegment(sketch, "E2926", {"start": v(-6.84, 3.1) * mm, "end": v(-6.86, 3.1) * mm});
            skLineSegment(sketch, "E2927", {"start": v(-6.86, 3.1) * mm, "end": v(-6.89, 3.1) * mm});
            skLineSegment(sketch, "E2928", {"start": v(-6.89, 3.1) * mm, "end": v(-6.91, 3.1) * mm});
            skLineSegment(sketch, "E2929", {"start": v(-6.91, 3.1) * mm, "end": v(-6.94, 3.1) * mm});
            skLineSegment(sketch, "E2930", {"start": v(-6.94, 3.1) * mm, "end": v(-6.97, 3.1) * mm});
            skLineSegment(sketch, "E2931", {"start": v(-6.97, 3.1) * mm, "end": v(-7, 3.1) * mm});
            skLineSegment(sketch, "E2932", {"start": v(-7, 3.1) * mm, "end": v(-7.02, 3.1) * mm});
            skLineSegment(sketch, "E2933", {"start": v(-7.02, 3.1) * mm, "end": v(-7.05, 3.1) * mm});
            skLineSegment(sketch, "E2934", {"start": v(-7.05, 3.1) * mm, "end": v(-7.08, 3.1) * mm});
            skLineSegment(sketch, "E2935", {"start": v(-7.08, 3.1) * mm, "end": v(-7.1, 3.1) * mm});
            skLineSegment(sketch, "E2936", {"start": v(-7.1, 3.1) * mm, "end": v(-7.14, 3.1) * mm});
            skLineSegment(sketch, "E2937", {"start": v(-7.14, 3.1) * mm, "end": v(-7.17, 3.1) * mm});
            skLineSegment(sketch, "E2938", {"start": v(-7.17, 3.1) * mm, "end": v(-7.2, 3.09) * mm});
            skLineSegment(sketch, "E2939", {"start": v(-7.2, 3.09) * mm, "end": v(-7.23, 3.09) * mm});
            skLineSegment(sketch, "E2940", {"start": v(-7.23, 3.09) * mm, "end": v(-7.26, 3.08) * mm});
            skLineSegment(sketch, "E2941", {"start": v(-7.26, 3.08) * mm, "end": v(-7.3, 3.08) * mm});
            skLineSegment(sketch, "E2942", {"start": v(-7.3, 3.08) * mm, "end": v(-7.33, 3.08) * mm});
            skArc(sketch, "E2943", {"start": v(-7.33, 3.08) * mm, "mid": v(-7.38, 2.96) * mm, "end": v(-7.43, 2.83) * mm});
            skLineSegment(sketch, "E2944", {"start": v(-6.24, 3.28) * mm, "end": v(-6.24, 3.28) * mm});
            skLineSegment(sketch, "E2945", {"start": v(-6.24, 3.28) * mm, "end": v(-6.24, 3.3) * mm});
            skLineSegment(sketch, "E2946", {"start": v(-6.24, 3.3) * mm, "end": v(-6.24, 3.3) * mm});
            skLineSegment(sketch, "E2947", {"start": v(-6.24, 3.3) * mm, "end": v(-6.25, 3.3) * mm});
            skLineSegment(sketch, "E2948", {"start": v(-6.25, 3.3) * mm, "end": v(-6.25, 3.32) * mm});
            skLineSegment(sketch, "E2949", {"start": v(-6.25, 3.32) * mm, "end": v(-6.26, 3.33) * mm});
            skLineSegment(sketch, "E2950", {"start": v(-6.26, 3.33) * mm, "end": v(-6.27, 3.34) * mm});
            skLineSegment(sketch, "E2951", {"start": v(-6.27, 3.34) * mm, "end": v(-6.28, 3.34) * mm});
            skLineSegment(sketch, "E2952", {"start": v(-6.28, 3.34) * mm, "end": v(-6.29, 3.35) * mm});
            skLineSegment(sketch, "E2953", {"start": v(-6.29, 3.35) * mm, "end": v(-6.3, 3.36) * mm});
            skLineSegment(sketch, "E2954", {"start": v(-6.3, 3.36) * mm, "end": v(-6.3, 3.37) * mm});
            skLineSegment(sketch, "E2955", {"start": v(-6.3, 3.37) * mm, "end": v(-6.32, 3.38) * mm});
            skLineSegment(sketch, "E2956", {"start": v(-6.32, 3.38) * mm, "end": v(-6.33, 3.4) * mm});
            skLineSegment(sketch, "E2957", {"start": v(-6.33, 3.4) * mm, "end": v(-6.34, 3.4) * mm});
            skLineSegment(sketch, "E2958", {"start": v(-6.34, 3.4) * mm, "end": v(-6.36, 3.41) * mm});
            skLineSegment(sketch, "E2959", {"start": v(-6.36, 3.41) * mm, "end": v(-6.37, 3.42) * mm});
            skLineSegment(sketch, "E2960", {"start": v(-6.37, 3.42) * mm, "end": v(-6.38, 3.44) * mm});
            skLineSegment(sketch, "E2961", {"start": v(-6.38, 3.44) * mm, "end": v(-6.4, 3.45) * mm});
            skLineSegment(sketch, "E2962", {"start": v(-6.4, 3.45) * mm, "end": v(-6.4, 3.46) * mm});
            skLineSegment(sketch, "E2963", {"start": v(-6.4, 3.46) * mm, "end": v(-6.42, 3.48) * mm});
            skLineSegment(sketch, "E2964", {"start": v(-6.42, 3.48) * mm, "end": v(-6.43, 3.5) * mm});
            skLineSegment(sketch, "E2965", {"start": v(-6.43, 3.5) * mm, "end": v(-6.45, 3.5) * mm});
            skLineSegment(sketch, "E2966", {"start": v(-6.45, 3.5) * mm, "end": v(-6.46, 3.52) * mm});
            skLineSegment(sketch, "E2967", {"start": v(-6.46, 3.52) * mm, "end": v(-6.47, 3.54) * mm});
            skLineSegment(sketch, "E2968", {"start": v(-6.47, 3.54) * mm, "end": v(-6.49, 3.55) * mm});
            skLineSegment(sketch, "E2969", {"start": v(-6.49, 3.55) * mm, "end": v(-6.5, 3.57) * mm});
            skLineSegment(sketch, "E2970", {"start": v(-6.5, 3.57) * mm, "end": v(-6.52, 3.59) * mm});
            skLineSegment(sketch, "E2971", {"start": v(-6.52, 3.59) * mm, "end": v(-6.53, 3.6) * mm});
            skLineSegment(sketch, "E2972", {"start": v(-6.53, 3.6) * mm, "end": v(-6.55, 3.62) * mm});
            skLineSegment(sketch, "E2973", {"start": v(-6.55, 3.62) * mm, "end": v(-6.56, 3.64) * mm});
            skLineSegment(sketch, "E2974", {"start": v(-6.56, 3.64) * mm, "end": v(-6.58, 3.66) * mm});
            skLineSegment(sketch, "E2975", {"start": v(-6.58, 3.66) * mm, "end": v(-6.6, 3.68) * mm});
            skLineSegment(sketch, "E2976", {"start": v(-6.6, 3.68) * mm, "end": v(-6.6, 3.7) * mm});
            skLineSegment(sketch, "E2977", {"start": v(-6.6, 3.7) * mm, "end": v(-6.63, 3.72) * mm});
            skLineSegment(sketch, "E2978", {"start": v(-6.63, 3.72) * mm, "end": v(-6.64, 3.74) * mm});
            skLineSegment(sketch, "E2979", {"start": v(-6.64, 3.74) * mm, "end": v(-6.66, 3.77) * mm});
            skLineSegment(sketch, "E2980", {"start": v(-6.66, 3.77) * mm, "end": v(-6.67, 3.79) * mm});
            skLineSegment(sketch, "E2981", {"start": v(-6.67, 3.79) * mm, "end": v(-6.69, 3.81) * mm});
            skLineSegment(sketch, "E2982", {"start": v(-6.69, 3.81) * mm, "end": v(-6.7, 3.84) * mm});
            skLineSegment(sketch, "E2983", {"start": v(-6.7, 3.84) * mm, "end": v(-6.72, 3.86) * mm});
            skLineSegment(sketch, "E2984", {"start": v(-6.72, 3.86) * mm, "end": v(-6.74, 3.89) * mm});
            skLineSegment(sketch, "E2985", {"start": v(-6.74, 3.89) * mm, "end": v(-6.76, 3.91) * mm});
            skLineSegment(sketch, "E2986", {"start": v(-6.76, 3.91) * mm, "end": v(-6.77, 3.94) * mm});
            skLineSegment(sketch, "E2987", {"start": v(-6.77, 3.94) * mm, "end": v(-6.79, 3.96) * mm});
            skLineSegment(sketch, "E2988", {"start": v(-6.79, 3.96) * mm, "end": v(-6.8, 4) * mm});
            skLineSegment(sketch, "E2989", {"start": v(-6.8, 4) * mm, "end": v(-6.82, 4.02) * mm});
            skLineSegment(sketch, "E2990", {"start": v(-6.82, 4.02) * mm, "end": v(-6.84, 4.05) * mm});
            skLineSegment(sketch, "E2991", {"start": v(-5.74, 4.08) * mm, "end": v(-5.75, 4.08) * mm});
            skLineSegment(sketch, "E2992", {"start": v(-5.75, 4.08) * mm, "end": v(-5.75, 4.08) * mm});
            skLineSegment(sketch, "E2993", {"start": v(-5.75, 4.08) * mm, "end": v(-5.76, 4.07) * mm});
            skLineSegment(sketch, "E2994", {"start": v(-5.76, 4.07) * mm, "end": v(-5.77, 4.07) * mm});
            skLineSegment(sketch, "E2995", {"start": v(-5.77, 4.07) * mm, "end": v(-5.78, 4.08) * mm});
            skLineSegment(sketch, "E2996", {"start": v(-5.78, 4.08) * mm, "end": v(-5.8, 4.08) * mm});
            skLineSegment(sketch, "E2997", {"start": v(-5.8, 4.08) * mm, "end": v(-5.81, 4.08) * mm});
            skLineSegment(sketch, "E2998", {"start": v(-5.81, 4.08) * mm, "end": v(-5.82, 4.09) * mm});
            skLineSegment(sketch, "E2999", {"start": v(-5.82, 4.09) * mm, "end": v(-5.83, 4.1) * mm});
            skLineSegment(sketch, "E3000", {"start": v(-5.83, 4.1) * mm, "end": v(-5.84, 4.1) * mm});
            skLineSegment(sketch, "E3001", {"start": v(-5.84, 4.1) * mm, "end": v(-5.86, 4.1) * mm});
            skLineSegment(sketch, "E3002", {"start": v(-5.86, 4.1) * mm, "end": v(-5.87, 4.1) * mm});
            skLineSegment(sketch, "E3003", {"start": v(-5.87, 4.1) * mm, "end": v(-5.89, 4.11) * mm});
            skLineSegment(sketch, "E3004", {"start": v(-5.89, 4.11) * mm, "end": v(-5.9, 4.12) * mm});
            skLineSegment(sketch, "E3005", {"start": v(-5.9, 4.12) * mm, "end": v(-5.92, 4.12) * mm});
            skLineSegment(sketch, "E3006", {"start": v(-5.92, 4.12) * mm, "end": v(-5.93, 4.13) * mm});
            skLineSegment(sketch, "E3007", {"start": v(-5.93, 4.13) * mm, "end": v(-5.95, 4.14) * mm});
            skLineSegment(sketch, "E3008", {"start": v(-5.95, 4.14) * mm, "end": v(-5.97, 4.14) * mm});
            skLineSegment(sketch, "E3009", {"start": v(-5.97, 4.14) * mm, "end": v(-5.98, 4.15) * mm});
            skLineSegment(sketch, "E3010", {"start": v(-5.98, 4.15) * mm, "end": v(-6, 4.15) * mm});
            skLineSegment(sketch, "E3011", {"start": v(-6, 4.15) * mm, "end": v(-6.02, 4.16) * mm});
            skLineSegment(sketch, "E3012", {"start": v(-6.02, 4.16) * mm, "end": v(-6.04, 4.16) * mm});
            skLineSegment(sketch, "E3013", {"start": v(-6.04, 4.16) * mm, "end": v(-6.06, 4.17) * mm});
            skLineSegment(sketch, "E3014", {"start": v(-6.06, 4.17) * mm, "end": v(-6.08, 4.18) * mm});
            skLineSegment(sketch, "E3015", {"start": v(-6.08, 4.18) * mm, "end": v(-6.1, 4.18) * mm});
            skLineSegment(sketch, "E3016", {"start": v(-6.1, 4.18) * mm, "end": v(-6.12, 4.19) * mm});
            skLineSegment(sketch, "E3017", {"start": v(-6.12, 4.19) * mm, "end": v(-6.14, 4.2) * mm});
            skLineSegment(sketch, "E3018", {"start": v(-6.14, 4.2) * mm, "end": v(-6.17, 4.2) * mm});
            skLineSegment(sketch, "E3019", {"start": v(-6.17, 4.2) * mm, "end": v(-6.2, 4.2) * mm});
            skLineSegment(sketch, "E3020", {"start": v(-6.2, 4.2) * mm, "end": v(-6.21, 4.2) * mm});
            skLineSegment(sketch, "E3021", {"start": v(-6.21, 4.2) * mm, "end": v(-6.24, 4.21) * mm});
            skLineSegment(sketch, "E3022", {"start": v(-6.24, 4.21) * mm, "end": v(-6.26, 4.22) * mm});
            skLineSegment(sketch, "E3023", {"start": v(-6.26, 4.22) * mm, "end": v(-6.29, 4.22) * mm});
            skLineSegment(sketch, "E3024", {"start": v(-6.29, 4.22) * mm, "end": v(-6.31, 4.23) * mm});
            skLineSegment(sketch, "E3025", {"start": v(-6.31, 4.23) * mm, "end": v(-6.34, 4.23) * mm});
            skLineSegment(sketch, "E3026", {"start": v(-6.34, 4.23) * mm, "end": v(-6.37, 4.24) * mm});
            skLineSegment(sketch, "E3027", {"start": v(-6.37, 4.24) * mm, "end": v(-6.4, 4.24) * mm});
            skLineSegment(sketch, "E3028", {"start": v(-6.4, 4.24) * mm, "end": v(-6.42, 4.24) * mm});
            skLineSegment(sketch, "E3029", {"start": v(-6.42, 4.24) * mm, "end": v(-6.45, 4.25) * mm});
            skLineSegment(sketch, "E3030", {"start": v(-6.45, 4.25) * mm, "end": v(-6.48, 4.25) * mm});
            skLineSegment(sketch, "E3031", {"start": v(-6.48, 4.25) * mm, "end": v(-6.51, 4.25) * mm});
            skLineSegment(sketch, "E3032", {"start": v(-6.51, 4.25) * mm, "end": v(-6.54, 4.26) * mm});
            skLineSegment(sketch, "E3033", {"start": v(-6.54, 4.26) * mm, "end": v(-6.57, 4.26) * mm});
            skLineSegment(sketch, "E3034", {"start": v(-6.57, 4.26) * mm, "end": v(-6.6, 4.26) * mm});
            skLineSegment(sketch, "E3035", {"start": v(-6.6, 4.26) * mm, "end": v(-6.64, 4.27) * mm});
            skLineSegment(sketch, "E3036", {"start": v(-6.64, 4.27) * mm, "end": v(-6.67, 4.27) * mm});
            skLineSegment(sketch, "E3037", {"start": v(-6.67, 4.27) * mm, "end": v(-6.7, 4.27) * mm});
            skArc(sketch, "E3038", {"start": v(-6.7, 4.27) * mm, "mid": v(-6.77, 4.16) * mm, "end": v(-6.84, 4.05) * mm});
            skLineSegment(sketch, "E3039", {"start": v(-5.6, 4.28) * mm, "end": v(-5.6, 4.3) * mm});
            skLineSegment(sketch, "E3040", {"start": v(-5.6, 4.3) * mm, "end": v(-5.6, 4.3) * mm});
            skLineSegment(sketch, "E3041", {"start": v(-5.6, 4.3) * mm, "end": v(-5.6, 4.31) * mm});
            skLineSegment(sketch, "E3042", {"start": v(-5.6, 4.31) * mm, "end": v(-5.6, 4.33) * mm});
            skLineSegment(sketch, "E3043", {"start": v(-5.6, 4.33) * mm, "end": v(-5.6, 4.34) * mm});
            skLineSegment(sketch, "E3044", {"start": v(-5.6, 4.34) * mm, "end": v(-5.62, 4.35) * mm});
            skLineSegment(sketch, "E3045", {"start": v(-5.62, 4.35) * mm, "end": v(-5.62, 4.36) * mm});
            skLineSegment(sketch, "E3046", {"start": v(-5.62, 4.36) * mm, "end": v(-5.63, 4.37) * mm});
            skLineSegment(sketch, "E3047", {"start": v(-5.63, 4.37) * mm, "end": v(-5.64, 4.38) * mm});
            skLineSegment(sketch, "E3048", {"start": v(-5.64, 4.38) * mm, "end": v(-5.65, 4.39) * mm});
            skLineSegment(sketch, "E3049", {"start": v(-5.65, 4.39) * mm, "end": v(-5.66, 4.4) * mm});
            skLineSegment(sketch, "E3050", {"start": v(-5.66, 4.4) * mm, "end": v(-5.67, 4.41) * mm});
            skLineSegment(sketch, "E3051", {"start": v(-5.67, 4.41) * mm, "end": v(-5.68, 4.42) * mm});
            skLineSegment(sketch, "E3052", {"start": v(-5.68, 4.42) * mm, "end": v(-5.69, 4.44) * mm});
            skLineSegment(sketch, "E3053", {"start": v(-5.69, 4.44) * mm, "end": v(-5.7, 4.45) * mm});
            skLineSegment(sketch, "E3054", {"start": v(-5.7, 4.45) * mm, "end": v(-5.7, 4.47) * mm});
            skLineSegment(sketch, "E3055", {"start": v(-5.7, 4.47) * mm, "end": v(-5.72, 4.48) * mm});
            skLineSegment(sketch, "E3056", {"start": v(-5.72, 4.48) * mm, "end": v(-5.73, 4.5) * mm});
            skLineSegment(sketch, "E3057", {"start": v(-5.73, 4.5) * mm, "end": v(-5.74, 4.51) * mm});
            skLineSegment(sketch, "E3058", {"start": v(-5.74, 4.51) * mm, "end": v(-5.75, 4.53) * mm});
            skLineSegment(sketch, "E3059", {"start": v(-5.75, 4.53) * mm, "end": v(-5.76, 4.54) * mm});
            skLineSegment(sketch, "E3060", {"start": v(-5.76, 4.54) * mm, "end": v(-5.77, 4.56) * mm});
            skLineSegment(sketch, "E3061", {"start": v(-5.77, 4.56) * mm, "end": v(-5.78, 4.58) * mm});
            skLineSegment(sketch, "E3062", {"start": v(-5.78, 4.58) * mm, "end": v(-5.8, 4.6) * mm});
            skLineSegment(sketch, "E3063", {"start": v(-5.8, 4.6) * mm, "end": v(-5.8, 4.62) * mm});
            skLineSegment(sketch, "E3064", {"start": v(-5.8, 4.62) * mm, "end": v(-5.82, 4.64) * mm});
            skLineSegment(sketch, "E3065", {"start": v(-5.82, 4.64) * mm, "end": v(-5.83, 4.66) * mm});
            skLineSegment(sketch, "E3066", {"start": v(-5.83, 4.66) * mm, "end": v(-5.84, 4.68) * mm});
            skLineSegment(sketch, "E3067", {"start": v(-5.84, 4.68) * mm, "end": v(-5.85, 4.7) * mm});
            skLineSegment(sketch, "E3068", {"start": v(-5.85, 4.7) * mm, "end": v(-5.86, 4.72) * mm});
            skLineSegment(sketch, "E3069", {"start": v(-5.86, 4.72) * mm, "end": v(-5.88, 4.74) * mm});
            skLineSegment(sketch, "E3070", {"start": v(-5.88, 4.74) * mm, "end": v(-5.89, 4.76) * mm});
            skLineSegment(sketch, "E3071", {"start": v(-5.89, 4.76) * mm, "end": v(-5.9, 4.79) * mm});
            skLineSegment(sketch, "E3072", {"start": v(-5.9, 4.79) * mm, "end": v(-5.91, 4.81) * mm});
            skLineSegment(sketch, "E3073", {"start": v(-5.91, 4.81) * mm, "end": v(-5.92, 4.84) * mm});
            skLineSegment(sketch, "E3074", {"start": v(-5.92, 4.84) * mm, "end": v(-5.94, 4.86) * mm});
            skLineSegment(sketch, "E3075", {"start": v(-5.94, 4.86) * mm, "end": v(-5.95, 4.89) * mm});
            skLineSegment(sketch, "E3076", {"start": v(-5.95, 4.89) * mm, "end": v(-5.96, 4.91) * mm});
            skLineSegment(sketch, "E3077", {"start": v(-5.96, 4.91) * mm, "end": v(-5.97, 4.94) * mm});
            skLineSegment(sketch, "E3078", {"start": v(-5.97, 4.94) * mm, "end": v(-5.98, 4.97) * mm});
            skLineSegment(sketch, "E3079", {"start": v(-5.98, 4.97) * mm, "end": v(-6, 5) * mm});
            skLineSegment(sketch, "E3080", {"start": v(-6, 5) * mm, "end": v(-6, 5.02) * mm});
            skLineSegment(sketch, "E3081", {"start": v(-6, 5.02) * mm, "end": v(-6.02, 5.05) * mm});
            skLineSegment(sketch, "E3082", {"start": v(-6.02, 5.05) * mm, "end": v(-6.03, 5.08) * mm});
            skLineSegment(sketch, "E3083", {"start": v(-6.03, 5.08) * mm, "end": v(-6.04, 5.11) * mm});
            skLineSegment(sketch, "E3084", {"start": v(-6.04, 5.11) * mm, "end": v(-6.06, 5.14) * mm});
            skLineSegment(sketch, "E3085", {"start": v(-4.97, 5) * mm, "end": v(-4.97, 5) * mm});
            skLineSegment(sketch, "E3086", {"start": v(-4.97, 5) * mm, "end": v(-4.98, 4.99) * mm});
            skLineSegment(sketch, "E3087", {"start": v(-4.98, 4.99) * mm, "end": v(-5, 4.99) * mm});
            skLineSegment(sketch, "E3088", {"start": v(-5, 4.99) * mm, "end": v(-5, 5) * mm});
            skLineSegment(sketch, "E3089", {"start": v(-5, 5) * mm, "end": v(-5.01, 5) * mm});
            skLineSegment(sketch, "E3090", {"start": v(-5.01, 5) * mm, "end": v(-5.02, 5) * mm});
            skLineSegment(sketch, "E3091", {"start": v(-5.02, 5) * mm, "end": v(-5.04, 5) * mm});
            skLineSegment(sketch, "E3092", {"start": v(-5.04, 5) * mm, "end": v(-5.04, 5.01) * mm});
            skLineSegment(sketch, "E3093", {"start": v(-5.04, 5.01) * mm, "end": v(-5.05, 5.02) * mm});
            skLineSegment(sketch, "E3094", {"start": v(-5.05, 5.02) * mm, "end": v(-5.07, 5.03) * mm});
            skLineSegment(sketch, "E3095", {"start": v(-5.07, 5.03) * mm, "end": v(-5.08, 5.03) * mm});
            skLineSegment(sketch, "E3096", {"start": v(-5.08, 5.03) * mm, "end": v(-5.1, 5.04) * mm});
            skLineSegment(sketch, "E3097", {"start": v(-5.1, 5.04) * mm, "end": v(-5.1, 5.05) * mm});
            skLineSegment(sketch, "E3098", {"start": v(-5.1, 5.05) * mm, "end": v(-5.12, 5.06) * mm});
            skLineSegment(sketch, "E3099", {"start": v(-5.12, 5.06) * mm, "end": v(-5.13, 5.07) * mm});
            skLineSegment(sketch, "E3100", {"start": v(-5.13, 5.07) * mm, "end": v(-5.15, 5.07) * mm});
            skLineSegment(sketch, "E3101", {"start": v(-5.15, 5.07) * mm, "end": v(-5.16, 5.08) * mm});
            skLineSegment(sketch, "E3102", {"start": v(-5.16, 5.08) * mm, "end": v(-5.18, 5.1) * mm});
            skLineSegment(sketch, "E3103", {"start": v(-5.18, 5.1) * mm, "end": v(-5.2, 5.1) * mm});
            skLineSegment(sketch, "E3104", {"start": v(-5.2, 5.1) * mm, "end": v(-5.21, 5.1) * mm});
            skLineSegment(sketch, "E3105", {"start": v(-5.21, 5.1) * mm, "end": v(-5.23, 5.12) * mm});
            skLineSegment(sketch, "E3106", {"start": v(-5.23, 5.12) * mm, "end": v(-5.25, 5.12) * mm});
            skLineSegment(sketch, "E3107", {"start": v(-5.25, 5.12) * mm, "end": v(-5.27, 5.13) * mm});
            skLineSegment(sketch, "E3108", {"start": v(-5.27, 5.13) * mm, "end": v(-5.29, 5.14) * mm});
            skLineSegment(sketch, "E3109", {"start": v(-5.29, 5.14) * mm, "end": v(-5.3, 5.15) * mm});
            skLineSegment(sketch, "E3110", {"start": v(-5.3, 5.15) * mm, "end": v(-5.33, 5.16) * mm});
            skLineSegment(sketch, "E3111", {"start": v(-5.33, 5.16) * mm, "end": v(-5.35, 5.17) * mm});
            skLineSegment(sketch, "E3112", {"start": v(-5.35, 5.17) * mm, "end": v(-5.37, 5.18) * mm});
            skLineSegment(sketch, "E3113", {"start": v(-5.37, 5.18) * mm, "end": v(-5.39, 5.19) * mm});
            skLineSegment(sketch, "E3114", {"start": v(-5.39, 5.19) * mm, "end": v(-5.41, 5.2) * mm});
            skLineSegment(sketch, "E3115", {"start": v(-5.41, 5.2) * mm, "end": v(-5.44, 5.2) * mm});
            skLineSegment(sketch, "E3116", {"start": v(-5.44, 5.2) * mm, "end": v(-5.46, 5.21) * mm});
            skLineSegment(sketch, "E3117", {"start": v(-5.46, 5.21) * mm, "end": v(-5.48, 5.22) * mm});
            skLineSegment(sketch, "E3118", {"start": v(-5.48, 5.22) * mm, "end": v(-5.5, 5.23) * mm});
            skLineSegment(sketch, "E3119", {"start": v(-5.5, 5.23) * mm, "end": v(-5.53, 5.24) * mm});
            skLineSegment(sketch, "E3120", {"start": v(-5.53, 5.24) * mm, "end": v(-5.56, 5.25) * mm});
            skLineSegment(sketch, "E3121", {"start": v(-5.56, 5.25) * mm, "end": v(-5.59, 5.26) * mm});
            skLineSegment(sketch, "E3122", {"start": v(-5.59, 5.26) * mm, "end": v(-5.61, 5.27) * mm});
            skLineSegment(sketch, "E3123", {"start": v(-5.61, 5.27) * mm, "end": v(-5.64, 5.28) * mm});
            skLineSegment(sketch, "E3124", {"start": v(-5.64, 5.28) * mm, "end": v(-5.67, 5.29) * mm});
            skLineSegment(sketch, "E3125", {"start": v(-5.67, 5.29) * mm, "end": v(-5.7, 5.3) * mm});
            skLineSegment(sketch, "E3126", {"start": v(-5.7, 5.3) * mm, "end": v(-5.73, 5.3) * mm});
            skLineSegment(sketch, "E3127", {"start": v(-5.73, 5.3) * mm, "end": v(-5.76, 5.31) * mm});
            skLineSegment(sketch, "E3128", {"start": v(-5.76, 5.31) * mm, "end": v(-5.79, 5.32) * mm});
            skLineSegment(sketch, "E3129", {"start": v(-5.79, 5.32) * mm, "end": v(-5.82, 5.33) * mm});
            skLineSegment(sketch, "E3130", {"start": v(-5.82, 5.33) * mm, "end": v(-5.85, 5.33) * mm});
            skLineSegment(sketch, "E3131", {"start": v(-5.85, 5.33) * mm, "end": v(-5.88, 5.34) * mm});
            skArc(sketch, "E3132", {"start": v(-5.88, 5.34) * mm, "mid": v(-5.97, 5.24) * mm, "end": v(-6.06, 5.14) * mm});
            skLineSegment(sketch, "E3133", {"start": v(-4.79, 5.17) * mm, "end": v(-4.78, 5.17) * mm});
            skLineSegment(sketch, "E3134", {"start": v(-4.78, 5.17) * mm, "end": v(-4.78, 5.18) * mm});
            skLineSegment(sketch, "E3135", {"start": v(-4.78, 5.18) * mm, "end": v(-4.78, 5.19) * mm});
            skLineSegment(sketch, "E3136", {"start": v(-4.78, 5.19) * mm, "end": v(-4.78, 5.2) * mm});
            skLineSegment(sketch, "E3137", {"start": v(-4.78, 5.2) * mm, "end": v(-4.79, 5.2) * mm});
            skLineSegment(sketch, "E3138", {"start": v(-4.79, 5.2) * mm, "end": v(-4.8, 5.22) * mm});
            skLineSegment(sketch, "E3139", {"start": v(-4.8, 5.22) * mm, "end": v(-4.8, 5.24) * mm});
            skLineSegment(sketch, "E3140", {"start": v(-4.8, 5.24) * mm, "end": v(-4.8, 5.24) * mm});
            skLineSegment(sketch, "E3141", {"start": v(-4.8, 5.24) * mm, "end": v(-4.8, 5.25) * mm});
            skLineSegment(sketch, "E3142", {"start": v(-4.8, 5.25) * mm, "end": v(-4.82, 5.27) * mm});
            skLineSegment(sketch, "E3143", {"start": v(-4.82, 5.27) * mm, "end": v(-4.82, 5.28) * mm});
            skLineSegment(sketch, "E3144", {"start": v(-4.82, 5.28) * mm, "end": v(-4.83, 5.3) * mm});
            skLineSegment(sketch, "E3145", {"start": v(-4.83, 5.3) * mm, "end": v(-4.84, 5.3) * mm});
            skLineSegment(sketch, "E3146", {"start": v(-4.84, 5.3) * mm, "end": v(-4.84, 5.32) * mm});
            skLineSegment(sketch, "E3147", {"start": v(-4.84, 5.32) * mm, "end": v(-4.85, 5.33) * mm});
            skLineSegment(sketch, "E3148", {"start": v(-4.85, 5.33) * mm, "end": v(-4.86, 5.35) * mm});
            skLineSegment(sketch, "E3149", {"start": v(-4.86, 5.35) * mm, "end": v(-4.87, 5.37) * mm});
            skLineSegment(sketch, "E3150", {"start": v(-4.87, 5.37) * mm, "end": v(-4.88, 5.38) * mm});
            skLineSegment(sketch, "E3151", {"start": v(-4.88, 5.38) * mm, "end": v(-4.88, 5.4) * mm});
            skLineSegment(sketch, "E3152", {"start": v(-4.88, 5.4) * mm, "end": v(-4.9, 5.42) * mm});
            skLineSegment(sketch, "E3153", {"start": v(-4.9, 5.42) * mm, "end": v(-4.9, 5.43) * mm});
            skLineSegment(sketch, "E3154", {"start": v(-4.9, 5.43) * mm, "end": v(-4.9, 5.45) * mm});
            skLineSegment(sketch, "E3155", {"start": v(-4.9, 5.45) * mm, "end": v(-4.91, 5.47) * mm});
            skLineSegment(sketch, "E3156", {"start": v(-4.91, 5.47) * mm, "end": v(-4.92, 5.5) * mm});
            skLineSegment(sketch, "E3157", {"start": v(-4.92, 5.5) * mm, "end": v(-4.93, 5.51) * mm});
            skLineSegment(sketch, "E3158", {"start": v(-4.93, 5.51) * mm, "end": v(-4.94, 5.53) * mm});
            skLineSegment(sketch, "E3159", {"start": v(-4.94, 5.53) * mm, "end": v(-4.95, 5.55) * mm});
            skLineSegment(sketch, "E3160", {"start": v(-4.95, 5.55) * mm, "end": v(-4.96, 5.57) * mm});
            skLineSegment(sketch, "E3161", {"start": v(-4.96, 5.57) * mm, "end": v(-4.96, 5.6) * mm});
            skLineSegment(sketch, "E3162", {"start": v(-4.96, 5.6) * mm, "end": v(-4.97, 5.62) * mm});
            skLineSegment(sketch, "E3163", {"start": v(-4.97, 5.62) * mm, "end": v(-4.98, 5.64) * mm});
            skLineSegment(sketch, "E3164", {"start": v(-4.98, 5.64) * mm, "end": v(-4.99, 5.67) * mm});
            skLineSegment(sketch, "E3165", {"start": v(-4.99, 5.67) * mm, "end": v(-5, 5.7) * mm});
            skLineSegment(sketch, "E3166", {"start": v(-5, 5.7) * mm, "end": v(-5, 5.72) * mm});
            skLineSegment(sketch, "E3167", {"start": v(-5, 5.72) * mm, "end": v(-5.01, 5.74) * mm});
            skLineSegment(sketch, "E3168", {"start": v(-5.01, 5.74) * mm, "end": v(-5.02, 5.77) * mm});
            skLineSegment(sketch, "E3169", {"start": v(-5.02, 5.77) * mm, "end": v(-5.03, 5.8) * mm});
            skLineSegment(sketch, "E3170", {"start": v(-5.03, 5.8) * mm, "end": v(-5.03, 5.82) * mm});
            skLineSegment(sketch, "E3171", {"start": v(-5.03, 5.82) * mm, "end": v(-5.04, 5.85) * mm});
            skLineSegment(sketch, "E3172", {"start": v(-5.04, 5.85) * mm, "end": v(-5.05, 5.88) * mm});
            skLineSegment(sketch, "E3173", {"start": v(-5.05, 5.88) * mm, "end": v(-5.06, 5.9) * mm});
            skLineSegment(sketch, "E3174", {"start": v(-5.06, 5.9) * mm, "end": v(-5.06, 5.94) * mm});
            skLineSegment(sketch, "E3175", {"start": v(-5.06, 5.94) * mm, "end": v(-5.07, 5.97) * mm});
            skLineSegment(sketch, "E3176", {"start": v(-5.07, 5.97) * mm, "end": v(-5.08, 6) * mm});
            skLineSegment(sketch, "E3177", {"start": v(-5.08, 6) * mm, "end": v(-5.08, 6.03) * mm});
            skLineSegment(sketch, "E3178", {"start": v(-5.08, 6.03) * mm, "end": v(-5.1, 6.06) * mm});
            skLineSegment(sketch, "E3179", {"start": v(-5.1, 6.06) * mm, "end": v(-5.1, 6.1) * mm});
            skLineSegment(sketch, "E3180", {"start": v(-4.05, 5.76) * mm, "end": v(-4.06, 5.76) * mm});
            skLineSegment(sketch, "E3181", {"start": v(-4.06, 5.76) * mm, "end": v(-4.07, 5.76) * mm});
            skLineSegment(sketch, "E3182", {"start": v(-4.07, 5.76) * mm, "end": v(-4.07, 5.76) * mm});
            skLineSegment(sketch, "E3183", {"start": v(-4.07, 5.76) * mm, "end": v(-4.08, 5.76) * mm});
            skLineSegment(sketch, "E3184", {"start": v(-4.08, 5.76) * mm, "end": v(-4.1, 5.77) * mm});
            skLineSegment(sketch, "E3185", {"start": v(-4.1, 5.77) * mm, "end": v(-4.1, 5.78) * mm});
            skLineSegment(sketch, "E3186", {"start": v(-4.1, 5.78) * mm, "end": v(-4.12, 5.79) * mm});
            skLineSegment(sketch, "E3187", {"start": v(-4.12, 5.79) * mm, "end": v(-4.12, 5.8) * mm});
            skLineSegment(sketch, "E3188", {"start": v(-4.12, 5.8) * mm, "end": v(-4.13, 5.8) * mm});
            skLineSegment(sketch, "E3189", {"start": v(-4.13, 5.8) * mm, "end": v(-4.14, 5.81) * mm});
            skLineSegment(sketch, "E3190", {"start": v(-4.14, 5.81) * mm, "end": v(-4.15, 5.82) * mm});
            skLineSegment(sketch, "E3191", {"start": v(-4.15, 5.82) * mm, "end": v(-4.16, 5.83) * mm});
            skLineSegment(sketch, "E3192", {"start": v(-4.16, 5.83) * mm, "end": v(-4.18, 5.84) * mm});
            skLineSegment(sketch, "E3193", {"start": v(-4.18, 5.84) * mm, "end": v(-4.19, 5.85) * mm});
            skLineSegment(sketch, "E3194", {"start": v(-4.19, 5.85) * mm, "end": v(-4.2, 5.86) * mm});
            skLineSegment(sketch, "E3195", {"start": v(-4.2, 5.86) * mm, "end": v(-4.21, 5.87) * mm});
            skLineSegment(sketch, "E3196", {"start": v(-4.21, 5.87) * mm, "end": v(-4.23, 5.88) * mm});
            skLineSegment(sketch, "E3197", {"start": v(-4.23, 5.88) * mm, "end": v(-4.24, 5.9) * mm});
            skLineSegment(sketch, "E3198", {"start": v(-4.24, 5.9) * mm, "end": v(-4.26, 5.9) * mm});
            skLineSegment(sketch, "E3199", {"start": v(-4.26, 5.9) * mm, "end": v(-4.27, 5.91) * mm});
            skLineSegment(sketch, "E3200", {"start": v(-4.27, 5.91) * mm, "end": v(-4.29, 5.93) * mm});
            skLineSegment(sketch, "E3201", {"start": v(-4.29, 5.93) * mm, "end": v(-4.3, 5.94) * mm});
            skLineSegment(sketch, "E3202", {"start": v(-4.3, 5.94) * mm, "end": v(-4.32, 5.95) * mm});
            skLineSegment(sketch, "E3203", {"start": v(-4.32, 5.95) * mm, "end": v(-4.34, 5.96) * mm});
            skLineSegment(sketch, "E3204", {"start": v(-4.34, 5.96) * mm, "end": v(-4.36, 5.97) * mm});
            skLineSegment(sketch, "E3205", {"start": v(-4.36, 5.97) * mm, "end": v(-4.38, 5.99) * mm});
            skLineSegment(sketch, "E3206", {"start": v(-4.38, 5.99) * mm, "end": v(-4.4, 6) * mm});
            skLineSegment(sketch, "E3207", {"start": v(-4.4, 6) * mm, "end": v(-4.41, 6.01) * mm});
            skLineSegment(sketch, "E3208", {"start": v(-4.41, 6.01) * mm, "end": v(-4.43, 6.02) * mm});
            skLineSegment(sketch, "E3209", {"start": v(-4.43, 6.02) * mm, "end": v(-4.45, 6.04) * mm});
            skLineSegment(sketch, "E3210", {"start": v(-4.45, 6.04) * mm, "end": v(-4.48, 6.05) * mm});
            skLineSegment(sketch, "E3211", {"start": v(-4.48, 6.05) * mm, "end": v(-4.5, 6.06) * mm});
            skLineSegment(sketch, "E3212", {"start": v(-4.5, 6.06) * mm, "end": v(-4.52, 6.08) * mm});
            skLineSegment(sketch, "E3213", {"start": v(-4.52, 6.08) * mm, "end": v(-4.54, 6.09) * mm});
            skLineSegment(sketch, "E3214", {"start": v(-4.54, 6.09) * mm, "end": v(-4.57, 6.1) * mm});
            skLineSegment(sketch, "E3215", {"start": v(-4.57, 6.1) * mm, "end": v(-4.6, 6.11) * mm});
            skLineSegment(sketch, "E3216", {"start": v(-4.6, 6.11) * mm, "end": v(-4.61, 6.13) * mm});
            skLineSegment(sketch, "E3217", {"start": v(-4.61, 6.13) * mm, "end": v(-4.64, 6.14) * mm});
            skLineSegment(sketch, "E3218", {"start": v(-4.64, 6.14) * mm, "end": v(-4.67, 6.15) * mm});
            skLineSegment(sketch, "E3219", {"start": v(-4.67, 6.15) * mm, "end": v(-4.7, 6.17) * mm});
            skLineSegment(sketch, "E3220", {"start": v(-4.7, 6.17) * mm, "end": v(-4.72, 6.18) * mm});
            skLineSegment(sketch, "E3221", {"start": v(-4.72, 6.18) * mm, "end": v(-4.75, 6.2) * mm});
            skLineSegment(sketch, "E3222", {"start": v(-4.75, 6.2) * mm, "end": v(-4.77, 6.2) * mm});
            skLineSegment(sketch, "E3223", {"start": v(-4.77, 6.2) * mm, "end": v(-4.8, 6.22) * mm});
            skLineSegment(sketch, "E3224", {"start": v(-4.8, 6.22) * mm, "end": v(-4.83, 6.23) * mm});
            skLineSegment(sketch, "E3225", {"start": v(-4.83, 6.23) * mm, "end": v(-4.86, 6.25) * mm});
            skLineSegment(sketch, "E3226", {"start": v(-4.86, 6.25) * mm, "end": v(-4.9, 6.26) * mm});
            skArc(sketch, "E3227", {"start": v(-4.9, 6.26) * mm, "mid": v(-5, 6.18) * mm, "end": v(-5.1, 6.1) * mm});
            skLineSegment(sketch, "E3228", {"start": v(-3.84, 5.9) * mm, "end": v(-3.84, 5.9) * mm});
            skLineSegment(sketch, "E3229", {"start": v(-3.84, 5.9) * mm, "end": v(-3.84, 5.91) * mm});
            skLineSegment(sketch, "E3230", {"start": v(-3.84, 5.91) * mm, "end": v(-3.83, 5.92) * mm});
            skLineSegment(sketch, "E3231", {"start": v(-3.83, 5.92) * mm, "end": v(-3.83, 5.93) * mm});
            skLineSegment(sketch, "E3232", {"start": v(-3.83, 5.93) * mm, "end": v(-3.84, 5.94) * mm});
            skLineSegment(sketch, "E3233", {"start": v(-3.84, 5.94) * mm, "end": v(-3.84, 5.96) * mm});
            skLineSegment(sketch, "E3234", {"start": v(-3.84, 5.96) * mm, "end": v(-3.84, 5.97) * mm});
            skLineSegment(sketch, "E3235", {"start": v(-3.84, 5.97) * mm, "end": v(-3.85, 5.98) * mm});
            skLineSegment(sketch, "E3236", {"start": v(-3.85, 5.98) * mm, "end": v(-3.85, 6) * mm});
            skLineSegment(sketch, "E3237", {"start": v(-3.85, 6) * mm, "end": v(-3.86, 6) * mm});
            skLineSegment(sketch, "E3238", {"start": v(-3.86, 6) * mm, "end": v(-3.86, 6.02) * mm});
            skLineSegment(sketch, "E3239", {"start": v(-3.86, 6.02) * mm, "end": v(-3.86, 6.03) * mm});
            skLineSegment(sketch, "E3240", {"start": v(-3.86, 6.03) * mm, "end": v(-3.87, 6.05) * mm});
            skLineSegment(sketch, "E3241", {"start": v(-3.87, 6.05) * mm, "end": v(-3.87, 6.06) * mm});
            skLineSegment(sketch, "E3242", {"start": v(-3.87, 6.06) * mm, "end": v(-3.88, 6.08) * mm});
            skLineSegment(sketch, "E3243", {"start": v(-3.88, 6.08) * mm, "end": v(-3.88, 6.1) * mm});
            skLineSegment(sketch, "E3244", {"start": v(-3.88, 6.1) * mm, "end": v(-3.89, 6.11) * mm});
            skLineSegment(sketch, "E3245", {"start": v(-3.89, 6.11) * mm, "end": v(-3.9, 6.13) * mm});
            skLineSegment(sketch, "E3246", {"start": v(-3.9, 6.13) * mm, "end": v(-3.9, 6.15) * mm});
            skLineSegment(sketch, "E3247", {"start": v(-3.9, 6.15) * mm, "end": v(-3.9, 6.16) * mm});
            skLineSegment(sketch, "E3248", {"start": v(-3.9, 6.16) * mm, "end": v(-3.9, 6.18) * mm});
            skLineSegment(sketch, "E3249", {"start": v(-3.9, 6.18) * mm, "end": v(-3.91, 6.2) * mm});
            skLineSegment(sketch, "E3250", {"start": v(-3.91, 6.2) * mm, "end": v(-3.92, 6.22) * mm});
            skLineSegment(sketch, "E3251", {"start": v(-3.92, 6.22) * mm, "end": v(-3.92, 6.24) * mm});
            skLineSegment(sketch, "E3252", {"start": v(-3.92, 6.24) * mm, "end": v(-3.93, 6.26) * mm});
            skLineSegment(sketch, "E3253", {"start": v(-3.93, 6.26) * mm, "end": v(-3.93, 6.29) * mm});
            skLineSegment(sketch, "E3254", {"start": v(-3.93, 6.29) * mm, "end": v(-3.94, 6.3) * mm});
            skLineSegment(sketch, "E3255", {"start": v(-3.94, 6.3) * mm, "end": v(-3.94, 6.33) * mm});
            skLineSegment(sketch, "E3256", {"start": v(-3.94, 6.33) * mm, "end": v(-3.94, 6.35) * mm});
            skLineSegment(sketch, "E3257", {"start": v(-3.94, 6.35) * mm, "end": v(-3.95, 6.38) * mm});
            skLineSegment(sketch, "E3258", {"start": v(-3.95, 6.38) * mm, "end": v(-3.95, 6.4) * mm});
            skLineSegment(sketch, "E3259", {"start": v(-3.95, 6.4) * mm, "end": v(-3.96, 6.43) * mm});
            skLineSegment(sketch, "E3260", {"start": v(-3.96, 6.43) * mm, "end": v(-3.96, 6.45) * mm});
            skLineSegment(sketch, "E3261", {"start": v(-3.96, 6.45) * mm, "end": v(-3.96, 6.48) * mm});
            skLineSegment(sketch, "E3262", {"start": v(-3.96, 6.48) * mm, "end": v(-3.97, 6.5) * mm});
            skLineSegment(sketch, "E3263", {"start": v(-3.97, 6.5) * mm, "end": v(-3.97, 6.53) * mm});
            skLineSegment(sketch, "E3264", {"start": v(-3.97, 6.53) * mm, "end": v(-3.97, 6.56) * mm});
            skLineSegment(sketch, "E3265", {"start": v(-3.97, 6.56) * mm, "end": v(-3.98, 6.59) * mm});
            skLineSegment(sketch, "E3266", {"start": v(-3.98, 6.59) * mm, "end": v(-3.98, 6.62) * mm});
            skLineSegment(sketch, "E3267", {"start": v(-3.98, 6.62) * mm, "end": v(-3.98, 6.65) * mm});
            skLineSegment(sketch, "E3268", {"start": v(-3.98, 6.65) * mm, "end": v(-3.98, 6.68) * mm});
            skLineSegment(sketch, "E3269", {"start": v(-3.98, 6.68) * mm, "end": v(-3.99, 6.7) * mm});
            skLineSegment(sketch, "E3270", {"start": v(-3.99, 6.7) * mm, "end": v(-3.99, 6.74) * mm});
            skLineSegment(sketch, "E3271", {"start": v(-3.99, 6.74) * mm, "end": v(-3.99, 6.77) * mm});
            skLineSegment(sketch, "E3272", {"start": v(-3.99, 6.77) * mm, "end": v(-4, 6.8) * mm});
            skLineSegment(sketch, "E3273", {"start": v(-4, 6.8) * mm, "end": v(-4, 6.83) * mm});
            skLineSegment(sketch, "E3274", {"start": v(-4, 6.83) * mm, "end": v(-4, 6.87) * mm});
            skLineSegment(sketch, "E3275", {"start": v(-3.02, 6.36) * mm, "end": v(-3.03, 6.36) * mm});
            skLineSegment(sketch, "E3276", {"start": v(-3.03, 6.36) * mm, "end": v(-3.03, 6.36) * mm});
            skLineSegment(sketch, "E3277", {"start": v(-3.03, 6.36) * mm, "end": v(-3.04, 6.37) * mm});
            skLineSegment(sketch, "E3278", {"start": v(-3.04, 6.37) * mm, "end": v(-3.05, 6.37) * mm});
            skLineSegment(sketch, "E3279", {"start": v(-3.05, 6.37) * mm, "end": v(-3.06, 6.38) * mm});
            skLineSegment(sketch, "E3280", {"start": v(-3.06, 6.38) * mm, "end": v(-3.07, 6.39) * mm});
            skLineSegment(sketch, "E3281", {"start": v(-3.07, 6.39) * mm, "end": v(-3.08, 6.4) * mm});
            skLineSegment(sketch, "E3282", {"start": v(-3.08, 6.4) * mm, "end": v(-3.08, 6.4) * mm});
            skLineSegment(sketch, "E3283", {"start": v(-3.08, 6.4) * mm, "end": v(-3.1, 6.42) * mm});
            skLineSegment(sketch, "E3284", {"start": v(-3.1, 6.42) * mm, "end": v(-3.1, 6.43) * mm});
            skLineSegment(sketch, "E3285", {"start": v(-3.1, 6.43) * mm, "end": v(-3.1, 6.44) * mm});
            skLineSegment(sketch, "E3286", {"start": v(-3.1, 6.44) * mm, "end": v(-3.12, 6.45) * mm});
            skLineSegment(sketch, "E3287", {"start": v(-3.12, 6.45) * mm, "end": v(-3.13, 6.46) * mm});
            skLineSegment(sketch, "E3288", {"start": v(-3.13, 6.46) * mm, "end": v(-3.14, 6.47) * mm});
            skLineSegment(sketch, "E3289", {"start": v(-3.14, 6.47) * mm, "end": v(-3.15, 6.49) * mm});
            skLineSegment(sketch, "E3290", {"start": v(-3.15, 6.49) * mm, "end": v(-3.16, 6.5) * mm});
            skLineSegment(sketch, "E3291", {"start": v(-3.16, 6.5) * mm, "end": v(-3.17, 6.51) * mm});
            skLineSegment(sketch, "E3292", {"start": v(-3.17, 6.51) * mm, "end": v(-3.18, 6.52) * mm});
            skLineSegment(sketch, "E3293", {"start": v(-3.18, 6.52) * mm, "end": v(-3.2, 6.54) * mm});
            skLineSegment(sketch, "E3294", {"start": v(-3.2, 6.54) * mm, "end": v(-3.21, 6.55) * mm});
            skLineSegment(sketch, "E3295", {"start": v(-3.21, 6.55) * mm, "end": v(-3.22, 6.57) * mm});
            skLineSegment(sketch, "E3296", {"start": v(-3.22, 6.57) * mm, "end": v(-3.24, 6.58) * mm});
            skLineSegment(sketch, "E3297", {"start": v(-3.24, 6.58) * mm, "end": v(-3.25, 6.6) * mm});
            skLineSegment(sketch, "E3298", {"start": v(-3.25, 6.6) * mm, "end": v(-3.27, 6.6) * mm});
            skLineSegment(sketch, "E3299", {"start": v(-3.27, 6.6) * mm, "end": v(-3.28, 6.62) * mm});
            skLineSegment(sketch, "E3300", {"start": v(-3.28, 6.62) * mm, "end": v(-3.3, 6.64) * mm});
            skLineSegment(sketch, "E3301", {"start": v(-3.3, 6.64) * mm, "end": v(-3.32, 6.65) * mm});
            skLineSegment(sketch, "E3302", {"start": v(-3.32, 6.65) * mm, "end": v(-3.33, 6.67) * mm});
            skLineSegment(sketch, "E3303", {"start": v(-3.33, 6.67) * mm, "end": v(-3.35, 6.69) * mm});
            skLineSegment(sketch, "E3304", {"start": v(-3.35, 6.69) * mm, "end": v(-3.37, 6.7) * mm});
            skLineSegment(sketch, "E3305", {"start": v(-3.37, 6.7) * mm, "end": v(-3.39, 6.72) * mm});
            skLineSegment(sketch, "E3306", {"start": v(-3.39, 6.72) * mm, "end": v(-3.4, 6.73) * mm});
            skLineSegment(sketch, "E3307", {"start": v(-3.4, 6.73) * mm, "end": v(-3.43, 6.75) * mm});
            skLineSegment(sketch, "E3308", {"start": v(-3.43, 6.75) * mm, "end": v(-3.45, 6.77) * mm});
            skLineSegment(sketch, "E3309", {"start": v(-3.45, 6.77) * mm, "end": v(-3.47, 6.79) * mm});
            skLineSegment(sketch, "E3310", {"start": v(-3.47, 6.79) * mm, "end": v(-3.49, 6.8) * mm});
            skLineSegment(sketch, "E3311", {"start": v(-3.49, 6.8) * mm, "end": v(-3.51, 6.82) * mm});
            skLineSegment(sketch, "E3312", {"start": v(-3.51, 6.82) * mm, "end": v(-3.53, 6.84) * mm});
            skLineSegment(sketch, "E3313", {"start": v(-3.53, 6.84) * mm, "end": v(-3.56, 6.85) * mm});
            skLineSegment(sketch, "E3314", {"start": v(-3.56, 6.85) * mm, "end": v(-3.58, 6.87) * mm});
            skLineSegment(sketch, "E3315", {"start": v(-3.58, 6.87) * mm, "end": v(-3.6, 6.89) * mm});
            skLineSegment(sketch, "E3316", {"start": v(-3.6, 6.89) * mm, "end": v(-3.63, 6.9) * mm});
            skLineSegment(sketch, "E3317", {"start": v(-3.63, 6.9) * mm, "end": v(-3.66, 6.92) * mm});
            skLineSegment(sketch, "E3318", {"start": v(-3.66, 6.92) * mm, "end": v(-3.68, 6.94) * mm});
            skLineSegment(sketch, "E3319", {"start": v(-3.68, 6.94) * mm, "end": v(-3.7, 6.96) * mm});
            skLineSegment(sketch, "E3320", {"start": v(-3.7, 6.96) * mm, "end": v(-3.73, 6.98) * mm});
            skLineSegment(sketch, "E3321", {"start": v(-3.73, 6.98) * mm, "end": v(-3.76, 7) * mm});
            skArc(sketch, "E3322", {"start": v(-3.76, 7) * mm, "mid": v(-3.88, 6.93) * mm, "end": v(-4, 6.87) * mm});
            skLineSegment(sketch, "E3323", {"start": v(-2.79, 6.47) * mm, "end": v(-2.78, 6.47) * mm});
            skLineSegment(sketch, "E3324", {"start": v(-2.78, 6.47) * mm, "end": v(-2.78, 6.48) * mm});
            skLineSegment(sketch, "E3325", {"start": v(-2.78, 6.48) * mm, "end": v(-2.78, 6.48) * mm});
            skLineSegment(sketch, "E3326", {"start": v(-2.78, 6.48) * mm, "end": v(-2.78, 6.5) * mm});
            skLineSegment(sketch, "E3327", {"start": v(-2.78, 6.5) * mm, "end": v(-2.77, 6.5) * mm});
            skLineSegment(sketch, "E3328", {"start": v(-2.77, 6.5) * mm, "end": v(-2.78, 6.52) * mm});
            skLineSegment(sketch, "E3329", {"start": v(-2.78, 6.52) * mm, "end": v(-2.78, 6.54) * mm});
            skLineSegment(sketch, "E3330", {"start": v(-2.78, 6.54) * mm, "end": v(-2.78, 6.54) * mm});
            skLineSegment(sketch, "E3331", {"start": v(-2.78, 6.54) * mm, "end": v(-2.78, 6.56) * mm});
            skLineSegment(sketch, "E3332", {"start": v(-2.78, 6.56) * mm, "end": v(-2.78, 6.57) * mm});
            skLineSegment(sketch, "E3333", {"start": v(-2.78, 6.57) * mm, "end": v(-2.79, 6.58) * mm});
            skLineSegment(sketch, "E3334", {"start": v(-2.79, 6.58) * mm, "end": v(-2.79, 6.6) * mm});
            skLineSegment(sketch, "E3335", {"start": v(-2.79, 6.6) * mm, "end": v(-2.8, 6.61) * mm});
            skLineSegment(sketch, "E3336", {"start": v(-2.8, 6.61) * mm, "end": v(-2.8, 6.63) * mm});
            skLineSegment(sketch, "E3337", {"start": v(-2.8, 6.63) * mm, "end": v(-2.8, 6.65) * mm});
            skLineSegment(sketch, "E3338", {"start": v(-2.8, 6.65) * mm, "end": v(-2.8, 6.66) * mm});
            skLineSegment(sketch, "E3339", {"start": v(-2.8, 6.66) * mm, "end": v(-2.8, 6.68) * mm});
            skLineSegment(sketch, "E3340", {"start": v(-2.8, 6.68) * mm, "end": v(-2.8, 6.7) * mm});
            skLineSegment(sketch, "E3341", {"start": v(-2.8, 6.7) * mm, "end": v(-2.8, 6.72) * mm});
            skLineSegment(sketch, "E3342", {"start": v(-2.8, 6.72) * mm, "end": v(-2.8, 6.73) * mm});
            skLineSegment(sketch, "E3343", {"start": v(-2.8, 6.73) * mm, "end": v(-2.8, 6.75) * mm});
            skLineSegment(sketch, "E3344", {"start": v(-2.8, 6.75) * mm, "end": v(-2.8, 6.77) * mm});
            skLineSegment(sketch, "E3345", {"start": v(-2.8, 6.77) * mm, "end": v(-2.8, 6.8) * mm});
            skLineSegment(sketch, "E3346", {"start": v(-2.8, 6.8) * mm, "end": v(-2.8, 6.82) * mm});
            skLineSegment(sketch, "E3347", {"start": v(-2.8, 6.82) * mm, "end": v(-2.81, 6.84) * mm});
            skLineSegment(sketch, "E3348", {"start": v(-2.81, 6.84) * mm, "end": v(-2.81, 6.86) * mm});
            skLineSegment(sketch, "E3349", {"start": v(-2.81, 6.86) * mm, "end": v(-2.81, 6.88) * mm});
            skLineSegment(sketch, "E3350", {"start": v(-2.81, 6.88) * mm, "end": v(-2.81, 6.9) * mm});
            skLineSegment(sketch, "E3351", {"start": v(-2.81, 6.9) * mm, "end": v(-2.81, 6.93) * mm});
            skLineSegment(sketch, "E3352", {"start": v(-2.81, 6.93) * mm, "end": v(-2.81, 6.95) * mm});
            skLineSegment(sketch, "E3353", {"start": v(-2.81, 6.95) * mm, "end": v(-2.81, 6.98) * mm});
            skLineSegment(sketch, "E3354", {"start": v(-2.81, 6.98) * mm, "end": v(-2.81, 7) * mm});
            skLineSegment(sketch, "E3355", {"start": v(-2.81, 7) * mm, "end": v(-2.81, 7.03) * mm});
            skLineSegment(sketch, "E3356", {"start": v(-2.81, 7.03) * mm, "end": v(-2.81, 7.06) * mm});
            skLineSegment(sketch, "E3357", {"start": v(-2.81, 7.06) * mm, "end": v(-2.8, 7.08) * mm});
            skLineSegment(sketch, "E3358", {"start": v(-2.8, 7.08) * mm, "end": v(-2.8, 7.11) * mm});
            skLineSegment(sketch, "E3359", {"start": v(-2.8, 7.11) * mm, "end": v(-2.8, 7.14) * mm});
            skLineSegment(sketch, "E3360", {"start": v(-2.8, 7.14) * mm, "end": v(-2.8, 7.17) * mm});
            skLineSegment(sketch, "E3361", {"start": v(-2.8, 7.17) * mm, "end": v(-2.8, 7.2) * mm});
            skLineSegment(sketch, "E3362", {"start": v(-2.8, 7.2) * mm, "end": v(-2.8, 7.22) * mm});
            skLineSegment(sketch, "E3363", {"start": v(-2.8, 7.22) * mm, "end": v(-2.8, 7.25) * mm});
            skLineSegment(sketch, "E3364", {"start": v(-2.8, 7.25) * mm, "end": v(-2.8, 7.28) * mm});
            skLineSegment(sketch, "E3365", {"start": v(-2.8, 7.28) * mm, "end": v(-2.8, 7.32) * mm});
            skLineSegment(sketch, "E3366", {"start": v(-2.8, 7.32) * mm, "end": v(-2.79, 7.35) * mm});
            skLineSegment(sketch, "E3367", {"start": v(-2.79, 7.35) * mm, "end": v(-2.78, 7.38) * mm});
            skLineSegment(sketch, "E3368", {"start": v(-2.78, 7.38) * mm, "end": v(-2.78, 7.41) * mm});
            skLineSegment(sketch, "E3369", {"start": v(-2.78, 7.41) * mm, "end": v(-2.77, 7.44) * mm});
            skLineSegment(sketch, "E3370", {"start": v(-1.9, 6.78) * mm, "end": v(-1.9, 6.78) * mm});
            skLineSegment(sketch, "E3371", {"start": v(-1.9, 6.78) * mm, "end": v(-1.91, 6.78) * mm});
            skLineSegment(sketch, "E3372", {"start": v(-1.91, 6.78) * mm, "end": v(-1.92, 6.79) * mm});
            skLineSegment(sketch, "E3373", {"start": v(-1.92, 6.79) * mm, "end": v(-1.93, 6.8) * mm});
            skLineSegment(sketch, "E3374", {"start": v(-1.93, 6.8) * mm, "end": v(-1.93, 6.8) * mm});
            skLineSegment(sketch, "E3375", {"start": v(-1.93, 6.8) * mm, "end": v(-1.94, 6.81) * mm});
            skLineSegment(sketch, "E3376", {"start": v(-1.94, 6.81) * mm, "end": v(-1.95, 6.83) * mm});
            skLineSegment(sketch, "E3377", {"start": v(-1.95, 6.83) * mm, "end": v(-1.95, 6.83) * mm});
            skLineSegment(sketch, "E3378", {"start": v(-1.95, 6.83) * mm, "end": v(-1.96, 6.85) * mm});
            skLineSegment(sketch, "E3379", {"start": v(-1.96, 6.85) * mm, "end": v(-1.97, 6.86) * mm});
            skLineSegment(sketch, "E3380", {"start": v(-1.97, 6.86) * mm, "end": v(-1.97, 6.87) * mm});
            skLineSegment(sketch, "E3381", {"start": v(-1.97, 6.87) * mm, "end": v(-1.98, 6.88) * mm});
            skLineSegment(sketch, "E3382", {"start": v(-1.98, 6.88) * mm, "end": v(-1.99, 6.9) * mm});
            skLineSegment(sketch, "E3383", {"start": v(-1.99, 6.9) * mm, "end": v(-2, 6.9) * mm});
            skLineSegment(sketch, "E3384", {"start": v(-2, 6.9) * mm, "end": v(-2, 6.92) * mm});
            skLineSegment(sketch, "E3385", {"start": v(-2, 6.92) * mm, "end": v(-2.02, 6.94) * mm});
            skLineSegment(sketch, "E3386", {"start": v(-2.02, 6.94) * mm, "end": v(-2.02, 6.95) * mm});
            skLineSegment(sketch, "E3387", {"start": v(-2.02, 6.95) * mm, "end": v(-2.03, 6.97) * mm});
            skLineSegment(sketch, "E3388", {"start": v(-2.03, 6.97) * mm, "end": v(-2.04, 6.98) * mm});
            skLineSegment(sketch, "E3389", {"start": v(-2.04, 6.98) * mm, "end": v(-2.06, 7) * mm});
            skLineSegment(sketch, "E3390", {"start": v(-2.06, 7) * mm, "end": v(-2.07, 7.02) * mm});
            skLineSegment(sketch, "E3391", {"start": v(-2.07, 7.02) * mm, "end": v(-2.08, 7.03) * mm});
            skLineSegment(sketch, "E3392", {"start": v(-2.08, 7.03) * mm, "end": v(-2.09, 7.05) * mm});
            skLineSegment(sketch, "E3393", {"start": v(-2.09, 7.05) * mm, "end": v(-2.1, 7.07) * mm});
            skLineSegment(sketch, "E3394", {"start": v(-2.1, 7.07) * mm, "end": v(-2.11, 7.08) * mm});
            skLineSegment(sketch, "E3395", {"start": v(-2.11, 7.08) * mm, "end": v(-2.13, 7.1) * mm});
            skLineSegment(sketch, "E3396", {"start": v(-2.13, 7.1) * mm, "end": v(-2.14, 7.12) * mm});
            skLineSegment(sketch, "E3397", {"start": v(-2.14, 7.12) * mm, "end": v(-2.16, 7.14) * mm});
            skLineSegment(sketch, "E3398", {"start": v(-2.16, 7.14) * mm, "end": v(-2.17, 7.16) * mm});
            skLineSegment(sketch, "E3399", {"start": v(-2.17, 7.16) * mm, "end": v(-2.19, 7.18) * mm});
            skLineSegment(sketch, "E3400", {"start": v(-2.19, 7.18) * mm, "end": v(-2.2, 7.2) * mm});
            skLineSegment(sketch, "E3401", {"start": v(-2.2, 7.2) * mm, "end": v(-2.22, 7.21) * mm});
            skLineSegment(sketch, "E3402", {"start": v(-2.22, 7.21) * mm, "end": v(-2.23, 7.23) * mm});
            skLineSegment(sketch, "E3403", {"start": v(-2.23, 7.23) * mm, "end": v(-2.25, 7.25) * mm});
            skLineSegment(sketch, "E3404", {"start": v(-2.25, 7.25) * mm, "end": v(-2.27, 7.27) * mm});
            skLineSegment(sketch, "E3405", {"start": v(-2.27, 7.27) * mm, "end": v(-2.29, 7.3) * mm});
            skLineSegment(sketch, "E3406", {"start": v(-2.29, 7.3) * mm, "end": v(-2.3, 7.31) * mm});
            skLineSegment(sketch, "E3407", {"start": v(-2.3, 7.31) * mm, "end": v(-2.33, 7.34) * mm});
            skLineSegment(sketch, "E3408", {"start": v(-2.33, 7.34) * mm, "end": v(-2.35, 7.36) * mm});
            skLineSegment(sketch, "E3409", {"start": v(-2.35, 7.36) * mm, "end": v(-2.37, 7.38) * mm});
            skLineSegment(sketch, "E3410", {"start": v(-2.37, 7.38) * mm, "end": v(-2.39, 7.4) * mm});
            skLineSegment(sketch, "E3411", {"start": v(-2.39, 7.4) * mm, "end": v(-2.4, 7.42) * mm});
            skLineSegment(sketch, "E3412", {"start": v(-2.4, 7.42) * mm, "end": v(-2.43, 7.44) * mm});
            skLineSegment(sketch, "E3413", {"start": v(-2.43, 7.44) * mm, "end": v(-2.45, 7.46) * mm});
            skLineSegment(sketch, "E3414", {"start": v(-2.45, 7.46) * mm, "end": v(-2.48, 7.49) * mm});
            skLineSegment(sketch, "E3415", {"start": v(-2.48, 7.49) * mm, "end": v(-2.5, 7.5) * mm});
            skLineSegment(sketch, "E3416", {"start": v(-2.5, 7.5) * mm, "end": v(-2.52, 7.53) * mm});
            skArc(sketch, "E3417", {"start": v(-2.52, 7.53) * mm, "mid": v(-2.65, 7.49) * mm, "end": v(-2.77, 7.44) * mm});
            skLineSegment(sketch, "E3418", {"start": v(-1.65, 6.85) * mm, "end": v(-1.65, 6.85) * mm});
            skLineSegment(sketch, "E3419", {"start": v(-1.65, 6.85) * mm, "end": v(-1.64, 6.85) * mm});
            skLineSegment(sketch, "E3420", {"start": v(-1.64, 6.85) * mm, "end": v(-1.64, 6.86) * mm});
            skLineSegment(sketch, "E3421", {"start": v(-1.64, 6.86) * mm, "end": v(-1.64, 6.87) * mm});
            skLineSegment(sketch, "E3422", {"start": v(-1.64, 6.87) * mm, "end": v(-1.63, 6.88) * mm});
            skLineSegment(sketch, "E3423", {"start": v(-1.63, 6.88) * mm, "end": v(-1.63, 6.9) * mm});
            skLineSegment(sketch, "E3424", {"start": v(-1.63, 6.9) * mm, "end": v(-1.63, 6.91) * mm});
            skLineSegment(sketch, "E3425", {"start": v(-1.63, 6.91) * mm, "end": v(-1.63, 6.92) * mm});
            skLineSegment(sketch, "E3426", {"start": v(-1.63, 6.92) * mm, "end": v(-1.63, 6.93) * mm});
            skLineSegment(sketch, "E3427", {"start": v(-1.63, 6.93) * mm, "end": v(-1.63, 6.94) * mm});
            skLineSegment(sketch, "E3428", {"start": v(-1.63, 6.94) * mm, "end": v(-1.63, 6.96) * mm});
            skLineSegment(sketch, "E3429", {"start": v(-1.63, 6.96) * mm, "end": v(-1.63, 6.97) * mm});
            skLineSegment(sketch, "E3430", {"start": v(-1.63, 6.97) * mm, "end": v(-1.63, 6.99) * mm});
            skLineSegment(sketch, "E3431", {"start": v(-1.63, 6.99) * mm, "end": v(-1.63, 7) * mm});
            skLineSegment(sketch, "E3432", {"start": v(-1.63, 7) * mm, "end": v(-1.63, 7.02) * mm});
            skLineSegment(sketch, "E3433", {"start": v(-1.63, 7.02) * mm, "end": v(-1.63, 7.04) * mm});
            skLineSegment(sketch, "E3434", {"start": v(-1.63, 7.04) * mm, "end": v(-1.63, 7.06) * mm});
            skLineSegment(sketch, "E3435", {"start": v(-1.63, 7.06) * mm, "end": v(-1.63, 7.07) * mm});
            skLineSegment(sketch, "E3436", {"start": v(-1.63, 7.07) * mm, "end": v(-1.63, 7.1) * mm});
            skLineSegment(sketch, "E3437", {"start": v(-1.63, 7.1) * mm, "end": v(-1.62, 7.11) * mm});
            skLineSegment(sketch, "E3438", {"start": v(-1.62, 7.11) * mm, "end": v(-1.62, 7.13) * mm});
            skLineSegment(sketch, "E3439", {"start": v(-1.62, 7.13) * mm, "end": v(-1.62, 7.15) * mm});
            skLineSegment(sketch, "E3440", {"start": v(-1.62, 7.15) * mm, "end": v(-1.62, 7.17) * mm});
            skLineSegment(sketch, "E3441", {"start": v(-1.62, 7.17) * mm, "end": v(-1.62, 7.2) * mm});
            skLineSegment(sketch, "E3442", {"start": v(-1.62, 7.2) * mm, "end": v(-1.61, 7.21) * mm});
            skLineSegment(sketch, "E3443", {"start": v(-1.61, 7.21) * mm, "end": v(-1.6, 7.24) * mm});
            skLineSegment(sketch, "E3444", {"start": v(-1.6, 7.24) * mm, "end": v(-1.6, 7.26) * mm});
            skLineSegment(sketch, "E3445", {"start": v(-1.6, 7.26) * mm, "end": v(-1.6, 7.28) * mm});
            skLineSegment(sketch, "E3446", {"start": v(-1.6, 7.28) * mm, "end": v(-1.6, 7.3) * mm});
            skLineSegment(sketch, "E3447", {"start": v(-1.6, 7.3) * mm, "end": v(-1.6, 7.33) * mm});
            skLineSegment(sketch, "E3448", {"start": v(-1.6, 7.33) * mm, "end": v(-1.6, 7.35) * mm});
            skLineSegment(sketch, "E3449", {"start": v(-1.6, 7.35) * mm, "end": v(-1.59, 7.38) * mm});
            skLineSegment(sketch, "E3450", {"start": v(-1.59, 7.38) * mm, "end": v(-1.58, 7.4) * mm});
            skLineSegment(sketch, "E3451", {"start": v(-1.58, 7.4) * mm, "end": v(-1.58, 7.43) * mm});
            skLineSegment(sketch, "E3452", {"start": v(-1.58, 7.43) * mm, "end": v(-1.57, 7.46) * mm});
            skLineSegment(sketch, "E3453", {"start": v(-1.57, 7.46) * mm, "end": v(-1.56, 7.48) * mm});
            skLineSegment(sketch, "E3454", {"start": v(-1.56, 7.48) * mm, "end": v(-1.56, 7.5) * mm});
            skLineSegment(sketch, "E3455", {"start": v(-1.56, 7.5) * mm, "end": v(-1.55, 7.54) * mm});
            skLineSegment(sketch, "E3456", {"start": v(-1.55, 7.54) * mm, "end": v(-1.54, 7.57) * mm});
            skLineSegment(sketch, "E3457", {"start": v(-1.54, 7.57) * mm, "end": v(-1.54, 7.6) * mm});
            skLineSegment(sketch, "E3458", {"start": v(-1.54, 7.6) * mm, "end": v(-1.53, 7.62) * mm});
            skLineSegment(sketch, "E3459", {"start": v(-1.53, 7.62) * mm, "end": v(-1.52, 7.65) * mm});
            skLineSegment(sketch, "E3460", {"start": v(-1.52, 7.65) * mm, "end": v(-1.51, 7.68) * mm});
            skLineSegment(sketch, "E3461", {"start": v(-1.51, 7.68) * mm, "end": v(-1.5, 7.71) * mm});
            skLineSegment(sketch, "E3462", {"start": v(-1.5, 7.71) * mm, "end": v(-1.5, 7.74) * mm});
            skLineSegment(sketch, "E3463", {"start": v(-1.5, 7.74) * mm, "end": v(-1.48, 7.77) * mm});
            skLineSegment(sketch, "E3464", {"start": v(-1.48, 7.77) * mm, "end": v(-1.47, 7.8) * mm});
            skLineSegment(sketch, "E3465", {"start": v(-0.72, 7) * mm, "end": v(-0.73, 7) * mm});
            skLineSegment(sketch, "E3466", {"start": v(-0.73, 7) * mm, "end": v(-0.74, 7) * mm});
            skLineSegment(sketch, "E3467", {"start": v(-0.74, 7) * mm, "end": v(-0.74, 7.01) * mm});
            skLineSegment(sketch, "E3468", {"start": v(-0.74, 7.01) * mm, "end": v(-0.75, 7.02) * mm});
            skLineSegment(sketch, "E3469", {"start": v(-0.75, 7.02) * mm, "end": v(-0.76, 7.03) * mm});
            skLineSegment(sketch, "E3470", {"start": v(-0.76, 7.03) * mm, "end": v(-0.76, 7.04) * mm});
            skLineSegment(sketch, "E3471", {"start": v(-0.76, 7.04) * mm, "end": v(-0.77, 7.06) * mm});
            skLineSegment(sketch, "E3472", {"start": v(-0.77, 7.06) * mm, "end": v(-0.77, 7.07) * mm});
            skLineSegment(sketch, "E3473", {"start": v(-0.77, 7.07) * mm, "end": v(-0.77, 7.08) * mm});
            skLineSegment(sketch, "E3474", {"start": v(-0.77, 7.08) * mm, "end": v(-0.78, 7.1) * mm});
            skLineSegment(sketch, "E3475", {"start": v(-0.78, 7.1) * mm, "end": v(-0.78, 7.1) * mm});
            skLineSegment(sketch, "E3476", {"start": v(-0.78, 7.1) * mm, "end": v(-0.79, 7.12) * mm});
            skLineSegment(sketch, "E3477", {"start": v(-0.79, 7.12) * mm, "end": v(-0.8, 7.13) * mm});
            skLineSegment(sketch, "E3478", {"start": v(-0.8, 7.13) * mm, "end": v(-0.8, 7.15) * mm});
            skLineSegment(sketch, "E3479", {"start": v(-0.8, 7.15) * mm, "end": v(-0.8, 7.16) * mm});
            skLineSegment(sketch, "E3480", {"start": v(-0.8, 7.16) * mm, "end": v(-0.81, 7.18) * mm});
            skLineSegment(sketch, "E3481", {"start": v(-0.81, 7.18) * mm, "end": v(-0.82, 7.2) * mm});
            skLineSegment(sketch, "E3482", {"start": v(-0.82, 7.2) * mm, "end": v(-0.83, 7.21) * mm});
            skLineSegment(sketch, "E3483", {"start": v(-0.83, 7.21) * mm, "end": v(-0.83, 7.23) * mm});
            skLineSegment(sketch, "E3484", {"start": v(-0.83, 7.23) * mm, "end": v(-0.84, 7.25) * mm});
            skLineSegment(sketch, "E3485", {"start": v(-0.84, 7.25) * mm, "end": v(-0.85, 7.26) * mm});
            skLineSegment(sketch, "E3486", {"start": v(-0.85, 7.26) * mm, "end": v(-0.86, 7.28) * mm});
            skLineSegment(sketch, "E3487", {"start": v(-0.86, 7.28) * mm, "end": v(-0.87, 7.3) * mm});
            skLineSegment(sketch, "E3488", {"start": v(-0.87, 7.3) * mm, "end": v(-0.88, 7.32) * mm});
            skLineSegment(sketch, "E3489", {"start": v(-0.88, 7.32) * mm, "end": v(-0.89, 7.34) * mm});
            skLineSegment(sketch, "E3490", {"start": v(-0.89, 7.34) * mm, "end": v(-0.9, 7.36) * mm});
            skLineSegment(sketch, "E3491", {"start": v(-0.9, 7.36) * mm, "end": v(-0.9, 7.38) * mm});
            skLineSegment(sketch, "E3492", {"start": v(-0.9, 7.38) * mm, "end": v(-0.92, 7.4) * mm});
            skLineSegment(sketch, "E3493", {"start": v(-0.92, 7.4) * mm, "end": v(-0.93, 7.42) * mm});
            skLineSegment(sketch, "E3494", {"start": v(-0.93, 7.42) * mm, "end": v(-0.94, 7.44) * mm});
            skLineSegment(sketch, "E3495", {"start": v(-0.94, 7.44) * mm, "end": v(-0.95, 7.46) * mm});
            skLineSegment(sketch, "E3496", {"start": v(-0.95, 7.46) * mm, "end": v(-0.97, 7.48) * mm});
            skLineSegment(sketch, "E3497", {"start": v(-0.97, 7.48) * mm, "end": v(-0.98, 7.5) * mm});
            skLineSegment(sketch, "E3498", {"start": v(-0.98, 7.5) * mm, "end": v(-1, 7.53) * mm});
            skLineSegment(sketch, "E3499", {"start": v(-1, 7.53) * mm, "end": v(-1, 7.55) * mm});
            skLineSegment(sketch, "E3500", {"start": v(-1, 7.55) * mm, "end": v(-1.02, 7.58) * mm});
            skLineSegment(sketch, "E3501", {"start": v(-1.02, 7.58) * mm, "end": v(-1.04, 7.6) * mm});
            skLineSegment(sketch, "E3502", {"start": v(-1.04, 7.6) * mm, "end": v(-1.05, 7.62) * mm});
            skLineSegment(sketch, "E3503", {"start": v(-1.05, 7.62) * mm, "end": v(-1.07, 7.65) * mm});
            skLineSegment(sketch, "E3504", {"start": v(-1.07, 7.65) * mm, "end": v(-1.08, 7.67) * mm});
            skLineSegment(sketch, "E3505", {"start": v(-1.08, 7.67) * mm, "end": v(-1.1, 7.7) * mm});
            skLineSegment(sketch, "E3506", {"start": v(-1.1, 7.7) * mm, "end": v(-1.12, 7.72) * mm});
            skLineSegment(sketch, "E3507", {"start": v(-1.12, 7.72) * mm, "end": v(-1.14, 7.75) * mm});
            skLineSegment(sketch, "E3508", {"start": v(-1.14, 7.75) * mm, "end": v(-1.15, 7.77) * mm});
            skLineSegment(sketch, "E3509", {"start": v(-1.15, 7.77) * mm, "end": v(-1.17, 7.8) * mm});
            skLineSegment(sketch, "E3510", {"start": v(-1.17, 7.8) * mm, "end": v(-1.2, 7.82) * mm});
            skLineSegment(sketch, "E3511", {"start": v(-1.2, 7.82) * mm, "end": v(-1.21, 7.85) * mm});
            skArc(sketch, "E3512", {"start": v(-1.21, 7.85) * mm, "mid": v(-1.34, 7.83) * mm, "end": v(-1.47, 7.8) * mm});
            skArc(sketch, "E3513", {"start": v(0.72, 7) * mm, "mid": v(0.6, 7.02) * mm, "end": v(0.47, 7.03) * mm});
            skArc(sketch, "E3514", {"start": v(1.9, 6.78) * mm, "mid": v(1.78, 6.82) * mm, "end": v(1.65, 6.85) * mm});
            skArc(sketch, "E3515", {"start": v(3.02, 6.36) * mm, "mid": v(2.9, 6.42) * mm, "end": v(2.79, 6.47) * mm});
            skArc(sketch, "E3516", {"start": v(4.05, 5.76) * mm, "mid": v(3.95, 5.83) * mm, "end": v(3.84, 5.9) * mm});
            skArc(sketch, "E3517", {"start": v(4.97, 5) * mm, "mid": v(4.88, 5.08) * mm, "end": v(4.79, 5.17) * mm});
            skArc(sketch, "E3518", {"start": v(5.74, 4.08) * mm, "mid": v(5.67, 4.18) * mm, "end": v(5.6, 4.28) * mm});
            skArc(sketch, "E3519", {"start": v(6.35, 3.05) * mm, "mid": v(6.3, 3.17) * mm, "end": v(6.24, 3.28) * mm});
            skArc(sketch, "E3520", {"start": v(6.78, 1.93) * mm, "mid": v(6.74, 2.06) * mm, "end": v(6.7, 2.18) * mm});
            skArc(sketch, "E3521", {"start": v(7, 0.76) * mm, "mid": v(7, 0.89) * mm, "end": v(6.98, 1.01) * mm});
            skArc(sketch, "E3522", {"start": v(7.04, -0.43) * mm, "mid": v(7.05, -0.3) * mm, "end": v(7.05, -0.18) * mm});
            skArc(sketch, "E3523", {"start": v(6.87, -1.62) * mm, "mid": v(6.9, -1.5) * mm, "end": v(6.92, -1.37) * mm});
            skArc(sketch, "E3524", {"start": v(6.5, -2.76) * mm, "mid": v(6.54, -2.64) * mm, "end": v(6.59, -2.52) * mm});
            skArc(sketch, "E3525", {"start": v(5.94, -3.81) * mm, "mid": v(6, -3.7) * mm, "end": v(6.07, -3.6) * mm});
            skArc(sketch, "E3526", {"start": v(5.2, -4.76) * mm, "mid": v(5.3, -4.67) * mm, "end": v(5.38, -4.57) * mm});
            skArc(sketch, "E3527", {"start": v(4.33, -5.57) * mm, "mid": v(4.43, -5.5) * mm, "end": v(4.53, -5.42) * mm});
            skArc(sketch, "E3528", {"start": v(3.33, -6.23) * mm, "mid": v(3.44, -6.17) * mm, "end": v(3.55, -6.1) * mm});
            skArc(sketch, "E3529", {"start": v(2.23, -6.7) * mm, "mid": v(2.35, -6.66) * mm, "end": v(2.47, -6.62) * mm});
            skArc(sketch, "E3530", {"start": v(1.07, -6.98) * mm, "mid": v(1.2, -6.96) * mm, "end": v(1.32, -6.94) * mm});
            skArc(sketch, "E3531", {"start": v(-0.13, -7.06) * mm, "mid": v(0, -7.06) * mm, "end": v(0.13, -7.06) * mm});
            skArc(sketch, "E3532", {"start": v(-1.32, -6.94) * mm, "mid": v(-1.2, -6.96) * mm, "end": v(-1.07, -6.98) * mm});
            skArc(sketch, "E3533", {"start": v(-2.47, -6.62) * mm, "mid": v(-2.35, -6.66) * mm, "end": v(-2.23, -6.7) * mm});
            skArc(sketch, "E3534", {"start": v(-3.55, -6.1) * mm, "mid": v(-3.44, -6.17) * mm, "end": v(-3.33, -6.23) * mm});
            skArc(sketch, "E3535", {"start": v(-4.53, -5.42) * mm, "mid": v(-4.43, -5.5) * mm, "end": v(-4.33, -5.57) * mm});
            skArc(sketch, "E3536", {"start": v(-5.38, -4.57) * mm, "mid": v(-5.3, -4.67) * mm, "end": v(-5.2, -4.76) * mm});
            skArc(sketch, "E3537", {"start": v(-6.07, -3.6) * mm, "mid": v(-6, -3.7) * mm, "end": v(-5.94, -3.81) * mm});
            skArc(sketch, "E3538", {"start": v(-6.59, -2.52) * mm, "mid": v(-6.54, -2.64) * mm, "end": v(-6.5, -2.76) * mm});
            skArc(sketch, "E3539", {"start": v(-6.92, -1.37) * mm, "mid": v(-6.9, -1.5) * mm, "end": v(-6.87, -1.62) * mm});
            skArc(sketch, "E3540", {"start": v(-7.05, -0.18) * mm, "mid": v(-7.05, -0.3) * mm, "end": v(-7.04, -0.43) * mm});
            skArc(sketch, "E3541", {"start": v(-6.98, 1.01) * mm, "mid": v(-7, 0.89) * mm, "end": v(-7, 0.76) * mm});
            skArc(sketch, "E3542", {"start": v(-6.7, 2.18) * mm, "mid": v(-6.74, 2.06) * mm, "end": v(-6.78, 1.93) * mm});
            skArc(sketch, "E3543", {"start": v(-6.24, 3.28) * mm, "mid": v(-6.3, 3.17) * mm, "end": v(-6.35, 3.05) * mm});
            skArc(sketch, "E3544", {"start": v(-5.6, 4.28) * mm, "mid": v(-5.67, 4.18) * mm, "end": v(-5.74, 4.08) * mm});
            skArc(sketch, "E3545", {"start": v(-4.79, 5.17) * mm, "mid": v(-4.88, 5.08) * mm, "end": v(-4.97, 5) * mm});
            skArc(sketch, "E3546", {"start": v(-3.84, 5.9) * mm, "mid": v(-3.95, 5.83) * mm, "end": v(-4.05, 5.76) * mm});
            skArc(sketch, "E3547", {"start": v(-2.79, 6.47) * mm, "mid": v(-2.9, 6.42) * mm, "end": v(-3.02, 6.36) * mm});
            skArc(sketch, "E3548", {"start": v(-1.65, 6.85) * mm, "mid": v(-1.78, 6.82) * mm, "end": v(-1.9, 6.78) * mm});
            skArc(sketch, "E3549", {"start": v(-0.47, 7.03) * mm, "mid": v(-0.6, 7.02) * mm, "end": v(-0.72, 7) * mm});
            skSolve(sketch);
        }
        {
            var Q0;
            Q0 = qSketchRegion(id + "F0", true);
            extrude(context, id + "F1", {"entities" : qUnion([Q0]), "depth" : 3 * mm, "offsetDistance" : 25 * mm});
        }
        {
            var Q0;
            Q0=makeQuery(id+"F1.opExtrude","CAP_FACE",FACE,{"disambiguationData":[OSD([sQuery(id+"F0.wireOp",EDGE,"E0"),sQuery(id+"F0.wireOp",EDGE,"E1"),sQuery(id+"F0.wireOp",EDGE,"E2"),sQuery(id+"F0.wireOp",EDGE,"E3"),sQuery(id+"F0.wireOp",EDGE,"E4"),sQuery(id+"F0.wireOp",EDGE,"E5"),sQuery(id+"F0.wireOp",EDGE,"E6"),sQuery(id+"F0.wireOp",EDGE,"E7"),sQuery(id+"F0.wireOp",EDGE,"E8"),sQuery(id+"F0.wireOp",EDGE,"E9"),sQuery(id+"F0.wireOp",EDGE,"E10"),sQuery(id+"F0.wireOp",EDGE,"E11"),sQuery(id+"F0.wireOp",EDGE,"E12"),sQuery(id+"F0.wireOp",EDGE,"E13"),sQuery(id+"F0.wireOp",EDGE,"E14"),sQuery(id+"F0.wireOp",EDGE,"E15"),sQuery(id+"F0.wireOp",EDGE,"E16"),sQuery(id+"F0.wireOp",EDGE,"E17"),sQuery(id+"F0.wireOp",EDGE,"E18"),sQuery(id+"F0.wireOp",EDGE,"E19"),sQuery(id+"F0.wireOp",EDGE,"E20"),sQuery(id+"F0.wireOp",EDGE,"E21"),sQuery(id+"F0.wireOp",EDGE,"E22"),sQuery(id+"F0.wireOp",EDGE,"E23"),sQuery(id+"F0.wireOp",EDGE,"E24"),sQuery(id+"F0.wireOp",EDGE,"E25"),sQuery(id+"F0.wireOp",EDGE,"E26"),sQuery(id+"F0.wireOp",EDGE,"E27"),sQuery(id+"F0.wireOp",EDGE,"E28"),sQuery(id+"F0.wireOp",EDGE,"E29"),sQuery(id+"F0.wireOp",EDGE,"E30"),sQuery(id+"F0.wireOp",EDGE,"E31"),sQuery(id+"F0.wireOp",EDGE,"E32"),sQuery(id+"F0.wireOp",EDGE,"E33"),sQuery(id+"F0.wireOp",EDGE,"E34"),sQuery(id+"F0.wireOp",EDGE,"E35"),sQuery(id+"F0.wireOp",EDGE,"E36"),sQuery(id+"F0.wireOp",EDGE,"E37"),sQuery(id+"F0.wireOp",EDGE,"E38"),sQuery(id+"F0.wireOp",EDGE,"E39"),sQuery(id+"F0.wireOp",EDGE,"E40"),sQuery(id+"F0.wireOp",EDGE,"E41"),sQuery(id+"F0.wireOp",EDGE,"E42"),sQuery(id+"F0.wireOp",EDGE,"E43"),sQuery(id+"F0.wireOp",EDGE,"E44"),sQuery(id+"F0.wireOp",EDGE,"E45"),sQuery(id+"F0.wireOp",EDGE,"E46"),sQuery(id+"F0.wireOp",EDGE,"E47"),sQuery(id+"F0.wireOp",EDGE,"E48"),sQuery(id+"F0.wireOp",EDGE,"E49"),sQuery(id+"F0.wireOp",EDGE,"E50"),sQuery(id+"F0.wireOp",EDGE,"E51"),sQuery(id+"F0.wireOp",EDGE,"E52"),sQuery(id+"F0.wireOp",EDGE,"E53"),sQuery(id+"F0.wireOp",EDGE,"E54"),sQuery(id+"F0.wireOp",EDGE,"E55"),sQuery(id+"F0.wireOp",EDGE,"E56"),sQuery(id+"F0.wireOp",EDGE,"E57"),sQuery(id+"F0.wireOp",EDGE,"E58"),sQuery(id+"F0.wireOp",EDGE,"E59"),sQuery(id+"F0.wireOp",EDGE,"E60"),sQuery(id+"F0.wireOp",EDGE,"E61"),sQuery(id+"F0.wireOp",EDGE,"E62"),sQuery(id+"F0.wireOp",EDGE,"E63"),sQuery(id+"F0.wireOp",EDGE,"E64"),sQuery(id+"F0.wireOp",EDGE,"E65"),sQuery(id+"F0.wireOp",EDGE,"E66"),sQuery(id+"F0.wireOp",EDGE,"E67"),sQuery(id+"F0.wireOp",EDGE,"E68"),sQuery(id+"F0.wireOp",EDGE,"E69"),sQuery(id+"F0.wireOp",EDGE,"E70"),sQuery(id+"F0.wireOp",EDGE,"E71"),sQuery(id+"F0.wireOp",EDGE,"E72"),sQuery(id+"F0.wireOp",EDGE,"E73"),sQuery(id+"F0.wireOp",EDGE,"E74"),sQuery(id+"F0.wireOp",EDGE,"E75"),sQuery(id+"F0.wireOp",EDGE,"E76"),sQuery(id+"F0.wireOp",EDGE,"E77"),sQuery(id+"F0.wireOp",EDGE,"E78"),sQuery(id+"F0.wireOp",EDGE,"E79"),sQuery(id+"F0.wireOp",EDGE,"E80"),sQuery(id+"F0.wireOp",EDGE,"E81"),sQuery(id+"F0.wireOp",EDGE,"E82"),sQuery(id+"F0.wireOp",EDGE,"E83"),sQuery(id+"F0.wireOp",EDGE,"E84"),sQuery(id+"F0.wireOp",EDGE,"E85"),sQuery(id+"F0.wireOp",EDGE,"E86"),sQuery(id+"F0.wireOp",EDGE,"E87"),sQuery(id+"F0.wireOp",EDGE,"E88"),sQuery(id+"F0.wireOp",EDGE,"E89"),sQuery(id+"F0.wireOp",EDGE,"E90"),sQuery(id+"F0.wireOp",EDGE,"E91"),sQuery(id+"F0.wireOp",EDGE,"E92"),sQuery(id+"F0.wireOp",EDGE,"E93"),sQuery(id+"F0.wireOp",EDGE,"E94"),sQuery(id+"F0.wireOp",EDGE,"E95"),sQuery(id+"F0.wireOp",EDGE,"E96"),sQuery(id+"F0.wireOp",EDGE,"E97"),sQuery(id+"F0.wireOp",EDGE,"E98"),sQuery(id+"F0.wireOp",EDGE,"E99"),sQuery(id+"F0.wireOp",EDGE,"E100"),sQuery(id+"F0.wireOp",EDGE,"E101"),sQuery(id+"F0.wireOp",EDGE,"E102"),sQuery(id+"F0.wireOp",EDGE,"E103"),sQuery(id+"F0.wireOp",EDGE,"E104"),sQuery(id+"F0.wireOp",EDGE,"E105"),sQuery(id+"F0.wireOp",EDGE,"E106"),sQuery(id+"F0.wireOp",EDGE,"E107"),sQuery(id+"F0.wireOp",EDGE,"E108"),sQuery(id+"F0.wireOp",EDGE,"E109"),sQuery(id+"F0.wireOp",EDGE,"E110"),sQuery(id+"F0.wireOp",EDGE,"E111"),sQuery(id+"F0.wireOp",EDGE,"E112"),sQuery(id+"F0.wireOp",EDGE,"E113"),sQuery(id+"F0.wireOp",EDGE,"E114"),sQuery(id+"F0.wireOp",EDGE,"E115"),sQuery(id+"F0.wireOp",EDGE,"E116"),sQuery(id+"F0.wireOp",EDGE,"E117"),sQuery(id+"F0.wireOp",EDGE,"E118"),sQuery(id+"F0.wireOp",EDGE,"E119"),sQuery(id+"F0.wireOp",EDGE,"E120"),sQuery(id+"F0.wireOp",EDGE,"E121"),sQuery(id+"F0.wireOp",EDGE,"E122"),sQuery(id+"F0.wireOp",EDGE,"E123"),sQuery(id+"F0.wireOp",EDGE,"E124"),sQuery(id+"F0.wireOp",EDGE,"E125"),sQuery(id+"F0.wireOp",EDGE,"E126"),sQuery(id+"F0.wireOp",EDGE,"E127"),sQuery(id+"F0.wireOp",EDGE,"E128"),sQuery(id+"F0.wireOp",EDGE,"E129"),sQuery(id+"F0.wireOp",EDGE,"E130"),sQuery(id+"F0.wireOp",EDGE,"E131"),sQuery(id+"F0.wireOp",EDGE,"E132"),sQuery(id+"F0.wireOp",EDGE,"E133"),sQuery(id+"F0.wireOp",EDGE,"E134"),sQuery(id+"F0.wireOp",EDGE,"E135"),sQuery(id+"F0.wireOp",EDGE,"E136"),sQuery(id+"F0.wireOp",EDGE,"E137"),sQuery(id+"F0.wireOp",EDGE,"E138"),sQuery(id+"F0.wireOp",EDGE,"E139"),sQuery(id+"F0.wireOp",EDGE,"E140"),sQuery(id+"F0.wireOp",EDGE,"E141"),sQuery(id+"F0.wireOp",EDGE,"E142"),sQuery(id+"F0.wireOp",EDGE,"E143"),sQuery(id+"F0.wireOp",EDGE,"E144"),sQuery(id+"F0.wireOp",EDGE,"E145"),sQuery(id+"F0.wireOp",EDGE,"E146"),sQuery(id+"F0.wireOp",EDGE,"E147"),sQuery(id+"F0.wireOp",EDGE,"E148"),sQuery(id+"F0.wireOp",EDGE,"E149"),sQuery(id+"F0.wireOp",EDGE,"E150"),sQuery(id+"F0.wireOp",EDGE,"E151"),sQuery(id+"F0.wireOp",EDGE,"E152"),sQuery(id+"F0.wireOp",EDGE,"E153"),sQuery(id+"F0.wireOp",EDGE,"E154"),sQuery(id+"F0.wireOp",EDGE,"E155"),sQuery(id+"F0.wireOp",EDGE,"E156"),sQuery(id+"F0.wireOp",EDGE,"E157"),sQuery(id+"F0.wireOp",EDGE,"E158"),sQuery(id+"F0.wireOp",EDGE,"E159"),sQuery(id+"F0.wireOp",EDGE,"E160"),sQuery(id+"F0.wireOp",EDGE,"E161"),sQuery(id+"F0.wireOp",EDGE,"E162"),sQuery(id+"F0.wireOp",EDGE,"E163"),sQuery(id+"F0.wireOp",EDGE,"E164"),sQuery(id+"F0.wireOp",EDGE,"E165"),sQuery(id+"F0.wireOp",EDGE,"E166"),sQuery(id+"F0.wireOp",EDGE,"E167"),sQuery(id+"F0.wireOp",EDGE,"E168"),sQuery(id+"F0.wireOp",EDGE,"E169"),sQuery(id+"F0.wireOp",EDGE,"E170"),sQuery(id+"F0.wireOp",EDGE,"E171"),sQuery(id+"F0.wireOp",EDGE,"E172"),sQuery(id+"F0.wireOp",EDGE,"E173"),sQuery(id+"F0.wireOp",EDGE,"E174"),sQuery(id+"F0.wireOp",EDGE,"E175"),sQuery(id+"F0.wireOp",EDGE,"E176"),sQuery(id+"F0.wireOp",EDGE,"E177"),sQuery(id+"F0.wireOp",EDGE,"E178"),sQuery(id+"F0.wireOp",EDGE,"E179"),sQuery(id+"F0.wireOp",EDGE,"E180"),sQuery(id+"F0.wireOp",EDGE,"E181"),sQuery(id+"F0.wireOp",EDGE,"E182"),sQuery(id+"F0.wireOp",EDGE,"E183"),sQuery(id+"F0.wireOp",EDGE,"E184"),sQuery(id+"F0.wireOp",EDGE,"E185"),sQuery(id+"F0.wireOp",EDGE,"E186"),sQuery(id+"F0.wireOp",EDGE,"E187"),sQuery(id+"F0.wireOp",EDGE,"E188"),sQuery(id+"F0.wireOp",EDGE,"E189"),sQuery(id+"F0.wireOp",EDGE,"E190"),sQuery(id+"F0.wireOp",EDGE,"E191"),sQuery(id+"F0.wireOp",EDGE,"E192"),sQuery(id+"F0.wireOp",EDGE,"E193"),sQuery(id+"F0.wireOp",EDGE,"E194"),sQuery(id+"F0.wireOp",EDGE,"E195"),sQuery(id+"F0.wireOp",EDGE,"E196"),sQuery(id+"F0.wireOp",EDGE,"E197"),sQuery(id+"F0.wireOp",EDGE,"E198"),sQuery(id+"F0.wireOp",EDGE,"E199"),sQuery(id+"F0.wireOp",EDGE,"E200"),sQuery(id+"F0.wireOp",EDGE,"E201"),sQuery(id+"F0.wireOp",EDGE,"E202"),sQuery(id+"F0.wireOp",EDGE,"E203"),sQuery(id+"F0.wireOp",EDGE,"E204"),sQuery(id+"F0.wireOp",EDGE,"E205"),sQuery(id+"F0.wireOp",EDGE,"E206"),sQuery(id+"F0.wireOp",EDGE,"E207"),sQuery(id+"F0.wireOp",EDGE,"E208"),sQuery(id+"F0.wireOp",EDGE,"E209"),sQuery(id+"F0.wireOp",EDGE,"E210"),sQuery(id+"F0.wireOp",EDGE,"E211"),sQuery(id+"F0.wireOp",EDGE,"E212"),sQuery(id+"F0.wireOp",EDGE,"E213"),sQuery(id+"F0.wireOp",EDGE,"E214"),sQuery(id+"F0.wireOp",EDGE,"E215"),sQuery(id+"F0.wireOp",EDGE,"E216"),sQuery(id+"F0.wireOp",EDGE,"E217"),sQuery(id+"F0.wireOp",EDGE,"E218"),sQuery(id+"F0.wireOp",EDGE,"E219"),sQuery(id+"F0.wireOp",EDGE,"E220"),sQuery(id+"F0.wireOp",EDGE,"E221"),sQuery(id+"F0.wireOp",EDGE,"E222"),sQuery(id+"F0.wireOp",EDGE,"E223"),sQuery(id+"F0.wireOp",EDGE,"E224"),sQuery(id+"F0.wireOp",EDGE,"E225"),sQuery(id+"F0.wireOp",EDGE,"E226"),sQuery(id+"F0.wireOp",EDGE,"E227"),sQuery(id+"F0.wireOp",EDGE,"E228"),sQuery(id+"F0.wireOp",EDGE,"E229"),sQuery(id+"F0.wireOp",EDGE,"E230"),sQuery(id+"F0.wireOp",EDGE,"E231"),sQuery(id+"F0.wireOp",EDGE,"E232"),sQuery(id+"F0.wireOp",EDGE,"E233"),sQuery(id+"F0.wireOp",EDGE,"E234"),sQuery(id+"F0.wireOp",EDGE,"E235"),sQuery(id+"F0.wireOp",EDGE,"E236"),sQuery(id+"F0.wireOp",EDGE,"E237"),sQuery(id+"F0.wireOp",EDGE,"E238"),sQuery(id+"F0.wireOp",EDGE,"E239"),sQuery(id+"F0.wireOp",EDGE,"E240"),sQuery(id+"F0.wireOp",EDGE,"E241"),sQuery(id+"F0.wireOp",EDGE,"E242"),sQuery(id+"F0.wireOp",EDGE,"E243"),sQuery(id+"F0.wireOp",EDGE,"E244"),sQuery(id+"F0.wireOp",EDGE,"E245"),sQuery(id+"F0.wireOp",EDGE,"E246"),sQuery(id+"F0.wireOp",EDGE,"E247"),sQuery(id+"F0.wireOp",EDGE,"E248"),sQuery(id+"F0.wireOp",EDGE,"E249"),sQuery(id+"F0.wireOp",EDGE,"E250"),sQuery(id+"F0.wireOp",EDGE,"E251"),sQuery(id+"F0.wireOp",EDGE,"E252"),sQuery(id+"F0.wireOp",EDGE,"E253"),sQuery(id+"F0.wireOp",EDGE,"E254"),sQuery(id+"F0.wireOp",EDGE,"E255"),sQuery(id+"F0.wireOp",EDGE,"E256"),sQuery(id+"F0.wireOp",EDGE,"E257"),sQuery(id+"F0.wireOp",EDGE,"E258"),sQuery(id+"F0.wireOp",EDGE,"E259"),sQuery(id+"F0.wireOp",EDGE,"E260"),sQuery(id+"F0.wireOp",EDGE,"E261"),sQuery(id+"F0.wireOp",EDGE,"E262"),sQuery(id+"F0.wireOp",EDGE,"E263"),sQuery(id+"F0.wireOp",EDGE,"E264"),sQuery(id+"F0.wireOp",EDGE,"E265"),sQuery(id+"F0.wireOp",EDGE,"E266"),sQuery(id+"F0.wireOp",EDGE,"E267"),sQuery(id+"F0.wireOp",EDGE,"E268"),sQuery(id+"F0.wireOp",EDGE,"E269"),sQuery(id+"F0.wireOp",EDGE,"E270"),sQuery(id+"F0.wireOp",EDGE,"E271"),sQuery(id+"F0.wireOp",EDGE,"E272"),sQuery(id+"F0.wireOp",EDGE,"E273"),sQuery(id+"F0.wireOp",EDGE,"E274"),sQuery(id+"F0.wireOp",EDGE,"E275"),sQuery(id+"F0.wireOp",EDGE,"E276"),sQuery(id+"F0.wireOp",EDGE,"E277"),sQuery(id+"F0.wireOp",EDGE,"E278"),sQuery(id+"F0.wireOp",EDGE,"E279"),sQuery(id+"F0.wireOp",EDGE,"E280"),sQuery(id+"F0.wireOp",EDGE,"E281"),sQuery(id+"F0.wireOp",EDGE,"E282"),sQuery(id+"F0.wireOp",EDGE,"E283"),sQuery(id+"F0.wireOp",EDGE,"E284"),sQuery(id+"F0.wireOp",EDGE,"E285"),sQuery(id+"F0.wireOp",EDGE,"E286"),sQuery(id+"F0.wireOp",EDGE,"E287"),sQuery(id+"F0.wireOp",EDGE,"E288"),sQuery(id+"F0.wireOp",EDGE,"E289"),sQuery(id+"F0.wireOp",EDGE,"E290"),sQuery(id+"F0.wireOp",EDGE,"E291"),sQuery(id+"F0.wireOp",EDGE,"E292"),sQuery(id+"F0.wireOp",EDGE,"E293"),sQuery(id+"F0.wireOp",EDGE,"E294"),sQuery(id+"F0.wireOp",EDGE,"E295"),sQuery(id+"F0.wireOp",EDGE,"E296"),sQuery(id+"F0.wireOp",EDGE,"E297"),sQuery(id+"F0.wireOp",EDGE,"E298"),sQuery(id+"F0.wireOp",EDGE,"E299"),sQuery(id+"F0.wireOp",EDGE,"E300"),sQuery(id+"F0.wireOp",EDGE,"E301"),sQuery(id+"F0.wireOp",EDGE,"E302"),sQuery(id+"F0.wireOp",EDGE,"E303"),sQuery(id+"F0.wireOp",EDGE,"E304"),sQuery(id+"F0.wireOp",EDGE,"E305"),sQuery(id+"F0.wireOp",EDGE,"E306"),sQuery(id+"F0.wireOp",EDGE,"E307"),sQuery(id+"F0.wireOp",EDGE,"E308"),sQuery(id+"F0.wireOp",EDGE,"E309"),sQuery(id+"F0.wireOp",EDGE,"E310"),sQuery(id+"F0.wireOp",EDGE,"E311"),sQuery(id+"F0.wireOp",EDGE,"E312"),sQuery(id+"F0.wireOp",EDGE,"E313"),sQuery(id+"F0.wireOp",EDGE,"E314"),sQuery(id+"F0.wireOp",EDGE,"E315"),sQuery(id+"F0.wireOp",EDGE,"E316"),sQuery(id+"F0.wireOp",EDGE,"E317"),sQuery(id+"F0.wireOp",EDGE,"E318"),sQuery(id+"F0.wireOp",EDGE,"E319"),sQuery(id+"F0.wireOp",EDGE,"E320"),sQuery(id+"F0.wireOp",EDGE,"E321"),sQuery(id+"F0.wireOp",EDGE,"E322"),sQuery(id+"F0.wireOp",EDGE,"E323"),sQuery(id+"F0.wireOp",EDGE,"E324"),sQuery(id+"F0.wireOp",EDGE,"E325"),sQuery(id+"F0.wireOp",EDGE,"E326"),sQuery(id+"F0.wireOp",EDGE,"E327"),sQuery(id+"F0.wireOp",EDGE,"E328"),sQuery(id+"F0.wireOp",EDGE,"E329"),sQuery(id+"F0.wireOp",EDGE,"E330"),sQuery(id+"F0.wireOp",EDGE,"E331"),sQuery(id+"F0.wireOp",EDGE,"E332"),sQuery(id+"F0.wireOp",EDGE,"E333"),sQuery(id+"F0.wireOp",EDGE,"E334"),sQuery(id+"F0.wireOp",EDGE,"E335"),sQuery(id+"F0.wireOp",EDGE,"E336"),sQuery(id+"F0.wireOp",EDGE,"E337"),sQuery(id+"F0.wireOp",EDGE,"E338"),sQuery(id+"F0.wireOp",EDGE,"E339"),sQuery(id+"F0.wireOp",EDGE,"E340"),sQuery(id+"F0.wireOp",EDGE,"E341"),sQuery(id+"F0.wireOp",EDGE,"E342"),sQuery(id+"F0.wireOp",EDGE,"E343"),sQuery(id+"F0.wireOp",EDGE,"E344"),sQuery(id+"F0.wireOp",EDGE,"E345"),sQuery(id+"F0.wireOp",EDGE,"E346"),sQuery(id+"F0.wireOp",EDGE,"E347"),sQuery(id+"F0.wireOp",EDGE,"E348"),sQuery(id+"F0.wireOp",EDGE,"E349"),sQuery(id+"F0.wireOp",EDGE,"E350"),sQuery(id+"F0.wireOp",EDGE,"E351"),sQuery(id+"F0.wireOp",EDGE,"E352"),sQuery(id+"F0.wireOp",EDGE,"E353"),sQuery(id+"F0.wireOp",EDGE,"E354"),sQuery(id+"F0.wireOp",EDGE,"E355"),sQuery(id+"F0.wireOp",EDGE,"E356"),sQuery(id+"F0.wireOp",EDGE,"E357"),sQuery(id+"F0.wireOp",EDGE,"E358"),sQuery(id+"F0.wireOp",EDGE,"E359"),sQuery(id+"F0.wireOp",EDGE,"E360"),sQuery(id+"F0.wireOp",EDGE,"E361"),sQuery(id+"F0.wireOp",EDGE,"E362"),sQuery(id+"F0.wireOp",EDGE,"E363"),sQuery(id+"F0.wireOp",EDGE,"E364"),sQuery(id+"F0.wireOp",EDGE,"E365"),sQuery(id+"F0.wireOp",EDGE,"E366"),sQuery(id+"F0.wireOp",EDGE,"E367"),sQuery(id+"F0.wireOp",EDGE,"E368"),sQuery(id+"F0.wireOp",EDGE,"E369"),sQuery(id+"F0.wireOp",EDGE,"E370"),sQuery(id+"F0.wireOp",EDGE,"E371"),sQuery(id+"F0.wireOp",EDGE,"E372"),sQuery(id+"F0.wireOp",EDGE,"E373"),sQuery(id+"F0.wireOp",EDGE,"E374"),sQuery(id+"F0.wireOp",EDGE,"E375"),sQuery(id+"F0.wireOp",EDGE,"E376"),sQuery(id+"F0.wireOp",EDGE,"E377"),sQuery(id+"F0.wireOp",EDGE,"E378"),sQuery(id+"F0.wireOp",EDGE,"E379"),sQuery(id+"F0.wireOp",EDGE,"E380"),sQuery(id+"F0.wireOp",EDGE,"E381"),sQuery(id+"F0.wireOp",EDGE,"E382"),sQuery(id+"F0.wireOp",EDGE,"E383"),sQuery(id+"F0.wireOp",EDGE,"E384"),sQuery(id+"F0.wireOp",EDGE,"E385"),sQuery(id+"F0.wireOp",EDGE,"E386"),sQuery(id+"F0.wireOp",EDGE,"E387"),sQuery(id+"F0.wireOp",EDGE,"E388"),sQuery(id+"F0.wireOp",EDGE,"E389"),sQuery(id+"F0.wireOp",EDGE,"E390"),sQuery(id+"F0.wireOp",EDGE,"E391"),sQuery(id+"F0.wireOp",EDGE,"E392"),sQuery(id+"F0.wireOp",EDGE,"E393"),sQuery(id+"F0.wireOp",EDGE,"E394"),sQuery(id+"F0.wireOp",EDGE,"E395"),sQuery(id+"F0.wireOp",EDGE,"E396"),sQuery(id+"F0.wireOp",EDGE,"E397"),sQuery(id+"F0.wireOp",EDGE,"E398"),sQuery(id+"F0.wireOp",EDGE,"E399"),sQuery(id+"F0.wireOp",EDGE,"E400"),sQuery(id+"F0.wireOp",EDGE,"E401"),sQuery(id+"F0.wireOp",EDGE,"E402"),sQuery(id+"F0.wireOp",EDGE,"E403"),sQuery(id+"F0.wireOp",EDGE,"E404"),sQuery(id+"F0.wireOp",EDGE,"E405"),sQuery(id+"F0.wireOp",EDGE,"E406"),sQuery(id+"F0.wireOp",EDGE,"E407"),sQuery(id+"F0.wireOp",EDGE,"E408"),sQuery(id+"F0.wireOp",EDGE,"E409"),sQuery(id+"F0.wireOp",EDGE,"E410"),sQuery(id+"F0.wireOp",EDGE,"E411"),sQuery(id+"F0.wireOp",EDGE,"E412"),sQuery(id+"F0.wireOp",EDGE,"E413"),sQuery(id+"F0.wireOp",EDGE,"E414"),sQuery(id+"F0.wireOp",EDGE,"E415"),sQuery(id+"F0.wireOp",EDGE,"E416"),sQuery(id+"F0.wireOp",EDGE,"E417"),sQuery(id+"F0.wireOp",EDGE,"E418"),sQuery(id+"F0.wireOp",EDGE,"E419"),sQuery(id+"F0.wireOp",EDGE,"E420"),sQuery(id+"F0.wireOp",EDGE,"E421"),sQuery(id+"F0.wireOp",EDGE,"E422"),sQuery(id+"F0.wireOp",EDGE,"E423"),sQuery(id+"F0.wireOp",EDGE,"E424"),sQuery(id+"F0.wireOp",EDGE,"E425"),sQuery(id+"F0.wireOp",EDGE,"E426"),sQuery(id+"F0.wireOp",EDGE,"E427"),sQuery(id+"F0.wireOp",EDGE,"E428"),sQuery(id+"F0.wireOp",EDGE,"E429"),sQuery(id+"F0.wireOp",EDGE,"E430"),sQuery(id+"F0.wireOp",EDGE,"E431"),sQuery(id+"F0.wireOp",EDGE,"E432"),sQuery(id+"F0.wireOp",EDGE,"E433"),sQuery(id+"F0.wireOp",EDGE,"E434"),sQuery(id+"F0.wireOp",EDGE,"E435"),sQuery(id+"F0.wireOp",EDGE,"E436"),sQuery(id+"F0.wireOp",EDGE,"E437"),sQuery(id+"F0.wireOp",EDGE,"E438"),sQuery(id+"F0.wireOp",EDGE,"E439"),sQuery(id+"F0.wireOp",EDGE,"E440"),sQuery(id+"F0.wireOp",EDGE,"E441"),sQuery(id+"F0.wireOp",EDGE,"E442"),sQuery(id+"F0.wireOp",EDGE,"E443"),sQuery(id+"F0.wireOp",EDGE,"E444"),sQuery(id+"F0.wireOp",EDGE,"E445"),sQuery(id+"F0.wireOp",EDGE,"E446"),sQuery(id+"F0.wireOp",EDGE,"E447"),sQuery(id+"F0.wireOp",EDGE,"E448"),sQuery(id+"F0.wireOp",EDGE,"E449"),sQuery(id+"F0.wireOp",EDGE,"E450"),sQuery(id+"F0.wireOp",EDGE,"E451"),sQuery(id+"F0.wireOp",EDGE,"E452"),sQuery(id+"F0.wireOp",EDGE,"E453"),sQuery(id+"F0.wireOp",EDGE,"E454"),sQuery(id+"F0.wireOp",EDGE,"E455"),sQuery(id+"F0.wireOp",EDGE,"E456"),sQuery(id+"F0.wireOp",EDGE,"E457"),sQuery(id+"F0.wireOp",EDGE,"E458"),sQuery(id+"F0.wireOp",EDGE,"E459"),sQuery(id+"F0.wireOp",EDGE,"E460"),sQuery(id+"F0.wireOp",EDGE,"E461"),sQuery(id+"F0.wireOp",EDGE,"E462"),sQuery(id+"F0.wireOp",EDGE,"E463"),sQuery(id+"F0.wireOp",EDGE,"E464"),sQuery(id+"F0.wireOp",EDGE,"E465"),sQuery(id+"F0.wireOp",EDGE,"E466"),sQuery(id+"F0.wireOp",EDGE,"E467"),sQuery(id+"F0.wireOp",EDGE,"E468"),sQuery(id+"F0.wireOp",EDGE,"E469"),sQuery(id+"F0.wireOp",EDGE,"E470"),sQuery(id+"F0.wireOp",EDGE,"E471"),sQuery(id+"F0.wireOp",EDGE,"E472"),sQuery(id+"F0.wireOp",EDGE,"E473"),sQuery(id+"F0.wireOp",EDGE,"E474"),sQuery(id+"F0.wireOp",EDGE,"E475"),sQuery(id+"F0.wireOp",EDGE,"E476"),sQuery(id+"F0.wireOp",EDGE,"E477"),sQuery(id+"F0.wireOp",EDGE,"E478"),sQuery(id+"F0.wireOp",EDGE,"E479"),sQuery(id+"F0.wireOp",EDGE,"E480"),sQuery(id+"F0.wireOp",EDGE,"E481"),sQuery(id+"F0.wireOp",EDGE,"E482"),sQuery(id+"F0.wireOp",EDGE,"E483"),sQuery(id+"F0.wireOp",EDGE,"E484"),sQuery(id+"F0.wireOp",EDGE,"E485"),sQuery(id+"F0.wireOp",EDGE,"E486"),sQuery(id+"F0.wireOp",EDGE,"E487"),sQuery(id+"F0.wireOp",EDGE,"E488"),sQuery(id+"F0.wireOp",EDGE,"E489"),sQuery(id+"F0.wireOp",EDGE,"E490"),sQuery(id+"F0.wireOp",EDGE,"E491"),sQuery(id+"F0.wireOp",EDGE,"E492"),sQuery(id+"F0.wireOp",EDGE,"E493"),sQuery(id+"F0.wireOp",EDGE,"E494"),sQuery(id+"F0.wireOp",EDGE,"E495"),sQuery(id+"F0.wireOp",EDGE,"E496"),sQuery(id+"F0.wireOp",EDGE,"E497"),sQuery(id+"F0.wireOp",EDGE,"E498"),sQuery(id+"F0.wireOp",EDGE,"E499"),sQuery(id+"F0.wireOp",EDGE,"E500"),sQuery(id+"F0.wireOp",EDGE,"E501"),sQuery(id+"F0.wireOp",EDGE,"E502"),sQuery(id+"F0.wireOp",EDGE,"E503"),sQuery(id+"F0.wireOp",EDGE,"E504"),sQuery(id+"F0.wireOp",EDGE,"E505"),sQuery(id+"F0.wireOp",EDGE,"E506"),sQuery(id+"F0.wireOp",EDGE,"E507"),sQuery(id+"F0.wireOp",EDGE,"E508"),sQuery(id+"F0.wireOp",EDGE,"E509"),sQuery(id+"F0.wireOp",EDGE,"E510"),sQuery(id+"F0.wireOp",EDGE,"E511"),sQuery(id+"F0.wireOp",EDGE,"E512"),sQuery(id+"F0.wireOp",EDGE,"E513"),sQuery(id+"F0.wireOp",EDGE,"E514"),sQuery(id+"F0.wireOp",EDGE,"E515"),sQuery(id+"F0.wireOp",EDGE,"E516"),sQuery(id+"F0.wireOp",EDGE,"E517"),sQuery(id+"F0.wireOp",EDGE,"E518"),sQuery(id+"F0.wireOp",EDGE,"E519"),sQuery(id+"F0.wireOp",EDGE,"E520"),sQuery(id+"F0.wireOp",EDGE,"E521"),sQuery(id+"F0.wireOp",EDGE,"E522"),sQuery(id+"F0.wireOp",EDGE,"E523"),sQuery(id+"F0.wireOp",EDGE,"E523"),sQuery(id+"F0.wireOp",EDGE,"E524"),sQuery(id+"F0.wireOp",EDGE,"E525"),sQuery(id+"F0.wireOp",EDGE,"E526"),sQuery(id+"F0.wireOp",EDGE,"E527"),sQuery(id+"F0.wireOp",EDGE,"E528"),sQuery(id+"F0.wireOp",EDGE,"E529"),sQuery(id+"F0.wireOp",EDGE,"E530"),sQuery(id+"F0.wireOp",EDGE,"E531"),sQuery(id+"F0.wireOp",EDGE,"E532"),sQuery(id+"F0.wireOp",EDGE,"E533"),sQuery(id+"F0.wireOp",EDGE,"E534"),sQuery(id+"F0.wireOp",EDGE,"E535"),sQuery(id+"F0.wireOp",EDGE,"E536"),sQuery(id+"F0.wireOp",EDGE,"E537"),sQuery(id+"F0.wireOp",EDGE,"E538"),sQuery(id+"F0.wireOp",EDGE,"E539"),sQuery(id+"F0.wireOp",EDGE,"E540"),sQuery(id+"F0.wireOp",EDGE,"E541"),sQuery(id+"F0.wireOp",EDGE,"E542"),sQuery(id+"F0.wireOp",EDGE,"E543"),sQuery(id+"F0.wireOp",EDGE,"E544"),sQuery(id+"F0.wireOp",EDGE,"E545"),sQuery(id+"F0.wireOp",EDGE,"E546"),sQuery(id+"F0.wireOp",EDGE,"E547"),sQuery(id+"F0.wireOp",EDGE,"E548"),sQuery(id+"F0.wireOp",EDGE,"E549"),sQuery(id+"F0.wireOp",EDGE,"E550"),sQuery(id+"F0.wireOp",EDGE,"E551"),sQuery(id+"F0.wireOp",EDGE,"E552"),sQuery(id+"F0.wireOp",EDGE,"E553"),sQuery(id+"F0.wireOp",EDGE,"E554"),sQuery(id+"F0.wireOp",EDGE,"E555"),sQuery(id+"F0.wireOp",EDGE,"E556"),sQuery(id+"F0.wireOp",EDGE,"E557"),sQuery(id+"F0.wireOp",EDGE,"E558"),sQuery(id+"F0.wireOp",EDGE,"E559"),sQuery(id+"F0.wireOp",EDGE,"E560"),sQuery(id+"F0.wireOp",EDGE,"E561"),sQuery(id+"F0.wireOp",EDGE,"E562"),sQuery(id+"F0.wireOp",EDGE,"E563"),sQuery(id+"F0.wireOp",EDGE,"E564"),sQuery(id+"F0.wireOp",EDGE,"E565"),sQuery(id+"F0.wireOp",EDGE,"E566"),sQuery(id+"F0.wireOp",EDGE,"E567"),sQuery(id+"F0.wireOp",EDGE,"E568"),sQuery(id+"F0.wireOp",EDGE,"E569"),sQuery(id+"F0.wireOp",EDGE,"E570"),sQuery(id+"F0.wireOp",EDGE,"E571"),sQuery(id+"F0.wireOp",EDGE,"E572"),sQuery(id+"F0.wireOp",EDGE,"E573"),sQuery(id+"F0.wireOp",EDGE,"E574"),sQuery(id+"F0.wireOp",EDGE,"E575"),sQuery(id+"F0.wireOp",EDGE,"E576"),sQuery(id+"F0.wireOp",EDGE,"E577"),sQuery(id+"F0.wireOp",EDGE,"E578"),sQuery(id+"F0.wireOp",EDGE,"E579"),sQuery(id+"F0.wireOp",EDGE,"E580"),sQuery(id+"F0.wireOp",EDGE,"E581"),sQuery(id+"F0.wireOp",EDGE,"E582"),sQuery(id+"F0.wireOp",EDGE,"E583"),sQuery(id+"F0.wireOp",EDGE,"E584"),sQuery(id+"F0.wireOp",EDGE,"E585"),sQuery(id+"F0.wireOp",EDGE,"E586"),sQuery(id+"F0.wireOp",EDGE,"E587"),sQuery(id+"F0.wireOp",EDGE,"E588"),sQuery(id+"F0.wireOp",EDGE,"E589"),sQuery(id+"F0.wireOp",EDGE,"E590"),sQuery(id+"F0.wireOp",EDGE,"E591"),sQuery(id+"F0.wireOp",EDGE,"E592"),sQuery(id+"F0.wireOp",EDGE,"E593"),sQuery(id+"F0.wireOp",EDGE,"E594"),sQuery(id+"F0.wireOp",EDGE,"E595"),sQuery(id+"F0.wireOp",EDGE,"E596"),sQuery(id+"F0.wireOp",EDGE,"E597"),sQuery(id+"F0.wireOp",EDGE,"E598"),sQuery(id+"F0.wireOp",EDGE,"E599"),sQuery(id+"F0.wireOp",EDGE,"E600"),sQuery(id+"F0.wireOp",EDGE,"E601"),sQuery(id+"F0.wireOp",EDGE,"E602"),sQuery(id+"F0.wireOp",EDGE,"E603"),sQuery(id+"F0.wireOp",EDGE,"E604"),sQuery(id+"F0.wireOp",EDGE,"E605"),sQuery(id+"F0.wireOp",EDGE,"E606"),sQuery(id+"F0.wireOp",EDGE,"E607"),sQuery(id+"F0.wireOp",EDGE,"E608"),sQuery(id+"F0.wireOp",EDGE,"E609"),sQuery(id+"F0.wireOp",EDGE,"E610"),sQuery(id+"F0.wireOp",EDGE,"E611"),sQuery(id+"F0.wireOp",EDGE,"E612"),sQuery(id+"F0.wireOp",EDGE,"E613"),sQuery(id+"F0.wireOp",EDGE,"E614"),sQuery(id+"F0.wireOp",EDGE,"E615"),sQuery(id+"F0.wireOp",EDGE,"E616"),sQuery(id+"F0.wireOp",EDGE,"E617"),sQuery(id+"F0.wireOp",EDGE,"E618"),sQuery(id+"F0.wireOp",EDGE,"E619"),sQuery(id+"F0.wireOp",EDGE,"E620"),sQuery(id+"F0.wireOp",EDGE,"E621"),sQuery(id+"F0.wireOp",EDGE,"E622"),sQuery(id+"F0.wireOp",EDGE,"E623"),sQuery(id+"F0.wireOp",EDGE,"E624"),sQuery(id+"F0.wireOp",EDGE,"E625"),sQuery(id+"F0.wireOp",EDGE,"E626"),sQuery(id+"F0.wireOp",EDGE,"E627"),sQuery(id+"F0.wireOp",EDGE,"E628"),sQuery(id+"F0.wireOp",EDGE,"E629"),sQuery(id+"F0.wireOp",EDGE,"E630"),sQuery(id+"F0.wireOp",EDGE,"E631"),sQuery(id+"F0.wireOp",EDGE,"E632"),sQuery(id+"F0.wireOp",EDGE,"E633"),sQuery(id+"F0.wireOp",EDGE,"E634"),sQuery(id+"F0.wireOp",EDGE,"E635"),sQuery(id+"F0.wireOp",EDGE,"E636"),sQuery(id+"F0.wireOp",EDGE,"E637"),sQuery(id+"F0.wireOp",EDGE,"E638"),sQuery(id+"F0.wireOp",EDGE,"E639"),sQuery(id+"F0.wireOp",EDGE,"E640"),sQuery(id+"F0.wireOp",EDGE,"E641"),sQuery(id+"F0.wireOp",EDGE,"E642"),sQuery(id+"F0.wireOp",EDGE,"E643"),sQuery(id+"F0.wireOp",EDGE,"E644"),sQuery(id+"F0.wireOp",EDGE,"E645"),sQuery(id+"F0.wireOp",EDGE,"E646"),sQuery(id+"F0.wireOp",EDGE,"E647"),sQuery(id+"F0.wireOp",EDGE,"E648"),sQuery(id+"F0.wireOp",EDGE,"E649"),sQuery(id+"F0.wireOp",EDGE,"E650"),sQuery(id+"F0.wireOp",EDGE,"E651"),sQuery(id+"F0.wireOp",EDGE,"E652"),sQuery(id+"F0.wireOp",EDGE,"E653"),sQuery(id+"F0.wireOp",EDGE,"E654"),sQuery(id+"F0.wireOp",EDGE,"E655"),sQuery(id+"F0.wireOp",EDGE,"E656"),sQuery(id+"F0.wireOp",EDGE,"E657"),sQuery(id+"F0.wireOp",EDGE,"E658"),sQuery(id+"F0.wireOp",EDGE,"E659"),sQuery(id+"F0.wireOp",EDGE,"E660"),sQuery(id+"F0.wireOp",EDGE,"E661"),sQuery(id+"F0.wireOp",EDGE,"E662"),sQuery(id+"F0.wireOp",EDGE,"E663"),sQuery(id+"F0.wireOp",EDGE,"E664"),sQuery(id+"F0.wireOp",EDGE,"E665"),sQuery(id+"F0.wireOp",EDGE,"E666"),sQuery(id+"F0.wireOp",EDGE,"E667"),sQuery(id+"F0.wireOp",EDGE,"E668"),sQuery(id+"F0.wireOp",EDGE,"E669"),sQuery(id+"F0.wireOp",EDGE,"E670"),sQuery(id+"F0.wireOp",EDGE,"E671"),sQuery(id+"F0.wireOp",EDGE,"E672"),sQuery(id+"F0.wireOp",EDGE,"E673"),sQuery(id+"F0.wireOp",EDGE,"E674"),sQuery(id+"F0.wireOp",EDGE,"E675"),sQuery(id+"F0.wireOp",EDGE,"E676"),sQuery(id+"F0.wireOp",EDGE,"E677"),sQuery(id+"F0.wireOp",EDGE,"E678"),sQuery(id+"F0.wireOp",EDGE,"E679"),sQuery(id+"F0.wireOp",EDGE,"E680"),sQuery(id+"F0.wireOp",EDGE,"E681"),sQuery(id+"F0.wireOp",EDGE,"E682"),sQuery(id+"F0.wireOp",EDGE,"E683"),sQuery(id+"F0.wireOp",EDGE,"E684"),sQuery(id+"F0.wireOp",EDGE,"E685"),sQuery(id+"F0.wireOp",EDGE,"E686"),sQuery(id+"F0.wireOp",EDGE,"E687"),sQuery(id+"F0.wireOp",EDGE,"E688"),sQuery(id+"F0.wireOp",EDGE,"E689"),sQuery(id+"F0.wireOp",EDGE,"E690"),sQuery(id+"F0.wireOp",EDGE,"E691"),sQuery(id+"F0.wireOp",EDGE,"E692"),sQuery(id+"F0.wireOp",EDGE,"E693"),sQuery(id+"F0.wireOp",EDGE,"E694"),sQuery(id+"F0.wireOp",EDGE,"E695"),sQuery(id+"F0.wireOp",EDGE,"E696"),sQuery(id+"F0.wireOp",EDGE,"E697"),sQuery(id+"F0.wireOp",EDGE,"E698"),sQuery(id+"F0.wireOp",EDGE,"E699"),sQuery(id+"F0.wireOp",EDGE,"E700"),sQuery(id+"F0.wireOp",EDGE,"E701"),sQuery(id+"F0.wireOp",EDGE,"E702"),sQuery(id+"F0.wireOp",EDGE,"E703"),sQuery(id+"F0.wireOp",EDGE,"E704"),sQuery(id+"F0.wireOp",EDGE,"E705"),sQuery(id+"F0.wireOp",EDGE,"E706"),sQuery(id+"F0.wireOp",EDGE,"E707"),sQuery(id+"F0.wireOp",EDGE,"E708"),sQuery(id+"F0.wireOp",EDGE,"E709"),sQuery(id+"F0.wireOp",EDGE,"E710"),sQuery(id+"F0.wireOp",EDGE,"E711"),sQuery(id+"F0.wireOp",EDGE,"E712"),sQuery(id+"F0.wireOp",EDGE,"E713"),sQuery(id+"F0.wireOp",EDGE,"E714"),sQuery(id+"F0.wireOp",EDGE,"E715"),sQuery(id+"F0.wireOp",EDGE,"E716"),sQuery(id+"F0.wireOp",EDGE,"E717"),sQuery(id+"F0.wireOp",EDGE,"E718"),sQuery(id+"F0.wireOp",EDGE,"E719"),sQuery(id+"F0.wireOp",EDGE,"E720"),sQuery(id+"F0.wireOp",EDGE,"E721"),sQuery(id+"F0.wireOp",EDGE,"E722"),sQuery(id+"F0.wireOp",EDGE,"E723"),sQuery(id+"F0.wireOp",EDGE,"E724"),sQuery(id+"F0.wireOp",EDGE,"E725"),sQuery(id+"F0.wireOp",EDGE,"E726"),sQuery(id+"F0.wireOp",EDGE,"E727"),sQuery(id+"F0.wireOp",EDGE,"E728"),sQuery(id+"F0.wireOp",EDGE,"E729"),sQuery(id+"F0.wireOp",EDGE,"E730"),sQuery(id+"F0.wireOp",EDGE,"E731"),sQuery(id+"F0.wireOp",EDGE,"E732"),sQuery(id+"F0.wireOp",EDGE,"E733"),sQuery(id+"F0.wireOp",EDGE,"E734"),sQuery(id+"F0.wireOp",EDGE,"E735"),sQuery(id+"F0.wireOp",EDGE,"E736"),sQuery(id+"F0.wireOp",EDGE,"E737"),sQuery(id+"F0.wireOp",EDGE,"E738"),sQuery(id+"F0.wireOp",EDGE,"E739"),sQuery(id+"F0.wireOp",EDGE,"E740"),sQuery(id+"F0.wireOp",EDGE,"E741"),sQuery(id+"F0.wireOp",EDGE,"E742"),sQuery(id+"F0.wireOp",EDGE,"E743"),sQuery(id+"F0.wireOp",EDGE,"E744"),sQuery(id+"F0.wireOp",EDGE,"E745"),sQuery(id+"F0.wireOp",EDGE,"E746"),sQuery(id+"F0.wireOp",EDGE,"E747"),sQuery(id+"F0.wireOp",EDGE,"E748"),sQuery(id+"F0.wireOp",EDGE,"E749"),sQuery(id+"F0.wireOp",EDGE,"E750"),sQuery(id+"F0.wireOp",EDGE,"E751"),sQuery(id+"F0.wireOp",EDGE,"E752"),sQuery(id+"F0.wireOp",EDGE,"E753"),sQuery(id+"F0.wireOp",EDGE,"E754"),sQuery(id+"F0.wireOp",EDGE,"E755"),sQuery(id+"F0.wireOp",EDGE,"E756"),sQuery(id+"F0.wireOp",EDGE,"E757"),sQuery(id+"F0.wireOp",EDGE,"E758"),sQuery(id+"F0.wireOp",EDGE,"E759"),sQuery(id+"F0.wireOp",EDGE,"E760"),sQuery(id+"F0.wireOp",EDGE,"E761"),sQuery(id+"F0.wireOp",EDGE,"E762"),sQuery(id+"F0.wireOp",EDGE,"E763"),sQuery(id+"F0.wireOp",EDGE,"E764"),sQuery(id+"F0.wireOp",EDGE,"E765"),sQuery(id+"F0.wireOp",EDGE,"E766"),sQuery(id+"F0.wireOp",EDGE,"E767"),sQuery(id+"F0.wireOp",EDGE,"E768"),sQuery(id+"F0.wireOp",EDGE,"E769"),sQuery(id+"F0.wireOp",EDGE,"E770"),sQuery(id+"F0.wireOp",EDGE,"E771"),sQuery(id+"F0.wireOp",EDGE,"E772"),sQuery(id+"F0.wireOp",EDGE,"E773"),sQuery(id+"F0.wireOp",EDGE,"E774"),sQuery(id+"F0.wireOp",EDGE,"E775"),sQuery(id+"F0.wireOp",EDGE,"E776"),sQuery(id+"F0.wireOp",EDGE,"E777"),sQuery(id+"F0.wireOp",EDGE,"E778"),sQuery(id+"F0.wireOp",EDGE,"E779"),sQuery(id+"F0.wireOp",EDGE,"E780"),sQuery(id+"F0.wireOp",EDGE,"E781"),sQuery(id+"F0.wireOp",EDGE,"E782"),sQuery(id+"F0.wireOp",EDGE,"E783"),sQuery(id+"F0.wireOp",EDGE,"E784"),sQuery(id+"F0.wireOp",EDGE,"E785"),sQuery(id+"F0.wireOp",EDGE,"E786"),sQuery(id+"F0.wireOp",EDGE,"E787"),sQuery(id+"F0.wireOp",EDGE,"E788"),sQuery(id+"F0.wireOp",EDGE,"E789"),sQuery(id+"F0.wireOp",EDGE,"E790"),sQuery(id+"F0.wireOp",EDGE,"E791"),sQuery(id+"F0.wireOp",EDGE,"E792"),sQuery(id+"F0.wireOp",EDGE,"E793"),sQuery(id+"F0.wireOp",EDGE,"E794"),sQuery(id+"F0.wireOp",EDGE,"E795"),sQuery(id+"F0.wireOp",EDGE,"E796"),sQuery(id+"F0.wireOp",EDGE,"E797"),sQuery(id+"F0.wireOp",EDGE,"E798"),sQuery(id+"F0.wireOp",EDGE,"E799"),sQuery(id+"F0.wireOp",EDGE,"E800"),sQuery(id+"F0.wireOp",EDGE,"E801"),sQuery(id+"F0.wireOp",EDGE,"E802"),sQuery(id+"F0.wireOp",EDGE,"E803"),sQuery(id+"F0.wireOp",EDGE,"E804"),sQuery(id+"F0.wireOp",EDGE,"E805"),sQuery(id+"F0.wireOp",EDGE,"E806"),sQuery(id+"F0.wireOp",EDGE,"E807"),sQuery(id+"F0.wireOp",EDGE,"E808"),sQuery(id+"F0.wireOp",EDGE,"E809"),sQuery(id+"F0.wireOp",EDGE,"E810"),sQuery(id+"F0.wireOp",EDGE,"E811"),sQuery(id+"F0.wireOp",EDGE,"E812"),sQuery(id+"F0.wireOp",EDGE,"E813"),sQuery(id+"F0.wireOp",EDGE,"E814"),sQuery(id+"F0.wireOp",EDGE,"E815"),sQuery(id+"F0.wireOp",EDGE,"E816"),sQuery(id+"F0.wireOp",EDGE,"E817"),sQuery(id+"F0.wireOp",EDGE,"E818"),sQuery(id+"F0.wireOp",EDGE,"E819"),sQuery(id+"F0.wireOp",EDGE,"E820"),sQuery(id+"F0.wireOp",EDGE,"E821"),sQuery(id+"F0.wireOp",EDGE,"E822"),sQuery(id+"F0.wireOp",EDGE,"E823"),sQuery(id+"F0.wireOp",EDGE,"E824"),sQuery(id+"F0.wireOp",EDGE,"E825"),sQuery(id+"F0.wireOp",EDGE,"E826"),sQuery(id+"F0.wireOp",EDGE,"E827"),sQuery(id+"F0.wireOp",EDGE,"E828"),sQuery(id+"F0.wireOp",EDGE,"E829"),sQuery(id+"F0.wireOp",EDGE,"E830"),sQuery(id+"F0.wireOp",EDGE,"E831"),sQuery(id+"F0.wireOp",EDGE,"E832"),sQuery(id+"F0.wireOp",EDGE,"E833"),sQuery(id+"F0.wireOp",EDGE,"E834"),sQuery(id+"F0.wireOp",EDGE,"E835"),sQuery(id+"F0.wireOp",EDGE,"E836"),sQuery(id+"F0.wireOp",EDGE,"E837"),sQuery(id+"F0.wireOp",EDGE,"E838"),sQuery(id+"F0.wireOp",EDGE,"E839"),sQuery(id+"F0.wireOp",EDGE,"E840"),sQuery(id+"F0.wireOp",EDGE,"E841"),sQuery(id+"F0.wireOp",EDGE,"E842"),sQuery(id+"F0.wireOp",EDGE,"E843"),sQuery(id+"F0.wireOp",EDGE,"E844"),sQuery(id+"F0.wireOp",EDGE,"E845"),sQuery(id+"F0.wireOp",EDGE,"E846"),sQuery(id+"F0.wireOp",EDGE,"E847"),sQuery(id+"F0.wireOp",EDGE,"E848"),sQuery(id+"F0.wireOp",EDGE,"E849"),sQuery(id+"F0.wireOp",EDGE,"E850"),sQuery(id+"F0.wireOp",EDGE,"E851"),sQuery(id+"F0.wireOp",EDGE,"E852"),sQuery(id+"F0.wireOp",EDGE,"E853"),sQuery(id+"F0.wireOp",EDGE,"E854"),sQuery(id+"F0.wireOp",EDGE,"E855"),sQuery(id+"F0.wireOp",EDGE,"E856"),sQuery(id+"F0.wireOp",EDGE,"E857"),sQuery(id+"F0.wireOp",EDGE,"E858"),sQuery(id+"F0.wireOp",EDGE,"E859"),sQuery(id+"F0.wireOp",EDGE,"E860"),sQuery(id+"F0.wireOp",EDGE,"E861"),sQuery(id+"F0.wireOp",EDGE,"E862"),sQuery(id+"F0.wireOp",EDGE,"E863"),sQuery(id+"F0.wireOp",EDGE,"E864"),sQuery(id+"F0.wireOp",EDGE,"E865"),sQuery(id+"F0.wireOp",EDGE,"E866"),sQuery(id+"F0.wireOp",EDGE,"E867"),sQuery(id+"F0.wireOp",EDGE,"E868"),sQuery(id+"F0.wireOp",EDGE,"E869"),sQuery(id+"F0.wireOp",EDGE,"E870"),sQuery(id+"F0.wireOp",EDGE,"E871"),sQuery(id+"F0.wireOp",EDGE,"E872"),sQuery(id+"F0.wireOp",EDGE,"E873"),sQuery(id+"F0.wireOp",EDGE,"E874"),sQuery(id+"F0.wireOp",EDGE,"E875"),sQuery(id+"F0.wireOp",EDGE,"E876"),sQuery(id+"F0.wireOp",EDGE,"E877"),sQuery(id+"F0.wireOp",EDGE,"E878"),sQuery(id+"F0.wireOp",EDGE,"E879"),sQuery(id+"F0.wireOp",EDGE,"E880"),sQuery(id+"F0.wireOp",EDGE,"E881"),sQuery(id+"F0.wireOp",EDGE,"E882"),sQuery(id+"F0.wireOp",EDGE,"E883"),sQuery(id+"F0.wireOp",EDGE,"E884"),sQuery(id+"F0.wireOp",EDGE,"E885"),sQuery(id+"F0.wireOp",EDGE,"E886"),sQuery(id+"F0.wireOp",EDGE,"E887"),sQuery(id+"F0.wireOp",EDGE,"E888"),sQuery(id+"F0.wireOp",EDGE,"E889"),sQuery(id+"F0.wireOp",EDGE,"E890"),sQuery(id+"F0.wireOp",EDGE,"E891"),sQuery(id+"F0.wireOp",EDGE,"E892"),sQuery(id+"F0.wireOp",EDGE,"E893"),sQuery(id+"F0.wireOp",EDGE,"E894"),sQuery(id+"F0.wireOp",EDGE,"E895"),sQuery(id+"F0.wireOp",EDGE,"E896"),sQuery(id+"F0.wireOp",EDGE,"E897"),sQuery(id+"F0.wireOp",EDGE,"E898"),sQuery(id+"F0.wireOp",EDGE,"E899"),sQuery(id+"F0.wireOp",EDGE,"E900"),sQuery(id+"F0.wireOp",EDGE,"E901"),sQuery(id+"F0.wireOp",EDGE,"E902"),sQuery(id+"F0.wireOp",EDGE,"E903"),sQuery(id+"F0.wireOp",EDGE,"E904"),sQuery(id+"F0.wireOp",EDGE,"E905"),sQuery(id+"F0.wireOp",EDGE,"E906"),sQuery(id+"F0.wireOp",EDGE,"E907"),sQuery(id+"F0.wireOp",EDGE,"E908"),sQuery(id+"F0.wireOp",EDGE,"E909"),sQuery(id+"F0.wireOp",EDGE,"E910"),sQuery(id+"F0.wireOp",EDGE,"E911"),sQuery(id+"F0.wireOp",EDGE,"E912"),sQuery(id+"F0.wireOp",EDGE,"E913"),sQuery(id+"F0.wireOp",EDGE,"E914"),sQuery(id+"F0.wireOp",EDGE,"E915"),sQuery(id+"F0.wireOp",EDGE,"E916"),sQuery(id+"F0.wireOp",EDGE,"E917"),sQuery(id+"F0.wireOp",EDGE,"E918"),sQuery(id+"F0.wireOp",EDGE,"E919"),sQuery(id+"F0.wireOp",EDGE,"E920"),sQuery(id+"F0.wireOp",EDGE,"E921"),sQuery(id+"F0.wireOp",EDGE,"E922"),sQuery(id+"F0.wireOp",EDGE,"E923"),sQuery(id+"F0.wireOp",EDGE,"E924"),sQuery(id+"F0.wireOp",EDGE,"E925"),sQuery(id+"F0.wireOp",EDGE,"E926"),sQuery(id+"F0.wireOp",EDGE,"E927"),sQuery(id+"F0.wireOp",EDGE,"E928"),sQuery(id+"F0.wireOp",EDGE,"E929"),sQuery(id+"F0.wireOp",EDGE,"E930"),sQuery(id+"F0.wireOp",EDGE,"E931"),sQuery(id+"F0.wireOp",EDGE,"E932"),sQuery(id+"F0.wireOp",EDGE,"E933"),sQuery(id+"F0.wireOp",EDGE,"E934"),sQuery(id+"F0.wireOp",EDGE,"E935"),sQuery(id+"F0.wireOp",EDGE,"E936"),sQuery(id+"F0.wireOp",EDGE,"E937"),sQuery(id+"F0.wireOp",EDGE,"E938"),sQuery(id+"F0.wireOp",EDGE,"E939"),sQuery(id+"F0.wireOp",EDGE,"E940"),sQuery(id+"F0.wireOp",EDGE,"E941"),sQuery(id+"F0.wireOp",EDGE,"E942"),sQuery(id+"F0.wireOp",EDGE,"E943"),sQuery(id+"F0.wireOp",EDGE,"E944"),sQuery(id+"F0.wireOp",EDGE,"E945"),sQuery(id+"F0.wireOp",EDGE,"E946"),sQuery(id+"F0.wireOp",EDGE,"E947"),sQuery(id+"F0.wireOp",EDGE,"E948"),sQuery(id+"F0.wireOp",EDGE,"E949"),sQuery(id+"F0.wireOp",EDGE,"E950"),sQuery(id+"F0.wireOp",EDGE,"E951"),sQuery(id+"F0.wireOp",EDGE,"E952"),sQuery(id+"F0.wireOp",EDGE,"E953"),sQuery(id+"F0.wireOp",EDGE,"E954"),sQuery(id+"F0.wireOp",EDGE,"E955"),sQuery(id+"F0.wireOp",EDGE,"E956"),sQuery(id+"F0.wireOp",EDGE,"E957"),sQuery(id+"F0.wireOp",EDGE,"E958"),sQuery(id+"F0.wireOp",EDGE,"E959"),sQuery(id+"F0.wireOp",EDGE,"E960"),sQuery(id+"F0.wireOp",EDGE,"E961"),sQuery(id+"F0.wireOp",EDGE,"E962"),sQuery(id+"F0.wireOp",EDGE,"E963"),sQuery(id+"F0.wireOp",EDGE,"E964"),sQuery(id+"F0.wireOp",EDGE,"E965"),sQuery(id+"F0.wireOp",EDGE,"E966"),sQuery(id+"F0.wireOp",EDGE,"E967"),sQuery(id+"F0.wireOp",EDGE,"E968"),sQuery(id+"F0.wireOp",EDGE,"E969"),sQuery(id+"F0.wireOp",EDGE,"E970"),sQuery(id+"F0.wireOp",EDGE,"E971"),sQuery(id+"F0.wireOp",EDGE,"E972"),sQuery(id+"F0.wireOp",EDGE,"E973"),sQuery(id+"F0.wireOp",EDGE,"E974"),sQuery(id+"F0.wireOp",EDGE,"E975"),sQuery(id+"F0.wireOp",EDGE,"E976"),sQuery(id+"F0.wireOp",EDGE,"E977"),sQuery(id+"F0.wireOp",EDGE,"E978"),sQuery(id+"F0.wireOp",EDGE,"E979"),sQuery(id+"F0.wireOp",EDGE,"E980"),sQuery(id+"F0.wireOp",EDGE,"E981"),sQuery(id+"F0.wireOp",EDGE,"E982"),sQuery(id+"F0.wireOp",EDGE,"E983"),sQuery(id+"F0.wireOp",EDGE,"E984"),sQuery(id+"F0.wireOp",EDGE,"E985"),sQuery(id+"F0.wireOp",EDGE,"E986"),sQuery(id+"F0.wireOp",EDGE,"E987"),sQuery(id+"F0.wireOp",EDGE,"E988"),sQuery(id+"F0.wireOp",EDGE,"E989"),sQuery(id+"F0.wireOp",EDGE,"E990"),sQuery(id+"F0.wireOp",EDGE,"E991"),sQuery(id+"F0.wireOp",EDGE,"E992"),sQuery(id+"F0.wireOp",EDGE,"E993"),sQuery(id+"F0.wireOp",EDGE,"E994"),sQuery(id+"F0.wireOp",EDGE,"E995"),sQuery(id+"F0.wireOp",EDGE,"E996"),sQuery(id+"F0.wireOp",EDGE,"E997"),sQuery(id+"F0.wireOp",EDGE,"E998"),sQuery(id+"F0.wireOp",EDGE,"E999"),sQuery(id+"F0.wireOp",EDGE,"E1000"),sQuery(id+"F0.wireOp",EDGE,"E1001"),sQuery(id+"F0.wireOp",EDGE,"E1002"),sQuery(id+"F0.wireOp",EDGE,"E1003"),sQuery(id+"F0.wireOp",EDGE,"E1004"),sQuery(id+"F0.wireOp",EDGE,"E1005"),sQuery(id+"F0.wireOp",EDGE,"E1006"),sQuery(id+"F0.wireOp",EDGE,"E1007"),sQuery(id+"F0.wireOp",EDGE,"E1008"),sQuery(id+"F0.wireOp",EDGE,"E1009"),sQuery(id+"F0.wireOp",EDGE,"E1010"),sQuery(id+"F0.wireOp",EDGE,"E1011"),sQuery(id+"F0.wireOp",EDGE,"E1012"),sQuery(id+"F0.wireOp",EDGE,"E1013"),sQuery(id+"F0.wireOp",EDGE,"E1014"),sQuery(id+"F0.wireOp",EDGE,"E1015"),sQuery(id+"F0.wireOp",EDGE,"E1016"),sQuery(id+"F0.wireOp",EDGE,"E1017"),sQuery(id+"F0.wireOp",EDGE,"E1018"),sQuery(id+"F0.wireOp",EDGE,"E1019"),sQuery(id+"F0.wireOp",EDGE,"E1020"),sQuery(id+"F0.wireOp",EDGE,"E1021"),sQuery(id+"F0.wireOp",EDGE,"E1022"),sQuery(id+"F0.wireOp",EDGE,"E1023"),sQuery(id+"F0.wireOp",EDGE,"E1024"),sQuery(id+"F0.wireOp",EDGE,"E1025"),sQuery(id+"F0.wireOp",EDGE,"E1026"),sQuery(id+"F0.wireOp",EDGE,"E1027"),sQuery(id+"F0.wireOp",EDGE,"E1028"),sQuery(id+"F0.wireOp",EDGE,"E1029"),sQuery(id+"F0.wireOp",EDGE,"E1030"),sQuery(id+"F0.wireOp",EDGE,"E1031"),sQuery(id+"F0.wireOp",EDGE,"E1032"),sQuery(id+"F0.wireOp",EDGE,"E1033"),sQuery(id+"F0.wireOp",EDGE,"E1034"),sQuery(id+"F0.wireOp",EDGE,"E1035"),sQuery(id+"F0.wireOp",EDGE,"E1036"),sQuery(id+"F0.wireOp",EDGE,"E1037"),sQuery(id+"F0.wireOp",EDGE,"E1038"),sQuery(id+"F0.wireOp",EDGE,"E1039"),sQuery(id+"F0.wireOp",EDGE,"E1040"),sQuery(id+"F0.wireOp",EDGE,"E1041"),sQuery(id+"F0.wireOp",EDGE,"E1042"),sQuery(id+"F0.wireOp",EDGE,"E1043"),sQuery(id+"F0.wireOp",EDGE,"E1044"),sQuery(id+"F0.wireOp",EDGE,"E1045"),sQuery(id+"F0.wireOp",EDGE,"E1046"),sQuery(id+"F0.wireOp",EDGE,"E1047"),sQuery(id+"F0.wireOp",EDGE,"E1048"),sQuery(id+"F0.wireOp",EDGE,"E1049"),sQuery(id+"F0.wireOp",EDGE,"E1050"),sQuery(id+"F0.wireOp",EDGE,"E1051"),sQuery(id+"F0.wireOp",EDGE,"E1052"),sQuery(id+"F0.wireOp",EDGE,"E1053"),sQuery(id+"F0.wireOp",EDGE,"E1054"),sQuery(id+"F0.wireOp",EDGE,"E1055"),sQuery(id+"F0.wireOp",EDGE,"E1056"),sQuery(id+"F0.wireOp",EDGE,"E1057"),sQuery(id+"F0.wireOp",EDGE,"E1058"),sQuery(id+"F0.wireOp",EDGE,"E1059"),sQuery(id+"F0.wireOp",EDGE,"E1060"),sQuery(id+"F0.wireOp",EDGE,"E1061"),sQuery(id+"F0.wireOp",EDGE,"E1062"),sQuery(id+"F0.wireOp",EDGE,"E1063"),sQuery(id+"F0.wireOp",EDGE,"E1064"),sQuery(id+"F0.wireOp",EDGE,"E1065"),sQuery(id+"F0.wireOp",EDGE,"E1066"),sQuery(id+"F0.wireOp",EDGE,"E1067"),sQuery(id+"F0.wireOp",EDGE,"E1068"),sQuery(id+"F0.wireOp",EDGE,"E1069"),sQuery(id+"F0.wireOp",EDGE,"E1070"),sQuery(id+"F0.wireOp",EDGE,"E1071"),sQuery(id+"F0.wireOp",EDGE,"E1072"),sQuery(id+"F0.wireOp",EDGE,"E1073"),sQuery(id+"F0.wireOp",EDGE,"E1074"),sQuery(id+"F0.wireOp",EDGE,"E1075"),sQuery(id+"F0.wireOp",EDGE,"E1076"),sQuery(id+"F0.wireOp",EDGE,"E1077"),sQuery(id+"F0.wireOp",EDGE,"E1078"),sQuery(id+"F0.wireOp",EDGE,"E1079"),sQuery(id+"F0.wireOp",EDGE,"E1080"),sQuery(id+"F0.wireOp",EDGE,"E1081"),sQuery(id+"F0.wireOp",EDGE,"E1082"),sQuery(id+"F0.wireOp",EDGE,"E1083"),sQuery(id+"F0.wireOp",EDGE,"E1084"),sQuery(id+"F0.wireOp",EDGE,"E1085"),sQuery(id+"F0.wireOp",EDGE,"E1086"),sQuery(id+"F0.wireOp",EDGE,"E1087"),sQuery(id+"F0.wireOp",EDGE,"E1088"),sQuery(id+"F0.wireOp",EDGE,"E1089"),sQuery(id+"F0.wireOp",EDGE,"E1090"),sQuery(id+"F0.wireOp",EDGE,"E1091"),sQuery(id+"F0.wireOp",EDGE,"E1092"),sQuery(id+"F0.wireOp",EDGE,"E1093"),sQuery(id+"F0.wireOp",EDGE,"E1094"),sQuery(id+"F0.wireOp",EDGE,"E1095"),sQuery(id+"F0.wireOp",EDGE,"E1096"),sQuery(id+"F0.wireOp",EDGE,"E1097"),sQuery(id+"F0.wireOp",EDGE,"E1098"),sQuery(id+"F0.wireOp",EDGE,"E1099"),sQuery(id+"F0.wireOp",EDGE,"E1100"),sQuery(id+"F0.wireOp",EDGE,"E1101"),sQuery(id+"F0.wireOp",EDGE,"E1102"),sQuery(id+"F0.wireOp",EDGE,"E1103"),sQuery(id+"F0.wireOp",EDGE,"E1104"),sQuery(id+"F0.wireOp",EDGE,"E1105"),sQuery(id+"F0.wireOp",EDGE,"E1106"),sQuery(id+"F0.wireOp",EDGE,"E1107"),sQuery(id+"F0.wireOp",EDGE,"E1108"),sQuery(id+"F0.wireOp",EDGE,"E1109"),sQuery(id+"F0.wireOp",EDGE,"E1110"),sQuery(id+"F0.wireOp",EDGE,"E1111"),sQuery(id+"F0.wireOp",EDGE,"E1112"),sQuery(id+"F0.wireOp",EDGE,"E1113"),sQuery(id+"F0.wireOp",EDGE,"E1114"),sQuery(id+"F0.wireOp",EDGE,"E1115"),sQuery(id+"F0.wireOp",EDGE,"E1116"),sQuery(id+"F0.wireOp",EDGE,"E1117"),sQuery(id+"F0.wireOp",EDGE,"E1118"),sQuery(id+"F0.wireOp",EDGE,"E1119"),sQuery(id+"F0.wireOp",EDGE,"E1120"),sQuery(id+"F0.wireOp",EDGE,"E1121"),sQuery(id+"F0.wireOp",EDGE,"E1122"),sQuery(id+"F0.wireOp",EDGE,"E1123"),sQuery(id+"F0.wireOp",EDGE,"E1124"),sQuery(id+"F0.wireOp",EDGE,"E1125"),sQuery(id+"F0.wireOp",EDGE,"E1126"),sQuery(id+"F0.wireOp",EDGE,"E1127"),sQuery(id+"F0.wireOp",EDGE,"E1128"),sQuery(id+"F0.wireOp",EDGE,"E1129"),sQuery(id+"F0.wireOp",EDGE,"E1130"),sQuery(id+"F0.wireOp",EDGE,"E1131"),sQuery(id+"F0.wireOp",EDGE,"E1132"),sQuery(id+"F0.wireOp",EDGE,"E1133"),sQuery(id+"F0.wireOp",EDGE,"E1134"),sQuery(id+"F0.wireOp",EDGE,"E1135"),sQuery(id+"F0.wireOp",EDGE,"E1136"),sQuery(id+"F0.wireOp",EDGE,"E1137"),sQuery(id+"F0.wireOp",EDGE,"E1138"),sQuery(id+"F0.wireOp",EDGE,"E1139"),sQuery(id+"F0.wireOp",EDGE,"E1140"),sQuery(id+"F0.wireOp",EDGE,"E1141"),sQuery(id+"F0.wireOp",EDGE,"E1142"),sQuery(id+"F0.wireOp",EDGE,"E1143"),sQuery(id+"F0.wireOp",EDGE,"E1144"),sQuery(id+"F0.wireOp",EDGE,"E1145"),sQuery(id+"F0.wireOp",EDGE,"E1146"),sQuery(id+"F0.wireOp",EDGE,"E1147"),sQuery(id+"F0.wireOp",EDGE,"E1148"),sQuery(id+"F0.wireOp",EDGE,"E1149"),sQuery(id+"F0.wireOp",EDGE,"E1150"),sQuery(id+"F0.wireOp",EDGE,"E1151"),sQuery(id+"F0.wireOp",EDGE,"E1152"),sQuery(id+"F0.wireOp",EDGE,"E1153"),sQuery(id+"F0.wireOp",EDGE,"E1154"),sQuery(id+"F0.wireOp",EDGE,"E1155"),sQuery(id+"F0.wireOp",EDGE,"E1156"),sQuery(id+"F0.wireOp",EDGE,"E1157"),sQuery(id+"F0.wireOp",EDGE,"E1158"),sQuery(id+"F0.wireOp",EDGE,"E1159"),sQuery(id+"F0.wireOp",EDGE,"E1160"),sQuery(id+"F0.wireOp",EDGE,"E1161"),sQuery(id+"F0.wireOp",EDGE,"E1162"),sQuery(id+"F0.wireOp",EDGE,"E1163"),sQuery(id+"F0.wireOp",EDGE,"E1164"),sQuery(id+"F0.wireOp",EDGE,"E1165"),sQuery(id+"F0.wireOp",EDGE,"E1166"),sQuery(id+"F0.wireOp",EDGE,"E1167"),sQuery(id+"F0.wireOp",EDGE,"E1168"),sQuery(id+"F0.wireOp",EDGE,"E1169"),sQuery(id+"F0.wireOp",EDGE,"E1170"),sQuery(id+"F0.wireOp",EDGE,"E1171"),sQuery(id+"F0.wireOp",EDGE,"E1172"),sQuery(id+"F0.wireOp",EDGE,"E1173"),sQuery(id+"F0.wireOp",EDGE,"E1174"),sQuery(id+"F0.wireOp",EDGE,"E1175"),sQuery(id+"F0.wireOp",EDGE,"E1176"),sQuery(id+"F0.wireOp",EDGE,"E1177"),sQuery(id+"F0.wireOp",EDGE,"E1178"),sQuery(id+"F0.wireOp",EDGE,"E1179"),sQuery(id+"F0.wireOp",EDGE,"E1180"),sQuery(id+"F0.wireOp",EDGE,"E1181"),sQuery(id+"F0.wireOp",EDGE,"E1182"),sQuery(id+"F0.wireOp",EDGE,"E1183"),sQuery(id+"F0.wireOp",EDGE,"E1184"),sQuery(id+"F0.wireOp",EDGE,"E1185"),sQuery(id+"F0.wireOp",EDGE,"E1186"),sQuery(id+"F0.wireOp",EDGE,"E1187"),sQuery(id+"F0.wireOp",EDGE,"E1188"),sQuery(id+"F0.wireOp",EDGE,"E1189"),sQuery(id+"F0.wireOp",EDGE,"E1190"),sQuery(id+"F0.wireOp",EDGE,"E1191"),sQuery(id+"F0.wireOp",EDGE,"E1192"),sQuery(id+"F0.wireOp",EDGE,"E1193"),sQuery(id+"F0.wireOp",EDGE,"E1194"),sQuery(id+"F0.wireOp",EDGE,"E1195"),sQuery(id+"F0.wireOp",EDGE,"E1196"),sQuery(id+"F0.wireOp",EDGE,"E1197"),sQuery(id+"F0.wireOp",EDGE,"E1198"),sQuery(id+"F0.wireOp",EDGE,"E1199"),sQuery(id+"F0.wireOp",EDGE,"E1200"),sQuery(id+"F0.wireOp",EDGE,"E1201"),sQuery(id+"F0.wireOp",EDGE,"E1202"),sQuery(id+"F0.wireOp",EDGE,"E1203"),sQuery(id+"F0.wireOp",EDGE,"E1204"),sQuery(id+"F0.wireOp",EDGE,"E1205"),sQuery(id+"F0.wireOp",EDGE,"E1206"),sQuery(id+"F0.wireOp",EDGE,"E1207"),sQuery(id+"F0.wireOp",EDGE,"E1208"),sQuery(id+"F0.wireOp",EDGE,"E1209"),sQuery(id+"F0.wireOp",EDGE,"E1210"),sQuery(id+"F0.wireOp",EDGE,"E1211"),sQuery(id+"F0.wireOp",EDGE,"E1212"),sQuery(id+"F0.wireOp",EDGE,"E1213"),sQuery(id+"F0.wireOp",EDGE,"E1214"),sQuery(id+"F0.wireOp",EDGE,"E1215"),sQuery(id+"F0.wireOp",EDGE,"E1216"),sQuery(id+"F0.wireOp",EDGE,"E1217"),sQuery(id+"F0.wireOp",EDGE,"E1218"),sQuery(id+"F0.wireOp",EDGE,"E1219"),sQuery(id+"F0.wireOp",EDGE,"E1220"),sQuery(id+"F0.wireOp",EDGE,"E1221"),sQuery(id+"F0.wireOp",EDGE,"E1222"),sQuery(id+"F0.wireOp",EDGE,"E1223"),sQuery(id+"F0.wireOp",EDGE,"E1224"),sQuery(id+"F0.wireOp",EDGE,"E1225"),sQuery(id+"F0.wireOp",EDGE,"E1226"),sQuery(id+"F0.wireOp",EDGE,"E1227"),sQuery(id+"F0.wireOp",EDGE,"E1228"),sQuery(id+"F0.wireOp",EDGE,"E1229"),sQuery(id+"F0.wireOp",EDGE,"E1230"),sQuery(id+"F0.wireOp",EDGE,"E1231"),sQuery(id+"F0.wireOp",EDGE,"E1232"),sQuery(id+"F0.wireOp",EDGE,"E1233"),sQuery(id+"F0.wireOp",EDGE,"E1234"),sQuery(id+"F0.wireOp",EDGE,"E1235"),sQuery(id+"F0.wireOp",EDGE,"E1236"),sQuery(id+"F0.wireOp",EDGE,"E1237"),sQuery(id+"F0.wireOp",EDGE,"E1238"),sQuery(id+"F0.wireOp",EDGE,"E1239"),sQuery(id+"F0.wireOp",EDGE,"E1240"),sQuery(id+"F0.wireOp",EDGE,"E1241"),sQuery(id+"F0.wireOp",EDGE,"E1242"),sQuery(id+"F0.wireOp",EDGE,"E1243"),sQuery(id+"F0.wireOp",EDGE,"E1244"),sQuery(id+"F0.wireOp",EDGE,"E1245"),sQuery(id+"F0.wireOp",EDGE,"E1246"),sQuery(id+"F0.wireOp",EDGE,"E1247"),sQuery(id+"F0.wireOp",EDGE,"E1248"),sQuery(id+"F0.wireOp",EDGE,"E1249"),sQuery(id+"F0.wireOp",EDGE,"E1250"),sQuery(id+"F0.wireOp",EDGE,"E1251"),sQuery(id+"F0.wireOp",EDGE,"E1252"),sQuery(id+"F0.wireOp",EDGE,"E1253"),sQuery(id+"F0.wireOp",EDGE,"E1254"),sQuery(id+"F0.wireOp",EDGE,"E1255"),sQuery(id+"F0.wireOp",EDGE,"E1256"),sQuery(id+"F0.wireOp",EDGE,"E1257"),sQuery(id+"F0.wireOp",EDGE,"E1258"),sQuery(id+"F0.wireOp",EDGE,"E1259"),sQuery(id+"F0.wireOp",EDGE,"E1260"),sQuery(id+"F0.wireOp",EDGE,"E1261"),sQuery(id+"F0.wireOp",EDGE,"E1262"),sQuery(id+"F0.wireOp",EDGE,"E1263"),sQuery(id+"F0.wireOp",EDGE,"E1264"),sQuery(id+"F0.wireOp",EDGE,"E1265"),sQuery(id+"F0.wireOp",EDGE,"E1266"),sQuery(id+"F0.wireOp",EDGE,"E1267"),sQuery(id+"F0.wireOp",EDGE,"E1268"),sQuery(id+"F0.wireOp",EDGE,"E1269"),sQuery(id+"F0.wireOp",EDGE,"E1270"),sQuery(id+"F0.wireOp",EDGE,"E1271"),sQuery(id+"F0.wireOp",EDGE,"E1272"),sQuery(id+"F0.wireOp",EDGE,"E1273"),sQuery(id+"F0.wireOp",EDGE,"E1274"),sQuery(id+"F0.wireOp",EDGE,"E1275"),sQuery(id+"F0.wireOp",EDGE,"E1276"),sQuery(id+"F0.wireOp",EDGE,"E1277"),sQuery(id+"F0.wireOp",EDGE,"E1278"),sQuery(id+"F0.wireOp",EDGE,"E1279"),sQuery(id+"F0.wireOp",EDGE,"E1280"),sQuery(id+"F0.wireOp",EDGE,"E1281"),sQuery(id+"F0.wireOp",EDGE,"E1282"),sQuery(id+"F0.wireOp",EDGE,"E1283"),sQuery(id+"F0.wireOp",EDGE,"E1284"),sQuery(id+"F0.wireOp",EDGE,"E1285"),sQuery(id+"F0.wireOp",EDGE,"E1286"),sQuery(id+"F0.wireOp",EDGE,"E1287"),sQuery(id+"F0.wireOp",EDGE,"E1288"),sQuery(id+"F0.wireOp",EDGE,"E1289"),sQuery(id+"F0.wireOp",EDGE,"E1290"),sQuery(id+"F0.wireOp",EDGE,"E1291"),sQuery(id+"F0.wireOp",EDGE,"E1292"),sQuery(id+"F0.wireOp",EDGE,"E1293"),sQuery(id+"F0.wireOp",EDGE,"E1294"),sQuery(id+"F0.wireOp",EDGE,"E1295"),sQuery(id+"F0.wireOp",EDGE,"E1296"),sQuery(id+"F0.wireOp",EDGE,"E1297"),sQuery(id+"F0.wireOp",EDGE,"E1298"),sQuery(id+"F0.wireOp",EDGE,"E1299"),sQuery(id+"F0.wireOp",EDGE,"E1300"),sQuery(id+"F0.wireOp",EDGE,"E1301"),sQuery(id+"F0.wireOp",EDGE,"E1302"),sQuery(id+"F0.wireOp",EDGE,"E1303"),sQuery(id+"F0.wireOp",EDGE,"E1304"),sQuery(id+"F0.wireOp",EDGE,"E1305"),sQuery(id+"F0.wireOp",EDGE,"E1306"),sQuery(id+"F0.wireOp",EDGE,"E1307"),sQuery(id+"F0.wireOp",EDGE,"E1308"),sQuery(id+"F0.wireOp",EDGE,"E1309"),sQuery(id+"F0.wireOp",EDGE,"E1310"),sQuery(id+"F0.wireOp",EDGE,"E1311"),sQuery(id+"F0.wireOp",EDGE,"E1312"),sQuery(id+"F0.wireOp",EDGE,"E1313"),sQuery(id+"F0.wireOp",EDGE,"E1314"),sQuery(id+"F0.wireOp",EDGE,"E1315"),sQuery(id+"F0.wireOp",EDGE,"E1316"),sQuery(id+"F0.wireOp",EDGE,"E1317"),sQuery(id+"F0.wireOp",EDGE,"E1318"),sQuery(id+"F0.wireOp",EDGE,"E1319"),sQuery(id+"F0.wireOp",EDGE,"E1320"),sQuery(id+"F0.wireOp",EDGE,"E1321"),sQuery(id+"F0.wireOp",EDGE,"E1322"),sQuery(id+"F0.wireOp",EDGE,"E1323"),sQuery(id+"F0.wireOp",EDGE,"E1324"),sQuery(id+"F0.wireOp",EDGE,"E1325"),sQuery(id+"F0.wireOp",EDGE,"E1326"),sQuery(id+"F0.wireOp",EDGE,"E1327"),sQuery(id+"F0.wireOp",EDGE,"E1328"),sQuery(id+"F0.wireOp",EDGE,"E1329"),sQuery(id+"F0.wireOp",EDGE,"E1330"),sQuery(id+"F0.wireOp",EDGE,"E1331"),sQuery(id+"F0.wireOp",EDGE,"E1332"),sQuery(id+"F0.wireOp",EDGE,"E1333"),sQuery(id+"F0.wireOp",EDGE,"E1334"),sQuery(id+"F0.wireOp",EDGE,"E1335"),sQuery(id+"F0.wireOp",EDGE,"E1336"),sQuery(id+"F0.wireOp",EDGE,"E1337"),sQuery(id+"F0.wireOp",EDGE,"E1338"),sQuery(id+"F0.wireOp",EDGE,"E1339"),sQuery(id+"F0.wireOp",EDGE,"E1340"),sQuery(id+"F0.wireOp",EDGE,"E1341"),sQuery(id+"F0.wireOp",EDGE,"E1342"),sQuery(id+"F0.wireOp",EDGE,"E1343"),sQuery(id+"F0.wireOp",EDGE,"E1344"),sQuery(id+"F0.wireOp",EDGE,"E1345"),sQuery(id+"F0.wireOp",EDGE,"E1346"),sQuery(id+"F0.wireOp",EDGE,"E1347"),sQuery(id+"F0.wireOp",EDGE,"E1348"),sQuery(id+"F0.wireOp",EDGE,"E1349"),sQuery(id+"F0.wireOp",EDGE,"E1350"),sQuery(id+"F0.wireOp",EDGE,"E1351"),sQuery(id+"F0.wireOp",EDGE,"E1352"),sQuery(id+"F0.wireOp",EDGE,"E1353"),sQuery(id+"F0.wireOp",EDGE,"E1354"),sQuery(id+"F0.wireOp",EDGE,"E1355"),sQuery(id+"F0.wireOp",EDGE,"E1356"),sQuery(id+"F0.wireOp",EDGE,"E1357"),sQuery(id+"F0.wireOp",EDGE,"E1358"),sQuery(id+"F0.wireOp",EDGE,"E1359"),sQuery(id+"F0.wireOp",EDGE,"E1360"),sQuery(id+"F0.wireOp",EDGE,"E1361"),sQuery(id+"F0.wireOp",EDGE,"E1362"),sQuery(id+"F0.wireOp",EDGE,"E1363"),sQuery(id+"F0.wireOp",EDGE,"E1364"),sQuery(id+"F0.wireOp",EDGE,"E1365"),sQuery(id+"F0.wireOp",EDGE,"E1366"),sQuery(id+"F0.wireOp",EDGE,"E1367"),sQuery(id+"F0.wireOp",EDGE,"E1368"),sQuery(id+"F0.wireOp",EDGE,"E1369"),sQuery(id+"F0.wireOp",EDGE,"E1370"),sQuery(id+"F0.wireOp",EDGE,"E1371"),sQuery(id+"F0.wireOp",EDGE,"E1372"),sQuery(id+"F0.wireOp",EDGE,"E1373"),sQuery(id+"F0.wireOp",EDGE,"E1374"),sQuery(id+"F0.wireOp",EDGE,"E1375"),sQuery(id+"F0.wireOp",EDGE,"E1376"),sQuery(id+"F0.wireOp",EDGE,"E1377"),sQuery(id+"F0.wireOp",EDGE,"E1378"),sQuery(id+"F0.wireOp",EDGE,"E1379"),sQuery(id+"F0.wireOp",EDGE,"E1380"),sQuery(id+"F0.wireOp",EDGE,"E1381"),sQuery(id+"F0.wireOp",EDGE,"E1382"),sQuery(id+"F0.wireOp",EDGE,"E1383"),sQuery(id+"F0.wireOp",EDGE,"E1384"),sQuery(id+"F0.wireOp",EDGE,"E1385"),sQuery(id+"F0.wireOp",EDGE,"E1386"),sQuery(id+"F0.wireOp",EDGE,"E1387"),sQuery(id+"F0.wireOp",EDGE,"E1388"),sQuery(id+"F0.wireOp",EDGE,"E1389"),sQuery(id+"F0.wireOp",EDGE,"E1390"),sQuery(id+"F0.wireOp",EDGE,"E1391"),sQuery(id+"F0.wireOp",EDGE,"E1392"),sQuery(id+"F0.wireOp",EDGE,"E1393"),sQuery(id+"F0.wireOp",EDGE,"E1394"),sQuery(id+"F0.wireOp",EDGE,"E1395"),sQuery(id+"F0.wireOp",EDGE,"E1396"),sQuery(id+"F0.wireOp",EDGE,"E1397"),sQuery(id+"F0.wireOp",EDGE,"E1398"),sQuery(id+"F0.wireOp",EDGE,"E1399"),sQuery(id+"F0.wireOp",EDGE,"E1400"),sQuery(id+"F0.wireOp",EDGE,"E1401"),sQuery(id+"F0.wireOp",EDGE,"E1402"),sQuery(id+"F0.wireOp",EDGE,"E1403"),sQuery(id+"F0.wireOp",EDGE,"E1404"),sQuery(id+"F0.wireOp",EDGE,"E1405"),sQuery(id+"F0.wireOp",EDGE,"E1406"),sQuery(id+"F0.wireOp",EDGE,"E1407"),sQuery(id+"F0.wireOp",EDGE,"E1408"),sQuery(id+"F0.wireOp",EDGE,"E1409"),sQuery(id+"F0.wireOp",EDGE,"E1410"),sQuery(id+"F0.wireOp",EDGE,"E1411"),sQuery(id+"F0.wireOp",EDGE,"E1412"),sQuery(id+"F0.wireOp",EDGE,"E1413"),sQuery(id+"F0.wireOp",EDGE,"E1414"),sQuery(id+"F0.wireOp",EDGE,"E1415"),sQuery(id+"F0.wireOp",EDGE,"E1416"),sQuery(id+"F0.wireOp",EDGE,"E1417"),sQuery(id+"F0.wireOp",EDGE,"E1418"),sQuery(id+"F0.wireOp",EDGE,"E1419"),sQuery(id+"F0.wireOp",EDGE,"E1420"),sQuery(id+"F0.wireOp",EDGE,"E1421"),sQuery(id+"F0.wireOp",EDGE,"E1422"),sQuery(id+"F0.wireOp",EDGE,"E1423"),sQuery(id+"F0.wireOp",EDGE,"E1424"),sQuery(id+"F0.wireOp",EDGE,"E1425"),sQuery(id+"F0.wireOp",EDGE,"E1426"),sQuery(id+"F0.wireOp",EDGE,"E1427"),sQuery(id+"F0.wireOp",EDGE,"E1428"),sQuery(id+"F0.wireOp",EDGE,"E1429"),sQuery(id+"F0.wireOp",EDGE,"E1430"),sQuery(id+"F0.wireOp",EDGE,"E1431"),sQuery(id+"F0.wireOp",EDGE,"E1432"),sQuery(id+"F0.wireOp",EDGE,"E1433"),sQuery(id+"F0.wireOp",EDGE,"E1434"),sQuery(id+"F0.wireOp",EDGE,"E1435"),sQuery(id+"F0.wireOp",EDGE,"E1436"),sQuery(id+"F0.wireOp",EDGE,"E1437"),sQuery(id+"F0.wireOp",EDGE,"E1438"),sQuery(id+"F0.wireOp",EDGE,"E1439"),sQuery(id+"F0.wireOp",EDGE,"E1440"),sQuery(id+"F0.wireOp",EDGE,"E1441"),sQuery(id+"F0.wireOp",EDGE,"E1442"),sQuery(id+"F0.wireOp",EDGE,"E1443"),sQuery(id+"F0.wireOp",EDGE,"E1444"),sQuery(id+"F0.wireOp",EDGE,"E1445"),sQuery(id+"F0.wireOp",EDGE,"E1446"),sQuery(id+"F0.wireOp",EDGE,"E1447"),sQuery(id+"F0.wireOp",EDGE,"E1448"),sQuery(id+"F0.wireOp",EDGE,"E1449"),sQuery(id+"F0.wireOp",EDGE,"E1450"),sQuery(id+"F0.wireOp",EDGE,"E1451"),sQuery(id+"F0.wireOp",EDGE,"E1452"),sQuery(id+"F0.wireOp",EDGE,"E1453"),sQuery(id+"F0.wireOp",EDGE,"E1454"),sQuery(id+"F0.wireOp",EDGE,"E1455"),sQuery(id+"F0.wireOp",EDGE,"E1456"),sQuery(id+"F0.wireOp",EDGE,"E1457"),sQuery(id+"F0.wireOp",EDGE,"E1458"),sQuery(id+"F0.wireOp",EDGE,"E1459"),sQuery(id+"F0.wireOp",EDGE,"E1460"),sQuery(id+"F0.wireOp",EDGE,"E1461"),sQuery(id+"F0.wireOp",EDGE,"E1462"),sQuery(id+"F0.wireOp",EDGE,"E1463"),sQuery(id+"F0.wireOp",EDGE,"E1464"),sQuery(id+"F0.wireOp",EDGE,"E1465"),sQuery(id+"F0.wireOp",EDGE,"E1466"),sQuery(id+"F0.wireOp",EDGE,"E1467"),sQuery(id+"F0.wireOp",EDGE,"E1468"),sQuery(id+"F0.wireOp",EDGE,"E1469"),sQuery(id+"F0.wireOp",EDGE,"E1470"),sQuery(id+"F0.wireOp",EDGE,"E1471"),sQuery(id+"F0.wireOp",EDGE,"E1472"),sQuery(id+"F0.wireOp",EDGE,"E1473"),sQuery(id+"F0.wireOp",EDGE,"E1474"),sQuery(id+"F0.wireOp",EDGE,"E1475"),sQuery(id+"F0.wireOp",EDGE,"E1476"),sQuery(id+"F0.wireOp",EDGE,"E1477"),sQuery(id+"F0.wireOp",EDGE,"E1478"),sQuery(id+"F0.wireOp",EDGE,"E1479"),sQuery(id+"F0.wireOp",EDGE,"E1480"),sQuery(id+"F0.wireOp",EDGE,"E1481"),sQuery(id+"F0.wireOp",EDGE,"E1482"),sQuery(id+"F0.wireOp",EDGE,"E1483"),sQuery(id+"F0.wireOp",EDGE,"E1484"),sQuery(id+"F0.wireOp",EDGE,"E1485"),sQuery(id+"F0.wireOp",EDGE,"E1486"),sQuery(id+"F0.wireOp",EDGE,"E1487"),sQuery(id+"F0.wireOp",EDGE,"E1488"),sQuery(id+"F0.wireOp",EDGE,"E1489"),sQuery(id+"F0.wireOp",EDGE,"E1490"),sQuery(id+"F0.wireOp",EDGE,"E1491"),sQuery(id+"F0.wireOp",EDGE,"E1492"),sQuery(id+"F0.wireOp",EDGE,"E1493"),sQuery(id+"F0.wireOp",EDGE,"E1494"),sQuery(id+"F0.wireOp",EDGE,"E1495"),sQuery(id+"F0.wireOp",EDGE,"E1496"),sQuery(id+"F0.wireOp",EDGE,"E1497"),sQuery(id+"F0.wireOp",EDGE,"E1498"),sQuery(id+"F0.wireOp",EDGE,"E1499"),sQuery(id+"F0.wireOp",EDGE,"E1500"),sQuery(id+"F0.wireOp",EDGE,"E1501"),sQuery(id+"F0.wireOp",EDGE,"E1502"),sQuery(id+"F0.wireOp",EDGE,"E1503"),sQuery(id+"F0.wireOp",EDGE,"E1504"),sQuery(id+"F0.wireOp",EDGE,"E1505"),sQuery(id+"F0.wireOp",EDGE,"E1506"),sQuery(id+"F0.wireOp",EDGE,"E1507"),sQuery(id+"F0.wireOp",EDGE,"E1508"),sQuery(id+"F0.wireOp",EDGE,"E1509"),sQuery(id+"F0.wireOp",EDGE,"E1510"),sQuery(id+"F0.wireOp",EDGE,"E1511"),sQuery(id+"F0.wireOp",EDGE,"E1512"),sQuery(id+"F0.wireOp",EDGE,"E1513"),sQuery(id+"F0.wireOp",EDGE,"E1514"),sQuery(id+"F0.wireOp",EDGE,"E1515"),sQuery(id+"F0.wireOp",EDGE,"E1516"),sQuery(id+"F0.wireOp",EDGE,"E1517"),sQuery(id+"F0.wireOp",EDGE,"E1518"),sQuery(id+"F0.wireOp",EDGE,"E1519"),sQuery(id+"F0.wireOp",EDGE,"E1520"),sQuery(id+"F0.wireOp",EDGE,"E1521"),sQuery(id+"F0.wireOp",EDGE,"E1522"),sQuery(id+"F0.wireOp",EDGE,"E1523"),sQuery(id+"F0.wireOp",EDGE,"E1524"),sQuery(id+"F0.wireOp",EDGE,"E1525"),sQuery(id+"F0.wireOp",EDGE,"E1526"),sQuery(id+"F0.wireOp",EDGE,"E1527"),sQuery(id+"F0.wireOp",EDGE,"E1528"),sQuery(id+"F0.wireOp",EDGE,"E1529"),sQuery(id+"F0.wireOp",EDGE,"E1530"),sQuery(id+"F0.wireOp",EDGE,"E1531"),sQuery(id+"F0.wireOp",EDGE,"E1532"),sQuery(id+"F0.wireOp",EDGE,"E1533"),sQuery(id+"F0.wireOp",EDGE,"E1534"),sQuery(id+"F0.wireOp",EDGE,"E1535"),sQuery(id+"F0.wireOp",EDGE,"E1536"),sQuery(id+"F0.wireOp",EDGE,"E1537"),sQuery(id+"F0.wireOp",EDGE,"E1538"),sQuery(id+"F0.wireOp",EDGE,"E1539"),sQuery(id+"F0.wireOp",EDGE,"E1540"),sQuery(id+"F0.wireOp",EDGE,"E1541"),sQuery(id+"F0.wireOp",EDGE,"E1542"),sQuery(id+"F0.wireOp",EDGE,"E1543"),sQuery(id+"F0.wireOp",EDGE,"E1544"),sQuery(id+"F0.wireOp",EDGE,"E1545"),sQuery(id+"F0.wireOp",EDGE,"E1546"),sQuery(id+"F0.wireOp",EDGE,"E1547"),sQuery(id+"F0.wireOp",EDGE,"E1548"),sQuery(id+"F0.wireOp",EDGE,"E1549"),sQuery(id+"F0.wireOp",EDGE,"E1550"),sQuery(id+"F0.wireOp",EDGE,"E1551"),sQuery(id+"F0.wireOp",EDGE,"E1552"),sQuery(id+"F0.wireOp",EDGE,"E1553"),sQuery(id+"F0.wireOp",EDGE,"E1554"),sQuery(id+"F0.wireOp",EDGE,"E1555"),sQuery(id+"F0.wireOp",EDGE,"E1556"),sQuery(id+"F0.wireOp",EDGE,"E1557"),sQuery(id+"F0.wireOp",EDGE,"E1558"),sQuery(id+"F0.wireOp",EDGE,"E1559"),sQuery(id+"F0.wireOp",EDGE,"E1560"),sQuery(id+"F0.wireOp",EDGE,"E1561"),sQuery(id+"F0.wireOp",EDGE,"E1562"),sQuery(id+"F0.wireOp",EDGE,"E1563"),sQuery(id+"F0.wireOp",EDGE,"E1564"),sQuery(id+"F0.wireOp",EDGE,"E1565"),sQuery(id+"F0.wireOp",EDGE,"E1566"),sQuery(id+"F0.wireOp",EDGE,"E1567"),sQuery(id+"F0.wireOp",EDGE,"E1568"),sQuery(id+"F0.wireOp",EDGE,"E1569"),sQuery(id+"F0.wireOp",EDGE,"E1570"),sQuery(id+"F0.wireOp",EDGE,"E1571"),sQuery(id+"F0.wireOp",EDGE,"E1572"),sQuery(id+"F0.wireOp",EDGE,"E1573"),sQuery(id+"F0.wireOp",EDGE,"E1574"),sQuery(id+"F0.wireOp",EDGE,"E1575"),sQuery(id+"F0.wireOp",EDGE,"E1576"),sQuery(id+"F0.wireOp",EDGE,"E1577"),sQuery(id+"F0.wireOp",EDGE,"E1578"),sQuery(id+"F0.wireOp",EDGE,"E1579"),sQuery(id+"F0.wireOp",EDGE,"E1580"),sQuery(id+"F0.wireOp",EDGE,"E1581"),sQuery(id+"F0.wireOp",EDGE,"E1582"),sQuery(id+"F0.wireOp",EDGE,"E1583"),sQuery(id+"F0.wireOp",EDGE,"E1584"),sQuery(id+"F0.wireOp",EDGE,"E1585"),sQuery(id+"F0.wireOp",EDGE,"E1586"),sQuery(id+"F0.wireOp",EDGE,"E1587"),sQuery(id+"F0.wireOp",EDGE,"E1588"),sQuery(id+"F0.wireOp",EDGE,"E1589"),sQuery(id+"F0.wireOp",EDGE,"E1590"),sQuery(id+"F0.wireOp",EDGE,"E1591"),sQuery(id+"F0.wireOp",EDGE,"E1592"),sQuery(id+"F0.wireOp",EDGE,"E1593"),sQuery(id+"F0.wireOp",EDGE,"E1594"),sQuery(id+"F0.wireOp",EDGE,"E1595"),sQuery(id+"F0.wireOp",EDGE,"E1596"),sQuery(id+"F0.wireOp",EDGE,"E1597"),sQuery(id+"F0.wireOp",EDGE,"E1598"),sQuery(id+"F0.wireOp",EDGE,"E1599"),sQuery(id+"F0.wireOp",EDGE,"E1600"),sQuery(id+"F0.wireOp",EDGE,"E1601"),sQuery(id+"F0.wireOp",EDGE,"E1602"),sQuery(id+"F0.wireOp",EDGE,"E1603"),sQuery(id+"F0.wireOp",EDGE,"E1604"),sQuery(id+"F0.wireOp",EDGE,"E1605"),sQuery(id+"F0.wireOp",EDGE,"E1606"),sQuery(id+"F0.wireOp",EDGE,"E1607"),sQuery(id+"F0.wireOp",EDGE,"E1608"),sQuery(id+"F0.wireOp",EDGE,"E1609"),sQuery(id+"F0.wireOp",EDGE,"E1610"),sQuery(id+"F0.wireOp",EDGE,"E1611"),sQuery(id+"F0.wireOp",EDGE,"E1612"),sQuery(id+"F0.wireOp",EDGE,"E1613"),sQuery(id+"F0.wireOp",EDGE,"E1614"),sQuery(id+"F0.wireOp",EDGE,"E1615"),sQuery(id+"F0.wireOp",EDGE,"E1616"),sQuery(id+"F0.wireOp",EDGE,"E1617"),sQuery(id+"F0.wireOp",EDGE,"E1618"),sQuery(id+"F0.wireOp",EDGE,"E1619"),sQuery(id+"F0.wireOp",EDGE,"E1620"),sQuery(id+"F0.wireOp",EDGE,"E1621"),sQuery(id+"F0.wireOp",EDGE,"E1622"),sQuery(id+"F0.wireOp",EDGE,"E1623"),sQuery(id+"F0.wireOp",EDGE,"E1624"),sQuery(id+"F0.wireOp",EDGE,"E1625"),sQuery(id+"F0.wireOp",EDGE,"E1626"),sQuery(id+"F0.wireOp",EDGE,"E1627"),sQuery(id+"F0.wireOp",EDGE,"E1628"),sQuery(id+"F0.wireOp",EDGE,"E1629"),sQuery(id+"F0.wireOp",EDGE,"E1630"),sQuery(id+"F0.wireOp",EDGE,"E1631"),sQuery(id+"F0.wireOp",EDGE,"E1632"),sQuery(id+"F0.wireOp",EDGE,"E1633"),sQuery(id+"F0.wireOp",EDGE,"E1634"),sQuery(id+"F0.wireOp",EDGE,"E1635"),sQuery(id+"F0.wireOp",EDGE,"E1636"),sQuery(id+"F0.wireOp",EDGE,"E1637"),sQuery(id+"F0.wireOp",EDGE,"E1638"),sQuery(id+"F0.wireOp",EDGE,"E1639"),sQuery(id+"F0.wireOp",EDGE,"E1640"),sQuery(id+"F0.wireOp",EDGE,"E1641"),sQuery(id+"F0.wireOp",EDGE,"E1642"),sQuery(id+"F0.wireOp",EDGE,"E1643"),sQuery(id+"F0.wireOp",EDGE,"E1644"),sQuery(id+"F0.wireOp",EDGE,"E1645"),sQuery(id+"F0.wireOp",EDGE,"E1646"),sQuery(id+"F0.wireOp",EDGE,"E1647"),sQuery(id+"F0.wireOp",EDGE,"E1648"),sQuery(id+"F0.wireOp",EDGE,"E1649"),sQuery(id+"F0.wireOp",EDGE,"E1650"),sQuery(id+"F0.wireOp",EDGE,"E1651"),sQuery(id+"F0.wireOp",EDGE,"E1652"),sQuery(id+"F0.wireOp",EDGE,"E1653"),sQuery(id+"F0.wireOp",EDGE,"E1654"),sQuery(id+"F0.wireOp",EDGE,"E1655"),sQuery(id+"F0.wireOp",EDGE,"E1656"),sQuery(id+"F0.wireOp",EDGE,"E1657"),sQuery(id+"F0.wireOp",EDGE,"E1658"),sQuery(id+"F0.wireOp",EDGE,"E1659"),sQuery(id+"F0.wireOp",EDGE,"E1660"),sQuery(id+"F0.wireOp",EDGE,"E1661"),sQuery(id+"F0.wireOp",EDGE,"E1662"),sQuery(id+"F0.wireOp",EDGE,"E1663"),sQuery(id+"F0.wireOp",EDGE,"E1664"),sQuery(id+"F0.wireOp",EDGE,"E1665"),sQuery(id+"F0.wireOp",EDGE,"E1666"),sQuery(id+"F0.wireOp",EDGE,"E1667"),sQuery(id+"F0.wireOp",EDGE,"E1668"),sQuery(id+"F0.wireOp",EDGE,"E1669"),sQuery(id+"F0.wireOp",EDGE,"E1670"),sQuery(id+"F0.wireOp",EDGE,"E1671"),sQuery(id+"F0.wireOp",EDGE,"E1672"),sQuery(id+"F0.wireOp",EDGE,"E1673"),sQuery(id+"F0.wireOp",EDGE,"E1674"),sQuery(id+"F0.wireOp",EDGE,"E1675"),sQuery(id+"F0.wireOp",EDGE,"E1676"),sQuery(id+"F0.wireOp",EDGE,"E1677"),sQuery(id+"F0.wireOp",EDGE,"E1678"),sQuery(id+"F0.wireOp",EDGE,"E1679"),sQuery(id+"F0.wireOp",EDGE,"E1680"),sQuery(id+"F0.wireOp",EDGE,"E1681"),sQuery(id+"F0.wireOp",EDGE,"E1682"),sQuery(id+"F0.wireOp",EDGE,"E1683"),sQuery(id+"F0.wireOp",EDGE,"E1684"),sQuery(id+"F0.wireOp",EDGE,"E1685"),sQuery(id+"F0.wireOp",EDGE,"E1686"),sQuery(id+"F0.wireOp",EDGE,"E1687"),sQuery(id+"F0.wireOp",EDGE,"E1688"),sQuery(id+"F0.wireOp",EDGE,"E1689"),sQuery(id+"F0.wireOp",EDGE,"E1690"),sQuery(id+"F0.wireOp",EDGE,"E1691"),sQuery(id+"F0.wireOp",EDGE,"E1692"),sQuery(id+"F0.wireOp",EDGE,"E1693"),sQuery(id+"F0.wireOp",EDGE,"E1694"),sQuery(id+"F0.wireOp",EDGE,"E1695"),sQuery(id+"F0.wireOp",EDGE,"E1696"),sQuery(id+"F0.wireOp",EDGE,"E1697"),sQuery(id+"F0.wireOp",EDGE,"E1698"),sQuery(id+"F0.wireOp",EDGE,"E1699"),sQuery(id+"F0.wireOp",EDGE,"E1700"),sQuery(id+"F0.wireOp",EDGE,"E1701"),sQuery(id+"F0.wireOp",EDGE,"E1702"),sQuery(id+"F0.wireOp",EDGE,"E1703"),sQuery(id+"F0.wireOp",EDGE,"E1704"),sQuery(id+"F0.wireOp",EDGE,"E1705"),sQuery(id+"F0.wireOp",EDGE,"E1706"),sQuery(id+"F0.wireOp",EDGE,"E1707"),sQuery(id+"F0.wireOp",EDGE,"E1708"),sQuery(id+"F0.wireOp",EDGE,"E1709"),sQuery(id+"F0.wireOp",EDGE,"E1710"),sQuery(id+"F0.wireOp",EDGE,"E1711"),sQuery(id+"F0.wireOp",EDGE,"E1712"),sQuery(id+"F0.wireOp",EDGE,"E1713"),sQuery(id+"F0.wireOp",EDGE,"E1714"),sQuery(id+"F0.wireOp",EDGE,"E1715"),sQuery(id+"F0.wireOp",EDGE,"E1716"),sQuery(id+"F0.wireOp",EDGE,"E1717"),sQuery(id+"F0.wireOp",EDGE,"E1718"),sQuery(id+"F0.wireOp",EDGE,"E1719"),sQuery(id+"F0.wireOp",EDGE,"E1720"),sQuery(id+"F0.wireOp",EDGE,"E1721"),sQuery(id+"F0.wireOp",EDGE,"E1722"),sQuery(id+"F0.wireOp",EDGE,"E1723"),sQuery(id+"F0.wireOp",EDGE,"E1724"),sQuery(id+"F0.wireOp",EDGE,"E1725"),sQuery(id+"F0.wireOp",EDGE,"E1726"),sQuery(id+"F0.wireOp",EDGE,"E1727"),sQuery(id+"F0.wireOp",EDGE,"E1728"),sQuery(id+"F0.wireOp",EDGE,"E1729"),sQuery(id+"F0.wireOp",EDGE,"E1730"),sQuery(id+"F0.wireOp",EDGE,"E1731"),sQuery(id+"F0.wireOp",EDGE,"E1732"),sQuery(id+"F0.wireOp",EDGE,"E1733"),sQuery(id+"F0.wireOp",EDGE,"E1734"),sQuery(id+"F0.wireOp",EDGE,"E1735"),sQuery(id+"F0.wireOp",EDGE,"E1736"),sQuery(id+"F0.wireOp",EDGE,"E1737"),sQuery(id+"F0.wireOp",EDGE,"E1738"),sQuery(id+"F0.wireOp",EDGE,"E1739"),sQuery(id+"F0.wireOp",EDGE,"E1740"),sQuery(id+"F0.wireOp",EDGE,"E1741"),sQuery(id+"F0.wireOp",EDGE,"E1742"),sQuery(id+"F0.wireOp",EDGE,"E1743"),sQuery(id+"F0.wireOp",EDGE,"E1744"),sQuery(id+"F0.wireOp",EDGE,"E1745"),sQuery(id+"F0.wireOp",EDGE,"E1746"),sQuery(id+"F0.wireOp",EDGE,"E1747"),sQuery(id+"F0.wireOp",EDGE,"E1748"),sQuery(id+"F0.wireOp",EDGE,"E1749"),sQuery(id+"F0.wireOp",EDGE,"E1750"),sQuery(id+"F0.wireOp",EDGE,"E1751"),sQuery(id+"F0.wireOp",EDGE,"E1752"),sQuery(id+"F0.wireOp",EDGE,"E1753"),sQuery(id+"F0.wireOp",EDGE,"E1754"),sQuery(id+"F0.wireOp",EDGE,"E1755"),sQuery(id+"F0.wireOp",EDGE,"E1756"),sQuery(id+"F0.wireOp",EDGE,"E1757"),sQuery(id+"F0.wireOp",EDGE,"E1758"),sQuery(id+"F0.wireOp",EDGE,"E1759"),sQuery(id+"F0.wireOp",EDGE,"E1760"),sQuery(id+"F0.wireOp",EDGE,"E1761"),sQuery(id+"F0.wireOp",EDGE,"E1762"),sQuery(id+"F0.wireOp",EDGE,"E1763"),sQuery(id+"F0.wireOp",EDGE,"E1764"),sQuery(id+"F0.wireOp",EDGE,"E1765"),sQuery(id+"F0.wireOp",EDGE,"E1766"),sQuery(id+"F0.wireOp",EDGE,"E1767"),sQuery(id+"F0.wireOp",EDGE,"E1768"),sQuery(id+"F0.wireOp",EDGE,"E1769"),sQuery(id+"F0.wireOp",EDGE,"E1770"),sQuery(id+"F0.wireOp",EDGE,"E1771"),sQuery(id+"F0.wireOp",EDGE,"E1772"),sQuery(id+"F0.wireOp",EDGE,"E1773"),sQuery(id+"F0.wireOp",EDGE,"E1774"),sQuery(id+"F0.wireOp",EDGE,"E1775"),sQuery(id+"F0.wireOp",EDGE,"E1776"),sQuery(id+"F0.wireOp",EDGE,"E1777"),sQuery(id+"F0.wireOp",EDGE,"E1778"),sQuery(id+"F0.wireOp",EDGE,"E1779"),sQuery(id+"F0.wireOp",EDGE,"E1780"),sQuery(id+"F0.wireOp",EDGE,"E1781"),sQuery(id+"F0.wireOp",EDGE,"E1782"),sQuery(id+"F0.wireOp",EDGE,"E1783"),sQuery(id+"F0.wireOp",EDGE,"E1784"),sQuery(id+"F0.wireOp",EDGE,"E1785"),sQuery(id+"F0.wireOp",EDGE,"E1786"),sQuery(id+"F0.wireOp",EDGE,"E1787"),sQuery(id+"F0.wireOp",EDGE,"E1788"),sQuery(id+"F0.wireOp",EDGE,"E1789"),sQuery(id+"F0.wireOp",EDGE,"E1790"),sQuery(id+"F0.wireOp",EDGE,"E1791"),sQuery(id+"F0.wireOp",EDGE,"E1792"),sQuery(id+"F0.wireOp",EDGE,"E1793"),sQuery(id+"F0.wireOp",EDGE,"E1794"),sQuery(id+"F0.wireOp",EDGE,"E1795"),sQuery(id+"F0.wireOp",EDGE,"E1796"),sQuery(id+"F0.wireOp",EDGE,"E1797"),sQuery(id+"F0.wireOp",EDGE,"E1798"),sQuery(id+"F0.wireOp",EDGE,"E1799"),sQuery(id+"F0.wireOp",EDGE,"E1800"),sQuery(id+"F0.wireOp",EDGE,"E1801"),sQuery(id+"F0.wireOp",EDGE,"E1802"),sQuery(id+"F0.wireOp",EDGE,"E1803"),sQuery(id+"F0.wireOp",EDGE,"E1804"),sQuery(id+"F0.wireOp",EDGE,"E1805"),sQuery(id+"F0.wireOp",EDGE,"E1806"),sQuery(id+"F0.wireOp",EDGE,"E1807"),sQuery(id+"F0.wireOp",EDGE,"E1808"),sQuery(id+"F0.wireOp",EDGE,"E1809"),sQuery(id+"F0.wireOp",EDGE,"E1810"),sQuery(id+"F0.wireOp",EDGE,"E1811"),sQuery(id+"F0.wireOp",EDGE,"E1812"),sQuery(id+"F0.wireOp",EDGE,"E1813"),sQuery(id+"F0.wireOp",EDGE,"E1814"),sQuery(id+"F0.wireOp",EDGE,"E1815"),sQuery(id+"F0.wireOp",EDGE,"E1816"),sQuery(id+"F0.wireOp",EDGE,"E1817"),sQuery(id+"F0.wireOp",EDGE,"E1818"),sQuery(id+"F0.wireOp",EDGE,"E1819"),sQuery(id+"F0.wireOp",EDGE,"E1820"),sQuery(id+"F0.wireOp",EDGE,"E1821"),sQuery(id+"F0.wireOp",EDGE,"E1822"),sQuery(id+"F0.wireOp",EDGE,"E1823"),sQuery(id+"F0.wireOp",EDGE,"E1824"),sQuery(id+"F0.wireOp",EDGE,"E1825"),sQuery(id+"F0.wireOp",EDGE,"E1826"),sQuery(id+"F0.wireOp",EDGE,"E1827"),sQuery(id+"F0.wireOp",EDGE,"E1828"),sQuery(id+"F0.wireOp",EDGE,"E1829"),sQuery(id+"F0.wireOp",EDGE,"E1830"),sQuery(id+"F0.wireOp",EDGE,"E1831"),sQuery(id+"F0.wireOp",EDGE,"E1832"),sQuery(id+"F0.wireOp",EDGE,"E1833"),sQuery(id+"F0.wireOp",EDGE,"E1834"),sQuery(id+"F0.wireOp",EDGE,"E1835"),sQuery(id+"F0.wireOp",EDGE,"E1836"),sQuery(id+"F0.wireOp",EDGE,"E1837"),sQuery(id+"F0.wireOp",EDGE,"E1838"),sQuery(id+"F0.wireOp",EDGE,"E1839"),sQuery(id+"F0.wireOp",EDGE,"E1840"),sQuery(id+"F0.wireOp",EDGE,"E1841"),sQuery(id+"F0.wireOp",EDGE,"E1842"),sQuery(id+"F0.wireOp",EDGE,"E1843"),sQuery(id+"F0.wireOp",EDGE,"E1844"),sQuery(id+"F0.wireOp",EDGE,"E1845"),sQuery(id+"F0.wireOp",EDGE,"E1846"),sQuery(id+"F0.wireOp",EDGE,"E1847"),sQuery(id+"F0.wireOp",EDGE,"E1848"),sQuery(id+"F0.wireOp",EDGE,"E1849"),sQuery(id+"F0.wireOp",EDGE,"E1850"),sQuery(id+"F0.wireOp",EDGE,"E1851"),sQuery(id+"F0.wireOp",EDGE,"E1852"),sQuery(id+"F0.wireOp",EDGE,"E1853"),sQuery(id+"F0.wireOp",EDGE,"E1854"),sQuery(id+"F0.wireOp",EDGE,"E1855"),sQuery(id+"F0.wireOp",EDGE,"E1856"),sQuery(id+"F0.wireOp",EDGE,"E1857"),sQuery(id+"F0.wireOp",EDGE,"E1858"),sQuery(id+"F0.wireOp",EDGE,"E1859"),sQuery(id+"F0.wireOp",EDGE,"E1860"),sQuery(id+"F0.wireOp",EDGE,"E1861"),sQuery(id+"F0.wireOp",EDGE,"E1862"),sQuery(id+"F0.wireOp",EDGE,"E1863"),sQuery(id+"F0.wireOp",EDGE,"E1864"),sQuery(id+"F0.wireOp",EDGE,"E1865"),sQuery(id+"F0.wireOp",EDGE,"E1866"),sQuery(id+"F0.wireOp",EDGE,"E1867"),sQuery(id+"F0.wireOp",EDGE,"E1868"),sQuery(id+"F0.wireOp",EDGE,"E1869"),sQuery(id+"F0.wireOp",EDGE,"E1870"),sQuery(id+"F0.wireOp",EDGE,"E1871"),sQuery(id+"F0.wireOp",EDGE,"E1872"),sQuery(id+"F0.wireOp",EDGE,"E1873"),sQuery(id+"F0.wireOp",EDGE,"E1874"),sQuery(id+"F0.wireOp",EDGE,"E1875"),sQuery(id+"F0.wireOp",EDGE,"E1876"),sQuery(id+"F0.wireOp",EDGE,"E1877"),sQuery(id+"F0.wireOp",EDGE,"E1878"),sQuery(id+"F0.wireOp",EDGE,"E1879"),sQuery(id+"F0.wireOp",EDGE,"E1880"),sQuery(id+"F0.wireOp",EDGE,"E1881"),sQuery(id+"F0.wireOp",EDGE,"E1882"),sQuery(id+"F0.wireOp",EDGE,"E1883"),sQuery(id+"F0.wireOp",EDGE,"E1884"),sQuery(id+"F0.wireOp",EDGE,"E1885"),sQuery(id+"F0.wireOp",EDGE,"E1886"),sQuery(id+"F0.wireOp",EDGE,"E1887"),sQuery(id+"F0.wireOp",EDGE,"E1888"),sQuery(id+"F0.wireOp",EDGE,"E1889"),sQuery(id+"F0.wireOp",EDGE,"E1890"),sQuery(id+"F0.wireOp",EDGE,"E1891"),sQuery(id+"F0.wireOp",EDGE,"E1892"),sQuery(id+"F0.wireOp",EDGE,"E1893"),sQuery(id+"F0.wireOp",EDGE,"E1894"),sQuery(id+"F0.wireOp",EDGE,"E1895"),sQuery(id+"F0.wireOp",EDGE,"E1896"),sQuery(id+"F0.wireOp",EDGE,"E1897"),sQuery(id+"F0.wireOp",EDGE,"E1898"),sQuery(id+"F0.wireOp",EDGE,"E1899"),sQuery(id+"F0.wireOp",EDGE,"E1900"),sQuery(id+"F0.wireOp",EDGE,"E1901"),sQuery(id+"F0.wireOp",EDGE,"E1902"),sQuery(id+"F0.wireOp",EDGE,"E1903"),sQuery(id+"F0.wireOp",EDGE,"E1904"),sQuery(id+"F0.wireOp",EDGE,"E1905"),sQuery(id+"F0.wireOp",EDGE,"E1906"),sQuery(id+"F0.wireOp",EDGE,"E1907"),sQuery(id+"F0.wireOp",EDGE,"E1908"),sQuery(id+"F0.wireOp",EDGE,"E1909"),sQuery(id+"F0.wireOp",EDGE,"E1910"),sQuery(id+"F0.wireOp",EDGE,"E1911"),sQuery(id+"F0.wireOp",EDGE,"E1912"),sQuery(id+"F0.wireOp",EDGE,"E1913"),sQuery(id+"F0.wireOp",EDGE,"E1914"),sQuery(id+"F0.wireOp",EDGE,"E1915"),sQuery(id+"F0.wireOp",EDGE,"E1916"),sQuery(id+"F0.wireOp",EDGE,"E1917"),sQuery(id+"F0.wireOp",EDGE,"E1918"),sQuery(id+"F0.wireOp",EDGE,"E1919"),sQuery(id+"F0.wireOp",EDGE,"E1920"),sQuery(id+"F0.wireOp",EDGE,"E1921"),sQuery(id+"F0.wireOp",EDGE,"E1922"),sQuery(id+"F0.wireOp",EDGE,"E1923"),sQuery(id+"F0.wireOp",EDGE,"E1924"),sQuery(id+"F0.wireOp",EDGE,"E1925"),sQuery(id+"F0.wireOp",EDGE,"E1926"),sQuery(id+"F0.wireOp",EDGE,"E1927"),sQuery(id+"F0.wireOp",EDGE,"E1928"),sQuery(id+"F0.wireOp",EDGE,"E1929"),sQuery(id+"F0.wireOp",EDGE,"E1930"),sQuery(id+"F0.wireOp",EDGE,"E1931"),sQuery(id+"F0.wireOp",EDGE,"E1932"),sQuery(id+"F0.wireOp",EDGE,"E1933"),sQuery(id+"F0.wireOp",EDGE,"E1934"),sQuery(id+"F0.wireOp",EDGE,"E1935"),sQuery(id+"F0.wireOp",EDGE,"E1936"),sQuery(id+"F0.wireOp",EDGE,"E1937"),sQuery(id+"F0.wireOp",EDGE,"E1938"),sQuery(id+"F0.wireOp",EDGE,"E1939"),sQuery(id+"F0.wireOp",EDGE,"E1940"),sQuery(id+"F0.wireOp",EDGE,"E1941"),sQuery(id+"F0.wireOp",EDGE,"E1942"),sQuery(id+"F0.wireOp",EDGE,"E1943"),sQuery(id+"F0.wireOp",EDGE,"E1944"),sQuery(id+"F0.wireOp",EDGE,"E1945"),sQuery(id+"F0.wireOp",EDGE,"E1946"),sQuery(id+"F0.wireOp",EDGE,"E1947"),sQuery(id+"F0.wireOp",EDGE,"E1948"),sQuery(id+"F0.wireOp",EDGE,"E1949"),sQuery(id+"F0.wireOp",EDGE,"E1950"),sQuery(id+"F0.wireOp",EDGE,"E1951"),sQuery(id+"F0.wireOp",EDGE,"E1952"),sQuery(id+"F0.wireOp",EDGE,"E1953"),sQuery(id+"F0.wireOp",EDGE,"E1954"),sQuery(id+"F0.wireOp",EDGE,"E1955"),sQuery(id+"F0.wireOp",EDGE,"E1956"),sQuery(id+"F0.wireOp",EDGE,"E1957"),sQuery(id+"F0.wireOp",EDGE,"E1958"),sQuery(id+"F0.wireOp",EDGE,"E1959"),sQuery(id+"F0.wireOp",EDGE,"E1960"),sQuery(id+"F0.wireOp",EDGE,"E1961"),sQuery(id+"F0.wireOp",EDGE,"E1962"),sQuery(id+"F0.wireOp",EDGE,"E1963"),sQuery(id+"F0.wireOp",EDGE,"E1964"),sQuery(id+"F0.wireOp",EDGE,"E1965"),sQuery(id+"F0.wireOp",EDGE,"E1966"),sQuery(id+"F0.wireOp",EDGE,"E1967"),sQuery(id+"F0.wireOp",EDGE,"E1968"),sQuery(id+"F0.wireOp",EDGE,"E1969"),sQuery(id+"F0.wireOp",EDGE,"E1970"),sQuery(id+"F0.wireOp",EDGE,"E1971"),sQuery(id+"F0.wireOp",EDGE,"E1972"),sQuery(id+"F0.wireOp",EDGE,"E1973"),sQuery(id+"F0.wireOp",EDGE,"E1974"),sQuery(id+"F0.wireOp",EDGE,"E1975"),sQuery(id+"F0.wireOp",EDGE,"E1976"),sQuery(id+"F0.wireOp",EDGE,"E1977"),sQuery(id+"F0.wireOp",EDGE,"E1978"),sQuery(id+"F0.wireOp",EDGE,"E1979"),sQuery(id+"F0.wireOp",EDGE,"E1980"),sQuery(id+"F0.wireOp",EDGE,"E1981"),sQuery(id+"F0.wireOp",EDGE,"E1982"),sQuery(id+"F0.wireOp",EDGE,"E1983"),sQuery(id+"F0.wireOp",EDGE,"E1984"),sQuery(id+"F0.wireOp",EDGE,"E1985"),sQuery(id+"F0.wireOp",EDGE,"E1986"),sQuery(id+"F0.wireOp",EDGE,"E1987"),sQuery(id+"F0.wireOp",EDGE,"E1988"),sQuery(id+"F0.wireOp",EDGE,"E1989"),sQuery(id+"F0.wireOp",EDGE,"E1990"),sQuery(id+"F0.wireOp",EDGE,"E1991"),sQuery(id+"F0.wireOp",EDGE,"E1992"),sQuery(id+"F0.wireOp",EDGE,"E1993"),sQuery(id+"F0.wireOp",EDGE,"E1994"),sQuery(id+"F0.wireOp",EDGE,"E1995"),sQuery(id+"F0.wireOp",EDGE,"E1996"),sQuery(id+"F0.wireOp",EDGE,"E1997"),sQuery(id+"F0.wireOp",EDGE,"E1998"),sQuery(id+"F0.wireOp",EDGE,"E1999"),sQuery(id+"F0.wireOp",EDGE,"E2000"),sQuery(id+"F0.wireOp",EDGE,"E2001"),sQuery(id+"F0.wireOp",EDGE,"E2002"),sQuery(id+"F0.wireOp",EDGE,"E2003"),sQuery(id+"F0.wireOp",EDGE,"E2004"),sQuery(id+"F0.wireOp",EDGE,"E2005"),sQuery(id+"F0.wireOp",EDGE,"E2006"),sQuery(id+"F0.wireOp",EDGE,"E2007"),sQuery(id+"F0.wireOp",EDGE,"E2008"),sQuery(id+"F0.wireOp",EDGE,"E2009"),sQuery(id+"F0.wireOp",EDGE,"E2010"),sQuery(id+"F0.wireOp",EDGE,"E2011"),sQuery(id+"F0.wireOp",EDGE,"E2012"),sQuery(id+"F0.wireOp",EDGE,"E2013"),sQuery(id+"F0.wireOp",EDGE,"E2014"),sQuery(id+"F0.wireOp",EDGE,"E2015"),sQuery(id+"F0.wireOp",EDGE,"E2016"),sQuery(id+"F0.wireOp",EDGE,"E2017"),sQuery(id+"F0.wireOp",EDGE,"E2018"),sQuery(id+"F0.wireOp",EDGE,"E2019"),sQuery(id+"F0.wireOp",EDGE,"E2020"),sQuery(id+"F0.wireOp",EDGE,"E2021"),sQuery(id+"F0.wireOp",EDGE,"E2022"),sQuery(id+"F0.wireOp",EDGE,"E2023"),sQuery(id+"F0.wireOp",EDGE,"E2024"),sQuery(id+"F0.wireOp",EDGE,"E2025"),sQuery(id+"F0.wireOp",EDGE,"E2026"),sQuery(id+"F0.wireOp",EDGE,"E2027"),sQuery(id+"F0.wireOp",EDGE,"E2028"),sQuery(id+"F0.wireOp",EDGE,"E2029"),sQuery(id+"F0.wireOp",EDGE,"E2030"),sQuery(id+"F0.wireOp",EDGE,"E2031"),sQuery(id+"F0.wireOp",EDGE,"E2032"),sQuery(id+"F0.wireOp",EDGE,"E2033"),sQuery(id+"F0.wireOp",EDGE,"E2034"),sQuery(id+"F0.wireOp",EDGE,"E2035"),sQuery(id+"F0.wireOp",EDGE,"E2036"),sQuery(id+"F0.wireOp",EDGE,"E2037"),sQuery(id+"F0.wireOp",EDGE,"E2038"),sQuery(id+"F0.wireOp",EDGE,"E2039"),sQuery(id+"F0.wireOp",EDGE,"E2040"),sQuery(id+"F0.wireOp",EDGE,"E2041"),sQuery(id+"F0.wireOp",EDGE,"E2042"),sQuery(id+"F0.wireOp",EDGE,"E2043"),sQuery(id+"F0.wireOp",EDGE,"E2044"),sQuery(id+"F0.wireOp",EDGE,"E2045"),sQuery(id+"F0.wireOp",EDGE,"E2046"),sQuery(id+"F0.wireOp",EDGE,"E2047"),sQuery(id+"F0.wireOp",EDGE,"E2048"),sQuery(id+"F0.wireOp",EDGE,"E2049"),sQuery(id+"F0.wireOp",EDGE,"E2050"),sQuery(id+"F0.wireOp",EDGE,"E2051"),sQuery(id+"F0.wireOp",EDGE,"E2052"),sQuery(id+"F0.wireOp",EDGE,"E2053"),sQuery(id+"F0.wireOp",EDGE,"E2054"),sQuery(id+"F0.wireOp",EDGE,"E2055"),sQuery(id+"F0.wireOp",EDGE,"E2056"),sQuery(id+"F0.wireOp",EDGE,"E2057"),sQuery(id+"F0.wireOp",EDGE,"E2058"),sQuery(id+"F0.wireOp",EDGE,"E2059"),sQuery(id+"F0.wireOp",EDGE,"E2060"),sQuery(id+"F0.wireOp",EDGE,"E2061"),sQuery(id+"F0.wireOp",EDGE,"E2062"),sQuery(id+"F0.wireOp",EDGE,"E2063"),sQuery(id+"F0.wireOp",EDGE,"E2064"),sQuery(id+"F0.wireOp",EDGE,"E2065"),sQuery(id+"F0.wireOp",EDGE,"E2066"),sQuery(id+"F0.wireOp",EDGE,"E2067"),sQuery(id+"F0.wireOp",EDGE,"E2068"),sQuery(id+"F0.wireOp",EDGE,"E2069"),sQuery(id+"F0.wireOp",EDGE,"E2070"),sQuery(id+"F0.wireOp",EDGE,"E2071"),sQuery(id+"F0.wireOp",EDGE,"E2072"),sQuery(id+"F0.wireOp",EDGE,"E2073"),sQuery(id+"F0.wireOp",EDGE,"E2074"),sQuery(id+"F0.wireOp",EDGE,"E2075"),sQuery(id+"F0.wireOp",EDGE,"E2076"),sQuery(id+"F0.wireOp",EDGE,"E2077"),sQuery(id+"F0.wireOp",EDGE,"E2078"),sQuery(id+"F0.wireOp",EDGE,"E2079"),sQuery(id+"F0.wireOp",EDGE,"E2080"),sQuery(id+"F0.wireOp",EDGE,"E2081"),sQuery(id+"F0.wireOp",EDGE,"E2082"),sQuery(id+"F0.wireOp",EDGE,"E2083"),sQuery(id+"F0.wireOp",EDGE,"E2084"),sQuery(id+"F0.wireOp",EDGE,"E2085"),sQuery(id+"F0.wireOp",EDGE,"E2086"),sQuery(id+"F0.wireOp",EDGE,"E2087"),sQuery(id+"F0.wireOp",EDGE,"E2088"),sQuery(id+"F0.wireOp",EDGE,"E2089"),sQuery(id+"F0.wireOp",EDGE,"E2090"),sQuery(id+"F0.wireOp",EDGE,"E2091"),sQuery(id+"F0.wireOp",EDGE,"E2092"),sQuery(id+"F0.wireOp",EDGE,"E2093"),sQuery(id+"F0.wireOp",EDGE,"E2094"),sQuery(id+"F0.wireOp",EDGE,"E2095"),sQuery(id+"F0.wireOp",EDGE,"E2096"),sQuery(id+"F0.wireOp",EDGE,"E2097"),sQuery(id+"F0.wireOp",EDGE,"E2098"),sQuery(id+"F0.wireOp",EDGE,"E2099"),sQuery(id+"F0.wireOp",EDGE,"E2100"),sQuery(id+"F0.wireOp",EDGE,"E2101"),sQuery(id+"F0.wireOp",EDGE,"E2102"),sQuery(id+"F0.wireOp",EDGE,"E2103"),sQuery(id+"F0.wireOp",EDGE,"E2104"),sQuery(id+"F0.wireOp",EDGE,"E2105"),sQuery(id+"F0.wireOp",EDGE,"E2106"),sQuery(id+"F0.wireOp",EDGE,"E2107"),sQuery(id+"F0.wireOp",EDGE,"E2108"),sQuery(id+"F0.wireOp",EDGE,"E2109"),sQuery(id+"F0.wireOp",EDGE,"E2110"),sQuery(id+"F0.wireOp",EDGE,"E2111"),sQuery(id+"F0.wireOp",EDGE,"E2112"),sQuery(id+"F0.wireOp",EDGE,"E2113"),sQuery(id+"F0.wireOp",EDGE,"E2114"),sQuery(id+"F0.wireOp",EDGE,"E2115"),sQuery(id+"F0.wireOp",EDGE,"E2116"),sQuery(id+"F0.wireOp",EDGE,"E2117"),sQuery(id+"F0.wireOp",EDGE,"E2118"),sQuery(id+"F0.wireOp",EDGE,"E2119"),sQuery(id+"F0.wireOp",EDGE,"E2120"),sQuery(id+"F0.wireOp",EDGE,"E2121"),sQuery(id+"F0.wireOp",EDGE,"E2122"),sQuery(id+"F0.wireOp",EDGE,"E2123"),sQuery(id+"F0.wireOp",EDGE,"E2124"),sQuery(id+"F0.wireOp",EDGE,"E2125"),sQuery(id+"F0.wireOp",EDGE,"E2126"),sQuery(id+"F0.wireOp",EDGE,"E2127"),sQuery(id+"F0.wireOp",EDGE,"E2128"),sQuery(id+"F0.wireOp",EDGE,"E2129"),sQuery(id+"F0.wireOp",EDGE,"E2130"),sQuery(id+"F0.wireOp",EDGE,"E2131"),sQuery(id+"F0.wireOp",EDGE,"E2132"),sQuery(id+"F0.wireOp",EDGE,"E2133"),sQuery(id+"F0.wireOp",EDGE,"E2134"),sQuery(id+"F0.wireOp",EDGE,"E2135"),sQuery(id+"F0.wireOp",EDGE,"E2136"),sQuery(id+"F0.wireOp",EDGE,"E2137"),sQuery(id+"F0.wireOp",EDGE,"E2138"),sQuery(id+"F0.wireOp",EDGE,"E2139"),sQuery(id+"F0.wireOp",EDGE,"E2140"),sQuery(id+"F0.wireOp",EDGE,"E2141"),sQuery(id+"F0.wireOp",EDGE,"E2142"),sQuery(id+"F0.wireOp",EDGE,"E2143"),sQuery(id+"F0.wireOp",EDGE,"E2144"),sQuery(id+"F0.wireOp",EDGE,"E2145"),sQuery(id+"F0.wireOp",EDGE,"E2146"),sQuery(id+"F0.wireOp",EDGE,"E2147"),sQuery(id+"F0.wireOp",EDGE,"E2148"),sQuery(id+"F0.wireOp",EDGE,"E2149"),sQuery(id+"F0.wireOp",EDGE,"E2150"),sQuery(id+"F0.wireOp",EDGE,"E2151"),sQuery(id+"F0.wireOp",EDGE,"E2152"),sQuery(id+"F0.wireOp",EDGE,"E2153"),sQuery(id+"F0.wireOp",EDGE,"E2154"),sQuery(id+"F0.wireOp",EDGE,"E2155"),sQuery(id+"F0.wireOp",EDGE,"E2156"),sQuery(id+"F0.wireOp",EDGE,"E2157"),sQuery(id+"F0.wireOp",EDGE,"E2158"),sQuery(id+"F0.wireOp",EDGE,"E2159"),sQuery(id+"F0.wireOp",EDGE,"E2160"),sQuery(id+"F0.wireOp",EDGE,"E2161"),sQuery(id+"F0.wireOp",EDGE,"E2162"),sQuery(id+"F0.wireOp",EDGE,"E2163"),sQuery(id+"F0.wireOp",EDGE,"E2164"),sQuery(id+"F0.wireOp",EDGE,"E2165"),sQuery(id+"F0.wireOp",EDGE,"E2166"),sQuery(id+"F0.wireOp",EDGE,"E2167"),sQuery(id+"F0.wireOp",EDGE,"E2168"),sQuery(id+"F0.wireOp",EDGE,"E2169"),sQuery(id+"F0.wireOp",EDGE,"E2170"),sQuery(id+"F0.wireOp",EDGE,"E2171"),sQuery(id+"F0.wireOp",EDGE,"E2172"),sQuery(id+"F0.wireOp",EDGE,"E2173"),sQuery(id+"F0.wireOp",EDGE,"E2174"),sQuery(id+"F0.wireOp",EDGE,"E2175"),sQuery(id+"F0.wireOp",EDGE,"E2176"),sQuery(id+"F0.wireOp",EDGE,"E2177"),sQuery(id+"F0.wireOp",EDGE,"E2178"),sQuery(id+"F0.wireOp",EDGE,"E2179"),sQuery(id+"F0.wireOp",EDGE,"E2180"),sQuery(id+"F0.wireOp",EDGE,"E2181"),sQuery(id+"F0.wireOp",EDGE,"E2182"),sQuery(id+"F0.wireOp",EDGE,"E2183"),sQuery(id+"F0.wireOp",EDGE,"E2184"),sQuery(id+"F0.wireOp",EDGE,"E2185"),sQuery(id+"F0.wireOp",EDGE,"E2186"),sQuery(id+"F0.wireOp",EDGE,"E2187"),sQuery(id+"F0.wireOp",EDGE,"E2188"),sQuery(id+"F0.wireOp",EDGE,"E2189"),sQuery(id+"F0.wireOp",EDGE,"E2190"),sQuery(id+"F0.wireOp",EDGE,"E2191"),sQuery(id+"F0.wireOp",EDGE,"E2192"),sQuery(id+"F0.wireOp",EDGE,"E2193"),sQuery(id+"F0.wireOp",EDGE,"E2194"),sQuery(id+"F0.wireOp",EDGE,"E2195"),sQuery(id+"F0.wireOp",EDGE,"E2196"),sQuery(id+"F0.wireOp",EDGE,"E2197"),sQuery(id+"F0.wireOp",EDGE,"E2198"),sQuery(id+"F0.wireOp",EDGE,"E2199"),sQuery(id+"F0.wireOp",EDGE,"E2200"),sQuery(id+"F0.wireOp",EDGE,"E2201"),sQuery(id+"F0.wireOp",EDGE,"E2202"),sQuery(id+"F0.wireOp",EDGE,"E2203"),sQuery(id+"F0.wireOp",EDGE,"E2204"),sQuery(id+"F0.wireOp",EDGE,"E2205"),sQuery(id+"F0.wireOp",EDGE,"E2206"),sQuery(id+"F0.wireOp",EDGE,"E2207"),sQuery(id+"F0.wireOp",EDGE,"E2208"),sQuery(id+"F0.wireOp",EDGE,"E2209"),sQuery(id+"F0.wireOp",EDGE,"E2210"),sQuery(id+"F0.wireOp",EDGE,"E2211"),sQuery(id+"F0.wireOp",EDGE,"E2212"),sQuery(id+"F0.wireOp",EDGE,"E2213"),sQuery(id+"F0.wireOp",EDGE,"E2214"),sQuery(id+"F0.wireOp",EDGE,"E2215"),sQuery(id+"F0.wireOp",EDGE,"E2216"),sQuery(id+"F0.wireOp",EDGE,"E2217"),sQuery(id+"F0.wireOp",EDGE,"E2218"),sQuery(id+"F0.wireOp",EDGE,"E2219"),sQuery(id+"F0.wireOp",EDGE,"E2220"),sQuery(id+"F0.wireOp",EDGE,"E2221"),sQuery(id+"F0.wireOp",EDGE,"E2222"),sQuery(id+"F0.wireOp",EDGE,"E2223"),sQuery(id+"F0.wireOp",EDGE,"E2224"),sQuery(id+"F0.wireOp",EDGE,"E2225"),sQuery(id+"F0.wireOp",EDGE,"E2226"),sQuery(id+"F0.wireOp",EDGE,"E2227"),sQuery(id+"F0.wireOp",EDGE,"E2228"),sQuery(id+"F0.wireOp",EDGE,"E2229"),sQuery(id+"F0.wireOp",EDGE,"E2230"),sQuery(id+"F0.wireOp",EDGE,"E2231"),sQuery(id+"F0.wireOp",EDGE,"E2232"),sQuery(id+"F0.wireOp",EDGE,"E2233"),sQuery(id+"F0.wireOp",EDGE,"E2234"),sQuery(id+"F0.wireOp",EDGE,"E2235"),sQuery(id+"F0.wireOp",EDGE,"E2236"),sQuery(id+"F0.wireOp",EDGE,"E2237"),sQuery(id+"F0.wireOp",EDGE,"E2238"),sQuery(id+"F0.wireOp",EDGE,"E2239"),sQuery(id+"F0.wireOp",EDGE,"E2240"),sQuery(id+"F0.wireOp",EDGE,"E2241"),sQuery(id+"F0.wireOp",EDGE,"E2242"),sQuery(id+"F0.wireOp",EDGE,"E2243"),sQuery(id+"F0.wireOp",EDGE,"E2244"),sQuery(id+"F0.wireOp",EDGE,"E2245"),sQuery(id+"F0.wireOp",EDGE,"E2246"),sQuery(id+"F0.wireOp",EDGE,"E2247"),sQuery(id+"F0.wireOp",EDGE,"E2248"),sQuery(id+"F0.wireOp",EDGE,"E2249"),sQuery(id+"F0.wireOp",EDGE,"E2250"),sQuery(id+"F0.wireOp",EDGE,"E2251"),sQuery(id+"F0.wireOp",EDGE,"E2252"),sQuery(id+"F0.wireOp",EDGE,"E2253"),sQuery(id+"F0.wireOp",EDGE,"E2254"),sQuery(id+"F0.wireOp",EDGE,"E2255"),sQuery(id+"F0.wireOp",EDGE,"E2256"),sQuery(id+"F0.wireOp",EDGE,"E2257"),sQuery(id+"F0.wireOp",EDGE,"E2258"),sQuery(id+"F0.wireOp",EDGE,"E2259"),sQuery(id+"F0.wireOp",EDGE,"E2260"),sQuery(id+"F0.wireOp",EDGE,"E2261"),sQuery(id+"F0.wireOp",EDGE,"E2262"),sQuery(id+"F0.wireOp",EDGE,"E2263"),sQuery(id+"F0.wireOp",EDGE,"E2264"),sQuery(id+"F0.wireOp",EDGE,"E2265"),sQuery(id+"F0.wireOp",EDGE,"E2266"),sQuery(id+"F0.wireOp",EDGE,"E2267"),sQuery(id+"F0.wireOp",EDGE,"E2268"),sQuery(id+"F0.wireOp",EDGE,"E2269"),sQuery(id+"F0.wireOp",EDGE,"E2270"),sQuery(id+"F0.wireOp",EDGE,"E2271"),sQuery(id+"F0.wireOp",EDGE,"E2272"),sQuery(id+"F0.wireOp",EDGE,"E2273"),sQuery(id+"F0.wireOp",EDGE,"E2274"),sQuery(id+"F0.wireOp",EDGE,"E2275"),sQuery(id+"F0.wireOp",EDGE,"E2276"),sQuery(id+"F0.wireOp",EDGE,"E2277"),sQuery(id+"F0.wireOp",EDGE,"E2278"),sQuery(id+"F0.wireOp",EDGE,"E2279"),sQuery(id+"F0.wireOp",EDGE,"E2280"),sQuery(id+"F0.wireOp",EDGE,"E2281"),sQuery(id+"F0.wireOp",EDGE,"E2282"),sQuery(id+"F0.wireOp",EDGE,"E2283"),sQuery(id+"F0.wireOp",EDGE,"E2284"),sQuery(id+"F0.wireOp",EDGE,"E2285"),sQuery(id+"F0.wireOp",EDGE,"E2286"),sQuery(id+"F0.wireOp",EDGE,"E2287"),sQuery(id+"F0.wireOp",EDGE,"E2288"),sQuery(id+"F0.wireOp",EDGE,"E2289"),sQuery(id+"F0.wireOp",EDGE,"E2290"),sQuery(id+"F0.wireOp",EDGE,"E2291"),sQuery(id+"F0.wireOp",EDGE,"E2292"),sQuery(id+"F0.wireOp",EDGE,"E2293"),sQuery(id+"F0.wireOp",EDGE,"E2294"),sQuery(id+"F0.wireOp",EDGE,"E2295"),sQuery(id+"F0.wireOp",EDGE,"E2296"),sQuery(id+"F0.wireOp",EDGE,"E2297"),sQuery(id+"F0.wireOp",EDGE,"E2298"),sQuery(id+"F0.wireOp",EDGE,"E2299"),sQuery(id+"F0.wireOp",EDGE,"E2300"),sQuery(id+"F0.wireOp",EDGE,"E2301"),sQuery(id+"F0.wireOp",EDGE,"E2302"),sQuery(id+"F0.wireOp",EDGE,"E2303"),sQuery(id+"F0.wireOp",EDGE,"E2304"),sQuery(id+"F0.wireOp",EDGE,"E2305"),sQuery(id+"F0.wireOp",EDGE,"E2306"),sQuery(id+"F0.wireOp",EDGE,"E2307"),sQuery(id+"F0.wireOp",EDGE,"E2308"),sQuery(id+"F0.wireOp",EDGE,"E2309"),sQuery(id+"F0.wireOp",EDGE,"E2310"),sQuery(id+"F0.wireOp",EDGE,"E2311"),sQuery(id+"F0.wireOp",EDGE,"E2312"),sQuery(id+"F0.wireOp",EDGE,"E2313"),sQuery(id+"F0.wireOp",EDGE,"E2314"),sQuery(id+"F0.wireOp",EDGE,"E2315"),sQuery(id+"F0.wireOp",EDGE,"E2316"),sQuery(id+"F0.wireOp",EDGE,"E2317"),sQuery(id+"F0.wireOp",EDGE,"E2318"),sQuery(id+"F0.wireOp",EDGE,"E2319"),sQuery(id+"F0.wireOp",EDGE,"E2320"),sQuery(id+"F0.wireOp",EDGE,"E2321"),sQuery(id+"F0.wireOp",EDGE,"E2322"),sQuery(id+"F0.wireOp",EDGE,"E2323"),sQuery(id+"F0.wireOp",EDGE,"E2324"),sQuery(id+"F0.wireOp",EDGE,"E2325"),sQuery(id+"F0.wireOp",EDGE,"E2326"),sQuery(id+"F0.wireOp",EDGE,"E2327"),sQuery(id+"F0.wireOp",EDGE,"E2328"),sQuery(id+"F0.wireOp",EDGE,"E2329"),sQuery(id+"F0.wireOp",EDGE,"E2330"),sQuery(id+"F0.wireOp",EDGE,"E2331"),sQuery(id+"F0.wireOp",EDGE,"E2332"),sQuery(id+"F0.wireOp",EDGE,"E2333"),sQuery(id+"F0.wireOp",EDGE,"E2334"),sQuery(id+"F0.wireOp",EDGE,"E2335"),sQuery(id+"F0.wireOp",EDGE,"E2336"),sQuery(id+"F0.wireOp",EDGE,"E2337"),sQuery(id+"F0.wireOp",EDGE,"E2338"),sQuery(id+"F0.wireOp",EDGE,"E2339"),sQuery(id+"F0.wireOp",EDGE,"E2340"),sQuery(id+"F0.wireOp",EDGE,"E2341"),sQuery(id+"F0.wireOp",EDGE,"E2342"),sQuery(id+"F0.wireOp",EDGE,"E2343"),sQuery(id+"F0.wireOp",EDGE,"E2344"),sQuery(id+"F0.wireOp",EDGE,"E2345"),sQuery(id+"F0.wireOp",EDGE,"E2346"),sQuery(id+"F0.wireOp",EDGE,"E2347"),sQuery(id+"F0.wireOp",EDGE,"E2348"),sQuery(id+"F0.wireOp",EDGE,"E2349"),sQuery(id+"F0.wireOp",EDGE,"E2350"),sQuery(id+"F0.wireOp",EDGE,"E2351"),sQuery(id+"F0.wireOp",EDGE,"E2352"),sQuery(id+"F0.wireOp",EDGE,"E2353"),sQuery(id+"F0.wireOp",EDGE,"E2354"),sQuery(id+"F0.wireOp",EDGE,"E2355"),sQuery(id+"F0.wireOp",EDGE,"E2356"),sQuery(id+"F0.wireOp",EDGE,"E2357"),sQuery(id+"F0.wireOp",EDGE,"E2358"),sQuery(id+"F0.wireOp",EDGE,"E2359"),sQuery(id+"F0.wireOp",EDGE,"E2360"),sQuery(id+"F0.wireOp",EDGE,"E2361"),sQuery(id+"F0.wireOp",EDGE,"E2362"),sQuery(id+"F0.wireOp",EDGE,"E2363"),sQuery(id+"F0.wireOp",EDGE,"E2364"),sQuery(id+"F0.wireOp",EDGE,"E2365"),sQuery(id+"F0.wireOp",EDGE,"E2366"),sQuery(id+"F0.wireOp",EDGE,"E2367"),sQuery(id+"F0.wireOp",EDGE,"E2368"),sQuery(id+"F0.wireOp",EDGE,"E2369"),sQuery(id+"F0.wireOp",EDGE,"E2370"),sQuery(id+"F0.wireOp",EDGE,"E2371"),sQuery(id+"F0.wireOp",EDGE,"E2372"),sQuery(id+"F0.wireOp",EDGE,"E2373"),sQuery(id+"F0.wireOp",EDGE,"E2374"),sQuery(id+"F0.wireOp",EDGE,"E2375"),sQuery(id+"F0.wireOp",EDGE,"E2376"),sQuery(id+"F0.wireOp",EDGE,"E2377"),sQuery(id+"F0.wireOp",EDGE,"E2378"),sQuery(id+"F0.wireOp",EDGE,"E2379"),sQuery(id+"F0.wireOp",EDGE,"E2380"),sQuery(id+"F0.wireOp",EDGE,"E2381"),sQuery(id+"F0.wireOp",EDGE,"E2382"),sQuery(id+"F0.wireOp",EDGE,"E2383"),sQuery(id+"F0.wireOp",EDGE,"E2384"),sQuery(id+"F0.wireOp",EDGE,"E2385"),sQuery(id+"F0.wireOp",EDGE,"E2386"),sQuery(id+"F0.wireOp",EDGE,"E2387"),sQuery(id+"F0.wireOp",EDGE,"E2388"),sQuery(id+"F0.wireOp",EDGE,"E2389"),sQuery(id+"F0.wireOp",EDGE,"E2390"),sQuery(id+"F0.wireOp",EDGE,"E2391"),sQuery(id+"F0.wireOp",EDGE,"E2392"),sQuery(id+"F0.wireOp",EDGE,"E2393"),sQuery(id+"F0.wireOp",EDGE,"E2394"),sQuery(id+"F0.wireOp",EDGE,"E2395"),sQuery(id+"F0.wireOp",EDGE,"E2396"),sQuery(id+"F0.wireOp",EDGE,"E2397"),sQuery(id+"F0.wireOp",EDGE,"E2398"),sQuery(id+"F0.wireOp",EDGE,"E2399"),sQuery(id+"F0.wireOp",EDGE,"E2400"),sQuery(id+"F0.wireOp",EDGE,"E2401"),sQuery(id+"F0.wireOp",EDGE,"E2402"),sQuery(id+"F0.wireOp",EDGE,"E2403"),sQuery(id+"F0.wireOp",EDGE,"E2404"),sQuery(id+"F0.wireOp",EDGE,"E2405"),sQuery(id+"F0.wireOp",EDGE,"E2406"),sQuery(id+"F0.wireOp",EDGE,"E2407"),sQuery(id+"F0.wireOp",EDGE,"E2408"),sQuery(id+"F0.wireOp",EDGE,"E2409"),sQuery(id+"F0.wireOp",EDGE,"E2410"),sQuery(id+"F0.wireOp",EDGE,"E2411"),sQuery(id+"F0.wireOp",EDGE,"E2412"),sQuery(id+"F0.wireOp",EDGE,"E2413"),sQuery(id+"F0.wireOp",EDGE,"E2414"),sQuery(id+"F0.wireOp",EDGE,"E2415"),sQuery(id+"F0.wireOp",EDGE,"E2416"),sQuery(id+"F0.wireOp",EDGE,"E2417"),sQuery(id+"F0.wireOp",EDGE,"E2418"),sQuery(id+"F0.wireOp",EDGE,"E2419"),sQuery(id+"F0.wireOp",EDGE,"E2420"),sQuery(id+"F0.wireOp",EDGE,"E2421"),sQuery(id+"F0.wireOp",EDGE,"E2422"),sQuery(id+"F0.wireOp",EDGE,"E2423"),sQuery(id+"F0.wireOp",EDGE,"E2424"),sQuery(id+"F0.wireOp",EDGE,"E2425"),sQuery(id+"F0.wireOp",EDGE,"E2426"),sQuery(id+"F0.wireOp",EDGE,"E2427"),sQuery(id+"F0.wireOp",EDGE,"E2428"),sQuery(id+"F0.wireOp",EDGE,"E2429"),sQuery(id+"F0.wireOp",EDGE,"E2430"),sQuery(id+"F0.wireOp",EDGE,"E2431"),sQuery(id+"F0.wireOp",EDGE,"E2432"),sQuery(id+"F0.wireOp",EDGE,"E2433"),sQuery(id+"F0.wireOp",EDGE,"E2434"),sQuery(id+"F0.wireOp",EDGE,"E2435"),sQuery(id+"F0.wireOp",EDGE,"E2436"),sQuery(id+"F0.wireOp",EDGE,"E2437"),sQuery(id+"F0.wireOp",EDGE,"E2438"),sQuery(id+"F0.wireOp",EDGE,"E2439"),sQuery(id+"F0.wireOp",EDGE,"E2440"),sQuery(id+"F0.wireOp",EDGE,"E2441"),sQuery(id+"F0.wireOp",EDGE,"E2442"),sQuery(id+"F0.wireOp",EDGE,"E2443"),sQuery(id+"F0.wireOp",EDGE,"E2444"),sQuery(id+"F0.wireOp",EDGE,"E2445"),sQuery(id+"F0.wireOp",EDGE,"E2446"),sQuery(id+"F0.wireOp",EDGE,"E2447"),sQuery(id+"F0.wireOp",EDGE,"E2448"),sQuery(id+"F0.wireOp",EDGE,"E2449"),sQuery(id+"F0.wireOp",EDGE,"E2450"),sQuery(id+"F0.wireOp",EDGE,"E2451"),sQuery(id+"F0.wireOp",EDGE,"E2452"),sQuery(id+"F0.wireOp",EDGE,"E2453"),sQuery(id+"F0.wireOp",EDGE,"E2454"),sQuery(id+"F0.wireOp",EDGE,"E2455"),sQuery(id+"F0.wireOp",EDGE,"E2456"),sQuery(id+"F0.wireOp",EDGE,"E2457"),sQuery(id+"F0.wireOp",EDGE,"E2458"),sQuery(id+"F0.wireOp",EDGE,"E2459"),sQuery(id+"F0.wireOp",EDGE,"E2460"),sQuery(id+"F0.wireOp",EDGE,"E2461"),sQuery(id+"F0.wireOp",EDGE,"E2462"),sQuery(id+"F0.wireOp",EDGE,"E2463"),sQuery(id+"F0.wireOp",EDGE,"E2464"),sQuery(id+"F0.wireOp",EDGE,"E2465"),sQuery(id+"F0.wireOp",EDGE,"E2466"),sQuery(id+"F0.wireOp",EDGE,"E2467"),sQuery(id+"F0.wireOp",EDGE,"E2468"),sQuery(id+"F0.wireOp",EDGE,"E2469"),sQuery(id+"F0.wireOp",EDGE,"E2470"),sQuery(id+"F0.wireOp",EDGE,"E2471"),sQuery(id+"F0.wireOp",EDGE,"E2472"),sQuery(id+"F0.wireOp",EDGE,"E2473"),sQuery(id+"F0.wireOp",EDGE,"E2474"),sQuery(id+"F0.wireOp",EDGE,"E2475"),sQuery(id+"F0.wireOp",EDGE,"E2476"),sQuery(id+"F0.wireOp",EDGE,"E2477"),sQuery(id+"F0.wireOp",EDGE,"E2478"),sQuery(id+"F0.wireOp",EDGE,"E2479"),sQuery(id+"F0.wireOp",EDGE,"E2480"),sQuery(id+"F0.wireOp",EDGE,"E2481"),sQuery(id+"F0.wireOp",EDGE,"E2482"),sQuery(id+"F0.wireOp",EDGE,"E2483"),sQuery(id+"F0.wireOp",EDGE,"E2484"),sQuery(id+"F0.wireOp",EDGE,"E2485"),sQuery(id+"F0.wireOp",EDGE,"E2486"),sQuery(id+"F0.wireOp",EDGE,"E2487"),sQuery(id+"F0.wireOp",EDGE,"E2488"),sQuery(id+"F0.wireOp",EDGE,"E2489"),sQuery(id+"F0.wireOp",EDGE,"E2490"),sQuery(id+"F0.wireOp",EDGE,"E2491"),sQuery(id+"F0.wireOp",EDGE,"E2492"),sQuery(id+"F0.wireOp",EDGE,"E2493"),sQuery(id+"F0.wireOp",EDGE,"E2494"),sQuery(id+"F0.wireOp",EDGE,"E2495"),sQuery(id+"F0.wireOp",EDGE,"E2496"),sQuery(id+"F0.wireOp",EDGE,"E2497"),sQuery(id+"F0.wireOp",EDGE,"E2498"),sQuery(id+"F0.wireOp",EDGE,"E2499"),sQuery(id+"F0.wireOp",EDGE,"E2500"),sQuery(id+"F0.wireOp",EDGE,"E2501"),sQuery(id+"F0.wireOp",EDGE,"E2502"),sQuery(id+"F0.wireOp",EDGE,"E2503"),sQuery(id+"F0.wireOp",EDGE,"E2504"),sQuery(id+"F0.wireOp",EDGE,"E2505"),sQuery(id+"F0.wireOp",EDGE,"E2506"),sQuery(id+"F0.wireOp",EDGE,"E2507"),sQuery(id+"F0.wireOp",EDGE,"E2508"),sQuery(id+"F0.wireOp",EDGE,"E2509"),sQuery(id+"F0.wireOp",EDGE,"E2510"),sQuery(id+"F0.wireOp",EDGE,"E2511"),sQuery(id+"F0.wireOp",EDGE,"E2512"),sQuery(id+"F0.wireOp",EDGE,"E2513"),sQuery(id+"F0.wireOp",EDGE,"E2514"),sQuery(id+"F0.wireOp",EDGE,"E2515"),sQuery(id+"F0.wireOp",EDGE,"E2516"),sQuery(id+"F0.wireOp",EDGE,"E2517"),sQuery(id+"F0.wireOp",EDGE,"E2518"),sQuery(id+"F0.wireOp",EDGE,"E2519"),sQuery(id+"F0.wireOp",EDGE,"E2520"),sQuery(id+"F0.wireOp",EDGE,"E2521"),sQuery(id+"F0.wireOp",EDGE,"E2522"),sQuery(id+"F0.wireOp",EDGE,"E2523"),sQuery(id+"F0.wireOp",EDGE,"E2524"),sQuery(id+"F0.wireOp",EDGE,"E2525"),sQuery(id+"F0.wireOp",EDGE,"E2526"),sQuery(id+"F0.wireOp",EDGE,"E2527"),sQuery(id+"F0.wireOp",EDGE,"E2528"),sQuery(id+"F0.wireOp",EDGE,"E2529"),sQuery(id+"F0.wireOp",EDGE,"E2530"),sQuery(id+"F0.wireOp",EDGE,"E2531"),sQuery(id+"F0.wireOp",EDGE,"E2532"),sQuery(id+"F0.wireOp",EDGE,"E2533"),sQuery(id+"F0.wireOp",EDGE,"E2534"),sQuery(id+"F0.wireOp",EDGE,"E2535"),sQuery(id+"F0.wireOp",EDGE,"E2536"),sQuery(id+"F0.wireOp",EDGE,"E2537"),sQuery(id+"F0.wireOp",EDGE,"E2538"),sQuery(id+"F0.wireOp",EDGE,"E2539"),sQuery(id+"F0.wireOp",EDGE,"E2540"),sQuery(id+"F0.wireOp",EDGE,"E2541"),sQuery(id+"F0.wireOp",EDGE,"E2542"),sQuery(id+"F0.wireOp",EDGE,"E2543"),sQuery(id+"F0.wireOp",EDGE,"E2544"),sQuery(id+"F0.wireOp",EDGE,"E2545"),sQuery(id+"F0.wireOp",EDGE,"E2546"),sQuery(id+"F0.wireOp",EDGE,"E2547"),sQuery(id+"F0.wireOp",EDGE,"E2548"),sQuery(id+"F0.wireOp",EDGE,"E2549"),sQuery(id+"F0.wireOp",EDGE,"E2550"),sQuery(id+"F0.wireOp",EDGE,"E2551"),sQuery(id+"F0.wireOp",EDGE,"E2552"),sQuery(id+"F0.wireOp",EDGE,"E2553"),sQuery(id+"F0.wireOp",EDGE,"E2554"),sQuery(id+"F0.wireOp",EDGE,"E2555"),sQuery(id+"F0.wireOp",EDGE,"E2556"),sQuery(id+"F0.wireOp",EDGE,"E2557"),sQuery(id+"F0.wireOp",EDGE,"E2558"),sQuery(id+"F0.wireOp",EDGE,"E2559"),sQuery(id+"F0.wireOp",EDGE,"E2560"),sQuery(id+"F0.wireOp",EDGE,"E2561"),sQuery(id+"F0.wireOp",EDGE,"E2562"),sQuery(id+"F0.wireOp",EDGE,"E2563"),sQuery(id+"F0.wireOp",EDGE,"E2564"),sQuery(id+"F0.wireOp",EDGE,"E2565"),sQuery(id+"F0.wireOp",EDGE,"E2566"),sQuery(id+"F0.wireOp",EDGE,"E2567"),sQuery(id+"F0.wireOp",EDGE,"E2568"),sQuery(id+"F0.wireOp",EDGE,"E2569"),sQuery(id+"F0.wireOp",EDGE,"E2570"),sQuery(id+"F0.wireOp",EDGE,"E2571"),sQuery(id+"F0.wireOp",EDGE,"E2572"),sQuery(id+"F0.wireOp",EDGE,"E2573"),sQuery(id+"F0.wireOp",EDGE,"E2574"),sQuery(id+"F0.wireOp",EDGE,"E2575"),sQuery(id+"F0.wireOp",EDGE,"E2576"),sQuery(id+"F0.wireOp",EDGE,"E2577"),sQuery(id+"F0.wireOp",EDGE,"E2578"),sQuery(id+"F0.wireOp",EDGE,"E2579"),sQuery(id+"F0.wireOp",EDGE,"E2580"),sQuery(id+"F0.wireOp",EDGE,"E2581"),sQuery(id+"F0.wireOp",EDGE,"E2582"),sQuery(id+"F0.wireOp",EDGE,"E2583"),sQuery(id+"F0.wireOp",EDGE,"E2584"),sQuery(id+"F0.wireOp",EDGE,"E2585"),sQuery(id+"F0.wireOp",EDGE,"E2586"),sQuery(id+"F0.wireOp",EDGE,"E2587"),sQuery(id+"F0.wireOp",EDGE,"E2588"),sQuery(id+"F0.wireOp",EDGE,"E2589"),sQuery(id+"F0.wireOp",EDGE,"E2590"),sQuery(id+"F0.wireOp",EDGE,"E2591"),sQuery(id+"F0.wireOp",EDGE,"E2592"),sQuery(id+"F0.wireOp",EDGE,"E2593"),sQuery(id+"F0.wireOp",EDGE,"E2594"),sQuery(id+"F0.wireOp",EDGE,"E2595"),sQuery(id+"F0.wireOp",EDGE,"E2596"),sQuery(id+"F0.wireOp",EDGE,"E2597"),sQuery(id+"F0.wireOp",EDGE,"E2598"),sQuery(id+"F0.wireOp",EDGE,"E2599"),sQuery(id+"F0.wireOp",EDGE,"E2600"),sQuery(id+"F0.wireOp",EDGE,"E2601"),sQuery(id+"F0.wireOp",EDGE,"E2602"),sQuery(id+"F0.wireOp",EDGE,"E2603"),sQuery(id+"F0.wireOp",EDGE,"E2604"),sQuery(id+"F0.wireOp",EDGE,"E2605"),sQuery(id+"F0.wireOp",EDGE,"E2606"),sQuery(id+"F0.wireOp",EDGE,"E2607"),sQuery(id+"F0.wireOp",EDGE,"E2608"),sQuery(id+"F0.wireOp",EDGE,"E2609"),sQuery(id+"F0.wireOp",EDGE,"E2610"),sQuery(id+"F0.wireOp",EDGE,"E2611"),sQuery(id+"F0.wireOp",EDGE,"E2612"),sQuery(id+"F0.wireOp",EDGE,"E2613"),sQuery(id+"F0.wireOp",EDGE,"E2614"),sQuery(id+"F0.wireOp",EDGE,"E2615"),sQuery(id+"F0.wireOp",EDGE,"E2616"),sQuery(id+"F0.wireOp",EDGE,"E2617"),sQuery(id+"F0.wireOp",EDGE,"E2618"),sQuery(id+"F0.wireOp",EDGE,"E2619"),sQuery(id+"F0.wireOp",EDGE,"E2620"),sQuery(id+"F0.wireOp",EDGE,"E2621"),sQuery(id+"F0.wireOp",EDGE,"E2622"),sQuery(id+"F0.wireOp",EDGE,"E2623"),sQuery(id+"F0.wireOp",EDGE,"E2624"),sQuery(id+"F0.wireOp",EDGE,"E2625"),sQuery(id+"F0.wireOp",EDGE,"E2626"),sQuery(id+"F0.wireOp",EDGE,"E2627"),sQuery(id+"F0.wireOp",EDGE,"E2628"),sQuery(id+"F0.wireOp",EDGE,"E2629"),sQuery(id+"F0.wireOp",EDGE,"E2630"),sQuery(id+"F0.wireOp",EDGE,"E2631"),sQuery(id+"F0.wireOp",EDGE,"E2632"),sQuery(id+"F0.wireOp",EDGE,"E2633"),sQuery(id+"F0.wireOp",EDGE,"E2634"),sQuery(id+"F0.wireOp",EDGE,"E2635"),sQuery(id+"F0.wireOp",EDGE,"E2636"),sQuery(id+"F0.wireOp",EDGE,"E2637"),sQuery(id+"F0.wireOp",EDGE,"E2638"),sQuery(id+"F0.wireOp",EDGE,"E2639"),sQuery(id+"F0.wireOp",EDGE,"E2640"),sQuery(id+"F0.wireOp",EDGE,"E2641"),sQuery(id+"F0.wireOp",EDGE,"E2642"),sQuery(id+"F0.wireOp",EDGE,"E2643"),sQuery(id+"F0.wireOp",EDGE,"E2644"),sQuery(id+"F0.wireOp",EDGE,"E2645"),sQuery(id+"F0.wireOp",EDGE,"E2646"),sQuery(id+"F0.wireOp",EDGE,"E2647"),sQuery(id+"F0.wireOp",EDGE,"E2648"),sQuery(id+"F0.wireOp",EDGE,"E2649"),sQuery(id+"F0.wireOp",EDGE,"E2650"),sQuery(id+"F0.wireOp",EDGE,"E2651"),sQuery(id+"F0.wireOp",EDGE,"E2652"),sQuery(id+"F0.wireOp",EDGE,"E2653"),sQuery(id+"F0.wireOp",EDGE,"E2654"),sQuery(id+"F0.wireOp",EDGE,"E2655"),sQuery(id+"F0.wireOp",EDGE,"E2656"),sQuery(id+"F0.wireOp",EDGE,"E2657"),sQuery(id+"F0.wireOp",EDGE,"E2658"),sQuery(id+"F0.wireOp",EDGE,"E2659"),sQuery(id+"F0.wireOp",EDGE,"E2660"),sQuery(id+"F0.wireOp",EDGE,"E2661"),sQuery(id+"F0.wireOp",EDGE,"E2662"),sQuery(id+"F0.wireOp",EDGE,"E2663"),sQuery(id+"F0.wireOp",EDGE,"E2664"),sQuery(id+"F0.wireOp",EDGE,"E2665"),sQuery(id+"F0.wireOp",EDGE,"E2666"),sQuery(id+"F0.wireOp",EDGE,"E2667"),sQuery(id+"F0.wireOp",EDGE,"E2668"),sQuery(id+"F0.wireOp",EDGE,"E2669"),sQuery(id+"F0.wireOp",EDGE,"E2670"),sQuery(id+"F0.wireOp",EDGE,"E2671"),sQuery(id+"F0.wireOp",EDGE,"E2672"),sQuery(id+"F0.wireOp",EDGE,"E2673"),sQuery(id+"F0.wireOp",EDGE,"E2674"),sQuery(id+"F0.wireOp",EDGE,"E2675"),sQuery(id+"F0.wireOp",EDGE,"E2676"),sQuery(id+"F0.wireOp",EDGE,"E2677"),sQuery(id+"F0.wireOp",EDGE,"E2678"),sQuery(id+"F0.wireOp",EDGE,"E2679"),sQuery(id+"F0.wireOp",EDGE,"E2680"),sQuery(id+"F0.wireOp",EDGE,"E2681"),sQuery(id+"F0.wireOp",EDGE,"E2682"),sQuery(id+"F0.wireOp",EDGE,"E2683"),sQuery(id+"F0.wireOp",EDGE,"E2684"),sQuery(id+"F0.wireOp",EDGE,"E2685"),sQuery(id+"F0.wireOp",EDGE,"E2686"),sQuery(id+"F0.wireOp",EDGE,"E2687"),sQuery(id+"F0.wireOp",EDGE,"E2688"),sQuery(id+"F0.wireOp",EDGE,"E2689"),sQuery(id+"F0.wireOp",EDGE,"E2690"),sQuery(id+"F0.wireOp",EDGE,"E2691"),sQuery(id+"F0.wireOp",EDGE,"E2692"),sQuery(id+"F0.wireOp",EDGE,"E2693"),sQuery(id+"F0.wireOp",EDGE,"E2694"),sQuery(id+"F0.wireOp",EDGE,"E2695"),sQuery(id+"F0.wireOp",EDGE,"E2696"),sQuery(id+"F0.wireOp",EDGE,"E2697"),sQuery(id+"F0.wireOp",EDGE,"E2698"),sQuery(id+"F0.wireOp",EDGE,"E2699"),sQuery(id+"F0.wireOp",EDGE,"E2700"),sQuery(id+"F0.wireOp",EDGE,"E2701"),sQuery(id+"F0.wireOp",EDGE,"E2702"),sQuery(id+"F0.wireOp",EDGE,"E2703"),sQuery(id+"F0.wireOp",EDGE,"E2704"),sQuery(id+"F0.wireOp",EDGE,"E2705"),sQuery(id+"F0.wireOp",EDGE,"E2706"),sQuery(id+"F0.wireOp",EDGE,"E2707"),sQuery(id+"F0.wireOp",EDGE,"E2708"),sQuery(id+"F0.wireOp",EDGE,"E2709"),sQuery(id+"F0.wireOp",EDGE,"E2710"),sQuery(id+"F0.wireOp",EDGE,"E2711"),sQuery(id+"F0.wireOp",EDGE,"E2712"),sQuery(id+"F0.wireOp",EDGE,"E2713"),sQuery(id+"F0.wireOp",EDGE,"E2714"),sQuery(id+"F0.wireOp",EDGE,"E2715"),sQuery(id+"F0.wireOp",EDGE,"E2716"),sQuery(id+"F0.wireOp",EDGE,"E2717"),sQuery(id+"F0.wireOp",EDGE,"E2718"),sQuery(id+"F0.wireOp",EDGE,"E2719"),sQuery(id+"F0.wireOp",EDGE,"E2720"),sQuery(id+"F0.wireOp",EDGE,"E2721"),sQuery(id+"F0.wireOp",EDGE,"E2722"),sQuery(id+"F0.wireOp",EDGE,"E2723"),sQuery(id+"F0.wireOp",EDGE,"E2724"),sQuery(id+"F0.wireOp",EDGE,"E2725"),sQuery(id+"F0.wireOp",EDGE,"E2726"),sQuery(id+"F0.wireOp",EDGE,"E2727"),sQuery(id+"F0.wireOp",EDGE,"E2728"),sQuery(id+"F0.wireOp",EDGE,"E2729"),sQuery(id+"F0.wireOp",EDGE,"E2730"),sQuery(id+"F0.wireOp",EDGE,"E2731"),sQuery(id+"F0.wireOp",EDGE,"E2732"),sQuery(id+"F0.wireOp",EDGE,"E2733"),sQuery(id+"F0.wireOp",EDGE,"E2734"),sQuery(id+"F0.wireOp",EDGE,"E2735"),sQuery(id+"F0.wireOp",EDGE,"E2736"),sQuery(id+"F0.wireOp",EDGE,"E2737"),sQuery(id+"F0.wireOp",EDGE,"E2738"),sQuery(id+"F0.wireOp",EDGE,"E2739"),sQuery(id+"F0.wireOp",EDGE,"E2740"),sQuery(id+"F0.wireOp",EDGE,"E2741"),sQuery(id+"F0.wireOp",EDGE,"E2742"),sQuery(id+"F0.wireOp",EDGE,"E2743"),sQuery(id+"F0.wireOp",EDGE,"E2744"),sQuery(id+"F0.wireOp",EDGE,"E2745"),sQuery(id+"F0.wireOp",EDGE,"E2746"),sQuery(id+"F0.wireOp",EDGE,"E2747"),sQuery(id+"F0.wireOp",EDGE,"E2748"),sQuery(id+"F0.wireOp",EDGE,"E2749"),sQuery(id+"F0.wireOp",EDGE,"E2750"),sQuery(id+"F0.wireOp",EDGE,"E2751"),sQuery(id+"F0.wireOp",EDGE,"E2752"),sQuery(id+"F0.wireOp",EDGE,"E2753"),sQuery(id+"F0.wireOp",EDGE,"E2754"),sQuery(id+"F0.wireOp",EDGE,"E2755"),sQuery(id+"F0.wireOp",EDGE,"E2756"),sQuery(id+"F0.wireOp",EDGE,"E2757"),sQuery(id+"F0.wireOp",EDGE,"E2758"),sQuery(id+"F0.wireOp",EDGE,"E2759"),sQuery(id+"F0.wireOp",EDGE,"E2760"),sQuery(id+"F0.wireOp",EDGE,"E2761"),sQuery(id+"F0.wireOp",EDGE,"E2762"),sQuery(id+"F0.wireOp",EDGE,"E2763"),sQuery(id+"F0.wireOp",EDGE,"E2764"),sQuery(id+"F0.wireOp",EDGE,"E2765"),sQuery(id+"F0.wireOp",EDGE,"E2766"),sQuery(id+"F0.wireOp",EDGE,"E2767"),sQuery(id+"F0.wireOp",EDGE,"E2768"),sQuery(id+"F0.wireOp",EDGE,"E2769"),sQuery(id+"F0.wireOp",EDGE,"E2770"),sQuery(id+"F0.wireOp",EDGE,"E2771"),sQuery(id+"F0.wireOp",EDGE,"E2772"),sQuery(id+"F0.wireOp",EDGE,"E2773"),sQuery(id+"F0.wireOp",EDGE,"E2774"),sQuery(id+"F0.wireOp",EDGE,"E2775"),sQuery(id+"F0.wireOp",EDGE,"E2776"),sQuery(id+"F0.wireOp",EDGE,"E2777"),sQuery(id+"F0.wireOp",EDGE,"E2778"),sQuery(id+"F0.wireOp",EDGE,"E2779"),sQuery(id+"F0.wireOp",EDGE,"E2780"),sQuery(id+"F0.wireOp",EDGE,"E2781"),sQuery(id+"F0.wireOp",EDGE,"E2782"),sQuery(id+"F0.wireOp",EDGE,"E2783"),sQuery(id+"F0.wireOp",EDGE,"E2784"),sQuery(id+"F0.wireOp",EDGE,"E2785"),sQuery(id+"F0.wireOp",EDGE,"E2786"),sQuery(id+"F0.wireOp",EDGE,"E2787"),sQuery(id+"F0.wireOp",EDGE,"E2788"),sQuery(id+"F0.wireOp",EDGE,"E2789"),sQuery(id+"F0.wireOp",EDGE,"E2790"),sQuery(id+"F0.wireOp",EDGE,"E2791"),sQuery(id+"F0.wireOp",EDGE,"E2792"),sQuery(id+"F0.wireOp",EDGE,"E2793"),sQuery(id+"F0.wireOp",EDGE,"E2794"),sQuery(id+"F0.wireOp",EDGE,"E2795"),sQuery(id+"F0.wireOp",EDGE,"E2796"),sQuery(id+"F0.wireOp",EDGE,"E2797"),sQuery(id+"F0.wireOp",EDGE,"E2798"),sQuery(id+"F0.wireOp",EDGE,"E2799"),sQuery(id+"F0.wireOp",EDGE,"E2800"),sQuery(id+"F0.wireOp",EDGE,"E2801"),sQuery(id+"F0.wireOp",EDGE,"E2802"),sQuery(id+"F0.wireOp",EDGE,"E2803"),sQuery(id+"F0.wireOp",EDGE,"E2804"),sQuery(id+"F0.wireOp",EDGE,"E2805"),sQuery(id+"F0.wireOp",EDGE,"E2806"),sQuery(id+"F0.wireOp",EDGE,"E2807"),sQuery(id+"F0.wireOp",EDGE,"E2808"),sQuery(id+"F0.wireOp",EDGE,"E2809"),sQuery(id+"F0.wireOp",EDGE,"E2810"),sQuery(id+"F0.wireOp",EDGE,"E2811"),sQuery(id+"F0.wireOp",EDGE,"E2812"),sQuery(id+"F0.wireOp",EDGE,"E2813"),sQuery(id+"F0.wireOp",EDGE,"E2814"),sQuery(id+"F0.wireOp",EDGE,"E2815"),sQuery(id+"F0.wireOp",EDGE,"E2816"),sQuery(id+"F0.wireOp",EDGE,"E2817"),sQuery(id+"F0.wireOp",EDGE,"E2818"),sQuery(id+"F0.wireOp",EDGE,"E2819"),sQuery(id+"F0.wireOp",EDGE,"E2820"),sQuery(id+"F0.wireOp",EDGE,"E2821"),sQuery(id+"F0.wireOp",EDGE,"E2822"),sQuery(id+"F0.wireOp",EDGE,"E2823"),sQuery(id+"F0.wireOp",EDGE,"E2824"),sQuery(id+"F0.wireOp",EDGE,"E2825"),sQuery(id+"F0.wireOp",EDGE,"E2826"),sQuery(id+"F0.wireOp",EDGE,"E2827"),sQuery(id+"F0.wireOp",EDGE,"E2828"),sQuery(id+"F0.wireOp",EDGE,"E2829"),sQuery(id+"F0.wireOp",EDGE,"E2830"),sQuery(id+"F0.wireOp",EDGE,"E2831"),sQuery(id+"F0.wireOp",EDGE,"E2832"),sQuery(id+"F0.wireOp",EDGE,"E2833"),sQuery(id+"F0.wireOp",EDGE,"E2834"),sQuery(id+"F0.wireOp",EDGE,"E2835"),sQuery(id+"F0.wireOp",EDGE,"E2836"),sQuery(id+"F0.wireOp",EDGE,"E2837"),sQuery(id+"F0.wireOp",EDGE,"E2838"),sQuery(id+"F0.wireOp",EDGE,"E2839"),sQuery(id+"F0.wireOp",EDGE,"E2840"),sQuery(id+"F0.wireOp",EDGE,"E2841"),sQuery(id+"F0.wireOp",EDGE,"E2842"),sQuery(id+"F0.wireOp",EDGE,"E2843"),sQuery(id+"F0.wireOp",EDGE,"E2844"),sQuery(id+"F0.wireOp",EDGE,"E2845"),sQuery(id+"F0.wireOp",EDGE,"E2846"),sQuery(id+"F0.wireOp",EDGE,"E2847"),sQuery(id+"F0.wireOp",EDGE,"E2848"),sQuery(id+"F0.wireOp",EDGE,"E2849"),sQuery(id+"F0.wireOp",EDGE,"E2850"),sQuery(id+"F0.wireOp",EDGE,"E2851"),sQuery(id+"F0.wireOp",EDGE,"E2852"),sQuery(id+"F0.wireOp",EDGE,"E2853"),sQuery(id+"F0.wireOp",EDGE,"E2854"),sQuery(id+"F0.wireOp",EDGE,"E2855"),sQuery(id+"F0.wireOp",EDGE,"E2856"),sQuery(id+"F0.wireOp",EDGE,"E2857"),sQuery(id+"F0.wireOp",EDGE,"E2858"),sQuery(id+"F0.wireOp",EDGE,"E2859"),sQuery(id+"F0.wireOp",EDGE,"E2860"),sQuery(id+"F0.wireOp",EDGE,"E2861"),sQuery(id+"F0.wireOp",EDGE,"E2862"),sQuery(id+"F0.wireOp",EDGE,"E2863"),sQuery(id+"F0.wireOp",EDGE,"E2864"),sQuery(id+"F0.wireOp",EDGE,"E2865"),sQuery(id+"F0.wireOp",EDGE,"E2866"),sQuery(id+"F0.wireOp",EDGE,"E2867"),sQuery(id+"F0.wireOp",EDGE,"E2868"),sQuery(id+"F0.wireOp",EDGE,"E2869"),sQuery(id+"F0.wireOp",EDGE,"E2870"),sQuery(id+"F0.wireOp",EDGE,"E2871"),sQuery(id+"F0.wireOp",EDGE,"E2872"),sQuery(id+"F0.wireOp",EDGE,"E2873"),sQuery(id+"F0.wireOp",EDGE,"E2874"),sQuery(id+"F0.wireOp",EDGE,"E2875"),sQuery(id+"F0.wireOp",EDGE,"E2876"),sQuery(id+"F0.wireOp",EDGE,"E2877"),sQuery(id+"F0.wireOp",EDGE,"E2878"),sQuery(id+"F0.wireOp",EDGE,"E2879"),sQuery(id+"F0.wireOp",EDGE,"E2880"),sQuery(id+"F0.wireOp",EDGE,"E2881"),sQuery(id+"F0.wireOp",EDGE,"E2882"),sQuery(id+"F0.wireOp",EDGE,"E2883"),sQuery(id+"F0.wireOp",EDGE,"E2884"),sQuery(id+"F0.wireOp",EDGE,"E2885"),sQuery(id+"F0.wireOp",EDGE,"E2886"),sQuery(id+"F0.wireOp",EDGE,"E2887"),sQuery(id+"F0.wireOp",EDGE,"E2888"),sQuery(id+"F0.wireOp",EDGE,"E2889"),sQuery(id+"F0.wireOp",EDGE,"E2890"),sQuery(id+"F0.wireOp",EDGE,"E2891"),sQuery(id+"F0.wireOp",EDGE,"E2892"),sQuery(id+"F0.wireOp",EDGE,"E2893"),sQuery(id+"F0.wireOp",EDGE,"E2894"),sQuery(id+"F0.wireOp",EDGE,"E2895"),sQuery(id+"F0.wireOp",EDGE,"E2896"),sQuery(id+"F0.wireOp",EDGE,"E2897"),sQuery(id+"F0.wireOp",EDGE,"E2898"),sQuery(id+"F0.wireOp",EDGE,"E2899"),sQuery(id+"F0.wireOp",EDGE,"E2900"),sQuery(id+"F0.wireOp",EDGE,"E2901"),sQuery(id+"F0.wireOp",EDGE,"E2902"),sQuery(id+"F0.wireOp",EDGE,"E2903"),sQuery(id+"F0.wireOp",EDGE,"E2904"),sQuery(id+"F0.wireOp",EDGE,"E2905"),sQuery(id+"F0.wireOp",EDGE,"E2906"),sQuery(id+"F0.wireOp",EDGE,"E2907"),sQuery(id+"F0.wireOp",EDGE,"E2908"),sQuery(id+"F0.wireOp",EDGE,"E2909"),sQuery(id+"F0.wireOp",EDGE,"E2910"),sQuery(id+"F0.wireOp",EDGE,"E2911"),sQuery(id+"F0.wireOp",EDGE,"E2912"),sQuery(id+"F0.wireOp",EDGE,"E2913"),sQuery(id+"F0.wireOp",EDGE,"E2914"),sQuery(id+"F0.wireOp",EDGE,"E2915"),sQuery(id+"F0.wireOp",EDGE,"E2916"),sQuery(id+"F0.wireOp",EDGE,"E2917"),sQuery(id+"F0.wireOp",EDGE,"E2918"),sQuery(id+"F0.wireOp",EDGE,"E2919"),sQuery(id+"F0.wireOp",EDGE,"E2920"),sQuery(id+"F0.wireOp",EDGE,"E2921"),sQuery(id+"F0.wireOp",EDGE,"E2922"),sQuery(id+"F0.wireOp",EDGE,"E2923"),sQuery(id+"F0.wireOp",EDGE,"E2924"),sQuery(id+"F0.wireOp",EDGE,"E2925"),sQuery(id+"F0.wireOp",EDGE,"E2926"),sQuery(id+"F0.wireOp",EDGE,"E2927"),sQuery(id+"F0.wireOp",EDGE,"E2928"),sQuery(id+"F0.wireOp",EDGE,"E2929"),sQuery(id+"F0.wireOp",EDGE,"E2930"),sQuery(id+"F0.wireOp",EDGE,"E2931"),sQuery(id+"F0.wireOp",EDGE,"E2932"),sQuery(id+"F0.wireOp",EDGE,"E2933"),sQuery(id+"F0.wireOp",EDGE,"E2934"),sQuery(id+"F0.wireOp",EDGE,"E2935"),sQuery(id+"F0.wireOp",EDGE,"E2936"),sQuery(id+"F0.wireOp",EDGE,"E2937"),sQuery(id+"F0.wireOp",EDGE,"E2938"),sQuery(id+"F0.wireOp",EDGE,"E2939"),sQuery(id+"F0.wireOp",EDGE,"E2940"),sQuery(id+"F0.wireOp",EDGE,"E2941"),sQuery(id+"F0.wireOp",EDGE,"E2942"),sQuery(id+"F0.wireOp",EDGE,"E2943"),sQuery(id+"F0.wireOp",EDGE,"E2944"),sQuery(id+"F0.wireOp",EDGE,"E2945"),sQuery(id+"F0.wireOp",EDGE,"E2946"),sQuery(id+"F0.wireOp",EDGE,"E2947"),sQuery(id+"F0.wireOp",EDGE,"E2948"),sQuery(id+"F0.wireOp",EDGE,"E2949"),sQuery(id+"F0.wireOp",EDGE,"E2950"),sQuery(id+"F0.wireOp",EDGE,"E2951"),sQuery(id+"F0.wireOp",EDGE,"E2952"),sQuery(id+"F0.wireOp",EDGE,"E2953"),sQuery(id+"F0.wireOp",EDGE,"E2954"),sQuery(id+"F0.wireOp",EDGE,"E2955"),sQuery(id+"F0.wireOp",EDGE,"E2956"),sQuery(id+"F0.wireOp",EDGE,"E2957"),sQuery(id+"F0.wireOp",EDGE,"E2958"),sQuery(id+"F0.wireOp",EDGE,"E2959"),sQuery(id+"F0.wireOp",EDGE,"E2960"),sQuery(id+"F0.wireOp",EDGE,"E2961"),sQuery(id+"F0.wireOp",EDGE,"E2962"),sQuery(id+"F0.wireOp",EDGE,"E2963"),sQuery(id+"F0.wireOp",EDGE,"E2964"),sQuery(id+"F0.wireOp",EDGE,"E2965"),sQuery(id+"F0.wireOp",EDGE,"E2966"),sQuery(id+"F0.wireOp",EDGE,"E2967"),sQuery(id+"F0.wireOp",EDGE,"E2968"),sQuery(id+"F0.wireOp",EDGE,"E2969"),sQuery(id+"F0.wireOp",EDGE,"E2970"),sQuery(id+"F0.wireOp",EDGE,"E2971"),sQuery(id+"F0.wireOp",EDGE,"E2972"),sQuery(id+"F0.wireOp",EDGE,"E2973"),sQuery(id+"F0.wireOp",EDGE,"E2974"),sQuery(id+"F0.wireOp",EDGE,"E2975"),sQuery(id+"F0.wireOp",EDGE,"E2976"),sQuery(id+"F0.wireOp",EDGE,"E2977"),sQuery(id+"F0.wireOp",EDGE,"E2978"),sQuery(id+"F0.wireOp",EDGE,"E2979"),sQuery(id+"F0.wireOp",EDGE,"E2980"),sQuery(id+"F0.wireOp",EDGE,"E2981"),sQuery(id+"F0.wireOp",EDGE,"E2982"),sQuery(id+"F0.wireOp",EDGE,"E2983"),sQuery(id+"F0.wireOp",EDGE,"E2984"),sQuery(id+"F0.wireOp",EDGE,"E2985"),sQuery(id+"F0.wireOp",EDGE,"E2986"),sQuery(id+"F0.wireOp",EDGE,"E2987"),sQuery(id+"F0.wireOp",EDGE,"E2988"),sQuery(id+"F0.wireOp",EDGE,"E2989"),sQuery(id+"F0.wireOp",EDGE,"E2990"),sQuery(id+"F0.wireOp",EDGE,"E2991"),sQuery(id+"F0.wireOp",EDGE,"E2992"),sQuery(id+"F0.wireOp",EDGE,"E2993"),sQuery(id+"F0.wireOp",EDGE,"E2994"),sQuery(id+"F0.wireOp",EDGE,"E2995"),sQuery(id+"F0.wireOp",EDGE,"E2996"),sQuery(id+"F0.wireOp",EDGE,"E2997"),sQuery(id+"F0.wireOp",EDGE,"E2998"),sQuery(id+"F0.wireOp",EDGE,"E2999"),sQuery(id+"F0.wireOp",EDGE,"E3000"),sQuery(id+"F0.wireOp",EDGE,"E3001"),sQuery(id+"F0.wireOp",EDGE,"E3002"),sQuery(id+"F0.wireOp",EDGE,"E3003"),sQuery(id+"F0.wireOp",EDGE,"E3004"),sQuery(id+"F0.wireOp",EDGE,"E3005"),sQuery(id+"F0.wireOp",EDGE,"E3006"),sQuery(id+"F0.wireOp",EDGE,"E3007"),sQuery(id+"F0.wireOp",EDGE,"E3008"),sQuery(id+"F0.wireOp",EDGE,"E3009"),sQuery(id+"F0.wireOp",EDGE,"E3010"),sQuery(id+"F0.wireOp",EDGE,"E3011"),sQuery(id+"F0.wireOp",EDGE,"E3012"),sQuery(id+"F0.wireOp",EDGE,"E3013"),sQuery(id+"F0.wireOp",EDGE,"E3014"),sQuery(id+"F0.wireOp",EDGE,"E3015"),sQuery(id+"F0.wireOp",EDGE,"E3016"),sQuery(id+"F0.wireOp",EDGE,"E3017"),sQuery(id+"F0.wireOp",EDGE,"E3018"),sQuery(id+"F0.wireOp",EDGE,"E3019"),sQuery(id+"F0.wireOp",EDGE,"E3020"),sQuery(id+"F0.wireOp",EDGE,"E3021"),sQuery(id+"F0.wireOp",EDGE,"E3022"),sQuery(id+"F0.wireOp",EDGE,"E3023"),sQuery(id+"F0.wireOp",EDGE,"E3024"),sQuery(id+"F0.wireOp",EDGE,"E3025"),sQuery(id+"F0.wireOp",EDGE,"E3026"),sQuery(id+"F0.wireOp",EDGE,"E3027"),sQuery(id+"F0.wireOp",EDGE,"E3028"),sQuery(id+"F0.wireOp",EDGE,"E3029"),sQuery(id+"F0.wireOp",EDGE,"E3030"),sQuery(id+"F0.wireOp",EDGE,"E3031"),sQuery(id+"F0.wireOp",EDGE,"E3032"),sQuery(id+"F0.wireOp",EDGE,"E3033"),sQuery(id+"F0.wireOp",EDGE,"E3034"),sQuery(id+"F0.wireOp",EDGE,"E3035"),sQuery(id+"F0.wireOp",EDGE,"E3036"),sQuery(id+"F0.wireOp",EDGE,"E3037"),sQuery(id+"F0.wireOp",EDGE,"E3038"),sQuery(id+"F0.wireOp",EDGE,"E3039"),sQuery(id+"F0.wireOp",EDGE,"E3040"),sQuery(id+"F0.wireOp",EDGE,"E3040"),sQuery(id+"F0.wireOp",EDGE,"E3041"),sQuery(id+"F0.wireOp",EDGE,"E3042"),sQuery(id+"F0.wireOp",EDGE,"E3043"),sQuery(id+"F0.wireOp",EDGE,"E3044"),sQuery(id+"F0.wireOp",EDGE,"E3045"),sQuery(id+"F0.wireOp",EDGE,"E3046"),sQuery(id+"F0.wireOp",EDGE,"E3047"),sQuery(id+"F0.wireOp",EDGE,"E3048"),sQuery(id+"F0.wireOp",EDGE,"E3049"),sQuery(id+"F0.wireOp",EDGE,"E3050"),sQuery(id+"F0.wireOp",EDGE,"E3051"),sQuery(id+"F0.wireOp",EDGE,"E3052"),sQuery(id+"F0.wireOp",EDGE,"E3053"),sQuery(id+"F0.wireOp",EDGE,"E3054"),sQuery(id+"F0.wireOp",EDGE,"E3055"),sQuery(id+"F0.wireOp",EDGE,"E3056"),sQuery(id+"F0.wireOp",EDGE,"E3057"),sQuery(id+"F0.wireOp",EDGE,"E3058"),sQuery(id+"F0.wireOp",EDGE,"E3059"),sQuery(id+"F0.wireOp",EDGE,"E3060"),sQuery(id+"F0.wireOp",EDGE,"E3061"),sQuery(id+"F0.wireOp",EDGE,"E3062"),sQuery(id+"F0.wireOp",EDGE,"E3063"),sQuery(id+"F0.wireOp",EDGE,"E3064"),sQuery(id+"F0.wireOp",EDGE,"E3065"),sQuery(id+"F0.wireOp",EDGE,"E3066"),sQuery(id+"F0.wireOp",EDGE,"E3067"),sQuery(id+"F0.wireOp",EDGE,"E3068"),sQuery(id+"F0.wireOp",EDGE,"E3069"),sQuery(id+"F0.wireOp",EDGE,"E3070"),sQuery(id+"F0.wireOp",EDGE,"E3071"),sQuery(id+"F0.wireOp",EDGE,"E3072"),sQuery(id+"F0.wireOp",EDGE,"E3073"),sQuery(id+"F0.wireOp",EDGE,"E3074"),sQuery(id+"F0.wireOp",EDGE,"E3075"),sQuery(id+"F0.wireOp",EDGE,"E3076"),sQuery(id+"F0.wireOp",EDGE,"E3077"),sQuery(id+"F0.wireOp",EDGE,"E3078"),sQuery(id+"F0.wireOp",EDGE,"E3079"),sQuery(id+"F0.wireOp",EDGE,"E3080"),sQuery(id+"F0.wireOp",EDGE,"E3081"),sQuery(id+"F0.wireOp",EDGE,"E3082"),sQuery(id+"F0.wireOp",EDGE,"E3083"),sQuery(id+"F0.wireOp",EDGE,"E3084"),sQuery(id+"F0.wireOp",EDGE,"E3085"),sQuery(id+"F0.wireOp",EDGE,"E3086"),sQuery(id+"F0.wireOp",EDGE,"E3087"),sQuery(id+"F0.wireOp",EDGE,"E3088"),sQuery(id+"F0.wireOp",EDGE,"E3089"),sQuery(id+"F0.wireOp",EDGE,"E3090"),sQuery(id+"F0.wireOp",EDGE,"E3091"),sQuery(id+"F0.wireOp",EDGE,"E3092"),sQuery(id+"F0.wireOp",EDGE,"E3093"),sQuery(id+"F0.wireOp",EDGE,"E3094"),sQuery(id+"F0.wireOp",EDGE,"E3095"),sQuery(id+"F0.wireOp",EDGE,"E3096"),sQuery(id+"F0.wireOp",EDGE,"E3097"),sQuery(id+"F0.wireOp",EDGE,"E3098"),sQuery(id+"F0.wireOp",EDGE,"E3099"),sQuery(id+"F0.wireOp",EDGE,"E3100"),sQuery(id+"F0.wireOp",EDGE,"E3101"),sQuery(id+"F0.wireOp",EDGE,"E3102"),sQuery(id+"F0.wireOp",EDGE,"E3103"),sQuery(id+"F0.wireOp",EDGE,"E3104"),sQuery(id+"F0.wireOp",EDGE,"E3105"),sQuery(id+"F0.wireOp",EDGE,"E3106"),sQuery(id+"F0.wireOp",EDGE,"E3107"),sQuery(id+"F0.wireOp",EDGE,"E3108"),sQuery(id+"F0.wireOp",EDGE,"E3109"),sQuery(id+"F0.wireOp",EDGE,"E3110"),sQuery(id+"F0.wireOp",EDGE,"E3111"),sQuery(id+"F0.wireOp",EDGE,"E3112"),sQuery(id+"F0.wireOp",EDGE,"E3113"),sQuery(id+"F0.wireOp",EDGE,"E3114"),sQuery(id+"F0.wireOp",EDGE,"E3115"),sQuery(id+"F0.wireOp",EDGE,"E3116"),sQuery(id+"F0.wireOp",EDGE,"E3117"),sQuery(id+"F0.wireOp",EDGE,"E3118"),sQuery(id+"F0.wireOp",EDGE,"E3119"),sQuery(id+"F0.wireOp",EDGE,"E3120"),sQuery(id+"F0.wireOp",EDGE,"E3121"),sQuery(id+"F0.wireOp",EDGE,"E3122"),sQuery(id+"F0.wireOp",EDGE,"E3123"),sQuery(id+"F0.wireOp",EDGE,"E3124"),sQuery(id+"F0.wireOp",EDGE,"E3125"),sQuery(id+"F0.wireOp",EDGE,"E3126"),sQuery(id+"F0.wireOp",EDGE,"E3127"),sQuery(id+"F0.wireOp",EDGE,"E3128"),sQuery(id+"F0.wireOp",EDGE,"E3129"),sQuery(id+"F0.wireOp",EDGE,"E3130"),sQuery(id+"F0.wireOp",EDGE,"E3131"),sQuery(id+"F0.wireOp",EDGE,"E3132"),sQuery(id+"F0.wireOp",EDGE,"E3133"),sQuery(id+"F0.wireOp",EDGE,"E3134"),sQuery(id+"F0.wireOp",EDGE,"E3135"),sQuery(id+"F0.wireOp",EDGE,"E3136"),sQuery(id+"F0.wireOp",EDGE,"E3137"),sQuery(id+"F0.wireOp",EDGE,"E3138"),sQuery(id+"F0.wireOp",EDGE,"E3139"),sQuery(id+"F0.wireOp",EDGE,"E3140"),sQuery(id+"F0.wireOp",EDGE,"E3141"),sQuery(id+"F0.wireOp",EDGE,"E3142"),sQuery(id+"F0.wireOp",EDGE,"E3143"),sQuery(id+"F0.wireOp",EDGE,"E3144"),sQuery(id+"F0.wireOp",EDGE,"E3145"),sQuery(id+"F0.wireOp",EDGE,"E3146"),sQuery(id+"F0.wireOp",EDGE,"E3147"),sQuery(id+"F0.wireOp",EDGE,"E3148"),sQuery(id+"F0.wireOp",EDGE,"E3149"),sQuery(id+"F0.wireOp",EDGE,"E3150"),sQuery(id+"F0.wireOp",EDGE,"E3151"),sQuery(id+"F0.wireOp",EDGE,"E3152"),sQuery(id+"F0.wireOp",EDGE,"E3153"),sQuery(id+"F0.wireOp",EDGE,"E3154"),sQuery(id+"F0.wireOp",EDGE,"E3155"),sQuery(id+"F0.wireOp",EDGE,"E3156"),sQuery(id+"F0.wireOp",EDGE,"E3157"),sQuery(id+"F0.wireOp",EDGE,"E3158"),sQuery(id+"F0.wireOp",EDGE,"E3159"),sQuery(id+"F0.wireOp",EDGE,"E3160"),sQuery(id+"F0.wireOp",EDGE,"E3161"),sQuery(id+"F0.wireOp",EDGE,"E3162"),sQuery(id+"F0.wireOp",EDGE,"E3163"),sQuery(id+"F0.wireOp",EDGE,"E3164"),sQuery(id+"F0.wireOp",EDGE,"E3165"),sQuery(id+"F0.wireOp",EDGE,"E3166"),sQuery(id+"F0.wireOp",EDGE,"E3167"),sQuery(id+"F0.wireOp",EDGE,"E3168"),sQuery(id+"F0.wireOp",EDGE,"E3169"),sQuery(id+"F0.wireOp",EDGE,"E3170"),sQuery(id+"F0.wireOp",EDGE,"E3171"),sQuery(id+"F0.wireOp",EDGE,"E3172"),sQuery(id+"F0.wireOp",EDGE,"E3173"),sQuery(id+"F0.wireOp",EDGE,"E3174"),sQuery(id+"F0.wireOp",EDGE,"E3175"),sQuery(id+"F0.wireOp",EDGE,"E3176"),sQuery(id+"F0.wireOp",EDGE,"E3177"),sQuery(id+"F0.wireOp",EDGE,"E3178"),sQuery(id+"F0.wireOp",EDGE,"E3179"),sQuery(id+"F0.wireOp",EDGE,"E3180"),sQuery(id+"F0.wireOp",EDGE,"E3181"),sQuery(id+"F0.wireOp",EDGE,"E3182"),sQuery(id+"F0.wireOp",EDGE,"E3183"),sQuery(id+"F0.wireOp",EDGE,"E3184"),sQuery(id+"F0.wireOp",EDGE,"E3185"),sQuery(id+"F0.wireOp",EDGE,"E3186"),sQuery(id+"F0.wireOp",EDGE,"E3187"),sQuery(id+"F0.wireOp",EDGE,"E3188"),sQuery(id+"F0.wireOp",EDGE,"E3189"),sQuery(id+"F0.wireOp",EDGE,"E3190"),sQuery(id+"F0.wireOp",EDGE,"E3191"),sQuery(id+"F0.wireOp",EDGE,"E3192"),sQuery(id+"F0.wireOp",EDGE,"E3193"),sQuery(id+"F0.wireOp",EDGE,"E3194"),sQuery(id+"F0.wireOp",EDGE,"E3195"),sQuery(id+"F0.wireOp",EDGE,"E3196"),sQuery(id+"F0.wireOp",EDGE,"E3197"),sQuery(id+"F0.wireOp",EDGE,"E3198"),sQuery(id+"F0.wireOp",EDGE,"E3199"),sQuery(id+"F0.wireOp",EDGE,"E3200"),sQuery(id+"F0.wireOp",EDGE,"E3201"),sQuery(id+"F0.wireOp",EDGE,"E3202"),sQuery(id+"F0.wireOp",EDGE,"E3203"),sQuery(id+"F0.wireOp",EDGE,"E3204"),sQuery(id+"F0.wireOp",EDGE,"E3205"),sQuery(id+"F0.wireOp",EDGE,"E3206"),sQuery(id+"F0.wireOp",EDGE,"E3207"),sQuery(id+"F0.wireOp",EDGE,"E3208"),sQuery(id+"F0.wireOp",EDGE,"E3209"),sQuery(id+"F0.wireOp",EDGE,"E3210"),sQuery(id+"F0.wireOp",EDGE,"E3211"),sQuery(id+"F0.wireOp",EDGE,"E3212"),sQuery(id+"F0.wireOp",EDGE,"E3213"),sQuery(id+"F0.wireOp",EDGE,"E3214"),sQuery(id+"F0.wireOp",EDGE,"E3215"),sQuery(id+"F0.wireOp",EDGE,"E3216"),sQuery(id+"F0.wireOp",EDGE,"E3217"),sQuery(id+"F0.wireOp",EDGE,"E3218"),sQuery(id+"F0.wireOp",EDGE,"E3219"),sQuery(id+"F0.wireOp",EDGE,"E3220"),sQuery(id+"F0.wireOp",EDGE,"E3221"),sQuery(id+"F0.wireOp",EDGE,"E3222"),sQuery(id+"F0.wireOp",EDGE,"E3223"),sQuery(id+"F0.wireOp",EDGE,"E3224"),sQuery(id+"F0.wireOp",EDGE,"E3225"),sQuery(id+"F0.wireOp",EDGE,"E3226"),sQuery(id+"F0.wireOp",EDGE,"E3227"),sQuery(id+"F0.wireOp",EDGE,"E3228"),sQuery(id+"F0.wireOp",EDGE,"E3229"),sQuery(id+"F0.wireOp",EDGE,"E3230"),sQuery(id+"F0.wireOp",EDGE,"E3231"),sQuery(id+"F0.wireOp",EDGE,"E3232"),sQuery(id+"F0.wireOp",EDGE,"E3233"),sQuery(id+"F0.wireOp",EDGE,"E3234"),sQuery(id+"F0.wireOp",EDGE,"E3235"),sQuery(id+"F0.wireOp",EDGE,"E3236"),sQuery(id+"F0.wireOp",EDGE,"E3237"),sQuery(id+"F0.wireOp",EDGE,"E3238"),sQuery(id+"F0.wireOp",EDGE,"E3239"),sQuery(id+"F0.wireOp",EDGE,"E3240"),sQuery(id+"F0.wireOp",EDGE,"E3241"),sQuery(id+"F0.wireOp",EDGE,"E3242"),sQuery(id+"F0.wireOp",EDGE,"E3243"),sQuery(id+"F0.wireOp",EDGE,"E3244"),sQuery(id+"F0.wireOp",EDGE,"E3245"),sQuery(id+"F0.wireOp",EDGE,"E3246"),sQuery(id+"F0.wireOp",EDGE,"E3247"),sQuery(id+"F0.wireOp",EDGE,"E3248"),sQuery(id+"F0.wireOp",EDGE,"E3249"),sQuery(id+"F0.wireOp",EDGE,"E3250"),sQuery(id+"F0.wireOp",EDGE,"E3251"),sQuery(id+"F0.wireOp",EDGE,"E3252"),sQuery(id+"F0.wireOp",EDGE,"E3253"),sQuery(id+"F0.wireOp",EDGE,"E3254"),sQuery(id+"F0.wireOp",EDGE,"E3255"),sQuery(id+"F0.wireOp",EDGE,"E3256"),sQuery(id+"F0.wireOp",EDGE,"E3257"),sQuery(id+"F0.wireOp",EDGE,"E3258"),sQuery(id+"F0.wireOp",EDGE,"E3259"),sQuery(id+"F0.wireOp",EDGE,"E3260"),sQuery(id+"F0.wireOp",EDGE,"E3261"),sQuery(id+"F0.wireOp",EDGE,"E3262"),sQuery(id+"F0.wireOp",EDGE,"E3263"),sQuery(id+"F0.wireOp",EDGE,"E3264"),sQuery(id+"F0.wireOp",EDGE,"E3265"),sQuery(id+"F0.wireOp",EDGE,"E3266"),sQuery(id+"F0.wireOp",EDGE,"E3267"),sQuery(id+"F0.wireOp",EDGE,"E3268"),sQuery(id+"F0.wireOp",EDGE,"E3269"),sQuery(id+"F0.wireOp",EDGE,"E3270"),sQuery(id+"F0.wireOp",EDGE,"E3271"),sQuery(id+"F0.wireOp",EDGE,"E3272"),sQuery(id+"F0.wireOp",EDGE,"E3273"),sQuery(id+"F0.wireOp",EDGE,"E3274"),sQuery(id+"F0.wireOp",EDGE,"E3275"),sQuery(id+"F0.wireOp",EDGE,"E3276"),sQuery(id+"F0.wireOp",EDGE,"E3277"),sQuery(id+"F0.wireOp",EDGE,"E3278"),sQuery(id+"F0.wireOp",EDGE,"E3279"),sQuery(id+"F0.wireOp",EDGE,"E3280"),sQuery(id+"F0.wireOp",EDGE,"E3281"),sQuery(id+"F0.wireOp",EDGE,"E3282"),sQuery(id+"F0.wireOp",EDGE,"E3283"),sQuery(id+"F0.wireOp",EDGE,"E3284"),sQuery(id+"F0.wireOp",EDGE,"E3285"),sQuery(id+"F0.wireOp",EDGE,"E3286"),sQuery(id+"F0.wireOp",EDGE,"E3287"),sQuery(id+"F0.wireOp",EDGE,"E3288"),sQuery(id+"F0.wireOp",EDGE,"E3289"),sQuery(id+"F0.wireOp",EDGE,"E3290"),sQuery(id+"F0.wireOp",EDGE,"E3291"),sQuery(id+"F0.wireOp",EDGE,"E3292"),sQuery(id+"F0.wireOp",EDGE,"E3293"),sQuery(id+"F0.wireOp",EDGE,"E3294"),sQuery(id+"F0.wireOp",EDGE,"E3295"),sQuery(id+"F0.wireOp",EDGE,"E3296"),sQuery(id+"F0.wireOp",EDGE,"E3297"),sQuery(id+"F0.wireOp",EDGE,"E3298"),sQuery(id+"F0.wireOp",EDGE,"E3299"),sQuery(id+"F0.wireOp",EDGE,"E3300"),sQuery(id+"F0.wireOp",EDGE,"E3301"),sQuery(id+"F0.wireOp",EDGE,"E3302"),sQuery(id+"F0.wireOp",EDGE,"E3303"),sQuery(id+"F0.wireOp",EDGE,"E3304"),sQuery(id+"F0.wireOp",EDGE,"E3305"),sQuery(id+"F0.wireOp",EDGE,"E3306"),sQuery(id+"F0.wireOp",EDGE,"E3307"),sQuery(id+"F0.wireOp",EDGE,"E3308"),sQuery(id+"F0.wireOp",EDGE,"E3309"),sQuery(id+"F0.wireOp",EDGE,"E3310"),sQuery(id+"F0.wireOp",EDGE,"E3311"),sQuery(id+"F0.wireOp",EDGE,"E3312"),sQuery(id+"F0.wireOp",EDGE,"E3313"),sQuery(id+"F0.wireOp",EDGE,"E3314"),sQuery(id+"F0.wireOp",EDGE,"E3315"),sQuery(id+"F0.wireOp",EDGE,"E3316"),sQuery(id+"F0.wireOp",EDGE,"E3317"),sQuery(id+"F0.wireOp",EDGE,"E3318"),sQuery(id+"F0.wireOp",EDGE,"E3319"),sQuery(id+"F0.wireOp",EDGE,"E3320"),sQuery(id+"F0.wireOp",EDGE,"E3321"),sQuery(id+"F0.wireOp",EDGE,"E3322"),sQuery(id+"F0.wireOp",EDGE,"E3323"),sQuery(id+"F0.wireOp",EDGE,"E3324"),sQuery(id+"F0.wireOp",EDGE,"E3325"),sQuery(id+"F0.wireOp",EDGE,"E3326"),sQuery(id+"F0.wireOp",EDGE,"E3327"),sQuery(id+"F0.wireOp",EDGE,"E3328"),sQuery(id+"F0.wireOp",EDGE,"E3329"),sQuery(id+"F0.wireOp",EDGE,"E3330"),sQuery(id+"F0.wireOp",EDGE,"E3331"),sQuery(id+"F0.wireOp",EDGE,"E3332"),sQuery(id+"F0.wireOp",EDGE,"E3333"),sQuery(id+"F0.wireOp",EDGE,"E3334"),sQuery(id+"F0.wireOp",EDGE,"E3335"),sQuery(id+"F0.wireOp",EDGE,"E3336"),sQuery(id+"F0.wireOp",EDGE,"E3337"),sQuery(id+"F0.wireOp",EDGE,"E3338"),sQuery(id+"F0.wireOp",EDGE,"E3339"),sQuery(id+"F0.wireOp",EDGE,"E3340"),sQuery(id+"F0.wireOp",EDGE,"E3341"),sQuery(id+"F0.wireOp",EDGE,"E3342"),sQuery(id+"F0.wireOp",EDGE,"E3343"),sQuery(id+"F0.wireOp",EDGE,"E3344"),sQuery(id+"F0.wireOp",EDGE,"E3345"),sQuery(id+"F0.wireOp",EDGE,"E3346"),sQuery(id+"F0.wireOp",EDGE,"E3347"),sQuery(id+"F0.wireOp",EDGE,"E3348"),sQuery(id+"F0.wireOp",EDGE,"E3349"),sQuery(id+"F0.wireOp",EDGE,"E3350"),sQuery(id+"F0.wireOp",EDGE,"E3351"),sQuery(id+"F0.wireOp",EDGE,"E3352"),sQuery(id+"F0.wireOp",EDGE,"E3353"),sQuery(id+"F0.wireOp",EDGE,"E3354"),sQuery(id+"F0.wireOp",EDGE,"E3355"),sQuery(id+"F0.wireOp",EDGE,"E3356"),sQuery(id+"F0.wireOp",EDGE,"E3357"),sQuery(id+"F0.wireOp",EDGE,"E3358"),sQuery(id+"F0.wireOp",EDGE,"E3359"),sQuery(id+"F0.wireOp",EDGE,"E3360"),sQuery(id+"F0.wireOp",EDGE,"E3361"),sQuery(id+"F0.wireOp",EDGE,"E3362"),sQuery(id+"F0.wireOp",EDGE,"E3363"),sQuery(id+"F0.wireOp",EDGE,"E3364"),sQuery(id+"F0.wireOp",EDGE,"E3365"),sQuery(id+"F0.wireOp",EDGE,"E3366"),sQuery(id+"F0.wireOp",EDGE,"E3367"),sQuery(id+"F0.wireOp",EDGE,"E3368"),sQuery(id+"F0.wireOp",EDGE,"E3369"),sQuery(id+"F0.wireOp",EDGE,"E3370"),sQuery(id+"F0.wireOp",EDGE,"E3371"),sQuery(id+"F0.wireOp",EDGE,"E3372"),sQuery(id+"F0.wireOp",EDGE,"E3373"),sQuery(id+"F0.wireOp",EDGE,"E3374"),sQuery(id+"F0.wireOp",EDGE,"E3375"),sQuery(id+"F0.wireOp",EDGE,"E3376"),sQuery(id+"F0.wireOp",EDGE,"E3377"),sQuery(id+"F0.wireOp",EDGE,"E3378"),sQuery(id+"F0.wireOp",EDGE,"E3379"),sQuery(id+"F0.wireOp",EDGE,"E3380"),sQuery(id+"F0.wireOp",EDGE,"E3381"),sQuery(id+"F0.wireOp",EDGE,"E3382"),sQuery(id+"F0.wireOp",EDGE,"E3383"),sQuery(id+"F0.wireOp",EDGE,"E3384"),sQuery(id+"F0.wireOp",EDGE,"E3385"),sQuery(id+"F0.wireOp",EDGE,"E3386"),sQuery(id+"F0.wireOp",EDGE,"E3387"),sQuery(id+"F0.wireOp",EDGE,"E3388"),sQuery(id+"F0.wireOp",EDGE,"E3389"),sQuery(id+"F0.wireOp",EDGE,"E3390"),sQuery(id+"F0.wireOp",EDGE,"E3391"),sQuery(id+"F0.wireOp",EDGE,"E3392"),sQuery(id+"F0.wireOp",EDGE,"E3393"),sQuery(id+"F0.wireOp",EDGE,"E3394"),sQuery(id+"F0.wireOp",EDGE,"E3395"),sQuery(id+"F0.wireOp",EDGE,"E3396"),sQuery(id+"F0.wireOp",EDGE,"E3397"),sQuery(id+"F0.wireOp",EDGE,"E3398"),sQuery(id+"F0.wireOp",EDGE,"E3399"),sQuery(id+"F0.wireOp",EDGE,"E3400"),sQuery(id+"F0.wireOp",EDGE,"E3401"),sQuery(id+"F0.wireOp",EDGE,"E3402"),sQuery(id+"F0.wireOp",EDGE,"E3403"),sQuery(id+"F0.wireOp",EDGE,"E3404"),sQuery(id+"F0.wireOp",EDGE,"E3405"),sQuery(id+"F0.wireOp",EDGE,"E3406"),sQuery(id+"F0.wireOp",EDGE,"E3407"),sQuery(id+"F0.wireOp",EDGE,"E3408"),sQuery(id+"F0.wireOp",EDGE,"E3409"),sQuery(id+"F0.wireOp",EDGE,"E3410"),sQuery(id+"F0.wireOp",EDGE,"E3411"),sQuery(id+"F0.wireOp",EDGE,"E3412"),sQuery(id+"F0.wireOp",EDGE,"E3413"),sQuery(id+"F0.wireOp",EDGE,"E3414"),sQuery(id+"F0.wireOp",EDGE,"E3415"),sQuery(id+"F0.wireOp",EDGE,"E3416"),sQuery(id+"F0.wireOp",EDGE,"E3417"),sQuery(id+"F0.wireOp",EDGE,"E3418"),sQuery(id+"F0.wireOp",EDGE,"E3419"),sQuery(id+"F0.wireOp",EDGE,"E3420"),sQuery(id+"F0.wireOp",EDGE,"E3421"),sQuery(id+"F0.wireOp",EDGE,"E3422"),sQuery(id+"F0.wireOp",EDGE,"E3423"),sQuery(id+"F0.wireOp",EDGE,"E3424"),sQuery(id+"F0.wireOp",EDGE,"E3425"),sQuery(id+"F0.wireOp",EDGE,"E3426"),sQuery(id+"F0.wireOp",EDGE,"E3427"),sQuery(id+"F0.wireOp",EDGE,"E3428"),sQuery(id+"F0.wireOp",EDGE,"E3429"),sQuery(id+"F0.wireOp",EDGE,"E3430"),sQuery(id+"F0.wireOp",EDGE,"E3431"),sQuery(id+"F0.wireOp",EDGE,"E3432"),sQuery(id+"F0.wireOp",EDGE,"E3433"),sQuery(id+"F0.wireOp",EDGE,"E3434"),sQuery(id+"F0.wireOp",EDGE,"E3435"),sQuery(id+"F0.wireOp",EDGE,"E3436"),sQuery(id+"F0.wireOp",EDGE,"E3437"),sQuery(id+"F0.wireOp",EDGE,"E3438"),sQuery(id+"F0.wireOp",EDGE,"E3439"),sQuery(id+"F0.wireOp",EDGE,"E3440"),sQuery(id+"F0.wireOp",EDGE,"E3441"),sQuery(id+"F0.wireOp",EDGE,"E3442"),sQuery(id+"F0.wireOp",EDGE,"E3443"),sQuery(id+"F0.wireOp",EDGE,"E3444"),sQuery(id+"F0.wireOp",EDGE,"E3445"),sQuery(id+"F0.wireOp",EDGE,"E3446"),sQuery(id+"F0.wireOp",EDGE,"E3447"),sQuery(id+"F0.wireOp",EDGE,"E3448"),sQuery(id+"F0.wireOp",EDGE,"E3449"),sQuery(id+"F0.wireOp",EDGE,"E3450"),sQuery(id+"F0.wireOp",EDGE,"E3451"),sQuery(id+"F0.wireOp",EDGE,"E3452"),sQuery(id+"F0.wireOp",EDGE,"E3453"),sQuery(id+"F0.wireOp",EDGE,"E3454"),sQuery(id+"F0.wireOp",EDGE,"E3455"),sQuery(id+"F0.wireOp",EDGE,"E3456"),sQuery(id+"F0.wireOp",EDGE,"E3457"),sQuery(id+"F0.wireOp",EDGE,"E3458"),sQuery(id+"F0.wireOp",EDGE,"E3459"),sQuery(id+"F0.wireOp",EDGE,"E3460"),sQuery(id+"F0.wireOp",EDGE,"E3461"),sQuery(id+"F0.wireOp",EDGE,"E3462"),sQuery(id+"F0.wireOp",EDGE,"E3463"),sQuery(id+"F0.wireOp",EDGE,"E3464"),sQuery(id+"F0.wireOp",EDGE,"E3465"),sQuery(id+"F0.wireOp",EDGE,"E3466"),sQuery(id+"F0.wireOp",EDGE,"E3467"),sQuery(id+"F0.wireOp",EDGE,"E3468"),sQuery(id+"F0.wireOp",EDGE,"E3469"),sQuery(id+"F0.wireOp",EDGE,"E3470"),sQuery(id+"F0.wireOp",EDGE,"E3471"),sQuery(id+"F0.wireOp",EDGE,"E3472"),sQuery(id+"F0.wireOp",EDGE,"E3473"),sQuery(id+"F0.wireOp",EDGE,"E3474"),sQuery(id+"F0.wireOp",EDGE,"E3475"),sQuery(id+"F0.wireOp",EDGE,"E3476"),sQuery(id+"F0.wireOp",EDGE,"E3477"),sQuery(id+"F0.wireOp",EDGE,"E3478"),sQuery(id+"F0.wireOp",EDGE,"E3479"),sQuery(id+"F0.wireOp",EDGE,"E3480"),sQuery(id+"F0.wireOp",EDGE,"E3481"),sQuery(id+"F0.wireOp",EDGE,"E3482"),sQuery(id+"F0.wireOp",EDGE,"E3483"),sQuery(id+"F0.wireOp",EDGE,"E3484"),sQuery(id+"F0.wireOp",EDGE,"E3485"),sQuery(id+"F0.wireOp",EDGE,"E3486"),sQuery(id+"F0.wireOp",EDGE,"E3487"),sQuery(id+"F0.wireOp",EDGE,"E3488"),sQuery(id+"F0.wireOp",EDGE,"E3489"),sQuery(id+"F0.wireOp",EDGE,"E3490"),sQuery(id+"F0.wireOp",EDGE,"E3491"),sQuery(id+"F0.wireOp",EDGE,"E3492"),sQuery(id+"F0.wireOp",EDGE,"E3493"),sQuery(id+"F0.wireOp",EDGE,"E3494"),sQuery(id+"F0.wireOp",EDGE,"E3495"),sQuery(id+"F0.wireOp",EDGE,"E3496"),sQuery(id+"F0.wireOp",EDGE,"E3497"),sQuery(id+"F0.wireOp",EDGE,"E3498"),sQuery(id+"F0.wireOp",EDGE,"E3499"),sQuery(id+"F0.wireOp",EDGE,"E3500"),sQuery(id+"F0.wireOp",EDGE,"E3501"),sQuery(id+"F0.wireOp",EDGE,"E3502"),sQuery(id+"F0.wireOp",EDGE,"E3503"),sQuery(id+"F0.wireOp",EDGE,"E3504"),sQuery(id+"F0.wireOp",EDGE,"E3505"),sQuery(id+"F0.wireOp",EDGE,"E3506"),sQuery(id+"F0.wireOp",EDGE,"E3507"),sQuery(id+"F0.wireOp",EDGE,"E3508"),sQuery(id+"F0.wireOp",EDGE,"E3509"),sQuery(id+"F0.wireOp",EDGE,"E3510"),sQuery(id+"F0.wireOp",EDGE,"E3511"),sQuery(id+"F0.wireOp",EDGE,"E3512"),sQuery(id+"F0.wireOp",EDGE,"E3513"),sQuery(id+"F0.wireOp",EDGE,"E3514"),sQuery(id+"F0.wireOp",EDGE,"E3515"),sQuery(id+"F0.wireOp",EDGE,"E3516"),sQuery(id+"F0.wireOp",EDGE,"E3517"),sQuery(id+"F0.wireOp",EDGE,"E3518"),sQuery(id+"F0.wireOp",EDGE,"E3519"),sQuery(id+"F0.wireOp",EDGE,"E3520"),sQuery(id+"F0.wireOp",EDGE,"E3521"),sQuery(id+"F0.wireOp",EDGE,"E3522"),sQuery(id+"F0.wireOp",EDGE,"E3523"),sQuery(id+"F0.wireOp",EDGE,"E3524"),sQuery(id+"F0.wireOp",EDGE,"E3525"),sQuery(id+"F0.wireOp",EDGE,"E3526"),sQuery(id+"F0.wireOp",EDGE,"E3527"),sQuery(id+"F0.wireOp",EDGE,"E3528"),sQuery(id+"F0.wireOp",EDGE,"E3529"),sQuery(id+"F0.wireOp",EDGE,"E3530"),sQuery(id+"F0.wireOp",EDGE,"E3531"),sQuery(id+"F0.wireOp",EDGE,"E3532"),sQuery(id+"F0.wireOp",EDGE,"E3533"),sQuery(id+"F0.wireOp",EDGE,"E3534"),sQuery(id+"F0.wireOp",EDGE,"E3535"),sQuery(id+"F0.wireOp",EDGE,"E3536"),sQuery(id+"F0.wireOp",EDGE,"E3537"),sQuery(id+"F0.wireOp",EDGE,"E3538"),sQuery(id+"F0.wireOp",EDGE,"E3539"),sQuery(id+"F0.wireOp",EDGE,"E3540"),sQuery(id+"F0.wireOp",EDGE,"E3541"),sQuery(id+"F0.wireOp",EDGE,"E3542"),sQuery(id+"F0.wireOp",EDGE,"E3543"),sQuery(id+"F0.wireOp",EDGE,"E3544"),sQuery(id+"F0.wireOp",EDGE,"E3545"),sQuery(id+"F0.wireOp",EDGE,"E3546"),sQuery(id+"F0.wireOp",EDGE,"E3547"),sQuery(id+"F0.wireOp",EDGE,"E3548"),sQuery(id+"F0.wireOp",EDGE,"E3549")])],"isStart":false});
            var sketch = newSketch(context, id + "F2", { "sketchPlane" : qUnion([Q0])});
            skCircle(sketch, "E3550", {"center": v(0, 0) * mm, "radius": 1.5 * mm});
            skSolve(sketch);
        }
        {
            var Q0;
            Q0 = qSketchRegion(id + "F2", true);
            extrude(context, id + "F3", {"entities" : qUnion([Q0]), "operationType" : NewBodyOperationType.REMOVE, "oppositeDirection" : true, "depth" : 25 * mm, "offsetDistance" : 25 * mm});
        }
    });
